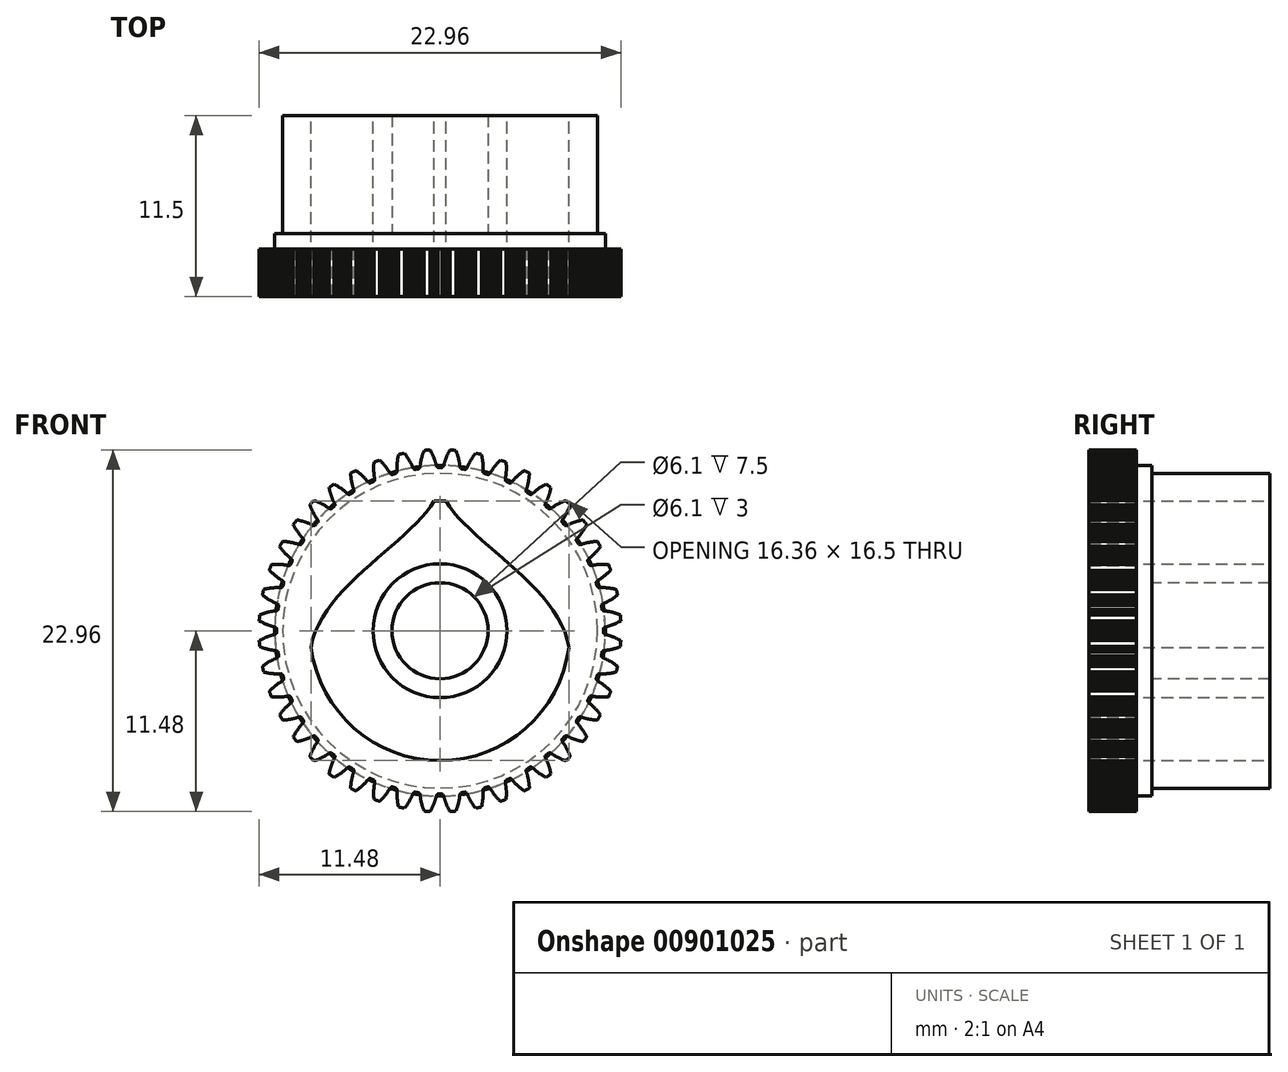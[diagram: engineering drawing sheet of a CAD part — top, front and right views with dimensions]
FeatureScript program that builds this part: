
annotation { "Feature Type Name" : "Feature", "Feature Type Description" : "" }
export const myFeature = defineFeature(function(context is Context, id is Id, definition is map)
    precondition{}
    {
        {
            var Q0;
            Q0=qCreatedBy(makeId("Front.planeOp"),FACE);
            var sketch = newSketch(context, id + "F0", { "sketchPlane" : qUnion([Q0])});
            skLineSegment(sketch, "E0", {"start": v(10.38, 0) * mm, "end": v(10.37, 0.02) * mm});
            skLineSegment(sketch, "E1", {"start": v(10.37, 0.02) * mm, "end": v(10.37, 0.05) * mm});
            skLineSegment(sketch, "E2", {"start": v(10.37, 0.05) * mm, "end": v(10.37, 0.07) * mm});
            skLineSegment(sketch, "E3", {"start": v(10.37, 0.07) * mm, "end": v(10.37, 0.1) * mm});
            skLineSegment(sketch, "E4", {"start": v(10.37, 0.1) * mm, "end": v(10.37, 0.12) * mm});
            skLineSegment(sketch, "E5", {"start": v(10.37, 0.12) * mm, "end": v(10.37, 0.12) * mm});
            skLineSegment(sketch, "E6", {"start": v(10.37, 0.12) * mm, "end": v(10.38, 0.13) * mm});
            skLineSegment(sketch, "E7", {"start": v(10.38, 0.13) * mm, "end": v(10.38, 0.14) * mm});
            skLineSegment(sketch, "E8", {"start": v(10.38, 0.14) * mm, "end": v(10.38, 0.15) * mm});
            skLineSegment(sketch, "E9", {"start": v(10.38, 0.15) * mm, "end": v(10.39, 0.16) * mm});
            skLineSegment(sketch, "E10", {"start": v(10.39, 0.16) * mm, "end": v(10.4, 0.16) * mm});
            skLineSegment(sketch, "E11", {"start": v(10.4, 0.16) * mm, "end": v(10.4, 0.17) * mm});
            skLineSegment(sketch, "E12", {"start": v(10.4, 0.17) * mm, "end": v(10.4, 0.18) * mm});
            skLineSegment(sketch, "E13", {"start": v(10.4, 0.18) * mm, "end": v(10.41, 0.19) * mm});
            skLineSegment(sketch, "E14", {"start": v(10.41, 0.19) * mm, "end": v(10.42, 0.2) * mm});
            skLineSegment(sketch, "E15", {"start": v(10.42, 0.2) * mm, "end": v(10.43, 0.2) * mm});
            skLineSegment(sketch, "E16", {"start": v(10.43, 0.2) * mm, "end": v(10.44, 0.2) * mm});
            skLineSegment(sketch, "E17", {"start": v(10.44, 0.2) * mm, "end": v(10.46, 0.21) * mm});
            skLineSegment(sketch, "E18", {"start": v(10.46, 0.21) * mm, "end": v(10.47, 0.22) * mm});
            skLineSegment(sketch, "E19", {"start": v(10.47, 0.22) * mm, "end": v(10.48, 0.23) * mm});
            skLineSegment(sketch, "E20", {"start": v(10.48, 0.23) * mm, "end": v(10.5, 0.23) * mm});
            skLineSegment(sketch, "E21", {"start": v(10.5, 0.23) * mm, "end": v(10.51, 0.24) * mm});
            skLineSegment(sketch, "E22", {"start": v(10.51, 0.24) * mm, "end": v(10.53, 0.24) * mm});
            skLineSegment(sketch, "E23", {"start": v(10.53, 0.24) * mm, "end": v(10.55, 0.25) * mm});
            skLineSegment(sketch, "E24", {"start": v(10.55, 0.25) * mm, "end": v(10.57, 0.25) * mm});
            skLineSegment(sketch, "E25", {"start": v(10.57, 0.25) * mm, "end": v(10.61, 0.26) * mm});
            skLineSegment(sketch, "E26", {"start": v(10.61, 0.26) * mm, "end": v(10.66, 0.28) * mm});
            skLineSegment(sketch, "E27", {"start": v(10.66, 0.28) * mm, "end": v(10.7, 0.3) * mm});
            skLineSegment(sketch, "E28", {"start": v(10.7, 0.3) * mm, "end": v(10.75, 0.3) * mm});
            skLineSegment(sketch, "E29", {"start": v(10.75, 0.3) * mm, "end": v(10.8, 0.32) * mm});
            skLineSegment(sketch, "E30", {"start": v(10.8, 0.32) * mm, "end": v(10.84, 0.34) * mm});
            skLineSegment(sketch, "E31", {"start": v(10.84, 0.34) * mm, "end": v(10.89, 0.35) * mm});
            skLineSegment(sketch, "E32", {"start": v(10.89, 0.35) * mm, "end": v(10.94, 0.37) * mm});
            skLineSegment(sketch, "E33", {"start": v(10.94, 0.37) * mm, "end": v(10.98, 0.39) * mm});
            skLineSegment(sketch, "E34", {"start": v(10.98, 0.39) * mm, "end": v(11.03, 0.4) * mm});
            skLineSegment(sketch, "E35", {"start": v(11.03, 0.4) * mm, "end": v(11.07, 0.43) * mm});
            skLineSegment(sketch, "E36", {"start": v(11.07, 0.43) * mm, "end": v(11.12, 0.45) * mm});
            skLineSegment(sketch, "E37", {"start": v(11.12, 0.45) * mm, "end": v(11.16, 0.47) * mm});
            skLineSegment(sketch, "E38", {"start": v(11.16, 0.47) * mm, "end": v(11.21, 0.49) * mm});
            skLineSegment(sketch, "E39", {"start": v(11.21, 0.49) * mm, "end": v(11.26, 0.51) * mm});
            skLineSegment(sketch, "E40", {"start": v(11.26, 0.51) * mm, "end": v(11.3, 0.53) * mm});
            skLineSegment(sketch, "E41", {"start": v(11.3, 0.53) * mm, "end": v(11.35, 0.56) * mm});
            skLineSegment(sketch, "E42", {"start": v(11.35, 0.56) * mm, "end": v(11.4, 0.58) * mm});
            skLineSegment(sketch, "E43", {"start": v(11.4, 0.58) * mm, "end": v(11.44, 0.6) * mm});
            skLineSegment(sketch, "E44", {"start": v(11.44, 0.6) * mm, "end": v(11.48, 0.63) * mm});
            skLineSegment(sketch, "E45", {"start": v(11.48, 0.63) * mm, "end": v(11.48, 0.67) * mm});
            skLineSegment(sketch, "E46", {"start": v(11.48, 0.67) * mm, "end": v(11.48, 0.7) * mm});
            skLineSegment(sketch, "E47", {"start": v(11.48, 0.7) * mm, "end": v(11.48, 0.74) * mm});
            skLineSegment(sketch, "E48", {"start": v(11.48, 0.74) * mm, "end": v(11.47, 0.78) * mm});
            skLineSegment(sketch, "E49", {"start": v(11.47, 0.78) * mm, "end": v(11.47, 0.82) * mm});
            skLineSegment(sketch, "E50.MirrorCS", {"start": v(10.37, -0.12) * mm, "end": v(10.37, -0.12) * mm});
            skLineSegment(sketch, "E51.MirrorCS", {"start": v(10.37, -0.12) * mm, "end": v(10.38, -0.13) * mm});
            skLineSegment(sketch, "E52.MirrorCS", {"start": v(10.38, -0.13) * mm, "end": v(10.38, -0.14) * mm});
            skLineSegment(sketch, "E53.MirrorCS", {"start": v(10.38, -0.14) * mm, "end": v(10.38, -0.15) * mm});
            skLineSegment(sketch, "E54.MirrorCS", {"start": v(10.46, -0.21) * mm, "end": v(10.47, -0.22) * mm});
            skLineSegment(sketch, "E55.MirrorCS", {"start": v(10.38, -0.15) * mm, "end": v(10.39, -0.16) * mm});
            skLineSegment(sketch, "E56.MirrorCS", {"start": v(10.44, -0.2) * mm, "end": v(10.46, -0.21) * mm});
            skLineSegment(sketch, "E57.MirrorCS", {"start": v(10.57, -0.25) * mm, "end": v(10.61, -0.26) * mm});
            skLineSegment(sketch, "E58.MirrorCS", {"start": v(10.39, -0.16) * mm, "end": v(10.4, -0.16) * mm});
            skLineSegment(sketch, "E59.MirrorCS", {"start": v(10.55, -0.25) * mm, "end": v(10.57, -0.25) * mm});
            skLineSegment(sketch, "E60.MirrorCS", {"start": v(10.43, -0.2) * mm, "end": v(10.44, -0.2) * mm});
            skLineSegment(sketch, "E61.MirrorCS", {"start": v(10.4, -0.16) * mm, "end": v(10.4, -0.17) * mm});
            skLineSegment(sketch, "E62.MirrorCS", {"start": v(10.53, -0.24) * mm, "end": v(10.55, -0.25) * mm});
            skLineSegment(sketch, "E63.MirrorCS", {"start": v(11.07, -0.43) * mm, "end": v(11.12, -0.45) * mm});
            skLineSegment(sketch, "E64.MirrorCS", {"start": v(10.51, -0.24) * mm, "end": v(10.53, -0.24) * mm});
            skLineSegment(sketch, "E65.MirrorCS", {"start": v(10.4, -0.17) * mm, "end": v(10.4, -0.18) * mm});
            skLineSegment(sketch, "E66.MirrorCS", {"start": v(10.7, -0.3) * mm, "end": v(10.75, -0.3) * mm});
            skLineSegment(sketch, "E67.MirrorCS", {"start": v(10.37, -0.02) * mm, "end": v(10.37, -0.05) * mm});
            skLineSegment(sketch, "E68.MirrorCS", {"start": v(10.37, -0.05) * mm, "end": v(10.37, -0.07) * mm});
            skLineSegment(sketch, "E69.MirrorCS", {"start": v(10.42, -0.2) * mm, "end": v(10.43, -0.2) * mm});
            skLineSegment(sketch, "E70.MirrorCS", {"start": v(11.03, -0.4) * mm, "end": v(11.07, -0.43) * mm});
            skLineSegment(sketch, "E71.MirrorCS", {"start": v(10.5, -0.23) * mm, "end": v(10.51, -0.24) * mm});
            skLineSegment(sketch, "E72.MirrorCS", {"start": v(10.66, -0.28) * mm, "end": v(10.7, -0.3) * mm});
            skLineSegment(sketch, "E73.MirrorCS", {"start": v(10.4, -0.18) * mm, "end": v(10.41, -0.19) * mm});
            skLineSegment(sketch, "E74.MirrorCS", {"start": v(10.98, -0.39) * mm, "end": v(11.03, -0.4) * mm});
            skLineSegment(sketch, "E75.MirrorCS", {"start": v(10.8, -0.32) * mm, "end": v(10.84, -0.34) * mm});
            skLineSegment(sketch, "E76.MirrorCS", {"start": v(10.84, -0.34) * mm, "end": v(10.89, -0.35) * mm});
            skLineSegment(sketch, "E77.MirrorCS", {"start": v(10.48, -0.23) * mm, "end": v(10.5, -0.23) * mm});
            skLineSegment(sketch, "E78.MirrorCS", {"start": v(10.37, -0.07) * mm, "end": v(10.37, -0.1) * mm});
            skLineSegment(sketch, "E79.MirrorCS", {"start": v(10.47, -0.22) * mm, "end": v(10.48, -0.23) * mm});
            skLineSegment(sketch, "E80.MirrorCS", {"start": v(10.89, -0.35) * mm, "end": v(10.94, -0.37) * mm});
            skLineSegment(sketch, "E81.MirrorCS", {"start": v(10.38, 0) * mm, "end": v(10.37, -0.02) * mm});
            skLineSegment(sketch, "E82.MirrorCS", {"start": v(10.75, -0.3) * mm, "end": v(10.8, -0.32) * mm});
            skLineSegment(sketch, "E83.MirrorCS", {"start": v(10.61, -0.26) * mm, "end": v(10.66, -0.28) * mm});
            skLineSegment(sketch, "E84.MirrorCS", {"start": v(10.41, -0.19) * mm, "end": v(10.42, -0.2) * mm});
            skLineSegment(sketch, "E85.MirrorCS", {"start": v(10.37, -0.1) * mm, "end": v(10.37, -0.12) * mm});
            skLineSegment(sketch, "E86.MirrorCS", {"start": v(10.94, -0.37) * mm, "end": v(10.98, -0.39) * mm});
            skLineSegment(sketch, "E87.MirrorCS", {"start": v(11.21, -0.49) * mm, "end": v(11.26, -0.51) * mm});
            skLineSegment(sketch, "E88.MirrorCS", {"start": v(11.44, -0.6) * mm, "end": v(11.48, -0.63) * mm});
            skLineSegment(sketch, "E89.MirrorCS", {"start": v(11.16, -0.47) * mm, "end": v(11.21, -0.49) * mm});
            skLineSegment(sketch, "E90.MirrorCS", {"start": v(11.26, -0.51) * mm, "end": v(11.3, -0.53) * mm});
            skLineSegment(sketch, "E91.MirrorCS", {"start": v(11.4, -0.58) * mm, "end": v(11.44, -0.6) * mm});
            skLineSegment(sketch, "E92.MirrorCS", {"start": v(11.12, -0.45) * mm, "end": v(11.16, -0.47) * mm});
            skLineSegment(sketch, "E93.MirrorCS", {"start": v(11.3, -0.53) * mm, "end": v(11.35, -0.56) * mm});
            skLineSegment(sketch, "E94.MirrorCS", {"start": v(11.48, -0.67) * mm, "end": v(11.48, -0.7) * mm});
            skLineSegment(sketch, "E95.MirrorCS", {"start": v(11.48, -0.7) * mm, "end": v(11.48, -0.74) * mm});
            skLineSegment(sketch, "E96.MirrorCS", {"start": v(11.47, -0.78) * mm, "end": v(11.47, -0.82) * mm});
            skLineSegment(sketch, "E97.MirrorCS", {"start": v(11.48, -0.74) * mm, "end": v(11.47, -0.78) * mm});
            skLineSegment(sketch, "E98.MirrorCS", {"start": v(11.35, -0.56) * mm, "end": v(11.4, -0.58) * mm});
            skLineSegment(sketch, "E99.MirrorCS", {"start": v(11.48, -0.63) * mm, "end": v(11.48, -0.67) * mm});
            skLineSegment(sketch, "E100.1.0", {"start": v(11.46, 0.97) * mm, "end": v(11.46, 0.94) * mm});
            skLineSegment(sketch, "E100.1.1", {"start": v(11.26, 2.33) * mm, "end": v(11.25, 2.37) * mm});
            skLineSegment(sketch, "E100.1.2", {"start": v(11.15, 2.17) * mm, "end": v(11.2, 2.2) * mm});
            skLineSegment(sketch, "E100.1.3", {"start": v(11.25, 2.4) * mm, "end": v(11.24, 2.44) * mm});
            skLineSegment(sketch, "E100.1.4", {"start": v(11.02, 1.15) * mm, "end": v(11.07, 1.14) * mm});
            skLineSegment(sketch, "E100.1.5", {"start": v(11.46, 0.9) * mm, "end": v(11.47, 0.86) * mm});
            skLineSegment(sketch, "E100.1.6", {"start": v(11.27, 2.3) * mm, "end": v(11.26, 2.33) * mm});
            skLineSegment(sketch, "E100.1.7", {"start": v(11.26, 1.08) * mm, "end": v(11.31, 1.06) * mm});
            skLineSegment(sketch, "E100.1.8", {"start": v(11.25, 2.37) * mm, "end": v(11.25, 2.4) * mm});
            skLineSegment(sketch, "E100.1.9", {"start": v(11.31, 1.06) * mm, "end": v(11.36, 1.05) * mm});
            skLineSegment(sketch, "E100.1.10", {"start": v(11.47, 0.86) * mm, "end": v(11.47, 0.82) * mm});
            skLineSegment(sketch, "E100.1.11", {"start": v(11.36, 1.05) * mm, "end": v(11.4, 1.03) * mm});
            skLineSegment(sketch, "E100.1.12", {"start": v(11.21, 1.1) * mm, "end": v(11.26, 1.08) * mm});
            skLineSegment(sketch, "E100.1.13", {"start": v(11.24, 2.23) * mm, "end": v(11.28, 2.26) * mm});
            skLineSegment(sketch, "E100.1.14", {"start": v(11.46, 1.01) * mm, "end": v(11.46, 0.97) * mm});
            skLineSegment(sketch, "E100.1.15", {"start": v(11.07, 1.14) * mm, "end": v(11.12, 1.13) * mm});
            skLineSegment(sketch, "E100.1.16", {"start": v(11.46, 0.94) * mm, "end": v(11.46, 0.9) * mm});
            skLineSegment(sketch, "E100.1.17", {"start": v(11.28, 2.26) * mm, "end": v(11.27, 2.3) * mm});
            skLineSegment(sketch, "E100.1.18", {"start": v(11.07, 2.1) * mm, "end": v(11.11, 2.14) * mm});
            skLineSegment(sketch, "E100.1.19", {"start": v(11.17, 1.11) * mm, "end": v(11.21, 1.1) * mm});
            skLineSegment(sketch, "E100.1.20", {"start": v(11.4, 1.03) * mm, "end": v(11.46, 1.01) * mm});
            skLineSegment(sketch, "E100.1.21", {"start": v(10.94, 2.02) * mm, "end": v(10.98, 2.05) * mm});
            skLineSegment(sketch, "E100.1.22", {"start": v(11.11, 2.14) * mm, "end": v(11.15, 2.17) * mm});
            skLineSegment(sketch, "E100.1.23", {"start": v(11.12, 1.13) * mm, "end": v(11.17, 1.11) * mm});
            skLineSegment(sketch, "E100.1.24", {"start": v(10.98, 2.05) * mm, "end": v(11.03, 2.08) * mm});
            skLineSegment(sketch, "E100.1.25", {"start": v(11.03, 2.08) * mm, "end": v(11.07, 2.1) * mm});
            skLineSegment(sketch, "E100.1.26", {"start": v(11.2, 2.2) * mm, "end": v(11.24, 2.23) * mm});
            skLineSegment(sketch, "E100.1.27", {"start": v(10.9, 2) * mm, "end": v(10.94, 2.02) * mm});
            skLineSegment(sketch, "E100.1.28", {"start": v(10.3, 1.7) * mm, "end": v(10.32, 1.7) * mm});
            skLineSegment(sketch, "E100.1.29", {"start": v(10.55, 1.81) * mm, "end": v(10.6, 1.83) * mm});
            skLineSegment(sketch, "E100.1.30", {"start": v(10.69, 1.88) * mm, "end": v(10.73, 1.9) * mm});
            skLineSegment(sketch, "E100.1.31", {"start": v(10.4, 1.27) * mm, "end": v(10.4, 1.27) * mm});
            skLineSegment(sketch, "E100.1.32", {"start": v(10.97, 1.17) * mm, "end": v(11.02, 1.15) * mm});
            skLineSegment(sketch, "E100.1.33", {"start": v(10.27, 1.65) * mm, "end": v(10.27, 1.66) * mm});
            skLineSegment(sketch, "E100.1.34", {"start": v(10.32, 1.31) * mm, "end": v(10.32, 1.3) * mm});
            skLineSegment(sketch, "E100.1.35", {"start": v(10.33, 1.7) * mm, "end": v(10.34, 1.72) * mm});
            skLineSegment(sketch, "E100.1.36", {"start": v(10.42, 1.75) * mm, "end": v(10.47, 1.77) * mm});
            skLineSegment(sketch, "E100.1.37", {"start": v(10.88, 1.2) * mm, "end": v(10.92, 1.18) * mm});
            skLineSegment(sketch, "E100.1.38", {"start": v(10.59, 1.24) * mm, "end": v(10.64, 1.24) * mm});
            skLineSegment(sketch, "E100.1.39", {"start": v(10.73, 1.22) * mm, "end": v(10.78, 1.21) * mm});
            skLineSegment(sketch, "E100.1.40", {"start": v(10.27, 1.48) * mm, "end": v(10.27, 1.45) * mm});
            skLineSegment(sketch, "E100.1.41", {"start": v(10.27, 1.45) * mm, "end": v(10.28, 1.43) * mm});
            skLineSegment(sketch, "E100.1.42", {"start": v(10.77, 1.92) * mm, "end": v(10.81, 1.95) * mm});
            skLineSegment(sketch, "E100.1.43", {"start": v(10.73, 1.9) * mm, "end": v(10.77, 1.92) * mm});
            skLineSegment(sketch, "E100.1.44", {"start": v(10.92, 1.18) * mm, "end": v(10.97, 1.17) * mm});
            skLineSegment(sketch, "E100.1.45", {"start": v(10.34, 1.3) * mm, "end": v(10.35, 1.29) * mm});
            skLineSegment(sketch, "E100.1.46", {"start": v(10.29, 1.35) * mm, "end": v(10.29, 1.35) * mm});
            skLineSegment(sketch, "E100.1.47", {"start": v(10.78, 1.21) * mm, "end": v(10.83, 1.2) * mm});
            skLineSegment(sketch, "E100.1.48", {"start": v(10.86, 1.97) * mm, "end": v(10.9, 2) * mm});
            skLineSegment(sketch, "E100.1.49", {"start": v(10.36, 1.72) * mm, "end": v(10.37, 1.73) * mm});
            skLineSegment(sketch, "E100.1.50", {"start": v(10.83, 1.2) * mm, "end": v(10.88, 1.2) * mm});
            skLineSegment(sketch, "E100.1.51", {"start": v(10.54, 1.25) * mm, "end": v(10.59, 1.24) * mm});
            skLineSegment(sketch, "E100.1.52", {"start": v(10.26, 1.64) * mm, "end": v(10.27, 1.65) * mm});
            skLineSegment(sketch, "E100.1.53", {"start": v(10.64, 1.85) * mm, "end": v(10.69, 1.88) * mm});
            skLineSegment(sketch, "E100.1.54", {"start": v(10.42, 1.26) * mm, "end": v(10.44, 1.26) * mm});
            skLineSegment(sketch, "E100.1.55", {"start": v(10.28, 1.38) * mm, "end": v(10.29, 1.36) * mm});
            skLineSegment(sketch, "E100.1.56", {"start": v(10.38, 1.28) * mm, "end": v(10.4, 1.27) * mm});
            skLineSegment(sketch, "E100.1.57", {"start": v(10.26, 1.63) * mm, "end": v(10.26, 1.64) * mm});
            skLineSegment(sketch, "E100.1.58", {"start": v(10.46, 1.26) * mm, "end": v(10.48, 1.26) * mm});
            skLineSegment(sketch, "E100.1.59", {"start": v(10.37, 1.73) * mm, "end": v(10.39, 1.74) * mm});
            skLineSegment(sketch, "E100.1.60", {"start": v(10.64, 1.24) * mm, "end": v(10.69, 1.23) * mm});
            skLineSegment(sketch, "E100.1.61", {"start": v(10.81, 1.95) * mm, "end": v(10.86, 1.97) * mm});
            skLineSegment(sketch, "E100.1.62", {"start": v(10.6, 1.83) * mm, "end": v(10.64, 1.85) * mm});
            skLineSegment(sketch, "E100.1.63", {"start": v(10.4, 1.75) * mm, "end": v(10.42, 1.75) * mm});
            skLineSegment(sketch, "E100.1.64", {"start": v(10.26, 1.62) * mm, "end": v(10.26, 1.63) * mm});
            skLineSegment(sketch, "E100.1.65", {"start": v(10.28, 1.4) * mm, "end": v(10.28, 1.38) * mm});
            skLineSegment(sketch, "E100.1.66", {"start": v(10.44, 1.26) * mm, "end": v(10.46, 1.26) * mm});
            skLineSegment(sketch, "E100.1.67", {"start": v(10.69, 1.23) * mm, "end": v(10.73, 1.22) * mm});
            skLineSegment(sketch, "E100.1.68", {"start": v(10.37, 1.28) * mm, "end": v(10.38, 1.28) * mm});
            skLineSegment(sketch, "E100.1.69", {"start": v(10.51, 1.8) * mm, "end": v(10.55, 1.81) * mm});
            skLineSegment(sketch, "E100.1.70", {"start": v(10.3, 1.34) * mm, "end": v(10.3, 1.33) * mm});
            skLineSegment(sketch, "E100.1.71", {"start": v(10.4, 1.27) * mm, "end": v(10.42, 1.26) * mm});
            skLineSegment(sketch, "E100.1.72", {"start": v(10.3, 1.32) * mm, "end": v(10.3, 1.32) * mm});
            skLineSegment(sketch, "E100.1.73", {"start": v(10.47, 1.77) * mm, "end": v(10.51, 1.8) * mm});
            skLineSegment(sketch, "E100.1.74", {"start": v(10.25, 1.62) * mm, "end": v(10.26, 1.62) * mm});
            skLineSegment(sketch, "E100.1.75", {"start": v(10.25, 1.6) * mm, "end": v(10.25, 1.62) * mm});
            skLineSegment(sketch, "E100.1.76", {"start": v(10.26, 1.52) * mm, "end": v(10.26, 1.55) * mm});
            skLineSegment(sketch, "E100.1.77", {"start": v(10.35, 1.29) * mm, "end": v(10.37, 1.28) * mm});
            skLineSegment(sketch, "E100.1.78", {"start": v(10.32, 1.7) * mm, "end": v(10.33, 1.7) * mm});
            skLineSegment(sketch, "E100.1.79", {"start": v(10.5, 1.25) * mm, "end": v(10.54, 1.25) * mm});
            skLineSegment(sketch, "E100.1.80", {"start": v(10.3, 1.32) * mm, "end": v(10.32, 1.31) * mm});
            skLineSegment(sketch, "E100.1.81", {"start": v(10.25, 1.6) * mm, "end": v(10.25, 1.6) * mm});
            skLineSegment(sketch, "E100.1.82", {"start": v(10.48, 1.26) * mm, "end": v(10.5, 1.25) * mm});
            skLineSegment(sketch, "E100.1.83", {"start": v(10.27, 1.5) * mm, "end": v(10.26, 1.52) * mm});
            skLineSegment(sketch, "E100.1.84", {"start": v(10.34, 1.72) * mm, "end": v(10.36, 1.72) * mm});
            skLineSegment(sketch, "E100.1.85", {"start": v(10.33, 1.3) * mm, "end": v(10.34, 1.3) * mm});
            skLineSegment(sketch, "E100.1.86", {"start": v(10.27, 1.48) * mm, "end": v(10.27, 1.5) * mm});
            skLineSegment(sketch, "E100.1.87", {"start": v(10.39, 1.74) * mm, "end": v(10.4, 1.75) * mm});
            skLineSegment(sketch, "E100.1.88", {"start": v(10.25, 1.6) * mm, "end": v(10.25, 1.6) * mm});
            skLineSegment(sketch, "E100.1.89", {"start": v(10.26, 1.57) * mm, "end": v(10.25, 1.6) * mm});
            skLineSegment(sketch, "E100.1.90", {"start": v(10.29, 1.36) * mm, "end": v(10.29, 1.35) * mm});
            skLineSegment(sketch, "E100.1.91", {"start": v(10.3, 1.33) * mm, "end": v(10.3, 1.32) * mm});
            skLineSegment(sketch, "E100.1.92", {"start": v(10.32, 1.3) * mm, "end": v(10.33, 1.3) * mm});
            skLineSegment(sketch, "E100.1.93", {"start": v(10.28, 1.43) * mm, "end": v(10.28, 1.4) * mm});
            skLineSegment(sketch, "E100.1.94", {"start": v(10.26, 1.55) * mm, "end": v(10.26, 1.57) * mm});
            skLineSegment(sketch, "E100.1.95", {"start": v(10.28, 1.67) * mm, "end": v(10.29, 1.67) * mm});
            skLineSegment(sketch, "E100.1.96", {"start": v(10.29, 1.35) * mm, "end": v(10.3, 1.34) * mm});
            skLineSegment(sketch, "E100.1.97", {"start": v(10.27, 1.66) * mm, "end": v(10.28, 1.67) * mm});
            skLineSegment(sketch, "E100.1.98", {"start": v(10.29, 1.67) * mm, "end": v(10.3, 1.68) * mm});
            skLineSegment(sketch, "E100.1.99", {"start": v(10.3, 1.68) * mm, "end": v(10.3, 1.7) * mm});
            skLineSegment(sketch, "E100.2.0", {"start": v(11.2, 2.6) * mm, "end": v(11.21, 2.56) * mm});
            skLineSegment(sketch, "E100.2.1", {"start": v(10.81, 3.91) * mm, "end": v(10.8, 3.95) * mm});
            skLineSegment(sketch, "E100.2.2", {"start": v(10.73, 3.73) * mm, "end": v(10.77, 3.77) * mm});
            skLineSegment(sketch, "E100.2.3", {"start": v(10.79, 3.98) * mm, "end": v(10.77, 4.02) * mm});
            skLineSegment(sketch, "E100.2.4", {"start": v(10.74, 2.71) * mm, "end": v(10.8, 2.7) * mm});
            skLineSegment(sketch, "E100.2.5", {"start": v(11.22, 2.52) * mm, "end": v(11.23, 2.48) * mm});
            skLineSegment(sketch, "E100.2.6", {"start": v(10.83, 3.87) * mm, "end": v(10.81, 3.91) * mm});
            skLineSegment(sketch, "E100.2.7", {"start": v(11, 2.67) * mm, "end": v(11.04, 2.66) * mm});
            skLineSegment(sketch, "E100.2.8", {"start": v(10.8, 3.95) * mm, "end": v(10.79, 3.98) * mm});
            skLineSegment(sketch, "E100.2.9", {"start": v(11.04, 2.66) * mm, "end": v(11.1, 2.65) * mm});
            skLineSegment(sketch, "E100.2.10", {"start": v(11.23, 2.48) * mm, "end": v(11.24, 2.44) * mm});
            skLineSegment(sketch, "E100.2.11", {"start": v(11.1, 2.65) * mm, "end": v(11.14, 2.64) * mm});
            skLineSegment(sketch, "E100.2.12", {"start": v(10.94, 2.68) * mm, "end": v(11, 2.67) * mm});
            skLineSegment(sketch, "E100.2.13", {"start": v(10.8, 3.8) * mm, "end": v(10.84, 3.84) * mm});
            skLineSegment(sketch, "E100.2.14", {"start": v(11.2, 2.63) * mm, "end": v(11.2, 2.6) * mm});
            skLineSegment(sketch, "E100.2.15", {"start": v(10.8, 2.7) * mm, "end": v(10.84, 2.7) * mm});
            skLineSegment(sketch, "E100.2.16", {"start": v(11.21, 2.56) * mm, "end": v(11.22, 2.52) * mm});
            skLineSegment(sketch, "E100.2.17", {"start": v(10.84, 3.84) * mm, "end": v(10.83, 3.87) * mm});
            skLineSegment(sketch, "E100.2.18", {"start": v(10.66, 3.66) * mm, "end": v(10.7, 3.7) * mm});
            skLineSegment(sketch, "E100.2.19", {"start": v(10.9, 2.69) * mm, "end": v(10.94, 2.68) * mm});
            skLineSegment(sketch, "E100.2.20", {"start": v(11.14, 2.64) * mm, "end": v(11.2, 2.63) * mm});
            skLineSegment(sketch, "E100.2.21", {"start": v(10.54, 3.56) * mm, "end": v(10.58, 3.6) * mm});
            skLineSegment(sketch, "E100.2.22", {"start": v(10.7, 3.7) * mm, "end": v(10.73, 3.73) * mm});
            skLineSegment(sketch, "E100.2.23", {"start": v(10.84, 2.7) * mm, "end": v(10.9, 2.69) * mm});
            skLineSegment(sketch, "E100.2.24", {"start": v(10.58, 3.6) * mm, "end": v(10.62, 3.63) * mm});
            skLineSegment(sketch, "E100.2.25", {"start": v(10.62, 3.63) * mm, "end": v(10.66, 3.66) * mm});
            skLineSegment(sketch, "E100.2.26", {"start": v(10.77, 3.77) * mm, "end": v(10.8, 3.8) * mm});
            skLineSegment(sketch, "E100.2.27", {"start": v(10.5, 3.53) * mm, "end": v(10.54, 3.56) * mm});
            skLineSegment(sketch, "E100.2.28", {"start": v(9.96, 3.14) * mm, "end": v(9.97, 3.15) * mm});
            skLineSegment(sketch, "E100.2.29", {"start": v(10.19, 3.3) * mm, "end": v(10.23, 3.32) * mm});
            skLineSegment(sketch, "E100.2.30", {"start": v(10.3, 3.38) * mm, "end": v(10.35, 3.4) * mm});
            skLineSegment(sketch, "E100.2.31", {"start": v(10.1, 2.74) * mm, "end": v(10.12, 2.74) * mm});
            skLineSegment(sketch, "E100.2.32", {"start": v(10.7, 2.72) * mm, "end": v(10.74, 2.71) * mm});
            skLineSegment(sketch, "E100.2.33", {"start": v(9.93, 3.1) * mm, "end": v(9.93, 3.1) * mm});
            skLineSegment(sketch, "E100.2.34", {"start": v(10.02, 2.76) * mm, "end": v(10.03, 2.76) * mm});
            skLineSegment(sketch, "E100.2.35", {"start": v(9.98, 3.16) * mm, "end": v(10, 3.17) * mm});
            skLineSegment(sketch, "E100.2.36", {"start": v(10.07, 3.22) * mm, "end": v(10.1, 3.24) * mm});
            skLineSegment(sketch, "E100.2.37", {"start": v(10.6, 2.73) * mm, "end": v(10.65, 2.72) * mm});
            skLineSegment(sketch, "E100.2.38", {"start": v(10.3, 2.74) * mm, "end": v(10.35, 2.74) * mm});
            skLineSegment(sketch, "E100.2.39", {"start": v(10.45, 2.73) * mm, "end": v(10.5, 2.73) * mm});
            skLineSegment(sketch, "E100.2.40", {"start": v(9.95, 2.92) * mm, "end": v(9.96, 2.9) * mm});
            skLineSegment(sketch, "E100.2.41", {"start": v(9.96, 2.9) * mm, "end": v(9.97, 2.88) * mm});
            skLineSegment(sketch, "E100.2.42", {"start": v(10.39, 3.44) * mm, "end": v(10.43, 3.47) * mm});
            skLineSegment(sketch, "E100.2.43", {"start": v(10.35, 3.4) * mm, "end": v(10.39, 3.44) * mm});
            skLineSegment(sketch, "E100.2.44", {"start": v(10.65, 2.72) * mm, "end": v(10.7, 2.72) * mm});
            skLineSegment(sketch, "E100.2.45", {"start": v(10.05, 2.75) * mm, "end": v(10.07, 2.75) * mm});
            skLineSegment(sketch, "E100.2.46", {"start": v(9.99, 2.8) * mm, "end": v(10, 2.8) * mm});
            skLineSegment(sketch, "E100.2.47", {"start": v(10.5, 2.73) * mm, "end": v(10.55, 2.73) * mm});
            skLineSegment(sketch, "E100.2.48", {"start": v(10.47, 3.5) * mm, "end": v(10.5, 3.53) * mm});
            skLineSegment(sketch, "E100.2.49", {"start": v(10, 3.18) * mm, "end": v(10.02, 3.2) * mm});
            skLineSegment(sketch, "E100.2.50", {"start": v(10.55, 2.73) * mm, "end": v(10.6, 2.73) * mm});
            skLineSegment(sketch, "E100.2.51", {"start": v(10.26, 2.74) * mm, "end": v(10.3, 2.74) * mm});
            skLineSegment(sketch, "E100.2.52", {"start": v(9.92, 3.08) * mm, "end": v(9.93, 3.1) * mm});
            skLineSegment(sketch, "E100.2.53", {"start": v(10.27, 3.35) * mm, "end": v(10.3, 3.38) * mm});
            skLineSegment(sketch, "E100.2.54", {"start": v(10.14, 2.73) * mm, "end": v(10.15, 2.73) * mm});
            skLineSegment(sketch, "E100.2.55", {"start": v(9.98, 2.83) * mm, "end": v(9.99, 2.81) * mm});
            skLineSegment(sketch, "E100.2.56", {"start": v(10.1, 2.74) * mm, "end": v(10.1, 2.74) * mm});
            skLineSegment(sketch, "E100.2.57", {"start": v(9.92, 3.08) * mm, "end": v(9.92, 3.08) * mm});
            skLineSegment(sketch, "E100.2.58", {"start": v(10.17, 2.73) * mm, "end": v(10.2, 2.73) * mm});
            skLineSegment(sketch, "E100.2.59", {"start": v(10.02, 3.2) * mm, "end": v(10.03, 3.2) * mm});
            skLineSegment(sketch, "E100.2.60", {"start": v(10.35, 2.74) * mm, "end": v(10.4, 2.74) * mm});
            skLineSegment(sketch, "E100.2.61", {"start": v(10.43, 3.47) * mm, "end": v(10.47, 3.5) * mm});
            skLineSegment(sketch, "E100.2.62", {"start": v(10.23, 3.32) * mm, "end": v(10.27, 3.35) * mm});
            skLineSegment(sketch, "E100.2.63", {"start": v(10.05, 3.2) * mm, "end": v(10.07, 3.22) * mm});
            skLineSegment(sketch, "E100.2.64", {"start": v(9.92, 3.07) * mm, "end": v(9.92, 3.08) * mm});
            skLineSegment(sketch, "E100.2.65", {"start": v(9.97, 2.86) * mm, "end": v(9.98, 2.83) * mm});
            skLineSegment(sketch, "E100.2.66", {"start": v(10.15, 2.73) * mm, "end": v(10.17, 2.73) * mm});
            skLineSegment(sketch, "E100.2.67", {"start": v(10.4, 2.74) * mm, "end": v(10.45, 2.73) * mm});
            skLineSegment(sketch, "E100.2.68", {"start": v(10.08, 2.74) * mm, "end": v(10.1, 2.74) * mm});
            skLineSegment(sketch, "E100.2.69", {"start": v(10.15, 3.27) * mm, "end": v(10.19, 3.3) * mm});
            skLineSegment(sketch, "E100.2.70", {"start": v(10, 2.79) * mm, "end": v(10, 2.78) * mm});
            skLineSegment(sketch, "E100.2.71", {"start": v(10.12, 2.74) * mm, "end": v(10.14, 2.73) * mm});
            skLineSegment(sketch, "E100.2.72", {"start": v(10, 2.78) * mm, "end": v(10.02, 2.77) * mm});
            skLineSegment(sketch, "E100.2.73", {"start": v(10.1, 3.24) * mm, "end": v(10.15, 3.27) * mm});
            skLineSegment(sketch, "E100.2.74", {"start": v(9.92, 3.06) * mm, "end": v(9.92, 3.07) * mm});
            skLineSegment(sketch, "E100.2.75", {"start": v(9.92, 3.05) * mm, "end": v(9.92, 3.06) * mm});
            skLineSegment(sketch, "E100.2.76", {"start": v(9.94, 2.97) * mm, "end": v(9.93, 3) * mm});
            skLineSegment(sketch, "E100.2.77", {"start": v(10.07, 2.75) * mm, "end": v(10.08, 2.74) * mm});
            skLineSegment(sketch, "E100.2.78", {"start": v(9.97, 3.15) * mm, "end": v(9.98, 3.16) * mm});
            skLineSegment(sketch, "E100.2.79", {"start": v(10.2, 2.73) * mm, "end": v(10.26, 2.74) * mm});
            skLineSegment(sketch, "E100.2.80", {"start": v(10.02, 2.77) * mm, "end": v(10.02, 2.76) * mm});
            skLineSegment(sketch, "E100.2.81", {"start": v(9.92, 3.04) * mm, "end": v(9.92, 3.05) * mm});
            skLineSegment(sketch, "E100.2.82", {"start": v(10.2, 2.73) * mm, "end": v(10.2, 2.73) * mm});
            skLineSegment(sketch, "E100.2.83", {"start": v(9.95, 2.95) * mm, "end": v(9.94, 2.97) * mm});
            skLineSegment(sketch, "E100.2.84", {"start": v(10, 3.17) * mm, "end": v(10, 3.18) * mm});
            skLineSegment(sketch, "E100.2.85", {"start": v(10.04, 2.76) * mm, "end": v(10.05, 2.75) * mm});
            skLineSegment(sketch, "E100.2.86", {"start": v(9.95, 2.92) * mm, "end": v(9.95, 2.95) * mm});
            skLineSegment(sketch, "E100.2.87", {"start": v(10.03, 3.2) * mm, "end": v(10.05, 3.2) * mm});
            skLineSegment(sketch, "E100.2.88", {"start": v(9.92, 3.03) * mm, "end": v(9.92, 3.04) * mm});
            skLineSegment(sketch, "E100.2.89", {"start": v(9.93, 3.01) * mm, "end": v(9.92, 3.03) * mm});
            skLineSegment(sketch, "E100.2.90", {"start": v(9.99, 2.81) * mm, "end": v(9.99, 2.8) * mm});
            skLineSegment(sketch, "E100.2.91", {"start": v(10, 2.78) * mm, "end": v(10, 2.78) * mm});
            skLineSegment(sketch, "E100.2.92", {"start": v(10.03, 2.76) * mm, "end": v(10.04, 2.76) * mm});
            skLineSegment(sketch, "E100.2.93", {"start": v(9.97, 2.88) * mm, "end": v(9.97, 2.86) * mm});
            skLineSegment(sketch, "E100.2.94", {"start": v(9.93, 3) * mm, "end": v(9.93, 3.01) * mm});
            skLineSegment(sketch, "E100.2.95", {"start": v(9.94, 3.11) * mm, "end": v(9.95, 3.12) * mm});
            skLineSegment(sketch, "E100.2.96", {"start": v(10, 2.8) * mm, "end": v(10, 2.79) * mm});
            skLineSegment(sketch, "E100.2.97", {"start": v(9.93, 3.1) * mm, "end": v(9.94, 3.11) * mm});
            skLineSegment(sketch, "E100.2.98", {"start": v(9.95, 3.12) * mm, "end": v(9.95, 3.13) * mm});
            skLineSegment(sketch, "E100.2.99", {"start": v(9.95, 3.13) * mm, "end": v(9.96, 3.14) * mm});
            skLineSegment(sketch, "E100.3.0", {"start": v(10.72, 4.16) * mm, "end": v(10.73, 4.13) * mm});
            skLineSegment(sketch, "E100.3.1", {"start": v(10.15, 5.41) * mm, "end": v(10.13, 5.44) * mm});
            skLineSegment(sketch, "E100.3.2", {"start": v(10.1, 5.22) * mm, "end": v(10.12, 5.26) * mm});
            skLineSegment(sketch, "E100.3.3", {"start": v(10.11, 5.48) * mm, "end": v(10.1, 5.51) * mm});
            skLineSegment(sketch, "E100.3.4", {"start": v(10.25, 4.21) * mm, "end": v(10.3, 4.21) * mm});
            skLineSegment(sketch, "E100.3.5", {"start": v(10.75, 4.1) * mm, "end": v(10.76, 4.05) * mm});
            skLineSegment(sketch, "E100.3.6", {"start": v(10.17, 5.38) * mm, "end": v(10.15, 5.41) * mm});
            skLineSegment(sketch, "E100.3.7", {"start": v(10.5, 4.21) * mm, "end": v(10.55, 4.2) * mm});
            skLineSegment(sketch, "E100.3.8", {"start": v(10.13, 5.44) * mm, "end": v(10.11, 5.48) * mm});
            skLineSegment(sketch, "E100.3.9", {"start": v(10.55, 4.2) * mm, "end": v(10.6, 4.2) * mm});
            skLineSegment(sketch, "E100.3.10", {"start": v(10.76, 4.05) * mm, "end": v(10.77, 4.02) * mm});
            skLineSegment(sketch, "E100.3.11", {"start": v(10.6, 4.2) * mm, "end": v(10.65, 4.2) * mm});
            skLineSegment(sketch, "E100.3.12", {"start": v(10.45, 4.21) * mm, "end": v(10.5, 4.21) * mm});
            skLineSegment(sketch, "E100.3.13", {"start": v(10.15, 5.3) * mm, "end": v(10.18, 5.34) * mm});
            skLineSegment(sketch, "E100.3.14", {"start": v(10.7, 4.2) * mm, "end": v(10.72, 4.16) * mm});
            skLineSegment(sketch, "E100.3.15", {"start": v(10.3, 4.21) * mm, "end": v(10.35, 4.21) * mm});
            skLineSegment(sketch, "E100.3.16", {"start": v(10.73, 4.13) * mm, "end": v(10.75, 4.1) * mm});
            skLineSegment(sketch, "E100.3.17", {"start": v(10.18, 5.34) * mm, "end": v(10.17, 5.38) * mm});
            skLineSegment(sketch, "E100.3.18", {"start": v(10.03, 5.14) * mm, "end": v(10.06, 5.18) * mm});
            skLineSegment(sketch, "E100.3.19", {"start": v(10.4, 4.21) * mm, "end": v(10.45, 4.21) * mm});
            skLineSegment(sketch, "E100.3.20", {"start": v(10.65, 4.2) * mm, "end": v(10.7, 4.2) * mm});
            skLineSegment(sketch, "E100.3.21", {"start": v(9.93, 5.02) * mm, "end": v(9.96, 5.06) * mm});
            skLineSegment(sketch, "E100.3.22", {"start": v(10.06, 5.18) * mm, "end": v(10.1, 5.22) * mm});
            skLineSegment(sketch, "E100.3.23", {"start": v(10.35, 4.21) * mm, "end": v(10.4, 4.21) * mm});
            skLineSegment(sketch, "E100.3.24", {"start": v(9.96, 5.06) * mm, "end": v(10, 5.1) * mm});
            skLineSegment(sketch, "E100.3.25", {"start": v(10, 5.1) * mm, "end": v(10.03, 5.14) * mm});
            skLineSegment(sketch, "E100.3.26", {"start": v(10.12, 5.26) * mm, "end": v(10.15, 5.3) * mm});
            skLineSegment(sketch, "E100.3.27", {"start": v(9.9, 4.99) * mm, "end": v(9.93, 5.02) * mm});
            skLineSegment(sketch, "E100.3.28", {"start": v(9.41, 4.53) * mm, "end": v(9.42, 4.54) * mm});
            skLineSegment(sketch, "E100.3.29", {"start": v(9.62, 4.71) * mm, "end": v(9.65, 4.74) * mm});
            skLineSegment(sketch, "E100.3.30", {"start": v(9.72, 4.8) * mm, "end": v(9.76, 4.84) * mm});
            skLineSegment(sketch, "E100.3.31", {"start": v(9.61, 4.15) * mm, "end": v(9.63, 4.15) * mm});
            skLineSegment(sketch, "E100.3.32", {"start": v(10.2, 4.21) * mm, "end": v(10.25, 4.21) * mm});
            skLineSegment(sketch, "E100.3.33", {"start": v(9.39, 4.48) * mm, "end": v(9.4, 4.48) * mm});
            skLineSegment(sketch, "E100.3.34", {"start": v(9.53, 4.16) * mm, "end": v(9.54, 4.16) * mm});
            skLineSegment(sketch, "E100.3.35", {"start": v(9.43, 4.55) * mm, "end": v(9.44, 4.56) * mm});
            skLineSegment(sketch, "E100.3.36", {"start": v(9.5, 4.62) * mm, "end": v(9.54, 4.65) * mm});
            skLineSegment(sketch, "E100.3.37", {"start": v(10.1, 4.2) * mm, "end": v(10.15, 4.2) * mm});
            skLineSegment(sketch, "E100.3.38", {"start": v(9.81, 4.18) * mm, "end": v(9.86, 4.18) * mm});
            skLineSegment(sketch, "E100.3.39", {"start": v(9.95, 4.2) * mm, "end": v(10, 4.2) * mm});
            skLineSegment(sketch, "E100.3.40", {"start": v(9.44, 4.3) * mm, "end": v(9.45, 4.29) * mm});
            skLineSegment(sketch, "E100.3.41", {"start": v(9.45, 4.29) * mm, "end": v(9.46, 4.27) * mm});
            skLineSegment(sketch, "E100.3.42", {"start": v(9.8, 4.88) * mm, "end": v(9.83, 4.91) * mm});
            skLineSegment(sketch, "E100.3.43", {"start": v(9.76, 4.84) * mm, "end": v(9.8, 4.88) * mm});
            skLineSegment(sketch, "E100.3.44", {"start": v(10.15, 4.2) * mm, "end": v(10.2, 4.21) * mm});
            skLineSegment(sketch, "E100.3.45", {"start": v(9.56, 4.15) * mm, "end": v(9.57, 4.15) * mm});
            skLineSegment(sketch, "E100.3.46", {"start": v(9.49, 4.2) * mm, "end": v(9.5, 4.19) * mm});
            skLineSegment(sketch, "E100.3.47", {"start": v(10, 4.2) * mm, "end": v(10.05, 4.2) * mm});
            skLineSegment(sketch, "E100.3.48", {"start": v(9.86, 4.95) * mm, "end": v(9.9, 4.99) * mm});
            skLineSegment(sketch, "E100.3.49", {"start": v(9.45, 4.57) * mm, "end": v(9.46, 4.58) * mm});
            skLineSegment(sketch, "E100.3.50", {"start": v(10.05, 4.2) * mm, "end": v(10.1, 4.2) * mm});
            skLineSegment(sketch, "E100.3.51", {"start": v(9.76, 4.17) * mm, "end": v(9.81, 4.18) * mm});
            skLineSegment(sketch, "E100.3.52", {"start": v(9.38, 4.47) * mm, "end": v(9.39, 4.48) * mm});
            skLineSegment(sketch, "E100.3.53", {"start": v(9.69, 4.78) * mm, "end": v(9.72, 4.8) * mm});
            skLineSegment(sketch, "E100.3.54", {"start": v(9.65, 4.15) * mm, "end": v(9.66, 4.15) * mm});
            skLineSegment(sketch, "E100.3.55", {"start": v(9.48, 4.22) * mm, "end": v(9.49, 4.2) * mm});
            skLineSegment(sketch, "E100.3.56", {"start": v(9.6, 4.15) * mm, "end": v(9.61, 4.15) * mm});
            skLineSegment(sketch, "E100.3.57", {"start": v(9.38, 4.46) * mm, "end": v(9.38, 4.47) * mm});
            skLineSegment(sketch, "E100.3.58", {"start": v(9.68, 4.15) * mm, "end": v(9.7, 4.16) * mm});
            skLineSegment(sketch, "E100.3.59", {"start": v(9.46, 4.58) * mm, "end": v(9.48, 4.6) * mm});
            skLineSegment(sketch, "E100.3.60", {"start": v(9.86, 4.18) * mm, "end": v(9.9, 4.19) * mm});
            skLineSegment(sketch, "E100.3.61", {"start": v(9.83, 4.91) * mm, "end": v(9.86, 4.95) * mm});
            skLineSegment(sketch, "E100.3.62", {"start": v(9.65, 4.74) * mm, "end": v(9.69, 4.78) * mm});
            skLineSegment(sketch, "E100.3.63", {"start": v(9.5, 4.6) * mm, "end": v(9.5, 4.62) * mm});
            skLineSegment(sketch, "E100.3.64", {"start": v(9.38, 4.45) * mm, "end": v(9.38, 4.46) * mm});
            skLineSegment(sketch, "E100.3.65", {"start": v(9.47, 4.25) * mm, "end": v(9.48, 4.22) * mm});
            skLineSegment(sketch, "E100.3.66", {"start": v(9.66, 4.15) * mm, "end": v(9.68, 4.15) * mm});
            skLineSegment(sketch, "E100.3.67", {"start": v(9.9, 4.19) * mm, "end": v(9.95, 4.2) * mm});
            skLineSegment(sketch, "E100.3.68", {"start": v(9.59, 4.15) * mm, "end": v(9.6, 4.15) * mm});
            skLineSegment(sketch, "E100.3.69", {"start": v(9.58, 4.68) * mm, "end": v(9.62, 4.71) * mm});
            skLineSegment(sketch, "E100.3.70", {"start": v(9.5, 4.18) * mm, "end": v(9.5, 4.18) * mm});
            skLineSegment(sketch, "E100.3.71", {"start": v(9.63, 4.15) * mm, "end": v(9.65, 4.15) * mm});
            skLineSegment(sketch, "E100.3.72", {"start": v(9.51, 4.17) * mm, "end": v(9.52, 4.17) * mm});
            skLineSegment(sketch, "E100.3.73", {"start": v(9.54, 4.65) * mm, "end": v(9.58, 4.68) * mm});
            skLineSegment(sketch, "E100.3.74", {"start": v(9.38, 4.44) * mm, "end": v(9.38, 4.45) * mm});
            skLineSegment(sketch, "E100.3.75", {"start": v(9.38, 4.43) * mm, "end": v(9.38, 4.44) * mm});
            skLineSegment(sketch, "E100.3.76", {"start": v(9.42, 4.35) * mm, "end": v(9.4, 4.37) * mm});
            skLineSegment(sketch, "E100.3.77", {"start": v(9.57, 4.15) * mm, "end": v(9.59, 4.15) * mm});
            skLineSegment(sketch, "E100.3.78", {"start": v(9.42, 4.54) * mm, "end": v(9.43, 4.55) * mm});
            skLineSegment(sketch, "E100.3.79", {"start": v(9.72, 4.16) * mm, "end": v(9.76, 4.17) * mm});
            skLineSegment(sketch, "E100.3.80", {"start": v(9.52, 4.17) * mm, "end": v(9.53, 4.16) * mm});
            skLineSegment(sketch, "E100.3.81", {"start": v(9.39, 4.42) * mm, "end": v(9.38, 4.43) * mm});
            skLineSegment(sketch, "E100.3.82", {"start": v(9.7, 4.16) * mm, "end": v(9.72, 4.16) * mm});
            skLineSegment(sketch, "E100.3.83", {"start": v(9.43, 4.33) * mm, "end": v(9.42, 4.35) * mm});
            skLineSegment(sketch, "E100.3.84", {"start": v(9.44, 4.56) * mm, "end": v(9.45, 4.57) * mm});
            skLineSegment(sketch, "E100.3.85", {"start": v(9.55, 4.16) * mm, "end": v(9.56, 4.15) * mm});
            skLineSegment(sketch, "E100.3.86", {"start": v(9.44, 4.3) * mm, "end": v(9.43, 4.33) * mm});
            skLineSegment(sketch, "E100.3.87", {"start": v(9.48, 4.6) * mm, "end": v(9.5, 4.6) * mm});
            skLineSegment(sketch, "E100.3.88", {"start": v(9.39, 4.42) * mm, "end": v(9.39, 4.42) * mm});
            skLineSegment(sketch, "E100.3.89", {"start": v(9.4, 4.4) * mm, "end": v(9.39, 4.42) * mm});
            skLineSegment(sketch, "E100.3.90", {"start": v(9.49, 4.2) * mm, "end": v(9.49, 4.2) * mm});
            skLineSegment(sketch, "E100.3.91", {"start": v(9.5, 4.18) * mm, "end": v(9.51, 4.17) * mm});
            skLineSegment(sketch, "E100.3.92", {"start": v(9.54, 4.16) * mm, "end": v(9.55, 4.16) * mm});
            skLineSegment(sketch, "E100.3.93", {"start": v(9.46, 4.27) * mm, "end": v(9.47, 4.25) * mm});
            skLineSegment(sketch, "E100.3.94", {"start": v(9.4, 4.37) * mm, "end": v(9.4, 4.4) * mm});
            skLineSegment(sketch, "E100.3.95", {"start": v(9.4, 4.5) * mm, "end": v(9.4, 4.5) * mm});
            skLineSegment(sketch, "E100.3.96", {"start": v(9.5, 4.19) * mm, "end": v(9.5, 4.18) * mm});
            skLineSegment(sketch, "E100.3.97", {"start": v(9.4, 4.48) * mm, "end": v(9.4, 4.5) * mm});
            skLineSegment(sketch, "E100.3.98", {"start": v(9.4, 4.5) * mm, "end": v(9.4, 4.52) * mm});
            skLineSegment(sketch, "E100.3.99", {"start": v(9.4, 4.52) * mm, "end": v(9.41, 4.53) * mm});
            skLineSegment(sketch, "E100.4.0", {"start": v(10.02, 5.65) * mm, "end": v(10.04, 5.61) * mm});
            skLineSegment(sketch, "E100.4.1", {"start": v(9.27, 6.8) * mm, "end": v(9.25, 6.83) * mm});
            skLineSegment(sketch, "E100.4.2", {"start": v(9.24, 6.6) * mm, "end": v(9.27, 6.65) * mm});
            skLineSegment(sketch, "E100.4.3", {"start": v(9.23, 6.86) * mm, "end": v(9.2, 6.9) * mm});
            skLineSegment(sketch, "E100.4.4", {"start": v(9.55, 5.63) * mm, "end": v(9.6, 5.64) * mm});
            skLineSegment(sketch, "E100.4.5", {"start": v(10.06, 5.58) * mm, "end": v(10.07, 5.55) * mm});
            skLineSegment(sketch, "E100.4.6", {"start": v(9.3, 6.77) * mm, "end": v(9.27, 6.8) * mm});
            skLineSegment(sketch, "E100.4.7", {"start": v(9.8, 5.66) * mm, "end": v(9.85, 5.67) * mm});
            skLineSegment(sketch, "E100.4.8", {"start": v(9.25, 6.83) * mm, "end": v(9.23, 6.86) * mm});
            skLineSegment(sketch, "E100.4.9", {"start": v(9.85, 5.67) * mm, "end": v(9.9, 5.67) * mm});
            skLineSegment(sketch, "E100.4.10", {"start": v(10.07, 5.55) * mm, "end": v(10.1, 5.51) * mm});
            skLineSegment(sketch, "E100.4.11", {"start": v(9.9, 5.67) * mm, "end": v(9.95, 5.68) * mm});
            skLineSegment(sketch, "E100.4.12", {"start": v(9.74, 5.66) * mm, "end": v(9.8, 5.66) * mm});
            skLineSegment(sketch, "E100.4.13", {"start": v(9.3, 6.7) * mm, "end": v(9.32, 6.74) * mm});
            skLineSegment(sketch, "E100.4.14", {"start": v(10, 5.68) * mm, "end": v(10.02, 5.65) * mm});
            skLineSegment(sketch, "E100.4.15", {"start": v(9.6, 5.64) * mm, "end": v(9.64, 5.64) * mm});
            skLineSegment(sketch, "E100.4.16", {"start": v(10.04, 5.61) * mm, "end": v(10.06, 5.58) * mm});
            skLineSegment(sketch, "E100.4.17", {"start": v(9.32, 6.74) * mm, "end": v(9.3, 6.77) * mm});
            skLineSegment(sketch, "E100.4.18", {"start": v(9.2, 6.51) * mm, "end": v(9.22, 6.56) * mm});
            skLineSegment(sketch, "E100.4.19", {"start": v(9.7, 5.65) * mm, "end": v(9.74, 5.66) * mm});
            skLineSegment(sketch, "E100.4.20", {"start": v(9.95, 5.68) * mm, "end": v(10, 5.68) * mm});
            skLineSegment(sketch, "E100.4.21", {"start": v(9.11, 6.39) * mm, "end": v(9.14, 6.43) * mm});
            skLineSegment(sketch, "E100.4.22", {"start": v(9.22, 6.56) * mm, "end": v(9.24, 6.6) * mm});
            skLineSegment(sketch, "E100.4.23", {"start": v(9.64, 5.64) * mm, "end": v(9.7, 5.65) * mm});
            skLineSegment(sketch, "E100.4.24", {"start": v(9.14, 6.43) * mm, "end": v(9.17, 6.47) * mm});
            skLineSegment(sketch, "E100.4.25", {"start": v(9.17, 6.47) * mm, "end": v(9.2, 6.51) * mm});
            skLineSegment(sketch, "E100.4.26", {"start": v(9.27, 6.65) * mm, "end": v(9.3, 6.7) * mm});
            skLineSegment(sketch, "E100.4.27", {"start": v(9.08, 6.34) * mm, "end": v(9.11, 6.39) * mm});
            skLineSegment(sketch, "E100.4.28", {"start": v(8.67, 5.82) * mm, "end": v(8.68, 5.83) * mm});
            skLineSegment(sketch, "E100.4.29", {"start": v(8.85, 6.03) * mm, "end": v(8.88, 6.07) * mm});
            skLineSegment(sketch, "E100.4.30", {"start": v(8.94, 6.14) * mm, "end": v(8.97, 6.18) * mm});
            skLineSegment(sketch, "E100.4.31", {"start": v(8.93, 5.47) * mm, "end": v(8.94, 5.48) * mm});
            skLineSegment(sketch, "E100.4.32", {"start": v(9.5, 5.62) * mm, "end": v(9.55, 5.63) * mm});
            skLineSegment(sketch, "E100.4.33", {"start": v(8.65, 5.77) * mm, "end": v(8.66, 5.78) * mm});
            skLineSegment(sketch, "E100.4.34", {"start": v(8.84, 5.48) * mm, "end": v(8.85, 5.47) * mm});
            skLineSegment(sketch, "E100.4.35", {"start": v(8.69, 5.84) * mm, "end": v(8.7, 5.86) * mm});
            skLineSegment(sketch, "E100.4.36", {"start": v(8.75, 5.93) * mm, "end": v(8.78, 5.96) * mm});
            skLineSegment(sketch, "E100.4.37", {"start": v(9.4, 5.6) * mm, "end": v(9.45, 5.61) * mm});
            skLineSegment(sketch, "E100.4.38", {"start": v(9.12, 5.53) * mm, "end": v(9.16, 5.54) * mm});
            skLineSegment(sketch, "E100.4.39", {"start": v(9.26, 5.57) * mm, "end": v(9.3, 5.58) * mm});
            skLineSegment(sketch, "E100.4.40", {"start": v(8.73, 5.6) * mm, "end": v(8.74, 5.59) * mm});
            skLineSegment(sketch, "E100.4.41", {"start": v(8.74, 5.59) * mm, "end": v(8.75, 5.57) * mm});
            skLineSegment(sketch, "E100.4.42", {"start": v(9, 6.22) * mm, "end": v(9.03, 6.26) * mm});
            skLineSegment(sketch, "E100.4.43", {"start": v(8.97, 6.18) * mm, "end": v(9, 6.22) * mm});
            skLineSegment(sketch, "E100.4.44", {"start": v(9.45, 5.61) * mm, "end": v(9.5, 5.62) * mm});
            skLineSegment(sketch, "E100.4.45", {"start": v(8.87, 5.47) * mm, "end": v(8.88, 5.47) * mm});
            skLineSegment(sketch, "E100.4.46", {"start": v(8.8, 5.5) * mm, "end": v(8.8, 5.5) * mm});
            skLineSegment(sketch, "E100.4.47", {"start": v(9.3, 5.58) * mm, "end": v(9.35, 5.6) * mm});
            skLineSegment(sketch, "E100.4.48", {"start": v(9.06, 6.3) * mm, "end": v(9.08, 6.34) * mm});
            skLineSegment(sketch, "E100.4.49", {"start": v(8.7, 5.87) * mm, "end": v(8.72, 5.88) * mm});
            skLineSegment(sketch, "E100.4.50", {"start": v(9.35, 5.6) * mm, "end": v(9.4, 5.6) * mm});
            skLineSegment(sketch, "E100.4.51", {"start": v(9.07, 5.51) * mm, "end": v(9.12, 5.53) * mm});
            skLineSegment(sketch, "E100.4.52", {"start": v(8.65, 5.76) * mm, "end": v(8.65, 5.77) * mm});
            skLineSegment(sketch, "E100.4.53", {"start": v(8.91, 6.1) * mm, "end": v(8.94, 6.14) * mm});
            skLineSegment(sketch, "E100.4.54", {"start": v(8.96, 5.48) * mm, "end": v(8.97, 5.48) * mm});
            skLineSegment(sketch, "E100.4.55", {"start": v(8.78, 5.53) * mm, "end": v(8.8, 5.51) * mm});
            skLineSegment(sketch, "E100.4.56", {"start": v(8.91, 5.47) * mm, "end": v(8.93, 5.47) * mm});
            skLineSegment(sketch, "E100.4.57", {"start": v(8.65, 5.75) * mm, "end": v(8.65, 5.76) * mm});
            skLineSegment(sketch, "E100.4.58", {"start": v(8.99, 5.49) * mm, "end": v(9, 5.5) * mm});
            skLineSegment(sketch, "E100.4.59", {"start": v(8.72, 5.88) * mm, "end": v(8.73, 5.9) * mm});
            skLineSegment(sketch, "E100.4.60", {"start": v(9.16, 5.54) * mm, "end": v(9.2, 5.56) * mm});
            skLineSegment(sketch, "E100.4.61", {"start": v(9.03, 6.26) * mm, "end": v(9.06, 6.3) * mm});
            skLineSegment(sketch, "E100.4.62", {"start": v(8.88, 6.07) * mm, "end": v(8.91, 6.1) * mm});
            skLineSegment(sketch, "E100.4.63", {"start": v(8.74, 5.91) * mm, "end": v(8.75, 5.93) * mm});
            skLineSegment(sketch, "E100.4.64", {"start": v(8.65, 5.74) * mm, "end": v(8.65, 5.75) * mm});
            skLineSegment(sketch, "E100.4.65", {"start": v(8.77, 5.55) * mm, "end": v(8.78, 5.53) * mm});
            skLineSegment(sketch, "E100.4.66", {"start": v(8.97, 5.48) * mm, "end": v(8.99, 5.49) * mm});
            skLineSegment(sketch, "E100.4.67", {"start": v(9.2, 5.56) * mm, "end": v(9.26, 5.57) * mm});
            skLineSegment(sketch, "E100.4.68", {"start": v(8.9, 5.47) * mm, "end": v(8.91, 5.47) * mm});
            skLineSegment(sketch, "E100.4.69", {"start": v(8.82, 6) * mm, "end": v(8.85, 6.03) * mm});
            skLineSegment(sketch, "E100.4.70", {"start": v(8.8, 5.5) * mm, "end": v(8.81, 5.49) * mm});
            skLineSegment(sketch, "E100.4.71", {"start": v(8.94, 5.48) * mm, "end": v(8.96, 5.48) * mm});
            skLineSegment(sketch, "E100.4.72", {"start": v(8.82, 5.48) * mm, "end": v(8.83, 5.48) * mm});
            skLineSegment(sketch, "E100.4.73", {"start": v(8.78, 5.96) * mm, "end": v(8.82, 6) * mm});
            skLineSegment(sketch, "E100.4.74", {"start": v(8.65, 5.73) * mm, "end": v(8.65, 5.74) * mm});
            skLineSegment(sketch, "E100.4.75", {"start": v(8.66, 5.72) * mm, "end": v(8.65, 5.73) * mm});
            skLineSegment(sketch, "E100.4.76", {"start": v(8.7, 5.65) * mm, "end": v(8.69, 5.67) * mm});
            skLineSegment(sketch, "E100.4.77", {"start": v(8.88, 5.47) * mm, "end": v(8.9, 5.47) * mm});
            skLineSegment(sketch, "E100.4.78", {"start": v(8.68, 5.83) * mm, "end": v(8.69, 5.84) * mm});
            skLineSegment(sketch, "E100.4.79", {"start": v(9.03, 5.5) * mm, "end": v(9.07, 5.51) * mm});
            skLineSegment(sketch, "E100.4.80", {"start": v(8.83, 5.48) * mm, "end": v(8.84, 5.48) * mm});
            skLineSegment(sketch, "E100.4.81", {"start": v(8.66, 5.71) * mm, "end": v(8.66, 5.72) * mm});
            skLineSegment(sketch, "E100.4.82", {"start": v(9, 5.5) * mm, "end": v(9.03, 5.5) * mm});
            skLineSegment(sketch, "E100.4.83", {"start": v(8.72, 5.63) * mm, "end": v(8.7, 5.65) * mm});
            skLineSegment(sketch, "E100.4.84", {"start": v(8.7, 5.86) * mm, "end": v(8.7, 5.87) * mm});
            skLineSegment(sketch, "E100.4.85", {"start": v(8.86, 5.47) * mm, "end": v(8.87, 5.47) * mm});
            skLineSegment(sketch, "E100.4.86", {"start": v(8.73, 5.6) * mm, "end": v(8.72, 5.63) * mm});
            skLineSegment(sketch, "E100.4.87", {"start": v(8.73, 5.9) * mm, "end": v(8.74, 5.91) * mm});
            skLineSegment(sketch, "E100.4.88", {"start": v(8.66, 5.7) * mm, "end": v(8.66, 5.71) * mm});
            skLineSegment(sketch, "E100.4.89", {"start": v(8.68, 5.69) * mm, "end": v(8.66, 5.7) * mm});
            skLineSegment(sketch, "E100.4.90", {"start": v(8.8, 5.51) * mm, "end": v(8.8, 5.5) * mm});
            skLineSegment(sketch, "E100.4.91", {"start": v(8.81, 5.49) * mm, "end": v(8.82, 5.48) * mm});
            skLineSegment(sketch, "E100.4.92", {"start": v(8.85, 5.47) * mm, "end": v(8.86, 5.47) * mm});
            skLineSegment(sketch, "E100.4.93", {"start": v(8.75, 5.57) * mm, "end": v(8.77, 5.55) * mm});
            skLineSegment(sketch, "E100.4.94", {"start": v(8.69, 5.67) * mm, "end": v(8.68, 5.69) * mm});
            skLineSegment(sketch, "E100.4.95", {"start": v(8.66, 5.79) * mm, "end": v(8.66, 5.8) * mm});
            skLineSegment(sketch, "E100.4.96", {"start": v(8.8, 5.5) * mm, "end": v(8.8, 5.5) * mm});
            skLineSegment(sketch, "E100.4.97", {"start": v(8.66, 5.78) * mm, "end": v(8.66, 5.79) * mm});
            skLineSegment(sketch, "E100.4.98", {"start": v(8.66, 5.8) * mm, "end": v(8.67, 5.8) * mm});
            skLineSegment(sketch, "E100.4.99", {"start": v(8.67, 5.8) * mm, "end": v(8.67, 5.82) * mm});
            skLineSegment(sketch, "E100.5.0", {"start": v(9.11, 7.01) * mm, "end": v(9.14, 6.98) * mm});
            skLineSegment(sketch, "E100.5.1", {"start": v(8.21, 8.05) * mm, "end": v(8.19, 8.08) * mm});
            skLineSegment(sketch, "E100.5.2", {"start": v(8.21, 7.85) * mm, "end": v(8.23, 7.9) * mm});
            skLineSegment(sketch, "E100.5.3", {"start": v(8.16, 8.1) * mm, "end": v(8.13, 8.13) * mm});
            skLineSegment(sketch, "E100.5.4", {"start": v(8.65, 6.93) * mm, "end": v(8.7, 6.94) * mm});
            skLineSegment(sketch, "E100.5.5", {"start": v(9.16, 6.95) * mm, "end": v(9.18, 6.92) * mm});
            skLineSegment(sketch, "E100.5.6", {"start": v(8.24, 8.02) * mm, "end": v(8.21, 8.05) * mm});
            skLineSegment(sketch, "E100.5.7", {"start": v(8.89, 7) * mm, "end": v(8.94, 7.01) * mm});
            skLineSegment(sketch, "E100.5.8", {"start": v(8.19, 8.08) * mm, "end": v(8.16, 8.1) * mm});
            skLineSegment(sketch, "E100.5.9", {"start": v(8.94, 7.01) * mm, "end": v(8.99, 7.02) * mm});
            skLineSegment(sketch, "E100.5.10", {"start": v(9.18, 6.92) * mm, "end": v(9.2, 6.9) * mm});
            skLineSegment(sketch, "E100.5.11", {"start": v(8.99, 7.02) * mm, "end": v(9.04, 7.03) * mm});
            skLineSegment(sketch, "E100.5.12", {"start": v(8.84, 6.99) * mm, "end": v(8.89, 7) * mm});
            skLineSegment(sketch, "E100.5.13", {"start": v(8.25, 7.95) * mm, "end": v(8.27, 8) * mm});
            skLineSegment(sketch, "E100.5.14", {"start": v(9.09, 7.04) * mm, "end": v(9.11, 7.01) * mm});
            skLineSegment(sketch, "E100.5.15", {"start": v(8.7, 6.94) * mm, "end": v(8.74, 6.96) * mm});
            skLineSegment(sketch, "E100.5.16", {"start": v(9.14, 6.98) * mm, "end": v(9.16, 6.95) * mm});
            skLineSegment(sketch, "E100.5.17", {"start": v(8.27, 8) * mm, "end": v(8.24, 8.02) * mm});
            skLineSegment(sketch, "E100.5.18", {"start": v(8.17, 7.76) * mm, "end": v(8.2, 7.8) * mm});
            skLineSegment(sketch, "E100.5.19", {"start": v(8.8, 6.97) * mm, "end": v(8.84, 6.99) * mm});
            skLineSegment(sketch, "E100.5.20", {"start": v(9.04, 7.03) * mm, "end": v(9.09, 7.04) * mm});
            skLineSegment(sketch, "E100.5.21", {"start": v(8.11, 7.62) * mm, "end": v(8.13, 7.66) * mm});
            skLineSegment(sketch, "E100.5.22", {"start": v(8.2, 7.8) * mm, "end": v(8.21, 7.85) * mm});
            skLineSegment(sketch, "E100.5.23", {"start": v(8.74, 6.96) * mm, "end": v(8.8, 6.97) * mm});
            skLineSegment(sketch, "E100.5.24", {"start": v(8.13, 7.66) * mm, "end": v(8.15, 7.71) * mm});
            skLineSegment(sketch, "E100.5.25", {"start": v(8.15, 7.71) * mm, "end": v(8.17, 7.76) * mm});
            skLineSegment(sketch, "E100.5.26", {"start": v(8.23, 7.9) * mm, "end": v(8.25, 7.95) * mm});
            skLineSegment(sketch, "E100.5.27", {"start": v(8.09, 7.57) * mm, "end": v(8.11, 7.62) * mm});
            skLineSegment(sketch, "E100.5.28", {"start": v(7.76, 7) * mm, "end": v(7.76, 7) * mm});
            skLineSegment(sketch, "E100.5.29", {"start": v(7.9, 7.23) * mm, "end": v(7.93, 7.27) * mm});
            skLineSegment(sketch, "E100.5.30", {"start": v(7.97, 7.35) * mm, "end": v(8, 7.4) * mm});
            skLineSegment(sketch, "E100.5.31", {"start": v(8.06, 6.69) * mm, "end": v(8.07, 6.7) * mm});
            skLineSegment(sketch, "E100.5.32", {"start": v(8.6, 6.91) * mm, "end": v(8.65, 6.93) * mm});
            skLineSegment(sketch, "E100.5.33", {"start": v(7.75, 6.94) * mm, "end": v(7.75, 6.95) * mm});
            skLineSegment(sketch, "E100.5.34", {"start": v(7.97, 6.68) * mm, "end": v(7.98, 6.68) * mm});
            skLineSegment(sketch, "E100.5.35", {"start": v(7.77, 7.02) * mm, "end": v(7.77, 7.04) * mm});
            skLineSegment(sketch, "E100.5.36", {"start": v(7.82, 7.11) * mm, "end": v(7.85, 7.15) * mm});
            skLineSegment(sketch, "E100.5.37", {"start": v(8.5, 6.88) * mm, "end": v(8.55, 6.9) * mm});
            skLineSegment(sketch, "E100.5.38", {"start": v(8.24, 6.77) * mm, "end": v(8.28, 6.8) * mm});
            skLineSegment(sketch, "E100.5.39", {"start": v(8.37, 6.83) * mm, "end": v(8.41, 6.85) * mm});
            skLineSegment(sketch, "E100.5.40", {"start": v(7.84, 6.8) * mm, "end": v(7.86, 6.78) * mm});
            skLineSegment(sketch, "E100.5.41", {"start": v(7.86, 6.78) * mm, "end": v(7.87, 6.76) * mm});
            skLineSegment(sketch, "E100.5.42", {"start": v(8.02, 7.44) * mm, "end": v(8.05, 7.48) * mm});
            skLineSegment(sketch, "E100.5.43", {"start": v(8, 7.4) * mm, "end": v(8.02, 7.44) * mm});
            skLineSegment(sketch, "E100.5.44", {"start": v(8.55, 6.9) * mm, "end": v(8.6, 6.91) * mm});
            skLineSegment(sketch, "E100.5.45", {"start": v(8, 6.68) * mm, "end": v(8.02, 6.68) * mm});
            skLineSegment(sketch, "E100.5.46", {"start": v(7.92, 6.7) * mm, "end": v(7.93, 6.7) * mm});
            skLineSegment(sketch, "E100.5.47", {"start": v(8.41, 6.85) * mm, "end": v(8.46, 6.86) * mm});
            skLineSegment(sketch, "E100.5.48", {"start": v(8.07, 7.53) * mm, "end": v(8.09, 7.57) * mm});
            skLineSegment(sketch, "E100.5.49", {"start": v(7.78, 7.05) * mm, "end": v(7.79, 7.06) * mm});
            skLineSegment(sketch, "E100.5.50", {"start": v(8.46, 6.86) * mm, "end": v(8.5, 6.88) * mm});
            skLineSegment(sketch, "E100.5.51", {"start": v(8.2, 6.75) * mm, "end": v(8.24, 6.77) * mm});
            skLineSegment(sketch, "E100.5.52", {"start": v(7.75, 6.93) * mm, "end": v(7.75, 6.94) * mm});
            skLineSegment(sketch, "E100.5.53", {"start": v(7.95, 7.31) * mm, "end": v(7.97, 7.35) * mm});
            skLineSegment(sketch, "E100.5.54", {"start": v(8.09, 6.7) * mm, "end": v(8.1, 6.7) * mm});
            skLineSegment(sketch, "E100.5.55", {"start": v(7.9, 6.72) * mm, "end": v(7.92, 6.7) * mm});
            skLineSegment(sketch, "E100.5.56", {"start": v(8.04, 6.69) * mm, "end": v(8.06, 6.69) * mm});
            skLineSegment(sketch, "E100.5.57", {"start": v(7.75, 6.92) * mm, "end": v(7.75, 6.93) * mm});
            skLineSegment(sketch, "E100.5.58", {"start": v(8.12, 6.71) * mm, "end": v(8.13, 6.72) * mm});
            skLineSegment(sketch, "E100.5.59", {"start": v(7.79, 7.06) * mm, "end": v(7.8, 7.08) * mm});
            skLineSegment(sketch, "E100.5.60", {"start": v(8.28, 6.8) * mm, "end": v(8.32, 6.81) * mm});
            skLineSegment(sketch, "E100.5.61", {"start": v(8.05, 7.48) * mm, "end": v(8.07, 7.53) * mm});
            skLineSegment(sketch, "E100.5.62", {"start": v(7.93, 7.27) * mm, "end": v(7.95, 7.31) * mm});
            skLineSegment(sketch, "E100.5.63", {"start": v(7.8, 7.1) * mm, "end": v(7.82, 7.11) * mm});
            skLineSegment(sketch, "E100.5.64", {"start": v(7.75, 6.91) * mm, "end": v(7.75, 6.92) * mm});
            skLineSegment(sketch, "E100.5.65", {"start": v(7.89, 6.74) * mm, "end": v(7.9, 6.72) * mm});
            skLineSegment(sketch, "E100.5.66", {"start": v(8.1, 6.7) * mm, "end": v(8.12, 6.71) * mm});
            skLineSegment(sketch, "E100.5.67", {"start": v(8.32, 6.81) * mm, "end": v(8.37, 6.83) * mm});
            skLineSegment(sketch, "E100.5.68", {"start": v(8.03, 6.68) * mm, "end": v(8.04, 6.69) * mm});
            skLineSegment(sketch, "E100.5.69", {"start": v(7.87, 7.19) * mm, "end": v(7.9, 7.23) * mm});
            skLineSegment(sketch, "E100.5.70", {"start": v(7.94, 6.7) * mm, "end": v(7.94, 6.69) * mm});
            skLineSegment(sketch, "E100.5.71", {"start": v(8.07, 6.7) * mm, "end": v(8.09, 6.7) * mm});
            skLineSegment(sketch, "E100.5.72", {"start": v(7.95, 6.68) * mm, "end": v(7.96, 6.68) * mm});
            skLineSegment(sketch, "E100.5.73", {"start": v(7.85, 7.15) * mm, "end": v(7.87, 7.19) * mm});
            skLineSegment(sketch, "E100.5.74", {"start": v(7.75, 6.9) * mm, "end": v(7.75, 6.91) * mm});
            skLineSegment(sketch, "E100.5.75", {"start": v(7.75, 6.9) * mm, "end": v(7.75, 6.9) * mm});
            skLineSegment(sketch, "E100.5.76", {"start": v(7.81, 6.83) * mm, "end": v(7.8, 6.85) * mm});
            skLineSegment(sketch, "E100.5.77", {"start": v(8.02, 6.68) * mm, "end": v(8.03, 6.68) * mm});
            skLineSegment(sketch, "E100.5.78", {"start": v(7.76, 7) * mm, "end": v(7.77, 7.02) * mm});
            skLineSegment(sketch, "E100.5.79", {"start": v(8.15, 6.73) * mm, "end": v(8.2, 6.75) * mm});
            skLineSegment(sketch, "E100.5.80", {"start": v(7.96, 6.68) * mm, "end": v(7.97, 6.68) * mm});
            skLineSegment(sketch, "E100.5.81", {"start": v(7.76, 6.89) * mm, "end": v(7.75, 6.9) * mm});
            skLineSegment(sketch, "E100.5.82", {"start": v(8.13, 6.72) * mm, "end": v(8.15, 6.73) * mm});
            skLineSegment(sketch, "E100.5.83", {"start": v(7.83, 6.81) * mm, "end": v(7.81, 6.83) * mm});
            skLineSegment(sketch, "E100.5.84", {"start": v(7.77, 7.04) * mm, "end": v(7.78, 7.05) * mm});
            skLineSegment(sketch, "E100.5.85", {"start": v(8, 6.68) * mm, "end": v(8, 6.68) * mm});
            skLineSegment(sketch, "E100.5.86", {"start": v(7.84, 6.8) * mm, "end": v(7.83, 6.81) * mm});
            skLineSegment(sketch, "E100.5.87", {"start": v(7.8, 7.08) * mm, "end": v(7.8, 7.1) * mm});
            skLineSegment(sketch, "E100.5.88", {"start": v(7.76, 6.88) * mm, "end": v(7.76, 6.89) * mm});
            skLineSegment(sketch, "E100.5.89", {"start": v(7.78, 6.86) * mm, "end": v(7.76, 6.88) * mm});
            skLineSegment(sketch, "E100.5.90", {"start": v(7.92, 6.7) * mm, "end": v(7.92, 6.7) * mm});
            skLineSegment(sketch, "E100.5.91", {"start": v(7.94, 6.69) * mm, "end": v(7.95, 6.68) * mm});
            skLineSegment(sketch, "E100.5.92", {"start": v(7.98, 6.68) * mm, "end": v(8, 6.68) * mm});
            skLineSegment(sketch, "E100.5.93", {"start": v(7.87, 6.76) * mm, "end": v(7.89, 6.74) * mm});
            skLineSegment(sketch, "E100.5.94", {"start": v(7.8, 6.85) * mm, "end": v(7.78, 6.86) * mm});
            skLineSegment(sketch, "E100.5.95", {"start": v(7.75, 6.96) * mm, "end": v(7.75, 6.97) * mm});
            skLineSegment(sketch, "E100.5.96", {"start": v(7.93, 6.7) * mm, "end": v(7.94, 6.7) * mm});
            skLineSegment(sketch, "E100.5.97", {"start": v(7.75, 6.95) * mm, "end": v(7.75, 6.96) * mm});
            skLineSegment(sketch, "E100.5.98", {"start": v(7.75, 6.97) * mm, "end": v(7.75, 6.98) * mm});
            skLineSegment(sketch, "E100.5.99", {"start": v(7.75, 6.98) * mm, "end": v(7.76, 7) * mm});
            skLineSegment(sketch, "E100.6.0", {"start": v(8.02, 8.24) * mm, "end": v(8.05, 8.21) * mm});
            skLineSegment(sketch, "E100.6.1", {"start": v(6.98, 9.14) * mm, "end": v(6.95, 9.16) * mm});
            skLineSegment(sketch, "E100.6.2", {"start": v(7.01, 8.94) * mm, "end": v(7.02, 8.99) * mm});
            skLineSegment(sketch, "E100.6.3", {"start": v(6.92, 9.18) * mm, "end": v(6.9, 9.2) * mm});
            skLineSegment(sketch, "E100.6.4", {"start": v(7.57, 8.09) * mm, "end": v(7.62, 8.11) * mm});
            skLineSegment(sketch, "E100.6.5", {"start": v(8.08, 8.19) * mm, "end": v(8.1, 8.16) * mm});
            skLineSegment(sketch, "E100.6.6", {"start": v(7.01, 9.11) * mm, "end": v(6.98, 9.14) * mm});
            skLineSegment(sketch, "E100.6.7", {"start": v(7.8, 8.2) * mm, "end": v(7.85, 8.21) * mm});
            skLineSegment(sketch, "E100.6.8", {"start": v(6.95, 9.16) * mm, "end": v(6.92, 9.18) * mm});
            skLineSegment(sketch, "E100.6.9", {"start": v(7.85, 8.21) * mm, "end": v(7.9, 8.23) * mm});
            skLineSegment(sketch, "E100.6.10", {"start": v(8.1, 8.16) * mm, "end": v(8.13, 8.13) * mm});
            skLineSegment(sketch, "E100.6.11", {"start": v(7.9, 8.23) * mm, "end": v(7.95, 8.25) * mm});
            skLineSegment(sketch, "E100.6.12", {"start": v(7.76, 8.17) * mm, "end": v(7.8, 8.2) * mm});
            skLineSegment(sketch, "E100.6.13", {"start": v(7.03, 9.04) * mm, "end": v(7.04, 9.09) * mm});
            skLineSegment(sketch, "E100.6.14", {"start": v(8, 8.27) * mm, "end": v(8.02, 8.24) * mm});
            skLineSegment(sketch, "E100.6.15", {"start": v(7.62, 8.11) * mm, "end": v(7.66, 8.13) * mm});
            skLineSegment(sketch, "E100.6.16", {"start": v(8.05, 8.21) * mm, "end": v(8.08, 8.19) * mm});
            skLineSegment(sketch, "E100.6.17", {"start": v(7.04, 9.09) * mm, "end": v(7.01, 9.11) * mm});
            skLineSegment(sketch, "E100.6.18", {"start": v(6.99, 8.84) * mm, "end": v(7, 8.89) * mm});
            skLineSegment(sketch, "E100.6.19", {"start": v(7.71, 8.15) * mm, "end": v(7.76, 8.17) * mm});
            skLineSegment(sketch, "E100.6.20", {"start": v(7.95, 8.25) * mm, "end": v(8, 8.27) * mm});
            skLineSegment(sketch, "E100.6.21", {"start": v(6.94, 8.7) * mm, "end": v(6.96, 8.74) * mm});
            skLineSegment(sketch, "E100.6.22", {"start": v(7, 8.89) * mm, "end": v(7.01, 8.94) * mm});
            skLineSegment(sketch, "E100.6.23", {"start": v(7.66, 8.13) * mm, "end": v(7.71, 8.15) * mm});
            skLineSegment(sketch, "E100.6.24", {"start": v(6.96, 8.74) * mm, "end": v(6.97, 8.8) * mm});
            skLineSegment(sketch, "E100.6.25", {"start": v(6.97, 8.8) * mm, "end": v(6.99, 8.84) * mm});
            skLineSegment(sketch, "E100.6.26", {"start": v(7.02, 8.99) * mm, "end": v(7.03, 9.04) * mm});
            skLineSegment(sketch, "E100.6.27", {"start": v(6.93, 8.65) * mm, "end": v(6.94, 8.7) * mm});
            skLineSegment(sketch, "E100.6.28", {"start": v(6.68, 8.03) * mm, "end": v(6.69, 8.04) * mm});
            skLineSegment(sketch, "E100.6.29", {"start": v(6.8, 8.28) * mm, "end": v(6.81, 8.32) * mm});
            skLineSegment(sketch, "E100.6.30", {"start": v(6.85, 8.41) * mm, "end": v(6.86, 8.46) * mm});
            skLineSegment(sketch, "E100.6.31", {"start": v(7.02, 7.77) * mm, "end": v(7.04, 7.77) * mm});
            skLineSegment(sketch, "E100.6.32", {"start": v(7.53, 8.07) * mm, "end": v(7.57, 8.09) * mm});
            skLineSegment(sketch, "E100.6.33", {"start": v(6.68, 7.97) * mm, "end": v(6.68, 7.98) * mm});
            skLineSegment(sketch, "E100.6.34", {"start": v(6.94, 7.75) * mm, "end": v(6.95, 7.75) * mm});
            skLineSegment(sketch, "E100.6.35", {"start": v(6.69, 8.06) * mm, "end": v(6.7, 8.07) * mm});
            skLineSegment(sketch, "E100.6.36", {"start": v(6.73, 8.15) * mm, "end": v(6.75, 8.2) * mm});
            skLineSegment(sketch, "E100.6.37", {"start": v(7.44, 8.02) * mm, "end": v(7.48, 8.05) * mm});
            skLineSegment(sketch, "E100.6.38", {"start": v(7.19, 7.87) * mm, "end": v(7.23, 7.9) * mm});
            skLineSegment(sketch, "E100.6.39", {"start": v(7.31, 7.95) * mm, "end": v(7.35, 7.97) * mm});
            skLineSegment(sketch, "E100.6.40", {"start": v(6.8, 7.84) * mm, "end": v(6.81, 7.83) * mm});
            skLineSegment(sketch, "E100.6.41", {"start": v(6.81, 7.83) * mm, "end": v(6.83, 7.81) * mm});
            skLineSegment(sketch, "E100.6.42", {"start": v(6.88, 8.5) * mm, "end": v(6.9, 8.55) * mm});
            skLineSegment(sketch, "E100.6.43", {"start": v(6.86, 8.46) * mm, "end": v(6.88, 8.5) * mm});
            skLineSegment(sketch, "E100.6.44", {"start": v(7.48, 8.05) * mm, "end": v(7.53, 8.07) * mm});
            skLineSegment(sketch, "E100.6.45", {"start": v(6.97, 7.75) * mm, "end": v(6.98, 7.75) * mm});
            skLineSegment(sketch, "E100.6.46", {"start": v(6.89, 7.76) * mm, "end": v(6.9, 7.75) * mm});
            skLineSegment(sketch, "E100.6.47", {"start": v(7.35, 7.97) * mm, "end": v(7.4, 8) * mm});
            skLineSegment(sketch, "E100.6.48", {"start": v(6.91, 8.6) * mm, "end": v(6.93, 8.65) * mm});
            skLineSegment(sketch, "E100.6.49", {"start": v(6.7, 8.09) * mm, "end": v(6.7, 8.1) * mm});
            skLineSegment(sketch, "E100.6.50", {"start": v(7.4, 8) * mm, "end": v(7.44, 8.02) * mm});
            skLineSegment(sketch, "E100.6.51", {"start": v(7.15, 7.85) * mm, "end": v(7.19, 7.87) * mm});
            skLineSegment(sketch, "E100.6.52", {"start": v(6.68, 7.96) * mm, "end": v(6.68, 7.97) * mm});
            skLineSegment(sketch, "E100.6.53", {"start": v(6.83, 8.37) * mm, "end": v(6.85, 8.41) * mm});
            skLineSegment(sketch, "E100.6.54", {"start": v(7.05, 7.78) * mm, "end": v(7.06, 7.79) * mm});
            skLineSegment(sketch, "E100.6.55", {"start": v(6.86, 7.78) * mm, "end": v(6.88, 7.76) * mm});
            skLineSegment(sketch, "E100.6.56", {"start": v(7, 7.76) * mm, "end": v(7.02, 7.77) * mm});
            skLineSegment(sketch, "E100.6.57", {"start": v(6.68, 7.95) * mm, "end": v(6.68, 7.96) * mm});
            skLineSegment(sketch, "E100.6.58", {"start": v(7.08, 7.8) * mm, "end": v(7.1, 7.8) * mm});
            skLineSegment(sketch, "E100.6.59", {"start": v(6.7, 8.1) * mm, "end": v(6.71, 8.12) * mm});
            skLineSegment(sketch, "E100.6.60", {"start": v(7.23, 7.9) * mm, "end": v(7.27, 7.93) * mm});
            skLineSegment(sketch, "E100.6.61", {"start": v(6.9, 8.55) * mm, "end": v(6.91, 8.6) * mm});
            skLineSegment(sketch, "E100.6.62", {"start": v(6.81, 8.32) * mm, "end": v(6.83, 8.37) * mm});
            skLineSegment(sketch, "E100.6.63", {"start": v(6.72, 8.13) * mm, "end": v(6.73, 8.15) * mm});
            skLineSegment(sketch, "E100.6.64", {"start": v(6.69, 7.94) * mm, "end": v(6.68, 7.95) * mm});
            skLineSegment(sketch, "E100.6.65", {"start": v(6.85, 7.8) * mm, "end": v(6.86, 7.78) * mm});
            skLineSegment(sketch, "E100.6.66", {"start": v(7.06, 7.79) * mm, "end": v(7.08, 7.8) * mm});
            skLineSegment(sketch, "E100.6.67", {"start": v(7.27, 7.93) * mm, "end": v(7.31, 7.95) * mm});
            skLineSegment(sketch, "E100.6.68", {"start": v(7, 7.76) * mm, "end": v(7, 7.76) * mm});
            skLineSegment(sketch, "E100.6.69", {"start": v(6.77, 8.24) * mm, "end": v(6.8, 8.28) * mm});
            skLineSegment(sketch, "E100.6.70", {"start": v(6.9, 7.75) * mm, "end": v(6.91, 7.75) * mm});
            skLineSegment(sketch, "E100.6.71", {"start": v(7.04, 7.77) * mm, "end": v(7.05, 7.78) * mm});
            skLineSegment(sketch, "E100.6.72", {"start": v(6.92, 7.75) * mm, "end": v(6.93, 7.75) * mm});
            skLineSegment(sketch, "E100.6.73", {"start": v(6.75, 8.2) * mm, "end": v(6.77, 8.24) * mm});
            skLineSegment(sketch, "E100.6.74", {"start": v(6.7, 7.94) * mm, "end": v(6.69, 7.94) * mm});
            skLineSegment(sketch, "E100.6.75", {"start": v(6.7, 7.93) * mm, "end": v(6.7, 7.94) * mm});
            skLineSegment(sketch, "E100.6.76", {"start": v(6.76, 7.87) * mm, "end": v(6.74, 7.89) * mm});
            skLineSegment(sketch, "E100.6.77", {"start": v(6.98, 7.75) * mm, "end": v(7, 7.76) * mm});
            skLineSegment(sketch, "E100.6.78", {"start": v(6.69, 8.04) * mm, "end": v(6.69, 8.06) * mm});
            skLineSegment(sketch, "E100.6.79", {"start": v(7.11, 7.82) * mm, "end": v(7.15, 7.85) * mm});
            skLineSegment(sketch, "E100.6.80", {"start": v(6.93, 7.75) * mm, "end": v(6.94, 7.75) * mm});
            skLineSegment(sketch, "E100.6.81", {"start": v(6.7, 7.92) * mm, "end": v(6.7, 7.93) * mm});
            skLineSegment(sketch, "E100.6.82", {"start": v(7.1, 7.8) * mm, "end": v(7.11, 7.82) * mm});
            skLineSegment(sketch, "E100.6.83", {"start": v(6.78, 7.86) * mm, "end": v(6.76, 7.87) * mm});
            skLineSegment(sketch, "E100.6.84", {"start": v(6.7, 8.07) * mm, "end": v(6.7, 8.09) * mm});
            skLineSegment(sketch, "E100.6.85", {"start": v(6.96, 7.75) * mm, "end": v(6.97, 7.75) * mm});
            skLineSegment(sketch, "E100.6.86", {"start": v(6.8, 7.84) * mm, "end": v(6.78, 7.86) * mm});
            skLineSegment(sketch, "E100.6.87", {"start": v(6.71, 8.12) * mm, "end": v(6.72, 8.13) * mm});
            skLineSegment(sketch, "E100.6.88", {"start": v(6.7, 7.92) * mm, "end": v(6.7, 7.92) * mm});
            skLineSegment(sketch, "E100.6.89", {"start": v(6.72, 7.9) * mm, "end": v(6.7, 7.92) * mm});
            skLineSegment(sketch, "E100.6.90", {"start": v(6.88, 7.76) * mm, "end": v(6.89, 7.76) * mm});
            skLineSegment(sketch, "E100.6.91", {"start": v(6.91, 7.75) * mm, "end": v(6.92, 7.75) * mm});
            skLineSegment(sketch, "E100.6.92", {"start": v(6.95, 7.75) * mm, "end": v(6.96, 7.75) * mm});
            skLineSegment(sketch, "E100.6.93", {"start": v(6.83, 7.81) * mm, "end": v(6.85, 7.8) * mm});
            skLineSegment(sketch, "E100.6.94", {"start": v(6.74, 7.89) * mm, "end": v(6.72, 7.9) * mm});
            skLineSegment(sketch, "E100.6.95", {"start": v(6.68, 8) * mm, "end": v(6.68, 8) * mm});
            skLineSegment(sketch, "E100.6.96", {"start": v(6.9, 7.75) * mm, "end": v(6.9, 7.75) * mm});
            skLineSegment(sketch, "E100.6.97", {"start": v(6.68, 7.98) * mm, "end": v(6.68, 8) * mm});
            skLineSegment(sketch, "E100.6.98", {"start": v(6.68, 8) * mm, "end": v(6.68, 8.02) * mm});
            skLineSegment(sketch, "E100.6.99", {"start": v(6.68, 8.02) * mm, "end": v(6.68, 8.03) * mm});
            skLineSegment(sketch, "E100.7.0", {"start": v(6.77, 9.3) * mm, "end": v(6.8, 9.27) * mm});
            skLineSegment(sketch, "E100.7.1", {"start": v(5.61, 10.04) * mm, "end": v(5.58, 10.06) * mm});
            skLineSegment(sketch, "E100.7.2", {"start": v(5.67, 9.85) * mm, "end": v(5.67, 9.9) * mm});
            skLineSegment(sketch, "E100.7.3", {"start": v(5.55, 10.07) * mm, "end": v(5.51, 10.1) * mm});
            skLineSegment(sketch, "E100.7.4", {"start": v(6.34, 9.08) * mm, "end": v(6.39, 9.11) * mm});
            skLineSegment(sketch, "E100.7.5", {"start": v(6.83, 9.25) * mm, "end": v(6.86, 9.23) * mm});
            skLineSegment(sketch, "E100.7.6", {"start": v(5.65, 10.02) * mm, "end": v(5.61, 10.04) * mm});
            skLineSegment(sketch, "E100.7.7", {"start": v(6.56, 9.22) * mm, "end": v(6.6, 9.24) * mm});
            skLineSegment(sketch, "E100.7.8", {"start": v(5.58, 10.06) * mm, "end": v(5.55, 10.07) * mm});
            skLineSegment(sketch, "E100.7.9", {"start": v(6.6, 9.24) * mm, "end": v(6.65, 9.27) * mm});
            skLineSegment(sketch, "E100.7.10", {"start": v(6.86, 9.23) * mm, "end": v(6.9, 9.2) * mm});
            skLineSegment(sketch, "E100.7.11", {"start": v(6.65, 9.27) * mm, "end": v(6.7, 9.3) * mm});
            skLineSegment(sketch, "E100.7.12", {"start": v(6.51, 9.2) * mm, "end": v(6.56, 9.22) * mm});
            skLineSegment(sketch, "E100.7.13", {"start": v(5.68, 9.95) * mm, "end": v(5.68, 10) * mm});
            skLineSegment(sketch, "E100.7.14", {"start": v(6.74, 9.32) * mm, "end": v(6.77, 9.3) * mm});
            skLineSegment(sketch, "E100.7.15", {"start": v(6.39, 9.11) * mm, "end": v(6.43, 9.14) * mm});
            skLineSegment(sketch, "E100.7.16", {"start": v(6.8, 9.27) * mm, "end": v(6.83, 9.25) * mm});
            skLineSegment(sketch, "E100.7.17", {"start": v(5.68, 10) * mm, "end": v(5.65, 10.02) * mm});
            skLineSegment(sketch, "E100.7.18", {"start": v(5.66, 9.74) * mm, "end": v(5.66, 9.8) * mm});
            skLineSegment(sketch, "E100.7.19", {"start": v(6.47, 9.17) * mm, "end": v(6.51, 9.2) * mm});
            skLineSegment(sketch, "E100.7.20", {"start": v(6.7, 9.3) * mm, "end": v(6.74, 9.32) * mm});
            skLineSegment(sketch, "E100.7.21", {"start": v(5.64, 9.6) * mm, "end": v(5.64, 9.64) * mm});
            skLineSegment(sketch, "E100.7.22", {"start": v(5.66, 9.8) * mm, "end": v(5.67, 9.85) * mm});
            skLineSegment(sketch, "E100.7.23", {"start": v(6.43, 9.14) * mm, "end": v(6.47, 9.17) * mm});
            skLineSegment(sketch, "E100.7.24", {"start": v(5.64, 9.64) * mm, "end": v(5.65, 9.7) * mm});
            skLineSegment(sketch, "E100.7.25", {"start": v(5.65, 9.7) * mm, "end": v(5.66, 9.74) * mm});
            skLineSegment(sketch, "E100.7.26", {"start": v(5.67, 9.9) * mm, "end": v(5.68, 9.95) * mm});
            skLineSegment(sketch, "E100.7.27", {"start": v(5.63, 9.55) * mm, "end": v(5.64, 9.6) * mm});
            skLineSegment(sketch, "E100.7.28", {"start": v(5.47, 8.9) * mm, "end": v(5.47, 8.91) * mm});
            skLineSegment(sketch, "E100.7.29", {"start": v(5.54, 9.16) * mm, "end": v(5.56, 9.2) * mm});
            skLineSegment(sketch, "E100.7.30", {"start": v(5.58, 9.3) * mm, "end": v(5.6, 9.35) * mm});
            skLineSegment(sketch, "E100.7.31", {"start": v(5.84, 8.69) * mm, "end": v(5.86, 8.7) * mm});
            skLineSegment(sketch, "E100.7.32", {"start": v(6.3, 9.06) * mm, "end": v(6.34, 9.08) * mm});
            skLineSegment(sketch, "E100.7.33", {"start": v(5.48, 8.84) * mm, "end": v(5.47, 8.85) * mm});
            skLineSegment(sketch, "E100.7.34", {"start": v(5.77, 8.65) * mm, "end": v(5.78, 8.66) * mm});
            skLineSegment(sketch, "E100.7.35", {"start": v(5.47, 8.93) * mm, "end": v(5.48, 8.94) * mm});
            skLineSegment(sketch, "E100.7.36", {"start": v(5.5, 9.03) * mm, "end": v(5.51, 9.07) * mm});
            skLineSegment(sketch, "E100.7.37", {"start": v(6.22, 9) * mm, "end": v(6.26, 9.03) * mm});
            skLineSegment(sketch, "E100.7.38", {"start": v(6, 8.82) * mm, "end": v(6.03, 8.85) * mm});
            skLineSegment(sketch, "E100.7.39", {"start": v(6.1, 8.91) * mm, "end": v(6.14, 8.94) * mm});
            skLineSegment(sketch, "E100.7.40", {"start": v(5.6, 8.73) * mm, "end": v(5.63, 8.72) * mm});
            skLineSegment(sketch, "E100.7.41", {"start": v(5.63, 8.72) * mm, "end": v(5.65, 8.7) * mm});
            skLineSegment(sketch, "E100.7.42", {"start": v(5.6, 9.4) * mm, "end": v(5.61, 9.45) * mm});
            skLineSegment(sketch, "E100.7.43", {"start": v(5.6, 9.35) * mm, "end": v(5.6, 9.4) * mm});
            skLineSegment(sketch, "E100.7.44", {"start": v(6.26, 9.03) * mm, "end": v(6.3, 9.06) * mm});
            skLineSegment(sketch, "E100.7.45", {"start": v(5.8, 8.66) * mm, "end": v(5.8, 8.67) * mm});
            skLineSegment(sketch, "E100.7.46", {"start": v(5.71, 8.66) * mm, "end": v(5.72, 8.66) * mm});
            skLineSegment(sketch, "E100.7.47", {"start": v(6.14, 8.94) * mm, "end": v(6.18, 8.97) * mm});
            skLineSegment(sketch, "E100.7.48", {"start": v(5.62, 9.5) * mm, "end": v(5.63, 9.55) * mm});
            skLineSegment(sketch, "E100.7.49", {"start": v(5.48, 8.96) * mm, "end": v(5.48, 8.97) * mm});
            skLineSegment(sketch, "E100.7.50", {"start": v(6.18, 8.97) * mm, "end": v(6.22, 9) * mm});
            skLineSegment(sketch, "E100.7.51", {"start": v(5.96, 8.78) * mm, "end": v(6, 8.82) * mm});
            skLineSegment(sketch, "E100.7.52", {"start": v(5.48, 8.83) * mm, "end": v(5.48, 8.84) * mm});
            skLineSegment(sketch, "E100.7.53", {"start": v(5.57, 9.26) * mm, "end": v(5.58, 9.3) * mm});
            skLineSegment(sketch, "E100.7.54", {"start": v(5.87, 8.7) * mm, "end": v(5.88, 8.72) * mm});
            skLineSegment(sketch, "E100.7.55", {"start": v(5.69, 8.68) * mm, "end": v(5.7, 8.66) * mm});
            skLineSegment(sketch, "E100.7.56", {"start": v(5.83, 8.68) * mm, "end": v(5.84, 8.69) * mm});
            skLineSegment(sketch, "E100.7.57", {"start": v(5.48, 8.82) * mm, "end": v(5.48, 8.83) * mm});
            skLineSegment(sketch, "E100.7.58", {"start": v(5.9, 8.73) * mm, "end": v(5.91, 8.74) * mm});
            skLineSegment(sketch, "E100.7.59", {"start": v(5.48, 8.97) * mm, "end": v(5.49, 8.99) * mm});
            skLineSegment(sketch, "E100.7.60", {"start": v(6.03, 8.85) * mm, "end": v(6.07, 8.88) * mm});
            skLineSegment(sketch, "E100.7.61", {"start": v(5.61, 9.45) * mm, "end": v(5.62, 9.5) * mm});
            skLineSegment(sketch, "E100.7.62", {"start": v(5.56, 9.2) * mm, "end": v(5.57, 9.26) * mm});
            skLineSegment(sketch, "E100.7.63", {"start": v(5.5, 9) * mm, "end": v(5.5, 9.03) * mm});
            skLineSegment(sketch, "E100.7.64", {"start": v(5.49, 8.81) * mm, "end": v(5.48, 8.82) * mm});
            skLineSegment(sketch, "E100.7.65", {"start": v(5.67, 8.69) * mm, "end": v(5.69, 8.68) * mm});
            skLineSegment(sketch, "E100.7.66", {"start": v(5.88, 8.72) * mm, "end": v(5.9, 8.73) * mm});
            skLineSegment(sketch, "E100.7.67", {"start": v(6.07, 8.88) * mm, "end": v(6.1, 8.91) * mm});
            skLineSegment(sketch, "E100.7.68", {"start": v(5.82, 8.67) * mm, "end": v(5.83, 8.68) * mm});
            skLineSegment(sketch, "E100.7.69", {"start": v(5.53, 9.12) * mm, "end": v(5.54, 9.16) * mm});
            skLineSegment(sketch, "E100.7.70", {"start": v(5.73, 8.65) * mm, "end": v(5.74, 8.65) * mm});
            skLineSegment(sketch, "E100.7.71", {"start": v(5.86, 8.7) * mm, "end": v(5.87, 8.7) * mm});
            skLineSegment(sketch, "E100.7.72", {"start": v(5.75, 8.65) * mm, "end": v(5.76, 8.65) * mm});
            skLineSegment(sketch, "E100.7.73", {"start": v(5.51, 9.07) * mm, "end": v(5.53, 9.12) * mm});
            skLineSegment(sketch, "E100.7.74", {"start": v(5.5, 8.8) * mm, "end": v(5.49, 8.81) * mm});
            skLineSegment(sketch, "E100.7.75", {"start": v(5.5, 8.8) * mm, "end": v(5.5, 8.8) * mm});
            skLineSegment(sketch, "E100.7.76", {"start": v(5.57, 8.75) * mm, "end": v(5.55, 8.77) * mm});
            skLineSegment(sketch, "E100.7.77", {"start": v(5.8, 8.67) * mm, "end": v(5.82, 8.67) * mm});
            skLineSegment(sketch, "E100.7.78", {"start": v(5.47, 8.91) * mm, "end": v(5.47, 8.93) * mm});
            skLineSegment(sketch, "E100.7.79", {"start": v(5.93, 8.75) * mm, "end": v(5.96, 8.78) * mm});
            skLineSegment(sketch, "E100.7.80", {"start": v(5.76, 8.65) * mm, "end": v(5.77, 8.65) * mm});
            skLineSegment(sketch, "E100.7.81", {"start": v(5.5, 8.8) * mm, "end": v(5.5, 8.8) * mm});
            skLineSegment(sketch, "E100.7.82", {"start": v(5.91, 8.74) * mm, "end": v(5.93, 8.75) * mm});
            skLineSegment(sketch, "E100.7.83", {"start": v(5.59, 8.74) * mm, "end": v(5.57, 8.75) * mm});
            skLineSegment(sketch, "E100.7.84", {"start": v(5.48, 8.94) * mm, "end": v(5.48, 8.96) * mm});
            skLineSegment(sketch, "E100.7.85", {"start": v(5.79, 8.66) * mm, "end": v(5.8, 8.66) * mm});
            skLineSegment(sketch, "E100.7.86", {"start": v(5.6, 8.73) * mm, "end": v(5.59, 8.74) * mm});
            skLineSegment(sketch, "E100.7.87", {"start": v(5.49, 8.99) * mm, "end": v(5.5, 9) * mm});
            skLineSegment(sketch, "E100.7.88", {"start": v(5.51, 8.8) * mm, "end": v(5.5, 8.8) * mm});
            skLineSegment(sketch, "E100.7.89", {"start": v(5.53, 8.78) * mm, "end": v(5.51, 8.8) * mm});
            skLineSegment(sketch, "E100.7.90", {"start": v(5.7, 8.66) * mm, "end": v(5.71, 8.66) * mm});
            skLineSegment(sketch, "E100.7.91", {"start": v(5.74, 8.65) * mm, "end": v(5.75, 8.65) * mm});
            skLineSegment(sketch, "E100.7.92", {"start": v(5.78, 8.66) * mm, "end": v(5.79, 8.66) * mm});
            skLineSegment(sketch, "E100.7.93", {"start": v(5.65, 8.7) * mm, "end": v(5.67, 8.69) * mm});
            skLineSegment(sketch, "E100.7.94", {"start": v(5.55, 8.77) * mm, "end": v(5.53, 8.78) * mm});
            skLineSegment(sketch, "E100.7.95", {"start": v(5.47, 8.86) * mm, "end": v(5.47, 8.87) * mm});
            skLineSegment(sketch, "E100.7.96", {"start": v(5.72, 8.66) * mm, "end": v(5.73, 8.65) * mm});
            skLineSegment(sketch, "E100.7.97", {"start": v(5.47, 8.85) * mm, "end": v(5.47, 8.86) * mm});
            skLineSegment(sketch, "E100.7.98", {"start": v(5.47, 8.87) * mm, "end": v(5.47, 8.88) * mm});
            skLineSegment(sketch, "E100.7.99", {"start": v(5.47, 8.88) * mm, "end": v(5.47, 8.9) * mm});
            skLineSegment(sketch, "E100.8.0", {"start": v(5.38, 10.17) * mm, "end": v(5.41, 10.15) * mm});
            skLineSegment(sketch, "E100.8.1", {"start": v(4.13, 10.73) * mm, "end": v(4.1, 10.75) * mm});
            skLineSegment(sketch, "E100.8.2", {"start": v(4.2, 10.55) * mm, "end": v(4.2, 10.6) * mm});
            skLineSegment(sketch, "E100.8.3", {"start": v(4.05, 10.76) * mm, "end": v(4.02, 10.77) * mm});
            skLineSegment(sketch, "E100.8.4", {"start": v(4.99, 9.9) * mm, "end": v(5.02, 9.93) * mm});
            skLineSegment(sketch, "E100.8.5", {"start": v(5.44, 10.13) * mm, "end": v(5.48, 10.11) * mm});
            skLineSegment(sketch, "E100.8.6", {"start": v(4.16, 10.72) * mm, "end": v(4.13, 10.73) * mm});
            skLineSegment(sketch, "E100.8.7", {"start": v(5.18, 10.06) * mm, "end": v(5.22, 10.1) * mm});
            skLineSegment(sketch, "E100.8.8", {"start": v(4.1, 10.75) * mm, "end": v(4.05, 10.76) * mm});
            skLineSegment(sketch, "E100.8.9", {"start": v(5.22, 10.1) * mm, "end": v(5.26, 10.12) * mm});
            skLineSegment(sketch, "E100.8.10", {"start": v(5.48, 10.11) * mm, "end": v(5.51, 10.1) * mm});
            skLineSegment(sketch, "E100.8.11", {"start": v(5.26, 10.12) * mm, "end": v(5.3, 10.15) * mm});
            skLineSegment(sketch, "E100.8.12", {"start": v(5.14, 10.03) * mm, "end": v(5.18, 10.06) * mm});
            skLineSegment(sketch, "E100.8.13", {"start": v(4.2, 10.65) * mm, "end": v(4.2, 10.7) * mm});
            skLineSegment(sketch, "E100.8.14", {"start": v(5.34, 10.18) * mm, "end": v(5.38, 10.17) * mm});
            skLineSegment(sketch, "E100.8.15", {"start": v(5.02, 9.93) * mm, "end": v(5.06, 9.96) * mm});
            skLineSegment(sketch, "E100.8.16", {"start": v(5.41, 10.15) * mm, "end": v(5.44, 10.13) * mm});
            skLineSegment(sketch, "E100.8.17", {"start": v(4.2, 10.7) * mm, "end": v(4.16, 10.72) * mm});
            skLineSegment(sketch, "E100.8.18", {"start": v(4.21, 10.45) * mm, "end": v(4.21, 10.5) * mm});
            skLineSegment(sketch, "E100.8.19", {"start": v(5.1, 10) * mm, "end": v(5.14, 10.03) * mm});
            skLineSegment(sketch, "E100.8.20", {"start": v(5.3, 10.15) * mm, "end": v(5.34, 10.18) * mm});
            skLineSegment(sketch, "E100.8.21", {"start": v(4.21, 10.3) * mm, "end": v(4.21, 10.35) * mm});
            skLineSegment(sketch, "E100.8.22", {"start": v(4.21, 10.5) * mm, "end": v(4.2, 10.55) * mm});
            skLineSegment(sketch, "E100.8.23", {"start": v(5.06, 9.96) * mm, "end": v(5.1, 10) * mm});
            skLineSegment(sketch, "E100.8.24", {"start": v(4.21, 10.35) * mm, "end": v(4.21, 10.4) * mm});
            skLineSegment(sketch, "E100.8.25", {"start": v(4.21, 10.4) * mm, "end": v(4.21, 10.45) * mm});
            skLineSegment(sketch, "E100.8.26", {"start": v(4.2, 10.6) * mm, "end": v(4.2, 10.65) * mm});
            skLineSegment(sketch, "E100.8.27", {"start": v(4.21, 10.25) * mm, "end": v(4.21, 10.3) * mm});
            skLineSegment(sketch, "E100.8.28", {"start": v(4.15, 9.59) * mm, "end": v(4.15, 9.6) * mm});
            skLineSegment(sketch, "E100.8.29", {"start": v(4.18, 9.86) * mm, "end": v(4.19, 9.9) * mm});
            skLineSegment(sketch, "E100.8.30", {"start": v(4.2, 10) * mm, "end": v(4.2, 10.05) * mm});
            skLineSegment(sketch, "E100.8.31", {"start": v(4.55, 9.43) * mm, "end": v(4.56, 9.44) * mm});
            skLineSegment(sketch, "E100.8.32", {"start": v(4.95, 9.86) * mm, "end": v(4.99, 9.9) * mm});
            skLineSegment(sketch, "E100.8.33", {"start": v(4.16, 9.53) * mm, "end": v(4.16, 9.54) * mm});
            skLineSegment(sketch, "E100.8.34", {"start": v(4.48, 9.39) * mm, "end": v(4.48, 9.4) * mm});
            skLineSegment(sketch, "E100.8.35", {"start": v(4.15, 9.61) * mm, "end": v(4.15, 9.63) * mm});
            skLineSegment(sketch, "E100.8.36", {"start": v(4.16, 9.72) * mm, "end": v(4.17, 9.76) * mm});
            skLineSegment(sketch, "E100.8.37", {"start": v(4.88, 9.8) * mm, "end": v(4.91, 9.83) * mm});
            skLineSegment(sketch, "E100.8.38", {"start": v(4.68, 9.58) * mm, "end": v(4.71, 9.62) * mm});
            skLineSegment(sketch, "E100.8.39", {"start": v(4.78, 9.69) * mm, "end": v(4.8, 9.72) * mm});
            skLineSegment(sketch, "E100.8.40", {"start": v(4.3, 9.44) * mm, "end": v(4.33, 9.43) * mm});
            skLineSegment(sketch, "E100.8.41", {"start": v(4.33, 9.43) * mm, "end": v(4.35, 9.42) * mm});
            skLineSegment(sketch, "E100.8.42", {"start": v(4.2, 10.1) * mm, "end": v(4.2, 10.15) * mm});
            skLineSegment(sketch, "E100.8.43", {"start": v(4.2, 10.05) * mm, "end": v(4.2, 10.1) * mm});
            skLineSegment(sketch, "E100.8.44", {"start": v(4.91, 9.83) * mm, "end": v(4.95, 9.86) * mm});
            skLineSegment(sketch, "E100.8.45", {"start": v(4.5, 9.4) * mm, "end": v(4.52, 9.4) * mm});
            skLineSegment(sketch, "E100.8.46", {"start": v(4.42, 9.39) * mm, "end": v(4.43, 9.38) * mm});
            skLineSegment(sketch, "E100.8.47", {"start": v(4.8, 9.72) * mm, "end": v(4.84, 9.76) * mm});
            skLineSegment(sketch, "E100.8.48", {"start": v(4.21, 10.2) * mm, "end": v(4.21, 10.25) * mm});
            skLineSegment(sketch, "E100.8.49", {"start": v(4.15, 9.65) * mm, "end": v(4.15, 9.66) * mm});
            skLineSegment(sketch, "E100.8.50", {"start": v(4.84, 9.76) * mm, "end": v(4.88, 9.8) * mm});
            skLineSegment(sketch, "E100.8.51", {"start": v(4.65, 9.54) * mm, "end": v(4.68, 9.58) * mm});
            skLineSegment(sketch, "E100.8.52", {"start": v(4.17, 9.52) * mm, "end": v(4.16, 9.53) * mm});
            skLineSegment(sketch, "E100.8.53", {"start": v(4.2, 9.95) * mm, "end": v(4.2, 10) * mm});
            skLineSegment(sketch, "E100.8.54", {"start": v(4.57, 9.45) * mm, "end": v(4.58, 9.46) * mm});
            skLineSegment(sketch, "E100.8.55", {"start": v(4.4, 9.4) * mm, "end": v(4.42, 9.39) * mm});
            skLineSegment(sketch, "E100.8.56", {"start": v(4.54, 9.42) * mm, "end": v(4.55, 9.43) * mm});
            skLineSegment(sketch, "E100.8.57", {"start": v(4.17, 9.51) * mm, "end": v(4.17, 9.52) * mm});
            skLineSegment(sketch, "E100.8.58", {"start": v(4.6, 9.48) * mm, "end": v(4.6, 9.5) * mm});
            skLineSegment(sketch, "E100.8.59", {"start": v(4.15, 9.66) * mm, "end": v(4.15, 9.68) * mm});
            skLineSegment(sketch, "E100.8.60", {"start": v(4.71, 9.62) * mm, "end": v(4.74, 9.65) * mm});
            skLineSegment(sketch, "E100.8.61", {"start": v(4.2, 10.15) * mm, "end": v(4.21, 10.2) * mm});
            skLineSegment(sketch, "E100.8.62", {"start": v(4.19, 9.9) * mm, "end": v(4.2, 9.95) * mm});
            skLineSegment(sketch, "E100.8.63", {"start": v(4.16, 9.7) * mm, "end": v(4.16, 9.72) * mm});
            skLineSegment(sketch, "E100.8.64", {"start": v(4.18, 9.5) * mm, "end": v(4.17, 9.51) * mm});
            skLineSegment(sketch, "E100.8.65", {"start": v(4.37, 9.4) * mm, "end": v(4.4, 9.4) * mm});
            skLineSegment(sketch, "E100.8.66", {"start": v(4.58, 9.46) * mm, "end": v(4.6, 9.48) * mm});
            skLineSegment(sketch, "E100.8.67", {"start": v(4.74, 9.65) * mm, "end": v(4.78, 9.69) * mm});
            skLineSegment(sketch, "E100.8.68", {"start": v(4.53, 9.41) * mm, "end": v(4.54, 9.42) * mm});
            skLineSegment(sketch, "E100.8.69", {"start": v(4.18, 9.81) * mm, "end": v(4.18, 9.86) * mm});
            skLineSegment(sketch, "E100.8.70", {"start": v(4.44, 9.38) * mm, "end": v(4.45, 9.38) * mm});
            skLineSegment(sketch, "E100.8.71", {"start": v(4.56, 9.44) * mm, "end": v(4.57, 9.45) * mm});
            skLineSegment(sketch, "E100.8.72", {"start": v(4.46, 9.38) * mm, "end": v(4.47, 9.38) * mm});
            skLineSegment(sketch, "E100.8.73", {"start": v(4.17, 9.76) * mm, "end": v(4.18, 9.81) * mm});
            skLineSegment(sketch, "E100.8.74", {"start": v(4.18, 9.5) * mm, "end": v(4.18, 9.5) * mm});
            skLineSegment(sketch, "E100.8.75", {"start": v(4.19, 9.5) * mm, "end": v(4.18, 9.5) * mm});
            skLineSegment(sketch, "E100.8.76", {"start": v(4.27, 9.46) * mm, "end": v(4.25, 9.47) * mm});
            skLineSegment(sketch, "E100.8.77", {"start": v(4.52, 9.4) * mm, "end": v(4.53, 9.41) * mm});
            skLineSegment(sketch, "E100.8.78", {"start": v(4.15, 9.6) * mm, "end": v(4.15, 9.61) * mm});
            skLineSegment(sketch, "E100.8.79", {"start": v(4.62, 9.5) * mm, "end": v(4.65, 9.54) * mm});
            skLineSegment(sketch, "E100.8.80", {"start": v(4.47, 9.38) * mm, "end": v(4.48, 9.39) * mm});
            skLineSegment(sketch, "E100.8.81", {"start": v(4.2, 9.49) * mm, "end": v(4.19, 9.5) * mm});
            skLineSegment(sketch, "E100.8.82", {"start": v(4.6, 9.5) * mm, "end": v(4.62, 9.5) * mm});
            skLineSegment(sketch, "E100.8.83", {"start": v(4.29, 9.45) * mm, "end": v(4.27, 9.46) * mm});
            skLineSegment(sketch, "E100.8.84", {"start": v(4.15, 9.63) * mm, "end": v(4.15, 9.65) * mm});
            skLineSegment(sketch, "E100.8.85", {"start": v(4.5, 9.4) * mm, "end": v(4.5, 9.4) * mm});
            skLineSegment(sketch, "E100.8.86", {"start": v(4.3, 9.44) * mm, "end": v(4.29, 9.45) * mm});
            skLineSegment(sketch, "E100.8.87", {"start": v(4.15, 9.68) * mm, "end": v(4.16, 9.7) * mm});
            skLineSegment(sketch, "E100.8.88", {"start": v(4.2, 9.49) * mm, "end": v(4.2, 9.49) * mm});
            skLineSegment(sketch, "E100.8.89", {"start": v(4.22, 9.48) * mm, "end": v(4.2, 9.49) * mm});
            skLineSegment(sketch, "E100.8.90", {"start": v(4.42, 9.39) * mm, "end": v(4.42, 9.39) * mm});
            skLineSegment(sketch, "E100.8.91", {"start": v(4.45, 9.38) * mm, "end": v(4.46, 9.38) * mm});
            skLineSegment(sketch, "E100.8.92", {"start": v(4.48, 9.4) * mm, "end": v(4.5, 9.4) * mm});
            skLineSegment(sketch, "E100.8.93", {"start": v(4.35, 9.42) * mm, "end": v(4.37, 9.4) * mm});
            skLineSegment(sketch, "E100.8.94", {"start": v(4.25, 9.47) * mm, "end": v(4.22, 9.48) * mm});
            skLineSegment(sketch, "E100.8.95", {"start": v(4.16, 9.55) * mm, "end": v(4.15, 9.56) * mm});
            skLineSegment(sketch, "E100.8.96", {"start": v(4.43, 9.38) * mm, "end": v(4.44, 9.38) * mm});
            skLineSegment(sketch, "E100.8.97", {"start": v(4.16, 9.54) * mm, "end": v(4.16, 9.55) * mm});
            skLineSegment(sketch, "E100.8.98", {"start": v(4.15, 9.56) * mm, "end": v(4.15, 9.57) * mm});
            skLineSegment(sketch, "E100.8.99", {"start": v(4.15, 9.57) * mm, "end": v(4.15, 9.59) * mm});
            skLineSegment(sketch, "E100.9.0", {"start": v(3.87, 10.83) * mm, "end": v(3.91, 10.81) * mm});
            skLineSegment(sketch, "E100.9.1", {"start": v(2.56, 11.21) * mm, "end": v(2.52, 11.22) * mm});
            skLineSegment(sketch, "E100.9.2", {"start": v(2.66, 11.04) * mm, "end": v(2.65, 11.1) * mm});
            skLineSegment(sketch, "E100.9.3", {"start": v(2.48, 11.23) * mm, "end": v(2.44, 11.24) * mm});
            skLineSegment(sketch, "E100.9.4", {"start": v(3.53, 10.5) * mm, "end": v(3.56, 10.54) * mm});
            skLineSegment(sketch, "E100.9.5", {"start": v(3.95, 10.8) * mm, "end": v(3.98, 10.79) * mm});
            skLineSegment(sketch, "E100.9.6", {"start": v(2.6, 11.2) * mm, "end": v(2.56, 11.21) * mm});
            skLineSegment(sketch, "E100.9.7", {"start": v(3.7, 10.7) * mm, "end": v(3.73, 10.73) * mm});
            skLineSegment(sketch, "E100.9.8", {"start": v(2.52, 11.22) * mm, "end": v(2.48, 11.23) * mm});
            skLineSegment(sketch, "E100.9.9", {"start": v(3.73, 10.73) * mm, "end": v(3.77, 10.77) * mm});
            skLineSegment(sketch, "E100.9.10", {"start": v(3.98, 10.79) * mm, "end": v(4.02, 10.77) * mm});
            skLineSegment(sketch, "E100.9.11", {"start": v(3.77, 10.77) * mm, "end": v(3.8, 10.8) * mm});
            skLineSegment(sketch, "E100.9.12", {"start": v(3.66, 10.66) * mm, "end": v(3.7, 10.7) * mm});
            skLineSegment(sketch, "E100.9.13", {"start": v(2.64, 11.14) * mm, "end": v(2.63, 11.2) * mm});
            skLineSegment(sketch, "E100.9.14", {"start": v(3.84, 10.84) * mm, "end": v(3.87, 10.83) * mm});
            skLineSegment(sketch, "E100.9.15", {"start": v(3.56, 10.54) * mm, "end": v(3.6, 10.58) * mm});
            skLineSegment(sketch, "E100.9.16", {"start": v(3.91, 10.81) * mm, "end": v(3.95, 10.8) * mm});
            skLineSegment(sketch, "E100.9.17", {"start": v(2.63, 11.2) * mm, "end": v(2.6, 11.2) * mm});
            skLineSegment(sketch, "E100.9.18", {"start": v(2.68, 10.94) * mm, "end": v(2.67, 11) * mm});
            skLineSegment(sketch, "E100.9.19", {"start": v(3.63, 10.62) * mm, "end": v(3.66, 10.66) * mm});
            skLineSegment(sketch, "E100.9.20", {"start": v(3.8, 10.8) * mm, "end": v(3.84, 10.84) * mm});
            skLineSegment(sketch, "E100.9.21", {"start": v(2.7, 10.8) * mm, "end": v(2.7, 10.84) * mm});
            skLineSegment(sketch, "E100.9.22", {"start": v(2.67, 11) * mm, "end": v(2.66, 11.04) * mm});
            skLineSegment(sketch, "E100.9.23", {"start": v(3.6, 10.58) * mm, "end": v(3.63, 10.62) * mm});
            skLineSegment(sketch, "E100.9.24", {"start": v(2.7, 10.84) * mm, "end": v(2.69, 10.9) * mm});
            skLineSegment(sketch, "E100.9.25", {"start": v(2.69, 10.9) * mm, "end": v(2.68, 10.94) * mm});
            skLineSegment(sketch, "E100.9.26", {"start": v(2.65, 11.1) * mm, "end": v(2.64, 11.14) * mm});
            skLineSegment(sketch, "E100.9.27", {"start": v(2.71, 10.74) * mm, "end": v(2.7, 10.8) * mm});
            skLineSegment(sketch, "E100.9.28", {"start": v(2.74, 10.08) * mm, "end": v(2.74, 10.1) * mm});
            skLineSegment(sketch, "E100.9.29", {"start": v(2.74, 10.35) * mm, "end": v(2.74, 10.4) * mm});
            skLineSegment(sketch, "E100.9.30", {"start": v(2.73, 10.5) * mm, "end": v(2.73, 10.55) * mm});
            skLineSegment(sketch, "E100.9.31", {"start": v(3.16, 9.98) * mm, "end": v(3.17, 10) * mm});
            skLineSegment(sketch, "E100.9.32", {"start": v(3.5, 10.47) * mm, "end": v(3.53, 10.5) * mm});
            skLineSegment(sketch, "E100.9.33", {"start": v(2.76, 10.02) * mm, "end": v(2.76, 10.03) * mm});
            skLineSegment(sketch, "E100.9.34", {"start": v(3.1, 9.93) * mm, "end": v(3.1, 9.93) * mm});
            skLineSegment(sketch, "E100.9.35", {"start": v(2.74, 10.1) * mm, "end": v(2.74, 10.12) * mm});
            skLineSegment(sketch, "E100.9.36", {"start": v(2.73, 10.2) * mm, "end": v(2.74, 10.26) * mm});
            skLineSegment(sketch, "E100.9.37", {"start": v(3.44, 10.39) * mm, "end": v(3.47, 10.43) * mm});
            skLineSegment(sketch, "E100.9.38", {"start": v(3.27, 10.15) * mm, "end": v(3.3, 10.19) * mm});
            skLineSegment(sketch, "E100.9.39", {"start": v(3.35, 10.27) * mm, "end": v(3.38, 10.3) * mm});
            skLineSegment(sketch, "E100.9.40", {"start": v(2.92, 9.95) * mm, "end": v(2.95, 9.95) * mm});
            skLineSegment(sketch, "E100.9.41", {"start": v(2.95, 9.95) * mm, "end": v(2.97, 9.94) * mm});
            skLineSegment(sketch, "E100.9.42", {"start": v(2.73, 10.6) * mm, "end": v(2.72, 10.65) * mm});
            skLineSegment(sketch, "E100.9.43", {"start": v(2.73, 10.55) * mm, "end": v(2.73, 10.6) * mm});
            skLineSegment(sketch, "E100.9.44", {"start": v(3.47, 10.43) * mm, "end": v(3.5, 10.47) * mm});
            skLineSegment(sketch, "E100.9.45", {"start": v(3.12, 9.95) * mm, "end": v(3.13, 9.95) * mm});
            skLineSegment(sketch, "E100.9.46", {"start": v(3.04, 9.92) * mm, "end": v(3.05, 9.92) * mm});
            skLineSegment(sketch, "E100.9.47", {"start": v(3.38, 10.3) * mm, "end": v(3.4, 10.35) * mm});
            skLineSegment(sketch, "E100.9.48", {"start": v(2.72, 10.7) * mm, "end": v(2.71, 10.74) * mm});
            skLineSegment(sketch, "E100.9.49", {"start": v(2.73, 10.14) * mm, "end": v(2.73, 10.15) * mm});
            skLineSegment(sketch, "E100.9.50", {"start": v(3.4, 10.35) * mm, "end": v(3.44, 10.39) * mm});
            skLineSegment(sketch, "E100.9.51", {"start": v(3.24, 10.1) * mm, "end": v(3.27, 10.15) * mm});
            skLineSegment(sketch, "E100.9.52", {"start": v(2.77, 10.02) * mm, "end": v(2.76, 10.02) * mm});
            skLineSegment(sketch, "E100.9.53", {"start": v(2.73, 10.45) * mm, "end": v(2.73, 10.5) * mm});
            skLineSegment(sketch, "E100.9.54", {"start": v(3.18, 10) * mm, "end": v(3.2, 10.02) * mm});
            skLineSegment(sketch, "E100.9.55", {"start": v(3.01, 9.93) * mm, "end": v(3.03, 9.92) * mm});
            skLineSegment(sketch, "E100.9.56", {"start": v(3.15, 9.97) * mm, "end": v(3.16, 9.98) * mm});
            skLineSegment(sketch, "E100.9.57", {"start": v(2.78, 10) * mm, "end": v(2.77, 10.02) * mm});
            skLineSegment(sketch, "E100.9.58", {"start": v(3.2, 10.03) * mm, "end": v(3.2, 10.05) * mm});
            skLineSegment(sketch, "E100.9.59", {"start": v(2.73, 10.15) * mm, "end": v(2.73, 10.17) * mm});
            skLineSegment(sketch, "E100.9.60", {"start": v(3.3, 10.19) * mm, "end": v(3.32, 10.23) * mm});
            skLineSegment(sketch, "E100.9.61", {"start": v(2.72, 10.65) * mm, "end": v(2.72, 10.7) * mm});
            skLineSegment(sketch, "E100.9.62", {"start": v(2.74, 10.4) * mm, "end": v(2.73, 10.45) * mm});
            skLineSegment(sketch, "E100.9.63", {"start": v(2.73, 10.2) * mm, "end": v(2.73, 10.2) * mm});
            skLineSegment(sketch, "E100.9.64", {"start": v(2.78, 10) * mm, "end": v(2.78, 10) * mm});
            skLineSegment(sketch, "E100.9.65", {"start": v(3, 9.93) * mm, "end": v(3.01, 9.93) * mm});
            skLineSegment(sketch, "E100.9.66", {"start": v(3.2, 10.02) * mm, "end": v(3.2, 10.03) * mm});
            skLineSegment(sketch, "E100.9.67", {"start": v(3.32, 10.23) * mm, "end": v(3.35, 10.27) * mm});
            skLineSegment(sketch, "E100.9.68", {"start": v(3.14, 9.96) * mm, "end": v(3.15, 9.97) * mm});
            skLineSegment(sketch, "E100.9.69", {"start": v(2.74, 10.3) * mm, "end": v(2.74, 10.35) * mm});
            skLineSegment(sketch, "E100.9.70", {"start": v(3.06, 9.92) * mm, "end": v(3.07, 9.92) * mm});
            skLineSegment(sketch, "E100.9.71", {"start": v(3.17, 10) * mm, "end": v(3.18, 10) * mm});
            skLineSegment(sketch, "E100.9.72", {"start": v(3.08, 9.92) * mm, "end": v(3.08, 9.92) * mm});
            skLineSegment(sketch, "E100.9.73", {"start": v(2.74, 10.26) * mm, "end": v(2.74, 10.3) * mm});
            skLineSegment(sketch, "E100.9.74", {"start": v(2.79, 10) * mm, "end": v(2.78, 10) * mm});
            skLineSegment(sketch, "E100.9.75", {"start": v(2.8, 10) * mm, "end": v(2.79, 10) * mm});
            skLineSegment(sketch, "E100.9.76", {"start": v(2.88, 9.97) * mm, "end": v(2.86, 9.97) * mm});
            skLineSegment(sketch, "E100.9.77", {"start": v(3.13, 9.95) * mm, "end": v(3.14, 9.96) * mm});
            skLineSegment(sketch, "E100.9.78", {"start": v(2.74, 10.1) * mm, "end": v(2.74, 10.1) * mm});
            skLineSegment(sketch, "E100.9.79", {"start": v(3.22, 10.07) * mm, "end": v(3.24, 10.1) * mm});
            skLineSegment(sketch, "E100.9.80", {"start": v(3.08, 9.92) * mm, "end": v(3.1, 9.93) * mm});
            skLineSegment(sketch, "E100.9.81", {"start": v(2.8, 9.99) * mm, "end": v(2.8, 10) * mm});
            skLineSegment(sketch, "E100.9.82", {"start": v(3.2, 10.05) * mm, "end": v(3.22, 10.07) * mm});
            skLineSegment(sketch, "E100.9.83", {"start": v(2.9, 9.96) * mm, "end": v(2.88, 9.97) * mm});
            skLineSegment(sketch, "E100.9.84", {"start": v(2.74, 10.12) * mm, "end": v(2.73, 10.14) * mm});
            skLineSegment(sketch, "E100.9.85", {"start": v(3.11, 9.94) * mm, "end": v(3.12, 9.95) * mm});
            skLineSegment(sketch, "E100.9.86", {"start": v(2.92, 9.95) * mm, "end": v(2.9, 9.96) * mm});
            skLineSegment(sketch, "E100.9.87", {"start": v(2.73, 10.17) * mm, "end": v(2.73, 10.2) * mm});
            skLineSegment(sketch, "E100.9.88", {"start": v(2.81, 9.99) * mm, "end": v(2.8, 9.99) * mm});
            skLineSegment(sketch, "E100.9.89", {"start": v(2.83, 9.98) * mm, "end": v(2.81, 9.99) * mm});
            skLineSegment(sketch, "E100.9.90", {"start": v(3.03, 9.92) * mm, "end": v(3.04, 9.92) * mm});
            skLineSegment(sketch, "E100.9.91", {"start": v(3.07, 9.92) * mm, "end": v(3.08, 9.92) * mm});
            skLineSegment(sketch, "E100.9.92", {"start": v(3.1, 9.93) * mm, "end": v(3.11, 9.94) * mm});
            skLineSegment(sketch, "E100.9.93", {"start": v(2.97, 9.94) * mm, "end": v(3, 9.93) * mm});
            skLineSegment(sketch, "E100.9.94", {"start": v(2.86, 9.97) * mm, "end": v(2.83, 9.98) * mm});
            skLineSegment(sketch, "E100.9.95", {"start": v(2.76, 10.04) * mm, "end": v(2.75, 10.05) * mm});
            skLineSegment(sketch, "E100.9.96", {"start": v(3.05, 9.92) * mm, "end": v(3.06, 9.92) * mm});
            skLineSegment(sketch, "E100.9.97", {"start": v(2.76, 10.03) * mm, "end": v(2.76, 10.04) * mm});
            skLineSegment(sketch, "E100.9.98", {"start": v(2.75, 10.05) * mm, "end": v(2.75, 10.07) * mm});
            skLineSegment(sketch, "E100.9.99", {"start": v(2.75, 10.07) * mm, "end": v(2.74, 10.08) * mm});
            skLineSegment(sketch, "E100.10.0", {"start": v(2.3, 11.27) * mm, "end": v(2.33, 11.26) * mm});
            skLineSegment(sketch, "E100.10.1", {"start": v(0.94, 11.46) * mm, "end": v(0.9, 11.46) * mm});
            skLineSegment(sketch, "E100.10.2", {"start": v(1.06, 11.31) * mm, "end": v(1.05, 11.36) * mm});
            skLineSegment(sketch, "E100.10.3", {"start": v(0.86, 11.47) * mm, "end": v(0.82, 11.47) * mm});
            skLineSegment(sketch, "E100.10.4", {"start": v(2, 10.9) * mm, "end": v(2.02, 10.94) * mm});
            skLineSegment(sketch, "E100.10.5", {"start": v(2.37, 11.25) * mm, "end": v(2.4, 11.25) * mm});
            skLineSegment(sketch, "E100.10.6", {"start": v(0.97, 11.46) * mm, "end": v(0.94, 11.46) * mm});
            skLineSegment(sketch, "E100.10.7", {"start": v(2.14, 11.11) * mm, "end": v(2.17, 11.15) * mm});
            skLineSegment(sketch, "E100.10.8", {"start": v(0.9, 11.46) * mm, "end": v(0.86, 11.47) * mm});
            skLineSegment(sketch, "E100.10.9", {"start": v(2.17, 11.15) * mm, "end": v(2.2, 11.2) * mm});
            skLineSegment(sketch, "E100.10.10", {"start": v(2.4, 11.25) * mm, "end": v(2.44, 11.24) * mm});
            skLineSegment(sketch, "E100.10.11", {"start": v(2.2, 11.2) * mm, "end": v(2.23, 11.24) * mm});
            skLineSegment(sketch, "E100.10.12", {"start": v(2.1, 11.07) * mm, "end": v(2.14, 11.11) * mm});
            skLineSegment(sketch, "E100.10.13", {"start": v(1.03, 11.4) * mm, "end": v(1.01, 11.46) * mm});
            skLineSegment(sketch, "E100.10.14", {"start": v(2.26, 11.28) * mm, "end": v(2.3, 11.27) * mm});
            skLineSegment(sketch, "E100.10.15", {"start": v(2.02, 10.94) * mm, "end": v(2.05, 10.98) * mm});
            skLineSegment(sketch, "E100.10.16", {"start": v(2.33, 11.26) * mm, "end": v(2.37, 11.25) * mm});
            skLineSegment(sketch, "E100.10.17", {"start": v(1.01, 11.46) * mm, "end": v(0.97, 11.46) * mm});
            skLineSegment(sketch, "E100.10.18", {"start": v(1.1, 11.21) * mm, "end": v(1.08, 11.26) * mm});
            skLineSegment(sketch, "E100.10.19", {"start": v(2.08, 11.03) * mm, "end": v(2.1, 11.07) * mm});
            skLineSegment(sketch, "E100.10.20", {"start": v(2.23, 11.24) * mm, "end": v(2.26, 11.28) * mm});
            skLineSegment(sketch, "E100.10.21", {"start": v(1.14, 11.07) * mm, "end": v(1.13, 11.12) * mm});
            skLineSegment(sketch, "E100.10.22", {"start": v(1.08, 11.26) * mm, "end": v(1.06, 11.31) * mm});
            skLineSegment(sketch, "E100.10.23", {"start": v(2.05, 10.98) * mm, "end": v(2.08, 11.03) * mm});
            skLineSegment(sketch, "E100.10.24", {"start": v(1.13, 11.12) * mm, "end": v(1.11, 11.17) * mm});
            skLineSegment(sketch, "E100.10.25", {"start": v(1.11, 11.17) * mm, "end": v(1.1, 11.21) * mm});
            skLineSegment(sketch, "E100.10.26", {"start": v(1.05, 11.36) * mm, "end": v(1.03, 11.4) * mm});
            skLineSegment(sketch, "E100.10.27", {"start": v(1.15, 11.02) * mm, "end": v(1.14, 11.07) * mm});
            skLineSegment(sketch, "E100.10.28", {"start": v(1.28, 10.37) * mm, "end": v(1.28, 10.38) * mm});
            skLineSegment(sketch, "E100.10.29", {"start": v(1.24, 10.64) * mm, "end": v(1.23, 10.69) * mm});
            skLineSegment(sketch, "E100.10.30", {"start": v(1.21, 10.78) * mm, "end": v(1.2, 10.83) * mm});
            skLineSegment(sketch, "E100.10.31", {"start": v(1.7, 10.33) * mm, "end": v(1.72, 10.34) * mm});
            skLineSegment(sketch, "E100.10.32", {"start": v(1.97, 10.86) * mm, "end": v(2, 10.9) * mm});
            skLineSegment(sketch, "E100.10.33", {"start": v(1.31, 10.32) * mm, "end": v(1.3, 10.32) * mm});
            skLineSegment(sketch, "E100.10.34", {"start": v(1.65, 10.27) * mm, "end": v(1.66, 10.27) * mm});
            skLineSegment(sketch, "E100.10.35", {"start": v(1.27, 10.4) * mm, "end": v(1.27, 10.4) * mm});
            skLineSegment(sketch, "E100.10.36", {"start": v(1.25, 10.5) * mm, "end": v(1.25, 10.54) * mm});
            skLineSegment(sketch, "E100.10.37", {"start": v(1.92, 10.77) * mm, "end": v(1.95, 10.81) * mm});
            skLineSegment(sketch, "E100.10.38", {"start": v(1.8, 10.51) * mm, "end": v(1.81, 10.55) * mm});
            skLineSegment(sketch, "E100.10.39", {"start": v(1.85, 10.64) * mm, "end": v(1.88, 10.69) * mm});
            skLineSegment(sketch, "E100.10.40", {"start": v(1.48, 10.27) * mm, "end": v(1.5, 10.27) * mm});
            skLineSegment(sketch, "E100.10.41", {"start": v(1.5, 10.27) * mm, "end": v(1.52, 10.26) * mm});
            skLineSegment(sketch, "E100.10.42", {"start": v(1.2, 10.88) * mm, "end": v(1.18, 10.92) * mm});
            skLineSegment(sketch, "E100.10.43", {"start": v(1.2, 10.83) * mm, "end": v(1.2, 10.88) * mm});
            skLineSegment(sketch, "E100.10.44", {"start": v(1.95, 10.81) * mm, "end": v(1.97, 10.86) * mm});
            skLineSegment(sketch, "E100.10.45", {"start": v(1.67, 10.29) * mm, "end": v(1.68, 10.3) * mm});
            skLineSegment(sketch, "E100.10.46", {"start": v(1.6, 10.25) * mm, "end": v(1.6, 10.25) * mm});
            skLineSegment(sketch, "E100.10.47", {"start": v(1.88, 10.69) * mm, "end": v(1.9, 10.73) * mm});
            skLineSegment(sketch, "E100.10.48", {"start": v(1.17, 10.97) * mm, "end": v(1.15, 11.02) * mm});
            skLineSegment(sketch, "E100.10.49", {"start": v(1.26, 10.42) * mm, "end": v(1.26, 10.44) * mm});
            skLineSegment(sketch, "E100.10.50", {"start": v(1.9, 10.73) * mm, "end": v(1.92, 10.77) * mm});
            skLineSegment(sketch, "E100.10.51", {"start": v(1.77, 10.47) * mm, "end": v(1.8, 10.51) * mm});
            skLineSegment(sketch, "E100.10.52", {"start": v(1.32, 10.3) * mm, "end": v(1.31, 10.32) * mm});
            skLineSegment(sketch, "E100.10.53", {"start": v(1.22, 10.73) * mm, "end": v(1.21, 10.78) * mm});
            skLineSegment(sketch, "E100.10.54", {"start": v(1.72, 10.36) * mm, "end": v(1.73, 10.37) * mm});
            skLineSegment(sketch, "E100.10.55", {"start": v(1.57, 10.26) * mm, "end": v(1.6, 10.25) * mm});
            skLineSegment(sketch, "E100.10.56", {"start": v(1.7, 10.32) * mm, "end": v(1.7, 10.33) * mm});
            skLineSegment(sketch, "E100.10.57", {"start": v(1.32, 10.3) * mm, "end": v(1.32, 10.3) * mm});
            skLineSegment(sketch, "E100.10.58", {"start": v(1.74, 10.39) * mm, "end": v(1.75, 10.4) * mm});
            skLineSegment(sketch, "E100.10.59", {"start": v(1.26, 10.44) * mm, "end": v(1.26, 10.46) * mm});
            skLineSegment(sketch, "E100.10.60", {"start": v(1.81, 10.55) * mm, "end": v(1.83, 10.6) * mm});
            skLineSegment(sketch, "E100.10.61", {"start": v(1.18, 10.92) * mm, "end": v(1.17, 10.97) * mm});
            skLineSegment(sketch, "E100.10.62", {"start": v(1.23, 10.69) * mm, "end": v(1.22, 10.73) * mm});
            skLineSegment(sketch, "E100.10.63", {"start": v(1.26, 10.48) * mm, "end": v(1.25, 10.5) * mm});
            skLineSegment(sketch, "E100.10.64", {"start": v(1.33, 10.3) * mm, "end": v(1.32, 10.3) * mm});
            skLineSegment(sketch, "E100.10.65", {"start": v(1.55, 10.26) * mm, "end": v(1.57, 10.26) * mm});
            skLineSegment(sketch, "E100.10.66", {"start": v(1.73, 10.37) * mm, "end": v(1.74, 10.39) * mm});
            skLineSegment(sketch, "E100.10.67", {"start": v(1.83, 10.6) * mm, "end": v(1.85, 10.64) * mm});
            skLineSegment(sketch, "E100.10.68", {"start": v(1.7, 10.3) * mm, "end": v(1.7, 10.32) * mm});
            skLineSegment(sketch, "E100.10.69", {"start": v(1.24, 10.59) * mm, "end": v(1.24, 10.64) * mm});
            skLineSegment(sketch, "E100.10.70", {"start": v(1.62, 10.25) * mm, "end": v(1.62, 10.26) * mm});
            skLineSegment(sketch, "E100.10.71", {"start": v(1.72, 10.34) * mm, "end": v(1.72, 10.36) * mm});
            skLineSegment(sketch, "E100.10.72", {"start": v(1.63, 10.26) * mm, "end": v(1.64, 10.26) * mm});
            skLineSegment(sketch, "E100.10.73", {"start": v(1.25, 10.54) * mm, "end": v(1.24, 10.59) * mm});
            skLineSegment(sketch, "E100.10.74", {"start": v(1.34, 10.3) * mm, "end": v(1.33, 10.3) * mm});
            skLineSegment(sketch, "E100.10.75", {"start": v(1.35, 10.29) * mm, "end": v(1.34, 10.3) * mm});
            skLineSegment(sketch, "E100.10.76", {"start": v(1.43, 10.28) * mm, "end": v(1.4, 10.28) * mm});
            skLineSegment(sketch, "E100.10.77", {"start": v(1.68, 10.3) * mm, "end": v(1.7, 10.3) * mm});
            skLineSegment(sketch, "E100.10.78", {"start": v(1.28, 10.38) * mm, "end": v(1.27, 10.4) * mm});
            skLineSegment(sketch, "E100.10.79", {"start": v(1.75, 10.42) * mm, "end": v(1.77, 10.47) * mm});
            skLineSegment(sketch, "E100.10.80", {"start": v(1.64, 10.26) * mm, "end": v(1.65, 10.27) * mm});
            skLineSegment(sketch, "E100.10.81", {"start": v(1.35, 10.29) * mm, "end": v(1.35, 10.29) * mm});
            skLineSegment(sketch, "E100.10.82", {"start": v(1.75, 10.4) * mm, "end": v(1.75, 10.42) * mm});
            skLineSegment(sketch, "E100.10.83", {"start": v(1.45, 10.27) * mm, "end": v(1.43, 10.28) * mm});
            skLineSegment(sketch, "E100.10.84", {"start": v(1.27, 10.4) * mm, "end": v(1.26, 10.42) * mm});
            skLineSegment(sketch, "E100.10.85", {"start": v(1.67, 10.28) * mm, "end": v(1.67, 10.29) * mm});
            skLineSegment(sketch, "E100.10.86", {"start": v(1.48, 10.27) * mm, "end": v(1.45, 10.27) * mm});
            skLineSegment(sketch, "E100.10.87", {"start": v(1.26, 10.46) * mm, "end": v(1.26, 10.48) * mm});
            skLineSegment(sketch, "E100.10.88", {"start": v(1.36, 10.29) * mm, "end": v(1.35, 10.29) * mm});
            skLineSegment(sketch, "E100.10.89", {"start": v(1.38, 10.28) * mm, "end": v(1.36, 10.29) * mm});
            skLineSegment(sketch, "E100.10.90", {"start": v(1.6, 10.25) * mm, "end": v(1.6, 10.25) * mm});
            skLineSegment(sketch, "E100.10.91", {"start": v(1.62, 10.26) * mm, "end": v(1.63, 10.26) * mm});
            skLineSegment(sketch, "E100.10.92", {"start": v(1.66, 10.27) * mm, "end": v(1.67, 10.28) * mm});
            skLineSegment(sketch, "E100.10.93", {"start": v(1.52, 10.26) * mm, "end": v(1.55, 10.26) * mm});
            skLineSegment(sketch, "E100.10.94", {"start": v(1.4, 10.28) * mm, "end": v(1.38, 10.28) * mm});
            skLineSegment(sketch, "E100.10.95", {"start": v(1.3, 10.33) * mm, "end": v(1.3, 10.34) * mm});
            skLineSegment(sketch, "E100.10.96", {"start": v(1.6, 10.25) * mm, "end": v(1.62, 10.25) * mm});
            skLineSegment(sketch, "E100.10.97", {"start": v(1.3, 10.32) * mm, "end": v(1.3, 10.33) * mm});
            skLineSegment(sketch, "E100.10.98", {"start": v(1.3, 10.34) * mm, "end": v(1.29, 10.35) * mm});
            skLineSegment(sketch, "E100.10.99", {"start": v(1.29, 10.35) * mm, "end": v(1.28, 10.37) * mm});
            skLineSegment(sketch, "E100.11.0", {"start": v(0.67, 11.48) * mm, "end": v(0.7, 11.48) * mm});
            skLineSegment(sketch, "E100.11.1", {"start": v(-0.7, 11.48) * mm, "end": v(-0.74, 11.48) * mm});
            skLineSegment(sketch, "E100.11.2", {"start": v(-0.56, 11.35) * mm, "end": v(-0.58, 11.4) * mm});
            skLineSegment(sketch, "E100.11.3", {"start": v(-0.78, 11.47) * mm, "end": v(-0.82, 11.47) * mm});
            skLineSegment(sketch, "E100.11.4", {"start": v(0.43, 11.07) * mm, "end": v(0.45, 11.12) * mm});
            skLineSegment(sketch, "E100.11.5", {"start": v(0.74, 11.48) * mm, "end": v(0.78, 11.47) * mm});
            skLineSegment(sketch, "E100.11.6", {"start": v(-0.67, 11.48) * mm, "end": v(-0.7, 11.48) * mm});
            skLineSegment(sketch, "E100.11.7", {"start": v(0.53, 11.3) * mm, "end": v(0.56, 11.35) * mm});
            skLineSegment(sketch, "E100.11.8", {"start": v(-0.74, 11.48) * mm, "end": v(-0.78, 11.47) * mm});
            skLineSegment(sketch, "E100.11.9", {"start": v(0.56, 11.35) * mm, "end": v(0.58, 11.4) * mm});
            skLineSegment(sketch, "E100.11.10", {"start": v(0.78, 11.47) * mm, "end": v(0.82, 11.47) * mm});
            skLineSegment(sketch, "E100.11.11", {"start": v(0.58, 11.4) * mm, "end": v(0.6, 11.44) * mm});
            skLineSegment(sketch, "E100.11.12", {"start": v(0.51, 11.26) * mm, "end": v(0.53, 11.3) * mm});
            skLineSegment(sketch, "E100.11.13", {"start": v(-0.6, 11.44) * mm, "end": v(-0.63, 11.48) * mm});
            skLineSegment(sketch, "E100.11.14", {"start": v(0.63, 11.48) * mm, "end": v(0.67, 11.48) * mm});
            skLineSegment(sketch, "E100.11.15", {"start": v(0.45, 11.12) * mm, "end": v(0.47, 11.16) * mm});
            skLineSegment(sketch, "E100.11.16", {"start": v(0.7, 11.48) * mm, "end": v(0.74, 11.48) * mm});
            skLineSegment(sketch, "E100.11.17", {"start": v(-0.63, 11.48) * mm, "end": v(-0.67, 11.48) * mm});
            skLineSegment(sketch, "E100.11.18", {"start": v(-0.51, 11.26) * mm, "end": v(-0.53, 11.3) * mm});
            skLineSegment(sketch, "E100.11.19", {"start": v(0.49, 11.21) * mm, "end": v(0.51, 11.26) * mm});
            skLineSegment(sketch, "E100.11.20", {"start": v(0.6, 11.44) * mm, "end": v(0.63, 11.48) * mm});
            skLineSegment(sketch, "E100.11.21", {"start": v(-0.45, 11.12) * mm, "end": v(-0.47, 11.16) * mm});
            skLineSegment(sketch, "E100.11.22", {"start": v(-0.53, 11.3) * mm, "end": v(-0.56, 11.35) * mm});
            skLineSegment(sketch, "E100.11.23", {"start": v(0.47, 11.16) * mm, "end": v(0.49, 11.21) * mm});
            skLineSegment(sketch, "E100.11.24", {"start": v(-0.47, 11.16) * mm, "end": v(-0.49, 11.21) * mm});
            skLineSegment(sketch, "E100.11.25", {"start": v(-0.49, 11.21) * mm, "end": v(-0.51, 11.26) * mm});
            skLineSegment(sketch, "E100.11.26", {"start": v(-0.58, 11.4) * mm, "end": v(-0.6, 11.44) * mm});
            skLineSegment(sketch, "E100.11.27", {"start": v(-0.43, 11.07) * mm, "end": v(-0.45, 11.12) * mm});
            skLineSegment(sketch, "E100.11.28", {"start": v(-0.2, 10.44) * mm, "end": v(-0.21, 10.46) * mm});
            skLineSegment(sketch, "E100.11.29", {"start": v(-0.3, 10.7) * mm, "end": v(-0.3, 10.75) * mm});
            skLineSegment(sketch, "E100.11.30", {"start": v(-0.34, 10.84) * mm, "end": v(-0.35, 10.89) * mm});
            skLineSegment(sketch, "E100.11.31", {"start": v(0.22, 10.47) * mm, "end": v(0.23, 10.48) * mm});
            skLineSegment(sketch, "E100.11.32", {"start": v(0.4, 11.03) * mm, "end": v(0.43, 11.07) * mm});
            skLineSegment(sketch, "E100.11.33", {"start": v(-0.17, 10.4) * mm, "end": v(-0.18, 10.4) * mm});
            skLineSegment(sketch, "E100.11.34", {"start": v(0.17, 10.4) * mm, "end": v(0.18, 10.4) * mm});
            skLineSegment(sketch, "E100.11.35", {"start": v(-0.22, 10.47) * mm, "end": v(-0.23, 10.48) * mm});
            skLineSegment(sketch, "E100.11.36", {"start": v(-0.25, 10.57) * mm, "end": v(-0.26, 10.61) * mm});
            skLineSegment(sketch, "E100.11.37", {"start": v(0.37, 10.94) * mm, "end": v(0.39, 10.98) * mm});
            skLineSegment(sketch, "E100.11.38", {"start": v(0.28, 10.66) * mm, "end": v(0.3, 10.7) * mm});
            skLineSegment(sketch, "E100.11.39", {"start": v(0.32, 10.8) * mm, "end": v(0.34, 10.84) * mm});
            skLineSegment(sketch, "E100.11.40", {"start": v(0, 10.38) * mm, "end": v(0.02, 10.37) * mm});
            skLineSegment(sketch, "E100.11.41", {"start": v(0.02, 10.37) * mm, "end": v(0.05, 10.37) * mm});
            skLineSegment(sketch, "E100.11.42", {"start": v(-0.37, 10.94) * mm, "end": v(-0.39, 10.98) * mm});
            skLineSegment(sketch, "E100.11.43", {"start": v(-0.35, 10.89) * mm, "end": v(-0.37, 10.94) * mm});
            skLineSegment(sketch, "E100.11.44", {"start": v(0.39, 10.98) * mm, "end": v(0.4, 11.03) * mm});
            skLineSegment(sketch, "E100.11.45", {"start": v(0.2, 10.42) * mm, "end": v(0.2, 10.43) * mm});
            skLineSegment(sketch, "E100.11.46", {"start": v(0.12, 10.37) * mm, "end": v(0.13, 10.38) * mm});
            skLineSegment(sketch, "E100.11.47", {"start": v(0.34, 10.84) * mm, "end": v(0.35, 10.89) * mm});
            skLineSegment(sketch, "E100.11.48", {"start": v(-0.4, 11.03) * mm, "end": v(-0.43, 11.07) * mm});
            skLineSegment(sketch, "E100.11.49", {"start": v(-0.23, 10.5) * mm, "end": v(-0.24, 10.51) * mm});
            skLineSegment(sketch, "E100.11.50", {"start": v(0.35, 10.89) * mm, "end": v(0.37, 10.94) * mm});
            skLineSegment(sketch, "E100.11.51", {"start": v(0.26, 10.61) * mm, "end": v(0.28, 10.66) * mm});
            skLineSegment(sketch, "E100.11.52", {"start": v(-0.16, 10.4) * mm, "end": v(-0.17, 10.4) * mm});
            skLineSegment(sketch, "E100.11.53", {"start": v(-0.32, 10.8) * mm, "end": v(-0.34, 10.84) * mm});
            skLineSegment(sketch, "E100.11.54", {"start": v(0.23, 10.5) * mm, "end": v(0.24, 10.51) * mm});
            skLineSegment(sketch, "E100.11.55", {"start": v(0.1, 10.37) * mm, "end": v(0.12, 10.37) * mm});
            skLineSegment(sketch, "E100.11.56", {"start": v(0.21, 10.46) * mm, "end": v(0.22, 10.47) * mm});
            skLineSegment(sketch, "E100.11.57", {"start": v(-0.16, 10.39) * mm, "end": v(-0.16, 10.4) * mm});
            skLineSegment(sketch, "E100.11.58", {"start": v(0.24, 10.53) * mm, "end": v(0.25, 10.55) * mm});
            skLineSegment(sketch, "E100.11.59", {"start": v(-0.24, 10.51) * mm, "end": v(-0.24, 10.53) * mm});
            skLineSegment(sketch, "E100.11.60", {"start": v(0.3, 10.7) * mm, "end": v(0.3, 10.75) * mm});
            skLineSegment(sketch, "E100.11.61", {"start": v(-0.39, 10.98) * mm, "end": v(-0.4, 11.03) * mm});
            skLineSegment(sketch, "E100.11.62", {"start": v(-0.3, 10.75) * mm, "end": v(-0.32, 10.8) * mm});
            skLineSegment(sketch, "E100.11.63", {"start": v(-0.25, 10.55) * mm, "end": v(-0.25, 10.57) * mm});
            skLineSegment(sketch, "E100.11.64", {"start": v(-0.15, 10.38) * mm, "end": v(-0.16, 10.39) * mm});
            skLineSegment(sketch, "E100.11.65", {"start": v(0.07, 10.37) * mm, "end": v(0.1, 10.37) * mm});
            skLineSegment(sketch, "E100.11.66", {"start": v(0.24, 10.51) * mm, "end": v(0.24, 10.53) * mm});
            skLineSegment(sketch, "E100.11.67", {"start": v(0.3, 10.75) * mm, "end": v(0.32, 10.8) * mm});
            skLineSegment(sketch, "E100.11.68", {"start": v(0.2, 10.44) * mm, "end": v(0.21, 10.46) * mm});
            skLineSegment(sketch, "E100.11.69", {"start": v(-0.28, 10.66) * mm, "end": v(-0.3, 10.7) * mm});
            skLineSegment(sketch, "E100.11.70", {"start": v(0.14, 10.38) * mm, "end": v(0.15, 10.38) * mm});
            skLineSegment(sketch, "E100.11.71", {"start": v(0.23, 10.48) * mm, "end": v(0.23, 10.5) * mm});
            skLineSegment(sketch, "E100.11.72", {"start": v(0.16, 10.39) * mm, "end": v(0.16, 10.4) * mm});
            skLineSegment(sketch, "E100.11.73", {"start": v(-0.26, 10.61) * mm, "end": v(-0.28, 10.66) * mm});
            skLineSegment(sketch, "E100.11.74", {"start": v(-0.14, 10.38) * mm, "end": v(-0.15, 10.38) * mm});
            skLineSegment(sketch, "E100.11.75", {"start": v(-0.13, 10.38) * mm, "end": v(-0.14, 10.38) * mm});
            skLineSegment(sketch, "E100.11.76", {"start": v(-0.05, 10.37) * mm, "end": v(-0.07, 10.37) * mm});
            skLineSegment(sketch, "E100.11.77", {"start": v(0.2, 10.43) * mm, "end": v(0.2, 10.44) * mm});
            skLineSegment(sketch, "E100.11.78", {"start": v(-0.21, 10.46) * mm, "end": v(-0.22, 10.47) * mm});
            skLineSegment(sketch, "E100.11.79", {"start": v(0.25, 10.57) * mm, "end": v(0.26, 10.61) * mm});
            skLineSegment(sketch, "E100.11.80", {"start": v(0.16, 10.4) * mm, "end": v(0.17, 10.4) * mm});
            skLineSegment(sketch, "E100.11.81", {"start": v(-0.12, 10.37) * mm, "end": v(-0.13, 10.38) * mm});
            skLineSegment(sketch, "E100.11.82", {"start": v(0.25, 10.55) * mm, "end": v(0.25, 10.57) * mm});
            skLineSegment(sketch, "E100.11.83", {"start": v(-0.02, 10.37) * mm, "end": v(-0.05, 10.37) * mm});
            skLineSegment(sketch, "E100.11.84", {"start": v(-0.23, 10.48) * mm, "end": v(-0.23, 10.5) * mm});
            skLineSegment(sketch, "E100.11.85", {"start": v(0.19, 10.41) * mm, "end": v(0.2, 10.42) * mm});
            skLineSegment(sketch, "E100.11.86", {"start": v(0, 10.38) * mm, "end": v(-0.02, 10.37) * mm});
            skLineSegment(sketch, "E100.11.87", {"start": v(-0.24, 10.53) * mm, "end": v(-0.25, 10.55) * mm});
            skLineSegment(sketch, "E100.11.88", {"start": v(-0.12, 10.37) * mm, "end": v(-0.12, 10.37) * mm});
            skLineSegment(sketch, "E100.11.89", {"start": v(-0.1, 10.37) * mm, "end": v(-0.12, 10.37) * mm});
            skLineSegment(sketch, "E100.11.90", {"start": v(0.12, 10.37) * mm, "end": v(0.12, 10.37) * mm});
            skLineSegment(sketch, "E100.11.91", {"start": v(0.15, 10.38) * mm, "end": v(0.16, 10.39) * mm});
            skLineSegment(sketch, "E100.11.92", {"start": v(0.18, 10.4) * mm, "end": v(0.19, 10.41) * mm});
            skLineSegment(sketch, "E100.11.93", {"start": v(0.05, 10.37) * mm, "end": v(0.07, 10.37) * mm});
            skLineSegment(sketch, "E100.11.94", {"start": v(-0.07, 10.37) * mm, "end": v(-0.1, 10.37) * mm});
            skLineSegment(sketch, "E100.11.95", {"start": v(-0.19, 10.41) * mm, "end": v(-0.2, 10.42) * mm});
            skLineSegment(sketch, "E100.11.96", {"start": v(0.13, 10.38) * mm, "end": v(0.14, 10.38) * mm});
            skLineSegment(sketch, "E100.11.97", {"start": v(-0.18, 10.4) * mm, "end": v(-0.19, 10.41) * mm});
            skLineSegment(sketch, "E100.11.98", {"start": v(-0.2, 10.42) * mm, "end": v(-0.2, 10.43) * mm});
            skLineSegment(sketch, "E100.11.99", {"start": v(-0.2, 10.43) * mm, "end": v(-0.2, 10.44) * mm});
            skLineSegment(sketch, "E100.12.0", {"start": v(-0.97, 11.46) * mm, "end": v(-0.94, 11.46) * mm});
            skLineSegment(sketch, "E100.12.1", {"start": v(-2.33, 11.26) * mm, "end": v(-2.37, 11.25) * mm});
            skLineSegment(sketch, "E100.12.2", {"start": v(-2.17, 11.15) * mm, "end": v(-2.2, 11.2) * mm});
            skLineSegment(sketch, "E100.12.3", {"start": v(-2.4, 11.25) * mm, "end": v(-2.44, 11.24) * mm});
            skLineSegment(sketch, "E100.12.4", {"start": v(-1.15, 11.02) * mm, "end": v(-1.14, 11.07) * mm});
            skLineSegment(sketch, "E100.12.5", {"start": v(-0.9, 11.46) * mm, "end": v(-0.86, 11.47) * mm});
            skLineSegment(sketch, "E100.12.6", {"start": v(-2.3, 11.27) * mm, "end": v(-2.33, 11.26) * mm});
            skLineSegment(sketch, "E100.12.7", {"start": v(-1.08, 11.26) * mm, "end": v(-1.06, 11.31) * mm});
            skLineSegment(sketch, "E100.12.8", {"start": v(-2.37, 11.25) * mm, "end": v(-2.4, 11.25) * mm});
            skLineSegment(sketch, "E100.12.9", {"start": v(-1.06, 11.31) * mm, "end": v(-1.05, 11.36) * mm});
            skLineSegment(sketch, "E100.12.10", {"start": v(-0.86, 11.47) * mm, "end": v(-0.82, 11.47) * mm});
            skLineSegment(sketch, "E100.12.11", {"start": v(-1.05, 11.36) * mm, "end": v(-1.03, 11.4) * mm});
            skLineSegment(sketch, "E100.12.12", {"start": v(-1.1, 11.21) * mm, "end": v(-1.08, 11.26) * mm});
            skLineSegment(sketch, "E100.12.13", {"start": v(-2.23, 11.24) * mm, "end": v(-2.26, 11.28) * mm});
            skLineSegment(sketch, "E100.12.14", {"start": v(-1.01, 11.46) * mm, "end": v(-0.97, 11.46) * mm});
            skLineSegment(sketch, "E100.12.15", {"start": v(-1.14, 11.07) * mm, "end": v(-1.13, 11.12) * mm});
            skLineSegment(sketch, "E100.12.16", {"start": v(-0.94, 11.46) * mm, "end": v(-0.9, 11.46) * mm});
            skLineSegment(sketch, "E100.12.17", {"start": v(-2.26, 11.28) * mm, "end": v(-2.3, 11.27) * mm});
            skLineSegment(sketch, "E100.12.18", {"start": v(-2.1, 11.07) * mm, "end": v(-2.14, 11.11) * mm});
            skLineSegment(sketch, "E100.12.19", {"start": v(-1.11, 11.17) * mm, "end": v(-1.1, 11.21) * mm});
            skLineSegment(sketch, "E100.12.20", {"start": v(-1.03, 11.4) * mm, "end": v(-1.01, 11.46) * mm});
            skLineSegment(sketch, "E100.12.21", {"start": v(-2.02, 10.94) * mm, "end": v(-2.05, 10.98) * mm});
            skLineSegment(sketch, "E100.12.22", {"start": v(-2.14, 11.11) * mm, "end": v(-2.17, 11.15) * mm});
            skLineSegment(sketch, "E100.12.23", {"start": v(-1.13, 11.12) * mm, "end": v(-1.11, 11.17) * mm});
            skLineSegment(sketch, "E100.12.24", {"start": v(-2.05, 10.98) * mm, "end": v(-2.08, 11.03) * mm});
            skLineSegment(sketch, "E100.12.25", {"start": v(-2.08, 11.03) * mm, "end": v(-2.1, 11.07) * mm});
            skLineSegment(sketch, "E100.12.26", {"start": v(-2.2, 11.2) * mm, "end": v(-2.23, 11.24) * mm});
            skLineSegment(sketch, "E100.12.27", {"start": v(-2, 10.9) * mm, "end": v(-2.02, 10.94) * mm});
            skLineSegment(sketch, "E100.12.28", {"start": v(-1.7, 10.3) * mm, "end": v(-1.7, 10.32) * mm});
            skLineSegment(sketch, "E100.12.29", {"start": v(-1.81, 10.55) * mm, "end": v(-1.83, 10.6) * mm});
            skLineSegment(sketch, "E100.12.30", {"start": v(-1.88, 10.69) * mm, "end": v(-1.9, 10.73) * mm});
            skLineSegment(sketch, "E100.12.31", {"start": v(-1.27, 10.4) * mm, "end": v(-1.27, 10.4) * mm});
            skLineSegment(sketch, "E100.12.32", {"start": v(-1.17, 10.97) * mm, "end": v(-1.15, 11.02) * mm});
            skLineSegment(sketch, "E100.12.33", {"start": v(-1.65, 10.27) * mm, "end": v(-1.66, 10.27) * mm});
            skLineSegment(sketch, "E100.12.34", {"start": v(-1.31, 10.32) * mm, "end": v(-1.3, 10.32) * mm});
            skLineSegment(sketch, "E100.12.35", {"start": v(-1.7, 10.33) * mm, "end": v(-1.72, 10.34) * mm});
            skLineSegment(sketch, "E100.12.36", {"start": v(-1.75, 10.42) * mm, "end": v(-1.77, 10.47) * mm});
            skLineSegment(sketch, "E100.12.37", {"start": v(-1.2, 10.88) * mm, "end": v(-1.18, 10.92) * mm});
            skLineSegment(sketch, "E100.12.38", {"start": v(-1.24, 10.59) * mm, "end": v(-1.24, 10.64) * mm});
            skLineSegment(sketch, "E100.12.39", {"start": v(-1.22, 10.73) * mm, "end": v(-1.21, 10.78) * mm});
            skLineSegment(sketch, "E100.12.40", {"start": v(-1.48, 10.27) * mm, "end": v(-1.45, 10.27) * mm});
            skLineSegment(sketch, "E100.12.41", {"start": v(-1.45, 10.27) * mm, "end": v(-1.43, 10.28) * mm});
            skLineSegment(sketch, "E100.12.42", {"start": v(-1.92, 10.77) * mm, "end": v(-1.95, 10.81) * mm});
            skLineSegment(sketch, "E100.12.43", {"start": v(-1.9, 10.73) * mm, "end": v(-1.92, 10.77) * mm});
            skLineSegment(sketch, "E100.12.44", {"start": v(-1.18, 10.92) * mm, "end": v(-1.17, 10.97) * mm});
            skLineSegment(sketch, "E100.12.45", {"start": v(-1.3, 10.34) * mm, "end": v(-1.29, 10.35) * mm});
            skLineSegment(sketch, "E100.12.46", {"start": v(-1.35, 10.29) * mm, "end": v(-1.35, 10.29) * mm});
            skLineSegment(sketch, "E100.12.47", {"start": v(-1.21, 10.78) * mm, "end": v(-1.2, 10.83) * mm});
            skLineSegment(sketch, "E100.12.48", {"start": v(-1.97, 10.86) * mm, "end": v(-2, 10.9) * mm});
            skLineSegment(sketch, "E100.12.49", {"start": v(-1.72, 10.36) * mm, "end": v(-1.73, 10.37) * mm});
            skLineSegment(sketch, "E100.12.50", {"start": v(-1.2, 10.83) * mm, "end": v(-1.2, 10.88) * mm});
            skLineSegment(sketch, "E100.12.51", {"start": v(-1.25, 10.54) * mm, "end": v(-1.24, 10.59) * mm});
            skLineSegment(sketch, "E100.12.52", {"start": v(-1.64, 10.26) * mm, "end": v(-1.65, 10.27) * mm});
            skLineSegment(sketch, "E100.12.53", {"start": v(-1.85, 10.64) * mm, "end": v(-1.88, 10.69) * mm});
            skLineSegment(sketch, "E100.12.54", {"start": v(-1.26, 10.42) * mm, "end": v(-1.26, 10.44) * mm});
            skLineSegment(sketch, "E100.12.55", {"start": v(-1.38, 10.28) * mm, "end": v(-1.36, 10.29) * mm});
            skLineSegment(sketch, "E100.12.56", {"start": v(-1.28, 10.38) * mm, "end": v(-1.27, 10.4) * mm});
            skLineSegment(sketch, "E100.12.57", {"start": v(-1.63, 10.26) * mm, "end": v(-1.64, 10.26) * mm});
            skLineSegment(sketch, "E100.12.58", {"start": v(-1.26, 10.46) * mm, "end": v(-1.26, 10.48) * mm});
            skLineSegment(sketch, "E100.12.59", {"start": v(-1.73, 10.37) * mm, "end": v(-1.74, 10.39) * mm});
            skLineSegment(sketch, "E100.12.60", {"start": v(-1.24, 10.64) * mm, "end": v(-1.23, 10.69) * mm});
            skLineSegment(sketch, "E100.12.61", {"start": v(-1.95, 10.81) * mm, "end": v(-1.97, 10.86) * mm});
            skLineSegment(sketch, "E100.12.62", {"start": v(-1.83, 10.6) * mm, "end": v(-1.85, 10.64) * mm});
            skLineSegment(sketch, "E100.12.63", {"start": v(-1.75, 10.4) * mm, "end": v(-1.75, 10.42) * mm});
            skLineSegment(sketch, "E100.12.64", {"start": v(-1.62, 10.26) * mm, "end": v(-1.63, 10.26) * mm});
            skLineSegment(sketch, "E100.12.65", {"start": v(-1.4, 10.28) * mm, "end": v(-1.38, 10.28) * mm});
            skLineSegment(sketch, "E100.12.66", {"start": v(-1.26, 10.44) * mm, "end": v(-1.26, 10.46) * mm});
            skLineSegment(sketch, "E100.12.67", {"start": v(-1.23, 10.69) * mm, "end": v(-1.22, 10.73) * mm});
            skLineSegment(sketch, "E100.12.68", {"start": v(-1.28, 10.37) * mm, "end": v(-1.28, 10.38) * mm});
            skLineSegment(sketch, "E100.12.69", {"start": v(-1.8, 10.51) * mm, "end": v(-1.81, 10.55) * mm});
            skLineSegment(sketch, "E100.12.70", {"start": v(-1.34, 10.3) * mm, "end": v(-1.33, 10.3) * mm});
            skLineSegment(sketch, "E100.12.71", {"start": v(-1.27, 10.4) * mm, "end": v(-1.26, 10.42) * mm});
            skLineSegment(sketch, "E100.12.72", {"start": v(-1.32, 10.3) * mm, "end": v(-1.32, 10.3) * mm});
            skLineSegment(sketch, "E100.12.73", {"start": v(-1.77, 10.47) * mm, "end": v(-1.8, 10.51) * mm});
            skLineSegment(sketch, "E100.12.74", {"start": v(-1.62, 10.25) * mm, "end": v(-1.62, 10.26) * mm});
            skLineSegment(sketch, "E100.12.75", {"start": v(-1.6, 10.25) * mm, "end": v(-1.62, 10.25) * mm});
            skLineSegment(sketch, "E100.12.76", {"start": v(-1.52, 10.26) * mm, "end": v(-1.55, 10.26) * mm});
            skLineSegment(sketch, "E100.12.77", {"start": v(-1.29, 10.35) * mm, "end": v(-1.28, 10.37) * mm});
            skLineSegment(sketch, "E100.12.78", {"start": v(-1.7, 10.32) * mm, "end": v(-1.7, 10.33) * mm});
            skLineSegment(sketch, "E100.12.79", {"start": v(-1.25, 10.5) * mm, "end": v(-1.25, 10.54) * mm});
            skLineSegment(sketch, "E100.12.80", {"start": v(-1.32, 10.3) * mm, "end": v(-1.31, 10.32) * mm});
            skLineSegment(sketch, "E100.12.81", {"start": v(-1.6, 10.25) * mm, "end": v(-1.6, 10.25) * mm});
            skLineSegment(sketch, "E100.12.82", {"start": v(-1.26, 10.48) * mm, "end": v(-1.25, 10.5) * mm});
            skLineSegment(sketch, "E100.12.83", {"start": v(-1.5, 10.27) * mm, "end": v(-1.52, 10.26) * mm});
            skLineSegment(sketch, "E100.12.84", {"start": v(-1.72, 10.34) * mm, "end": v(-1.72, 10.36) * mm});
            skLineSegment(sketch, "E100.12.85", {"start": v(-1.3, 10.33) * mm, "end": v(-1.3, 10.34) * mm});
            skLineSegment(sketch, "E100.12.86", {"start": v(-1.48, 10.27) * mm, "end": v(-1.5, 10.27) * mm});
            skLineSegment(sketch, "E100.12.87", {"start": v(-1.74, 10.39) * mm, "end": v(-1.75, 10.4) * mm});
            skLineSegment(sketch, "E100.12.88", {"start": v(-1.6, 10.25) * mm, "end": v(-1.6, 10.25) * mm});
            skLineSegment(sketch, "E100.12.89", {"start": v(-1.57, 10.26) * mm, "end": v(-1.6, 10.25) * mm});
            skLineSegment(sketch, "E100.12.90", {"start": v(-1.36, 10.29) * mm, "end": v(-1.35, 10.29) * mm});
            skLineSegment(sketch, "E100.12.91", {"start": v(-1.33, 10.3) * mm, "end": v(-1.32, 10.3) * mm});
            skLineSegment(sketch, "E100.12.92", {"start": v(-1.3, 10.32) * mm, "end": v(-1.3, 10.33) * mm});
            skLineSegment(sketch, "E100.12.93", {"start": v(-1.43, 10.28) * mm, "end": v(-1.4, 10.28) * mm});
            skLineSegment(sketch, "E100.12.94", {"start": v(-1.55, 10.26) * mm, "end": v(-1.57, 10.26) * mm});
            skLineSegment(sketch, "E100.12.95", {"start": v(-1.67, 10.28) * mm, "end": v(-1.67, 10.29) * mm});
            skLineSegment(sketch, "E100.12.96", {"start": v(-1.35, 10.29) * mm, "end": v(-1.34, 10.3) * mm});
            skLineSegment(sketch, "E100.12.97", {"start": v(-1.66, 10.27) * mm, "end": v(-1.67, 10.28) * mm});
            skLineSegment(sketch, "E100.12.98", {"start": v(-1.67, 10.29) * mm, "end": v(-1.68, 10.3) * mm});
            skLineSegment(sketch, "E100.12.99", {"start": v(-1.68, 10.3) * mm, "end": v(-1.7, 10.3) * mm});
            skLineSegment(sketch, "E100.13.0", {"start": v(-2.6, 11.2) * mm, "end": v(-2.56, 11.21) * mm});
            skLineSegment(sketch, "E100.13.1", {"start": v(-3.91, 10.81) * mm, "end": v(-3.95, 10.8) * mm});
            skLineSegment(sketch, "E100.13.2", {"start": v(-3.73, 10.73) * mm, "end": v(-3.77, 10.77) * mm});
            skLineSegment(sketch, "E100.13.3", {"start": v(-3.98, 10.79) * mm, "end": v(-4.02, 10.77) * mm});
            skLineSegment(sketch, "E100.13.4", {"start": v(-2.71, 10.74) * mm, "end": v(-2.7, 10.8) * mm});
            skLineSegment(sketch, "E100.13.5", {"start": v(-2.52, 11.22) * mm, "end": v(-2.48, 11.23) * mm});
            skLineSegment(sketch, "E100.13.6", {"start": v(-3.87, 10.83) * mm, "end": v(-3.91, 10.81) * mm});
            skLineSegment(sketch, "E100.13.7", {"start": v(-2.67, 11) * mm, "end": v(-2.66, 11.04) * mm});
            skLineSegment(sketch, "E100.13.8", {"start": v(-3.95, 10.8) * mm, "end": v(-3.98, 10.79) * mm});
            skLineSegment(sketch, "E100.13.9", {"start": v(-2.66, 11.04) * mm, "end": v(-2.65, 11.1) * mm});
            skLineSegment(sketch, "E100.13.10", {"start": v(-2.48, 11.23) * mm, "end": v(-2.44, 11.24) * mm});
            skLineSegment(sketch, "E100.13.11", {"start": v(-2.65, 11.1) * mm, "end": v(-2.64, 11.14) * mm});
            skLineSegment(sketch, "E100.13.12", {"start": v(-2.68, 10.94) * mm, "end": v(-2.67, 11) * mm});
            skLineSegment(sketch, "E100.13.13", {"start": v(-3.8, 10.8) * mm, "end": v(-3.84, 10.84) * mm});
            skLineSegment(sketch, "E100.13.14", {"start": v(-2.63, 11.2) * mm, "end": v(-2.6, 11.2) * mm});
            skLineSegment(sketch, "E100.13.15", {"start": v(-2.7, 10.8) * mm, "end": v(-2.7, 10.84) * mm});
            skLineSegment(sketch, "E100.13.16", {"start": v(-2.56, 11.21) * mm, "end": v(-2.52, 11.22) * mm});
            skLineSegment(sketch, "E100.13.17", {"start": v(-3.84, 10.84) * mm, "end": v(-3.87, 10.83) * mm});
            skLineSegment(sketch, "E100.13.18", {"start": v(-3.66, 10.66) * mm, "end": v(-3.7, 10.7) * mm});
            skLineSegment(sketch, "E100.13.19", {"start": v(-2.69, 10.9) * mm, "end": v(-2.68, 10.94) * mm});
            skLineSegment(sketch, "E100.13.20", {"start": v(-2.64, 11.14) * mm, "end": v(-2.63, 11.2) * mm});
            skLineSegment(sketch, "E100.13.21", {"start": v(-3.56, 10.54) * mm, "end": v(-3.6, 10.58) * mm});
            skLineSegment(sketch, "E100.13.22", {"start": v(-3.7, 10.7) * mm, "end": v(-3.73, 10.73) * mm});
            skLineSegment(sketch, "E100.13.23", {"start": v(-2.7, 10.84) * mm, "end": v(-2.69, 10.9) * mm});
            skLineSegment(sketch, "E100.13.24", {"start": v(-3.6, 10.58) * mm, "end": v(-3.63, 10.62) * mm});
            skLineSegment(sketch, "E100.13.25", {"start": v(-3.63, 10.62) * mm, "end": v(-3.66, 10.66) * mm});
            skLineSegment(sketch, "E100.13.26", {"start": v(-3.77, 10.77) * mm, "end": v(-3.8, 10.8) * mm});
            skLineSegment(sketch, "E100.13.27", {"start": v(-3.53, 10.5) * mm, "end": v(-3.56, 10.54) * mm});
            skLineSegment(sketch, "E100.13.28", {"start": v(-3.14, 9.96) * mm, "end": v(-3.15, 9.97) * mm});
            skLineSegment(sketch, "E100.13.29", {"start": v(-3.3, 10.19) * mm, "end": v(-3.32, 10.23) * mm});
            skLineSegment(sketch, "E100.13.30", {"start": v(-3.38, 10.3) * mm, "end": v(-3.4, 10.35) * mm});
            skLineSegment(sketch, "E100.13.31", {"start": v(-2.74, 10.1) * mm, "end": v(-2.74, 10.12) * mm});
            skLineSegment(sketch, "E100.13.32", {"start": v(-2.72, 10.7) * mm, "end": v(-2.71, 10.74) * mm});
            skLineSegment(sketch, "E100.13.33", {"start": v(-3.1, 9.93) * mm, "end": v(-3.1, 9.93) * mm});
            skLineSegment(sketch, "E100.13.34", {"start": v(-2.76, 10.02) * mm, "end": v(-2.76, 10.03) * mm});
            skLineSegment(sketch, "E100.13.35", {"start": v(-3.16, 9.98) * mm, "end": v(-3.17, 10) * mm});
            skLineSegment(sketch, "E100.13.36", {"start": v(-3.22, 10.07) * mm, "end": v(-3.24, 10.1) * mm});
            skLineSegment(sketch, "E100.13.37", {"start": v(-2.73, 10.6) * mm, "end": v(-2.72, 10.65) * mm});
            skLineSegment(sketch, "E100.13.38", {"start": v(-2.74, 10.3) * mm, "end": v(-2.74, 10.35) * mm});
            skLineSegment(sketch, "E100.13.39", {"start": v(-2.73, 10.45) * mm, "end": v(-2.73, 10.5) * mm});
            skLineSegment(sketch, "E100.13.40", {"start": v(-2.92, 9.95) * mm, "end": v(-2.9, 9.96) * mm});
            skLineSegment(sketch, "E100.13.41", {"start": v(-2.9, 9.96) * mm, "end": v(-2.88, 9.97) * mm});
            skLineSegment(sketch, "E100.13.42", {"start": v(-3.44, 10.39) * mm, "end": v(-3.47, 10.43) * mm});
            skLineSegment(sketch, "E100.13.43", {"start": v(-3.4, 10.35) * mm, "end": v(-3.44, 10.39) * mm});
            skLineSegment(sketch, "E100.13.44", {"start": v(-2.72, 10.65) * mm, "end": v(-2.72, 10.7) * mm});
            skLineSegment(sketch, "E100.13.45", {"start": v(-2.75, 10.05) * mm, "end": v(-2.75, 10.07) * mm});
            skLineSegment(sketch, "E100.13.46", {"start": v(-2.8, 9.99) * mm, "end": v(-2.8, 10) * mm});
            skLineSegment(sketch, "E100.13.47", {"start": v(-2.73, 10.5) * mm, "end": v(-2.73, 10.55) * mm});
            skLineSegment(sketch, "E100.13.48", {"start": v(-3.5, 10.47) * mm, "end": v(-3.53, 10.5) * mm});
            skLineSegment(sketch, "E100.13.49", {"start": v(-3.18, 10) * mm, "end": v(-3.2, 10.02) * mm});
            skLineSegment(sketch, "E100.13.50", {"start": v(-2.73, 10.55) * mm, "end": v(-2.73, 10.6) * mm});
            skLineSegment(sketch, "E100.13.51", {"start": v(-2.74, 10.26) * mm, "end": v(-2.74, 10.3) * mm});
            skLineSegment(sketch, "E100.13.52", {"start": v(-3.08, 9.92) * mm, "end": v(-3.1, 9.93) * mm});
            skLineSegment(sketch, "E100.13.53", {"start": v(-3.35, 10.27) * mm, "end": v(-3.38, 10.3) * mm});
            skLineSegment(sketch, "E100.13.54", {"start": v(-2.73, 10.14) * mm, "end": v(-2.73, 10.15) * mm});
            skLineSegment(sketch, "E100.13.55", {"start": v(-2.83, 9.98) * mm, "end": v(-2.81, 9.99) * mm});
            skLineSegment(sketch, "E100.13.56", {"start": v(-2.74, 10.1) * mm, "end": v(-2.74, 10.1) * mm});
            skLineSegment(sketch, "E100.13.57", {"start": v(-3.08, 9.92) * mm, "end": v(-3.08, 9.92) * mm});
            skLineSegment(sketch, "E100.13.58", {"start": v(-2.73, 10.17) * mm, "end": v(-2.73, 10.2) * mm});
            skLineSegment(sketch, "E100.13.59", {"start": v(-3.2, 10.02) * mm, "end": v(-3.2, 10.03) * mm});
            skLineSegment(sketch, "E100.13.60", {"start": v(-2.74, 10.35) * mm, "end": v(-2.74, 10.4) * mm});
            skLineSegment(sketch, "E100.13.61", {"start": v(-3.47, 10.43) * mm, "end": v(-3.5, 10.47) * mm});
            skLineSegment(sketch, "E100.13.62", {"start": v(-3.32, 10.23) * mm, "end": v(-3.35, 10.27) * mm});
            skLineSegment(sketch, "E100.13.63", {"start": v(-3.2, 10.05) * mm, "end": v(-3.22, 10.07) * mm});
            skLineSegment(sketch, "E100.13.64", {"start": v(-3.07, 9.92) * mm, "end": v(-3.08, 9.92) * mm});
            skLineSegment(sketch, "E100.13.65", {"start": v(-2.86, 9.97) * mm, "end": v(-2.83, 9.98) * mm});
            skLineSegment(sketch, "E100.13.66", {"start": v(-2.73, 10.15) * mm, "end": v(-2.73, 10.17) * mm});
            skLineSegment(sketch, "E100.13.67", {"start": v(-2.74, 10.4) * mm, "end": v(-2.73, 10.45) * mm});
            skLineSegment(sketch, "E100.13.68", {"start": v(-2.74, 10.08) * mm, "end": v(-2.74, 10.1) * mm});
            skLineSegment(sketch, "E100.13.69", {"start": v(-3.27, 10.15) * mm, "end": v(-3.3, 10.19) * mm});
            skLineSegment(sketch, "E100.13.70", {"start": v(-2.79, 10) * mm, "end": v(-2.78, 10) * mm});
            skLineSegment(sketch, "E100.13.71", {"start": v(-2.74, 10.12) * mm, "end": v(-2.73, 10.14) * mm});
            skLineSegment(sketch, "E100.13.72", {"start": v(-2.78, 10) * mm, "end": v(-2.77, 10.02) * mm});
            skLineSegment(sketch, "E100.13.73", {"start": v(-3.24, 10.1) * mm, "end": v(-3.27, 10.15) * mm});
            skLineSegment(sketch, "E100.13.74", {"start": v(-3.06, 9.92) * mm, "end": v(-3.07, 9.92) * mm});
            skLineSegment(sketch, "E100.13.75", {"start": v(-3.05, 9.92) * mm, "end": v(-3.06, 9.92) * mm});
            skLineSegment(sketch, "E100.13.76", {"start": v(-2.97, 9.94) * mm, "end": v(-3, 9.93) * mm});
            skLineSegment(sketch, "E100.13.77", {"start": v(-2.75, 10.07) * mm, "end": v(-2.74, 10.08) * mm});
            skLineSegment(sketch, "E100.13.78", {"start": v(-3.15, 9.97) * mm, "end": v(-3.16, 9.98) * mm});
            skLineSegment(sketch, "E100.13.79", {"start": v(-2.73, 10.2) * mm, "end": v(-2.74, 10.26) * mm});
            skLineSegment(sketch, "E100.13.80", {"start": v(-2.77, 10.02) * mm, "end": v(-2.76, 10.02) * mm});
            skLineSegment(sketch, "E100.13.81", {"start": v(-3.04, 9.92) * mm, "end": v(-3.05, 9.92) * mm});
            skLineSegment(sketch, "E100.13.82", {"start": v(-2.73, 10.2) * mm, "end": v(-2.73, 10.2) * mm});
            skLineSegment(sketch, "E100.13.83", {"start": v(-2.95, 9.95) * mm, "end": v(-2.97, 9.94) * mm});
            skLineSegment(sketch, "E100.13.84", {"start": v(-3.17, 10) * mm, "end": v(-3.18, 10) * mm});
            skLineSegment(sketch, "E100.13.85", {"start": v(-2.76, 10.04) * mm, "end": v(-2.75, 10.05) * mm});
            skLineSegment(sketch, "E100.13.86", {"start": v(-2.92, 9.95) * mm, "end": v(-2.95, 9.95) * mm});
            skLineSegment(sketch, "E100.13.87", {"start": v(-3.2, 10.03) * mm, "end": v(-3.2, 10.05) * mm});
            skLineSegment(sketch, "E100.13.88", {"start": v(-3.03, 9.92) * mm, "end": v(-3.04, 9.92) * mm});
            skLineSegment(sketch, "E100.13.89", {"start": v(-3.01, 9.93) * mm, "end": v(-3.03, 9.92) * mm});
            skLineSegment(sketch, "E100.13.90", {"start": v(-2.81, 9.99) * mm, "end": v(-2.8, 9.99) * mm});
            skLineSegment(sketch, "E100.13.91", {"start": v(-2.78, 10) * mm, "end": v(-2.78, 10) * mm});
            skLineSegment(sketch, "E100.13.92", {"start": v(-2.76, 10.03) * mm, "end": v(-2.76, 10.04) * mm});
            skLineSegment(sketch, "E100.13.93", {"start": v(-2.88, 9.97) * mm, "end": v(-2.86, 9.97) * mm});
            skLineSegment(sketch, "E100.13.94", {"start": v(-3, 9.93) * mm, "end": v(-3.01, 9.93) * mm});
            skLineSegment(sketch, "E100.13.95", {"start": v(-3.11, 9.94) * mm, "end": v(-3.12, 9.95) * mm});
            skLineSegment(sketch, "E100.13.96", {"start": v(-2.8, 10) * mm, "end": v(-2.79, 10) * mm});
            skLineSegment(sketch, "E100.13.97", {"start": v(-3.1, 9.93) * mm, "end": v(-3.11, 9.94) * mm});
            skLineSegment(sketch, "E100.13.98", {"start": v(-3.12, 9.95) * mm, "end": v(-3.13, 9.95) * mm});
            skLineSegment(sketch, "E100.13.99", {"start": v(-3.13, 9.95) * mm, "end": v(-3.14, 9.96) * mm});
            skLineSegment(sketch, "E100.14.0", {"start": v(-4.16, 10.72) * mm, "end": v(-4.13, 10.73) * mm});
            skLineSegment(sketch, "E100.14.1", {"start": v(-5.41, 10.15) * mm, "end": v(-5.44, 10.13) * mm});
            skLineSegment(sketch, "E100.14.2", {"start": v(-5.22, 10.1) * mm, "end": v(-5.26, 10.12) * mm});
            skLineSegment(sketch, "E100.14.3", {"start": v(-5.48, 10.11) * mm, "end": v(-5.51, 10.1) * mm});
            skLineSegment(sketch, "E100.14.4", {"start": v(-4.21, 10.25) * mm, "end": v(-4.21, 10.3) * mm});
            skLineSegment(sketch, "E100.14.5", {"start": v(-4.1, 10.75) * mm, "end": v(-4.05, 10.76) * mm});
            skLineSegment(sketch, "E100.14.6", {"start": v(-5.38, 10.17) * mm, "end": v(-5.41, 10.15) * mm});
            skLineSegment(sketch, "E100.14.7", {"start": v(-4.21, 10.5) * mm, "end": v(-4.2, 10.55) * mm});
            skLineSegment(sketch, "E100.14.8", {"start": v(-5.44, 10.13) * mm, "end": v(-5.48, 10.11) * mm});
            skLineSegment(sketch, "E100.14.9", {"start": v(-4.2, 10.55) * mm, "end": v(-4.2, 10.6) * mm});
            skLineSegment(sketch, "E100.14.10", {"start": v(-4.05, 10.76) * mm, "end": v(-4.02, 10.77) * mm});
            skLineSegment(sketch, "E100.14.11", {"start": v(-4.2, 10.6) * mm, "end": v(-4.2, 10.65) * mm});
            skLineSegment(sketch, "E100.14.12", {"start": v(-4.21, 10.45) * mm, "end": v(-4.21, 10.5) * mm});
            skLineSegment(sketch, "E100.14.13", {"start": v(-5.3, 10.15) * mm, "end": v(-5.34, 10.18) * mm});
            skLineSegment(sketch, "E100.14.14", {"start": v(-4.2, 10.7) * mm, "end": v(-4.16, 10.72) * mm});
            skLineSegment(sketch, "E100.14.15", {"start": v(-4.21, 10.3) * mm, "end": v(-4.21, 10.35) * mm});
            skLineSegment(sketch, "E100.14.16", {"start": v(-4.13, 10.73) * mm, "end": v(-4.1, 10.75) * mm});
            skLineSegment(sketch, "E100.14.17", {"start": v(-5.34, 10.18) * mm, "end": v(-5.38, 10.17) * mm});
            skLineSegment(sketch, "E100.14.18", {"start": v(-5.14, 10.03) * mm, "end": v(-5.18, 10.06) * mm});
            skLineSegment(sketch, "E100.14.19", {"start": v(-4.21, 10.4) * mm, "end": v(-4.21, 10.45) * mm});
            skLineSegment(sketch, "E100.14.20", {"start": v(-4.2, 10.65) * mm, "end": v(-4.2, 10.7) * mm});
            skLineSegment(sketch, "E100.14.21", {"start": v(-5.02, 9.93) * mm, "end": v(-5.06, 9.96) * mm});
            skLineSegment(sketch, "E100.14.22", {"start": v(-5.18, 10.06) * mm, "end": v(-5.22, 10.1) * mm});
            skLineSegment(sketch, "E100.14.23", {"start": v(-4.21, 10.35) * mm, "end": v(-4.21, 10.4) * mm});
            skLineSegment(sketch, "E100.14.24", {"start": v(-5.06, 9.96) * mm, "end": v(-5.1, 10) * mm});
            skLineSegment(sketch, "E100.14.25", {"start": v(-5.1, 10) * mm, "end": v(-5.14, 10.03) * mm});
            skLineSegment(sketch, "E100.14.26", {"start": v(-5.26, 10.12) * mm, "end": v(-5.3, 10.15) * mm});
            skLineSegment(sketch, "E100.14.27", {"start": v(-4.99, 9.9) * mm, "end": v(-5.02, 9.93) * mm});
            skLineSegment(sketch, "E100.14.28", {"start": v(-4.53, 9.41) * mm, "end": v(-4.54, 9.42) * mm});
            skLineSegment(sketch, "E100.14.29", {"start": v(-4.71, 9.62) * mm, "end": v(-4.74, 9.65) * mm});
            skLineSegment(sketch, "E100.14.30", {"start": v(-4.8, 9.72) * mm, "end": v(-4.84, 9.76) * mm});
            skLineSegment(sketch, "E100.14.31", {"start": v(-4.15, 9.61) * mm, "end": v(-4.15, 9.63) * mm});
            skLineSegment(sketch, "E100.14.32", {"start": v(-4.21, 10.2) * mm, "end": v(-4.21, 10.25) * mm});
            skLineSegment(sketch, "E100.14.33", {"start": v(-4.48, 9.39) * mm, "end": v(-4.48, 9.4) * mm});
            skLineSegment(sketch, "E100.14.34", {"start": v(-4.16, 9.53) * mm, "end": v(-4.16, 9.54) * mm});
            skLineSegment(sketch, "E100.14.35", {"start": v(-4.55, 9.43) * mm, "end": v(-4.56, 9.44) * mm});
            skLineSegment(sketch, "E100.14.36", {"start": v(-4.62, 9.5) * mm, "end": v(-4.65, 9.54) * mm});
            skLineSegment(sketch, "E100.14.37", {"start": v(-4.2, 10.1) * mm, "end": v(-4.2, 10.15) * mm});
            skLineSegment(sketch, "E100.14.38", {"start": v(-4.18, 9.81) * mm, "end": v(-4.18, 9.86) * mm});
            skLineSegment(sketch, "E100.14.39", {"start": v(-4.2, 9.95) * mm, "end": v(-4.2, 10) * mm});
            skLineSegment(sketch, "E100.14.40", {"start": v(-4.3, 9.44) * mm, "end": v(-4.29, 9.45) * mm});
            skLineSegment(sketch, "E100.14.41", {"start": v(-4.29, 9.45) * mm, "end": v(-4.27, 9.46) * mm});
            skLineSegment(sketch, "E100.14.42", {"start": v(-4.88, 9.8) * mm, "end": v(-4.91, 9.83) * mm});
            skLineSegment(sketch, "E100.14.43", {"start": v(-4.84, 9.76) * mm, "end": v(-4.88, 9.8) * mm});
            skLineSegment(sketch, "E100.14.44", {"start": v(-4.2, 10.15) * mm, "end": v(-4.21, 10.2) * mm});
            skLineSegment(sketch, "E100.14.45", {"start": v(-4.15, 9.56) * mm, "end": v(-4.15, 9.57) * mm});
            skLineSegment(sketch, "E100.14.46", {"start": v(-4.2, 9.49) * mm, "end": v(-4.19, 9.5) * mm});
            skLineSegment(sketch, "E100.14.47", {"start": v(-4.2, 10) * mm, "end": v(-4.2, 10.05) * mm});
            skLineSegment(sketch, "E100.14.48", {"start": v(-4.95, 9.86) * mm, "end": v(-4.99, 9.9) * mm});
            skLineSegment(sketch, "E100.14.49", {"start": v(-4.57, 9.45) * mm, "end": v(-4.58, 9.46) * mm});
            skLineSegment(sketch, "E100.14.50", {"start": v(-4.2, 10.05) * mm, "end": v(-4.2, 10.1) * mm});
            skLineSegment(sketch, "E100.14.51", {"start": v(-4.17, 9.76) * mm, "end": v(-4.18, 9.81) * mm});
            skLineSegment(sketch, "E100.14.52", {"start": v(-4.47, 9.38) * mm, "end": v(-4.48, 9.39) * mm});
            skLineSegment(sketch, "E100.14.53", {"start": v(-4.78, 9.69) * mm, "end": v(-4.8, 9.72) * mm});
            skLineSegment(sketch, "E100.14.54", {"start": v(-4.15, 9.65) * mm, "end": v(-4.15, 9.66) * mm});
            skLineSegment(sketch, "E100.14.55", {"start": v(-4.22, 9.48) * mm, "end": v(-4.2, 9.49) * mm});
            skLineSegment(sketch, "E100.14.56", {"start": v(-4.15, 9.6) * mm, "end": v(-4.15, 9.61) * mm});
            skLineSegment(sketch, "E100.14.57", {"start": v(-4.46, 9.38) * mm, "end": v(-4.47, 9.38) * mm});
            skLineSegment(sketch, "E100.14.58", {"start": v(-4.15, 9.68) * mm, "end": v(-4.16, 9.7) * mm});
            skLineSegment(sketch, "E100.14.59", {"start": v(-4.58, 9.46) * mm, "end": v(-4.6, 9.48) * mm});
            skLineSegment(sketch, "E100.14.60", {"start": v(-4.18, 9.86) * mm, "end": v(-4.19, 9.9) * mm});
            skLineSegment(sketch, "E100.14.61", {"start": v(-4.91, 9.83) * mm, "end": v(-4.95, 9.86) * mm});
            skLineSegment(sketch, "E100.14.62", {"start": v(-4.74, 9.65) * mm, "end": v(-4.78, 9.69) * mm});
            skLineSegment(sketch, "E100.14.63", {"start": v(-4.6, 9.5) * mm, "end": v(-4.62, 9.5) * mm});
            skLineSegment(sketch, "E100.14.64", {"start": v(-4.45, 9.38) * mm, "end": v(-4.46, 9.38) * mm});
            skLineSegment(sketch, "E100.14.65", {"start": v(-4.25, 9.47) * mm, "end": v(-4.22, 9.48) * mm});
            skLineSegment(sketch, "E100.14.66", {"start": v(-4.15, 9.66) * mm, "end": v(-4.15, 9.68) * mm});
            skLineSegment(sketch, "E100.14.67", {"start": v(-4.19, 9.9) * mm, "end": v(-4.2, 9.95) * mm});
            skLineSegment(sketch, "E100.14.68", {"start": v(-4.15, 9.59) * mm, "end": v(-4.15, 9.6) * mm});
            skLineSegment(sketch, "E100.14.69", {"start": v(-4.68, 9.58) * mm, "end": v(-4.71, 9.62) * mm});
            skLineSegment(sketch, "E100.14.70", {"start": v(-4.18, 9.5) * mm, "end": v(-4.18, 9.5) * mm});
            skLineSegment(sketch, "E100.14.71", {"start": v(-4.15, 9.63) * mm, "end": v(-4.15, 9.65) * mm});
            skLineSegment(sketch, "E100.14.72", {"start": v(-4.17, 9.51) * mm, "end": v(-4.17, 9.52) * mm});
            skLineSegment(sketch, "E100.14.73", {"start": v(-4.65, 9.54) * mm, "end": v(-4.68, 9.58) * mm});
            skLineSegment(sketch, "E100.14.74", {"start": v(-4.44, 9.38) * mm, "end": v(-4.45, 9.38) * mm});
            skLineSegment(sketch, "E100.14.75", {"start": v(-4.43, 9.38) * mm, "end": v(-4.44, 9.38) * mm});
            skLineSegment(sketch, "E100.14.76", {"start": v(-4.35, 9.42) * mm, "end": v(-4.37, 9.4) * mm});
            skLineSegment(sketch, "E100.14.77", {"start": v(-4.15, 9.57) * mm, "end": v(-4.15, 9.59) * mm});
            skLineSegment(sketch, "E100.14.78", {"start": v(-4.54, 9.42) * mm, "end": v(-4.55, 9.43) * mm});
            skLineSegment(sketch, "E100.14.79", {"start": v(-4.16, 9.72) * mm, "end": v(-4.17, 9.76) * mm});
            skLineSegment(sketch, "E100.14.80", {"start": v(-4.17, 9.52) * mm, "end": v(-4.16, 9.53) * mm});
            skLineSegment(sketch, "E100.14.81", {"start": v(-4.42, 9.39) * mm, "end": v(-4.43, 9.38) * mm});
            skLineSegment(sketch, "E100.14.82", {"start": v(-4.16, 9.7) * mm, "end": v(-4.16, 9.72) * mm});
            skLineSegment(sketch, "E100.14.83", {"start": v(-4.33, 9.43) * mm, "end": v(-4.35, 9.42) * mm});
            skLineSegment(sketch, "E100.14.84", {"start": v(-4.56, 9.44) * mm, "end": v(-4.57, 9.45) * mm});
            skLineSegment(sketch, "E100.14.85", {"start": v(-4.16, 9.55) * mm, "end": v(-4.15, 9.56) * mm});
            skLineSegment(sketch, "E100.14.86", {"start": v(-4.3, 9.44) * mm, "end": v(-4.33, 9.43) * mm});
            skLineSegment(sketch, "E100.14.87", {"start": v(-4.6, 9.48) * mm, "end": v(-4.6, 9.5) * mm});
            skLineSegment(sketch, "E100.14.88", {"start": v(-4.42, 9.39) * mm, "end": v(-4.42, 9.39) * mm});
            skLineSegment(sketch, "E100.14.89", {"start": v(-4.4, 9.4) * mm, "end": v(-4.42, 9.39) * mm});
            skLineSegment(sketch, "E100.14.90", {"start": v(-4.2, 9.49) * mm, "end": v(-4.2, 9.49) * mm});
            skLineSegment(sketch, "E100.14.91", {"start": v(-4.18, 9.5) * mm, "end": v(-4.17, 9.51) * mm});
            skLineSegment(sketch, "E100.14.92", {"start": v(-4.16, 9.54) * mm, "end": v(-4.16, 9.55) * mm});
            skLineSegment(sketch, "E100.14.93", {"start": v(-4.27, 9.46) * mm, "end": v(-4.25, 9.47) * mm});
            skLineSegment(sketch, "E100.14.94", {"start": v(-4.37, 9.4) * mm, "end": v(-4.4, 9.4) * mm});
            skLineSegment(sketch, "E100.14.95", {"start": v(-4.5, 9.4) * mm, "end": v(-4.5, 9.4) * mm});
            skLineSegment(sketch, "E100.14.96", {"start": v(-4.19, 9.5) * mm, "end": v(-4.18, 9.5) * mm});
            skLineSegment(sketch, "E100.14.97", {"start": v(-4.48, 9.4) * mm, "end": v(-4.5, 9.4) * mm});
            skLineSegment(sketch, "E100.14.98", {"start": v(-4.5, 9.4) * mm, "end": v(-4.52, 9.4) * mm});
            skLineSegment(sketch, "E100.14.99", {"start": v(-4.52, 9.4) * mm, "end": v(-4.53, 9.41) * mm});
            skLineSegment(sketch, "E100.15.0", {"start": v(-5.65, 10.02) * mm, "end": v(-5.61, 10.04) * mm});
            skLineSegment(sketch, "E100.15.1", {"start": v(-6.8, 9.27) * mm, "end": v(-6.83, 9.25) * mm});
            skLineSegment(sketch, "E100.15.2", {"start": v(-6.6, 9.24) * mm, "end": v(-6.65, 9.27) * mm});
            skLineSegment(sketch, "E100.15.3", {"start": v(-6.86, 9.23) * mm, "end": v(-6.9, 9.2) * mm});
            skLineSegment(sketch, "E100.15.4", {"start": v(-5.63, 9.55) * mm, "end": v(-5.64, 9.6) * mm});
            skLineSegment(sketch, "E100.15.5", {"start": v(-5.58, 10.06) * mm, "end": v(-5.55, 10.07) * mm});
            skLineSegment(sketch, "E100.15.6", {"start": v(-6.77, 9.3) * mm, "end": v(-6.8, 9.27) * mm});
            skLineSegment(sketch, "E100.15.7", {"start": v(-5.66, 9.8) * mm, "end": v(-5.67, 9.85) * mm});
            skLineSegment(sketch, "E100.15.8", {"start": v(-6.83, 9.25) * mm, "end": v(-6.86, 9.23) * mm});
            skLineSegment(sketch, "E100.15.9", {"start": v(-5.67, 9.85) * mm, "end": v(-5.67, 9.9) * mm});
            skLineSegment(sketch, "E100.15.10", {"start": v(-5.55, 10.07) * mm, "end": v(-5.51, 10.1) * mm});
            skLineSegment(sketch, "E100.15.11", {"start": v(-5.67, 9.9) * mm, "end": v(-5.68, 9.95) * mm});
            skLineSegment(sketch, "E100.15.12", {"start": v(-5.66, 9.74) * mm, "end": v(-5.66, 9.8) * mm});
            skLineSegment(sketch, "E100.15.13", {"start": v(-6.7, 9.3) * mm, "end": v(-6.74, 9.32) * mm});
            skLineSegment(sketch, "E100.15.14", {"start": v(-5.68, 10) * mm, "end": v(-5.65, 10.02) * mm});
            skLineSegment(sketch, "E100.15.15", {"start": v(-5.64, 9.6) * mm, "end": v(-5.64, 9.64) * mm});
            skLineSegment(sketch, "E100.15.16", {"start": v(-5.61, 10.04) * mm, "end": v(-5.58, 10.06) * mm});
            skLineSegment(sketch, "E100.15.17", {"start": v(-6.74, 9.32) * mm, "end": v(-6.77, 9.3) * mm});
            skLineSegment(sketch, "E100.15.18", {"start": v(-6.51, 9.2) * mm, "end": v(-6.56, 9.22) * mm});
            skLineSegment(sketch, "E100.15.19", {"start": v(-5.65, 9.7) * mm, "end": v(-5.66, 9.74) * mm});
            skLineSegment(sketch, "E100.15.20", {"start": v(-5.68, 9.95) * mm, "end": v(-5.68, 10) * mm});
            skLineSegment(sketch, "E100.15.21", {"start": v(-6.39, 9.11) * mm, "end": v(-6.43, 9.14) * mm});
            skLineSegment(sketch, "E100.15.22", {"start": v(-6.56, 9.22) * mm, "end": v(-6.6, 9.24) * mm});
            skLineSegment(sketch, "E100.15.23", {"start": v(-5.64, 9.64) * mm, "end": v(-5.65, 9.7) * mm});
            skLineSegment(sketch, "E100.15.24", {"start": v(-6.43, 9.14) * mm, "end": v(-6.47, 9.17) * mm});
            skLineSegment(sketch, "E100.15.25", {"start": v(-6.47, 9.17) * mm, "end": v(-6.51, 9.2) * mm});
            skLineSegment(sketch, "E100.15.26", {"start": v(-6.65, 9.27) * mm, "end": v(-6.7, 9.3) * mm});
            skLineSegment(sketch, "E100.15.27", {"start": v(-6.34, 9.08) * mm, "end": v(-6.39, 9.11) * mm});
            skLineSegment(sketch, "E100.15.28", {"start": v(-5.82, 8.67) * mm, "end": v(-5.83, 8.68) * mm});
            skLineSegment(sketch, "E100.15.29", {"start": v(-6.03, 8.85) * mm, "end": v(-6.07, 8.88) * mm});
            skLineSegment(sketch, "E100.15.30", {"start": v(-6.14, 8.94) * mm, "end": v(-6.18, 8.97) * mm});
            skLineSegment(sketch, "E100.15.31", {"start": v(-5.47, 8.93) * mm, "end": v(-5.48, 8.94) * mm});
            skLineSegment(sketch, "E100.15.32", {"start": v(-5.62, 9.5) * mm, "end": v(-5.63, 9.55) * mm});
            skLineSegment(sketch, "E100.15.33", {"start": v(-5.77, 8.65) * mm, "end": v(-5.78, 8.66) * mm});
            skLineSegment(sketch, "E100.15.34", {"start": v(-5.48, 8.84) * mm, "end": v(-5.47, 8.85) * mm});
            skLineSegment(sketch, "E100.15.35", {"start": v(-5.84, 8.69) * mm, "end": v(-5.86, 8.7) * mm});
            skLineSegment(sketch, "E100.15.36", {"start": v(-5.93, 8.75) * mm, "end": v(-5.96, 8.78) * mm});
            skLineSegment(sketch, "E100.15.37", {"start": v(-5.6, 9.4) * mm, "end": v(-5.61, 9.45) * mm});
            skLineSegment(sketch, "E100.15.38", {"start": v(-5.53, 9.12) * mm, "end": v(-5.54, 9.16) * mm});
            skLineSegment(sketch, "E100.15.39", {"start": v(-5.57, 9.26) * mm, "end": v(-5.58, 9.3) * mm});
            skLineSegment(sketch, "E100.15.40", {"start": v(-5.6, 8.73) * mm, "end": v(-5.59, 8.74) * mm});
            skLineSegment(sketch, "E100.15.41", {"start": v(-5.59, 8.74) * mm, "end": v(-5.57, 8.75) * mm});
            skLineSegment(sketch, "E100.15.42", {"start": v(-6.22, 9) * mm, "end": v(-6.26, 9.03) * mm});
            skLineSegment(sketch, "E100.15.43", {"start": v(-6.18, 8.97) * mm, "end": v(-6.22, 9) * mm});
            skLineSegment(sketch, "E100.15.44", {"start": v(-5.61, 9.45) * mm, "end": v(-5.62, 9.5) * mm});
            skLineSegment(sketch, "E100.15.45", {"start": v(-5.47, 8.87) * mm, "end": v(-5.47, 8.88) * mm});
            skLineSegment(sketch, "E100.15.46", {"start": v(-5.5, 8.8) * mm, "end": v(-5.5, 8.8) * mm});
            skLineSegment(sketch, "E100.15.47", {"start": v(-5.58, 9.3) * mm, "end": v(-5.6, 9.35) * mm});
            skLineSegment(sketch, "E100.15.48", {"start": v(-6.3, 9.06) * mm, "end": v(-6.34, 9.08) * mm});
            skLineSegment(sketch, "E100.15.49", {"start": v(-5.87, 8.7) * mm, "end": v(-5.88, 8.72) * mm});
            skLineSegment(sketch, "E100.15.50", {"start": v(-5.6, 9.35) * mm, "end": v(-5.6, 9.4) * mm});
            skLineSegment(sketch, "E100.15.51", {"start": v(-5.51, 9.07) * mm, "end": v(-5.53, 9.12) * mm});
            skLineSegment(sketch, "E100.15.52", {"start": v(-5.76, 8.65) * mm, "end": v(-5.77, 8.65) * mm});
            skLineSegment(sketch, "E100.15.53", {"start": v(-6.1, 8.91) * mm, "end": v(-6.14, 8.94) * mm});
            skLineSegment(sketch, "E100.15.54", {"start": v(-5.48, 8.96) * mm, "end": v(-5.48, 8.97) * mm});
            skLineSegment(sketch, "E100.15.55", {"start": v(-5.53, 8.78) * mm, "end": v(-5.51, 8.8) * mm});
            skLineSegment(sketch, "E100.15.56", {"start": v(-5.47, 8.91) * mm, "end": v(-5.47, 8.93) * mm});
            skLineSegment(sketch, "E100.15.57", {"start": v(-5.75, 8.65) * mm, "end": v(-5.76, 8.65) * mm});
            skLineSegment(sketch, "E100.15.58", {"start": v(-5.49, 8.99) * mm, "end": v(-5.5, 9) * mm});
            skLineSegment(sketch, "E100.15.59", {"start": v(-5.88, 8.72) * mm, "end": v(-5.9, 8.73) * mm});
            skLineSegment(sketch, "E100.15.60", {"start": v(-5.54, 9.16) * mm, "end": v(-5.56, 9.2) * mm});
            skLineSegment(sketch, "E100.15.61", {"start": v(-6.26, 9.03) * mm, "end": v(-6.3, 9.06) * mm});
            skLineSegment(sketch, "E100.15.62", {"start": v(-6.07, 8.88) * mm, "end": v(-6.1, 8.91) * mm});
            skLineSegment(sketch, "E100.15.63", {"start": v(-5.91, 8.74) * mm, "end": v(-5.93, 8.75) * mm});
            skLineSegment(sketch, "E100.15.64", {"start": v(-5.74, 8.65) * mm, "end": v(-5.75, 8.65) * mm});
            skLineSegment(sketch, "E100.15.65", {"start": v(-5.55, 8.77) * mm, "end": v(-5.53, 8.78) * mm});
            skLineSegment(sketch, "E100.15.66", {"start": v(-5.48, 8.97) * mm, "end": v(-5.49, 8.99) * mm});
            skLineSegment(sketch, "E100.15.67", {"start": v(-5.56, 9.2) * mm, "end": v(-5.57, 9.26) * mm});
            skLineSegment(sketch, "E100.15.68", {"start": v(-5.47, 8.9) * mm, "end": v(-5.47, 8.91) * mm});
            skLineSegment(sketch, "E100.15.69", {"start": v(-6, 8.82) * mm, "end": v(-6.03, 8.85) * mm});
            skLineSegment(sketch, "E100.15.70", {"start": v(-5.5, 8.8) * mm, "end": v(-5.49, 8.81) * mm});
            skLineSegment(sketch, "E100.15.71", {"start": v(-5.48, 8.94) * mm, "end": v(-5.48, 8.96) * mm});
            skLineSegment(sketch, "E100.15.72", {"start": v(-5.48, 8.82) * mm, "end": v(-5.48, 8.83) * mm});
            skLineSegment(sketch, "E100.15.73", {"start": v(-5.96, 8.78) * mm, "end": v(-6, 8.82) * mm});
            skLineSegment(sketch, "E100.15.74", {"start": v(-5.73, 8.65) * mm, "end": v(-5.74, 8.65) * mm});
            skLineSegment(sketch, "E100.15.75", {"start": v(-5.72, 8.66) * mm, "end": v(-5.73, 8.65) * mm});
            skLineSegment(sketch, "E100.15.76", {"start": v(-5.65, 8.7) * mm, "end": v(-5.67, 8.69) * mm});
            skLineSegment(sketch, "E100.15.77", {"start": v(-5.47, 8.88) * mm, "end": v(-5.47, 8.9) * mm});
            skLineSegment(sketch, "E100.15.78", {"start": v(-5.83, 8.68) * mm, "end": v(-5.84, 8.69) * mm});
            skLineSegment(sketch, "E100.15.79", {"start": v(-5.5, 9.03) * mm, "end": v(-5.51, 9.07) * mm});
            skLineSegment(sketch, "E100.15.80", {"start": v(-5.48, 8.83) * mm, "end": v(-5.48, 8.84) * mm});
            skLineSegment(sketch, "E100.15.81", {"start": v(-5.71, 8.66) * mm, "end": v(-5.72, 8.66) * mm});
            skLineSegment(sketch, "E100.15.82", {"start": v(-5.5, 9) * mm, "end": v(-5.5, 9.03) * mm});
            skLineSegment(sketch, "E100.15.83", {"start": v(-5.63, 8.72) * mm, "end": v(-5.65, 8.7) * mm});
            skLineSegment(sketch, "E100.15.84", {"start": v(-5.86, 8.7) * mm, "end": v(-5.87, 8.7) * mm});
            skLineSegment(sketch, "E100.15.85", {"start": v(-5.47, 8.86) * mm, "end": v(-5.47, 8.87) * mm});
            skLineSegment(sketch, "E100.15.86", {"start": v(-5.6, 8.73) * mm, "end": v(-5.63, 8.72) * mm});
            skLineSegment(sketch, "E100.15.87", {"start": v(-5.9, 8.73) * mm, "end": v(-5.91, 8.74) * mm});
            skLineSegment(sketch, "E100.15.88", {"start": v(-5.7, 8.66) * mm, "end": v(-5.71, 8.66) * mm});
            skLineSegment(sketch, "E100.15.89", {"start": v(-5.69, 8.68) * mm, "end": v(-5.7, 8.66) * mm});
            skLineSegment(sketch, "E100.15.90", {"start": v(-5.51, 8.8) * mm, "end": v(-5.5, 8.8) * mm});
            skLineSegment(sketch, "E100.15.91", {"start": v(-5.49, 8.81) * mm, "end": v(-5.48, 8.82) * mm});
            skLineSegment(sketch, "E100.15.92", {"start": v(-5.47, 8.85) * mm, "end": v(-5.47, 8.86) * mm});
            skLineSegment(sketch, "E100.15.93", {"start": v(-5.57, 8.75) * mm, "end": v(-5.55, 8.77) * mm});
            skLineSegment(sketch, "E100.15.94", {"start": v(-5.67, 8.69) * mm, "end": v(-5.69, 8.68) * mm});
            skLineSegment(sketch, "E100.15.95", {"start": v(-5.79, 8.66) * mm, "end": v(-5.8, 8.66) * mm});
            skLineSegment(sketch, "E100.15.96", {"start": v(-5.5, 8.8) * mm, "end": v(-5.5, 8.8) * mm});
            skLineSegment(sketch, "E100.15.97", {"start": v(-5.78, 8.66) * mm, "end": v(-5.79, 8.66) * mm});
            skLineSegment(sketch, "E100.15.98", {"start": v(-5.8, 8.66) * mm, "end": v(-5.8, 8.67) * mm});
            skLineSegment(sketch, "E100.15.99", {"start": v(-5.8, 8.67) * mm, "end": v(-5.82, 8.67) * mm});
            skLineSegment(sketch, "E100.16.0", {"start": v(-7.01, 9.11) * mm, "end": v(-6.98, 9.14) * mm});
            skLineSegment(sketch, "E100.16.1", {"start": v(-8.05, 8.21) * mm, "end": v(-8.08, 8.19) * mm});
            skLineSegment(sketch, "E100.16.2", {"start": v(-7.85, 8.21) * mm, "end": v(-7.9, 8.23) * mm});
            skLineSegment(sketch, "E100.16.3", {"start": v(-8.1, 8.16) * mm, "end": v(-8.13, 8.13) * mm});
            skLineSegment(sketch, "E100.16.4", {"start": v(-6.93, 8.65) * mm, "end": v(-6.94, 8.7) * mm});
            skLineSegment(sketch, "E100.16.5", {"start": v(-6.95, 9.16) * mm, "end": v(-6.92, 9.18) * mm});
            skLineSegment(sketch, "E100.16.6", {"start": v(-8.02, 8.24) * mm, "end": v(-8.05, 8.21) * mm});
            skLineSegment(sketch, "E100.16.7", {"start": v(-7, 8.89) * mm, "end": v(-7.01, 8.94) * mm});
            skLineSegment(sketch, "E100.16.8", {"start": v(-8.08, 8.19) * mm, "end": v(-8.1, 8.16) * mm});
            skLineSegment(sketch, "E100.16.9", {"start": v(-7.01, 8.94) * mm, "end": v(-7.02, 8.99) * mm});
            skLineSegment(sketch, "E100.16.10", {"start": v(-6.92, 9.18) * mm, "end": v(-6.9, 9.2) * mm});
            skLineSegment(sketch, "E100.16.11", {"start": v(-7.02, 8.99) * mm, "end": v(-7.03, 9.04) * mm});
            skLineSegment(sketch, "E100.16.12", {"start": v(-6.99, 8.84) * mm, "end": v(-7, 8.89) * mm});
            skLineSegment(sketch, "E100.16.13", {"start": v(-7.95, 8.25) * mm, "end": v(-8, 8.27) * mm});
            skLineSegment(sketch, "E100.16.14", {"start": v(-7.04, 9.09) * mm, "end": v(-7.01, 9.11) * mm});
            skLineSegment(sketch, "E100.16.15", {"start": v(-6.94, 8.7) * mm, "end": v(-6.96, 8.74) * mm});
            skLineSegment(sketch, "E100.16.16", {"start": v(-6.98, 9.14) * mm, "end": v(-6.95, 9.16) * mm});
            skLineSegment(sketch, "E100.16.17", {"start": v(-8, 8.27) * mm, "end": v(-8.02, 8.24) * mm});
            skLineSegment(sketch, "E100.16.18", {"start": v(-7.76, 8.17) * mm, "end": v(-7.8, 8.2) * mm});
            skLineSegment(sketch, "E100.16.19", {"start": v(-6.97, 8.8) * mm, "end": v(-6.99, 8.84) * mm});
            skLineSegment(sketch, "E100.16.20", {"start": v(-7.03, 9.04) * mm, "end": v(-7.04, 9.09) * mm});
            skLineSegment(sketch, "E100.16.21", {"start": v(-7.62, 8.11) * mm, "end": v(-7.66, 8.13) * mm});
            skLineSegment(sketch, "E100.16.22", {"start": v(-7.8, 8.2) * mm, "end": v(-7.85, 8.21) * mm});
            skLineSegment(sketch, "E100.16.23", {"start": v(-6.96, 8.74) * mm, "end": v(-6.97, 8.8) * mm});
            skLineSegment(sketch, "E100.16.24", {"start": v(-7.66, 8.13) * mm, "end": v(-7.71, 8.15) * mm});
            skLineSegment(sketch, "E100.16.25", {"start": v(-7.71, 8.15) * mm, "end": v(-7.76, 8.17) * mm});
            skLineSegment(sketch, "E100.16.26", {"start": v(-7.9, 8.23) * mm, "end": v(-7.95, 8.25) * mm});
            skLineSegment(sketch, "E100.16.27", {"start": v(-7.57, 8.09) * mm, "end": v(-7.62, 8.11) * mm});
            skLineSegment(sketch, "E100.16.28", {"start": v(-7, 7.76) * mm, "end": v(-7, 7.76) * mm});
            skLineSegment(sketch, "E100.16.29", {"start": v(-7.23, 7.9) * mm, "end": v(-7.27, 7.93) * mm});
            skLineSegment(sketch, "E100.16.30", {"start": v(-7.35, 7.97) * mm, "end": v(-7.4, 8) * mm});
            skLineSegment(sketch, "E100.16.31", {"start": v(-6.69, 8.06) * mm, "end": v(-6.7, 8.07) * mm});
            skLineSegment(sketch, "E100.16.32", {"start": v(-6.91, 8.6) * mm, "end": v(-6.93, 8.65) * mm});
            skLineSegment(sketch, "E100.16.33", {"start": v(-6.94, 7.75) * mm, "end": v(-6.95, 7.75) * mm});
            skLineSegment(sketch, "E100.16.34", {"start": v(-6.68, 7.97) * mm, "end": v(-6.68, 7.98) * mm});
            skLineSegment(sketch, "E100.16.35", {"start": v(-7.02, 7.77) * mm, "end": v(-7.04, 7.77) * mm});
            skLineSegment(sketch, "E100.16.36", {"start": v(-7.11, 7.82) * mm, "end": v(-7.15, 7.85) * mm});
            skLineSegment(sketch, "E100.16.37", {"start": v(-6.88, 8.5) * mm, "end": v(-6.9, 8.55) * mm});
            skLineSegment(sketch, "E100.16.38", {"start": v(-6.77, 8.24) * mm, "end": v(-6.8, 8.28) * mm});
            skLineSegment(sketch, "E100.16.39", {"start": v(-6.83, 8.37) * mm, "end": v(-6.85, 8.41) * mm});
            skLineSegment(sketch, "E100.16.40", {"start": v(-6.8, 7.84) * mm, "end": v(-6.78, 7.86) * mm});
            skLineSegment(sketch, "E100.16.41", {"start": v(-6.78, 7.86) * mm, "end": v(-6.76, 7.87) * mm});
            skLineSegment(sketch, "E100.16.42", {"start": v(-7.44, 8.02) * mm, "end": v(-7.48, 8.05) * mm});
            skLineSegment(sketch, "E100.16.43", {"start": v(-7.4, 8) * mm, "end": v(-7.44, 8.02) * mm});
            skLineSegment(sketch, "E100.16.44", {"start": v(-6.9, 8.55) * mm, "end": v(-6.91, 8.6) * mm});
            skLineSegment(sketch, "E100.16.45", {"start": v(-6.68, 8) * mm, "end": v(-6.68, 8.02) * mm});
            skLineSegment(sketch, "E100.16.46", {"start": v(-6.7, 7.92) * mm, "end": v(-6.7, 7.93) * mm});
            skLineSegment(sketch, "E100.16.47", {"start": v(-6.85, 8.41) * mm, "end": v(-6.86, 8.46) * mm});
            skLineSegment(sketch, "E100.16.48", {"start": v(-7.53, 8.07) * mm, "end": v(-7.57, 8.09) * mm});
            skLineSegment(sketch, "E100.16.49", {"start": v(-7.05, 7.78) * mm, "end": v(-7.06, 7.79) * mm});
            skLineSegment(sketch, "E100.16.50", {"start": v(-6.86, 8.46) * mm, "end": v(-6.88, 8.5) * mm});
            skLineSegment(sketch, "E100.16.51", {"start": v(-6.75, 8.2) * mm, "end": v(-6.77, 8.24) * mm});
            skLineSegment(sketch, "E100.16.52", {"start": v(-6.93, 7.75) * mm, "end": v(-6.94, 7.75) * mm});
            skLineSegment(sketch, "E100.16.53", {"start": v(-7.31, 7.95) * mm, "end": v(-7.35, 7.97) * mm});
            skLineSegment(sketch, "E100.16.54", {"start": v(-6.7, 8.09) * mm, "end": v(-6.7, 8.1) * mm});
            skLineSegment(sketch, "E100.16.55", {"start": v(-6.72, 7.9) * mm, "end": v(-6.7, 7.92) * mm});
            skLineSegment(sketch, "E100.16.56", {"start": v(-6.69, 8.04) * mm, "end": v(-6.69, 8.06) * mm});
            skLineSegment(sketch, "E100.16.57", {"start": v(-6.92, 7.75) * mm, "end": v(-6.93, 7.75) * mm});
            skLineSegment(sketch, "E100.16.58", {"start": v(-6.71, 8.12) * mm, "end": v(-6.72, 8.13) * mm});
            skLineSegment(sketch, "E100.16.59", {"start": v(-7.06, 7.79) * mm, "end": v(-7.08, 7.8) * mm});
            skLineSegment(sketch, "E100.16.60", {"start": v(-6.8, 8.28) * mm, "end": v(-6.81, 8.32) * mm});
            skLineSegment(sketch, "E100.16.61", {"start": v(-7.48, 8.05) * mm, "end": v(-7.53, 8.07) * mm});
            skLineSegment(sketch, "E100.16.62", {"start": v(-7.27, 7.93) * mm, "end": v(-7.31, 7.95) * mm});
            skLineSegment(sketch, "E100.16.63", {"start": v(-7.1, 7.8) * mm, "end": v(-7.11, 7.82) * mm});
            skLineSegment(sketch, "E100.16.64", {"start": v(-6.91, 7.75) * mm, "end": v(-6.92, 7.75) * mm});
            skLineSegment(sketch, "E100.16.65", {"start": v(-6.74, 7.89) * mm, "end": v(-6.72, 7.9) * mm});
            skLineSegment(sketch, "E100.16.66", {"start": v(-6.7, 8.1) * mm, "end": v(-6.71, 8.12) * mm});
            skLineSegment(sketch, "E100.16.67", {"start": v(-6.81, 8.32) * mm, "end": v(-6.83, 8.37) * mm});
            skLineSegment(sketch, "E100.16.68", {"start": v(-6.68, 8.03) * mm, "end": v(-6.69, 8.04) * mm});
            skLineSegment(sketch, "E100.16.69", {"start": v(-7.19, 7.87) * mm, "end": v(-7.23, 7.9) * mm});
            skLineSegment(sketch, "E100.16.70", {"start": v(-6.7, 7.94) * mm, "end": v(-6.69, 7.94) * mm});
            skLineSegment(sketch, "E100.16.71", {"start": v(-6.7, 8.07) * mm, "end": v(-6.7, 8.09) * mm});
            skLineSegment(sketch, "E100.16.72", {"start": v(-6.68, 7.95) * mm, "end": v(-6.68, 7.96) * mm});
            skLineSegment(sketch, "E100.16.73", {"start": v(-7.15, 7.85) * mm, "end": v(-7.19, 7.87) * mm});
            skLineSegment(sketch, "E100.16.74", {"start": v(-6.9, 7.75) * mm, "end": v(-6.91, 7.75) * mm});
            skLineSegment(sketch, "E100.16.75", {"start": v(-6.9, 7.75) * mm, "end": v(-6.9, 7.75) * mm});
            skLineSegment(sketch, "E100.16.76", {"start": v(-6.83, 7.81) * mm, "end": v(-6.85, 7.8) * mm});
            skLineSegment(sketch, "E100.16.77", {"start": v(-6.68, 8.02) * mm, "end": v(-6.68, 8.03) * mm});
            skLineSegment(sketch, "E100.16.78", {"start": v(-7, 7.76) * mm, "end": v(-7.02, 7.77) * mm});
            skLineSegment(sketch, "E100.16.79", {"start": v(-6.73, 8.15) * mm, "end": v(-6.75, 8.2) * mm});
            skLineSegment(sketch, "E100.16.80", {"start": v(-6.68, 7.96) * mm, "end": v(-6.68, 7.97) * mm});
            skLineSegment(sketch, "E100.16.81", {"start": v(-6.89, 7.76) * mm, "end": v(-6.9, 7.75) * mm});
            skLineSegment(sketch, "E100.16.82", {"start": v(-6.72, 8.13) * mm, "end": v(-6.73, 8.15) * mm});
            skLineSegment(sketch, "E100.16.83", {"start": v(-6.81, 7.83) * mm, "end": v(-6.83, 7.81) * mm});
            skLineSegment(sketch, "E100.16.84", {"start": v(-7.04, 7.77) * mm, "end": v(-7.05, 7.78) * mm});
            skLineSegment(sketch, "E100.16.85", {"start": v(-6.68, 8) * mm, "end": v(-6.68, 8) * mm});
            skLineSegment(sketch, "E100.16.86", {"start": v(-6.8, 7.84) * mm, "end": v(-6.81, 7.83) * mm});
            skLineSegment(sketch, "E100.16.87", {"start": v(-7.08, 7.8) * mm, "end": v(-7.1, 7.8) * mm});
            skLineSegment(sketch, "E100.16.88", {"start": v(-6.88, 7.76) * mm, "end": v(-6.89, 7.76) * mm});
            skLineSegment(sketch, "E100.16.89", {"start": v(-6.86, 7.78) * mm, "end": v(-6.88, 7.76) * mm});
            skLineSegment(sketch, "E100.16.90", {"start": v(-6.7, 7.92) * mm, "end": v(-6.7, 7.92) * mm});
            skLineSegment(sketch, "E100.16.91", {"start": v(-6.69, 7.94) * mm, "end": v(-6.68, 7.95) * mm});
            skLineSegment(sketch, "E100.16.92", {"start": v(-6.68, 7.98) * mm, "end": v(-6.68, 8) * mm});
            skLineSegment(sketch, "E100.16.93", {"start": v(-6.76, 7.87) * mm, "end": v(-6.74, 7.89) * mm});
            skLineSegment(sketch, "E100.16.94", {"start": v(-6.85, 7.8) * mm, "end": v(-6.86, 7.78) * mm});
            skLineSegment(sketch, "E100.16.95", {"start": v(-6.96, 7.75) * mm, "end": v(-6.97, 7.75) * mm});
            skLineSegment(sketch, "E100.16.96", {"start": v(-6.7, 7.93) * mm, "end": v(-6.7, 7.94) * mm});
            skLineSegment(sketch, "E100.16.97", {"start": v(-6.95, 7.75) * mm, "end": v(-6.96, 7.75) * mm});
            skLineSegment(sketch, "E100.16.98", {"start": v(-6.97, 7.75) * mm, "end": v(-6.98, 7.75) * mm});
            skLineSegment(sketch, "E100.16.99", {"start": v(-6.98, 7.75) * mm, "end": v(-7, 7.76) * mm});
            skLineSegment(sketch, "E100.17.0", {"start": v(-8.24, 8.02) * mm, "end": v(-8.21, 8.05) * mm});
            skLineSegment(sketch, "E100.17.1", {"start": v(-9.14, 6.98) * mm, "end": v(-9.16, 6.95) * mm});
            skLineSegment(sketch, "E100.17.2", {"start": v(-8.94, 7.01) * mm, "end": v(-8.99, 7.02) * mm});
            skLineSegment(sketch, "E100.17.3", {"start": v(-9.18, 6.92) * mm, "end": v(-9.2, 6.9) * mm});
            skLineSegment(sketch, "E100.17.4", {"start": v(-8.09, 7.57) * mm, "end": v(-8.11, 7.62) * mm});
            skLineSegment(sketch, "E100.17.5", {"start": v(-8.19, 8.08) * mm, "end": v(-8.16, 8.1) * mm});
            skLineSegment(sketch, "E100.17.6", {"start": v(-9.11, 7.01) * mm, "end": v(-9.14, 6.98) * mm});
            skLineSegment(sketch, "E100.17.7", {"start": v(-8.2, 7.8) * mm, "end": v(-8.21, 7.85) * mm});
            skLineSegment(sketch, "E100.17.8", {"start": v(-9.16, 6.95) * mm, "end": v(-9.18, 6.92) * mm});
            skLineSegment(sketch, "E100.17.9", {"start": v(-8.21, 7.85) * mm, "end": v(-8.23, 7.9) * mm});
            skLineSegment(sketch, "E100.17.10", {"start": v(-8.16, 8.1) * mm, "end": v(-8.13, 8.13) * mm});
            skLineSegment(sketch, "E100.17.11", {"start": v(-8.23, 7.9) * mm, "end": v(-8.25, 7.95) * mm});
            skLineSegment(sketch, "E100.17.12", {"start": v(-8.17, 7.76) * mm, "end": v(-8.2, 7.8) * mm});
            skLineSegment(sketch, "E100.17.13", {"start": v(-9.04, 7.03) * mm, "end": v(-9.09, 7.04) * mm});
            skLineSegment(sketch, "E100.17.14", {"start": v(-8.27, 8) * mm, "end": v(-8.24, 8.02) * mm});
            skLineSegment(sketch, "E100.17.15", {"start": v(-8.11, 7.62) * mm, "end": v(-8.13, 7.66) * mm});
            skLineSegment(sketch, "E100.17.16", {"start": v(-8.21, 8.05) * mm, "end": v(-8.19, 8.08) * mm});
            skLineSegment(sketch, "E100.17.17", {"start": v(-9.09, 7.04) * mm, "end": v(-9.11, 7.01) * mm});
            skLineSegment(sketch, "E100.17.18", {"start": v(-8.84, 6.99) * mm, "end": v(-8.89, 7) * mm});
            skLineSegment(sketch, "E100.17.19", {"start": v(-8.15, 7.71) * mm, "end": v(-8.17, 7.76) * mm});
            skLineSegment(sketch, "E100.17.20", {"start": v(-8.25, 7.95) * mm, "end": v(-8.27, 8) * mm});
            skLineSegment(sketch, "E100.17.21", {"start": v(-8.7, 6.94) * mm, "end": v(-8.74, 6.96) * mm});
            skLineSegment(sketch, "E100.17.22", {"start": v(-8.89, 7) * mm, "end": v(-8.94, 7.01) * mm});
            skLineSegment(sketch, "E100.17.23", {"start": v(-8.13, 7.66) * mm, "end": v(-8.15, 7.71) * mm});
            skLineSegment(sketch, "E100.17.24", {"start": v(-8.74, 6.96) * mm, "end": v(-8.8, 6.97) * mm});
            skLineSegment(sketch, "E100.17.25", {"start": v(-8.8, 6.97) * mm, "end": v(-8.84, 6.99) * mm});
            skLineSegment(sketch, "E100.17.26", {"start": v(-8.99, 7.02) * mm, "end": v(-9.04, 7.03) * mm});
            skLineSegment(sketch, "E100.17.27", {"start": v(-8.65, 6.93) * mm, "end": v(-8.7, 6.94) * mm});
            skLineSegment(sketch, "E100.17.28", {"start": v(-8.03, 6.68) * mm, "end": v(-8.04, 6.69) * mm});
            skLineSegment(sketch, "E100.17.29", {"start": v(-8.28, 6.8) * mm, "end": v(-8.32, 6.81) * mm});
            skLineSegment(sketch, "E100.17.30", {"start": v(-8.41, 6.85) * mm, "end": v(-8.46, 6.86) * mm});
            skLineSegment(sketch, "E100.17.31", {"start": v(-7.77, 7.02) * mm, "end": v(-7.77, 7.04) * mm});
            skLineSegment(sketch, "E100.17.32", {"start": v(-8.07, 7.53) * mm, "end": v(-8.09, 7.57) * mm});
            skLineSegment(sketch, "E100.17.33", {"start": v(-7.97, 6.68) * mm, "end": v(-7.98, 6.68) * mm});
            skLineSegment(sketch, "E100.17.34", {"start": v(-7.75, 6.94) * mm, "end": v(-7.75, 6.95) * mm});
            skLineSegment(sketch, "E100.17.35", {"start": v(-8.06, 6.69) * mm, "end": v(-8.07, 6.7) * mm});
            skLineSegment(sketch, "E100.17.36", {"start": v(-8.15, 6.73) * mm, "end": v(-8.2, 6.75) * mm});
            skLineSegment(sketch, "E100.17.37", {"start": v(-8.02, 7.44) * mm, "end": v(-8.05, 7.48) * mm});
            skLineSegment(sketch, "E100.17.38", {"start": v(-7.87, 7.19) * mm, "end": v(-7.9, 7.23) * mm});
            skLineSegment(sketch, "E100.17.39", {"start": v(-7.95, 7.31) * mm, "end": v(-7.97, 7.35) * mm});
            skLineSegment(sketch, "E100.17.40", {"start": v(-7.84, 6.8) * mm, "end": v(-7.83, 6.81) * mm});
            skLineSegment(sketch, "E100.17.41", {"start": v(-7.83, 6.81) * mm, "end": v(-7.81, 6.83) * mm});
            skLineSegment(sketch, "E100.17.42", {"start": v(-8.5, 6.88) * mm, "end": v(-8.55, 6.9) * mm});
            skLineSegment(sketch, "E100.17.43", {"start": v(-8.46, 6.86) * mm, "end": v(-8.5, 6.88) * mm});
            skLineSegment(sketch, "E100.17.44", {"start": v(-8.05, 7.48) * mm, "end": v(-8.07, 7.53) * mm});
            skLineSegment(sketch, "E100.17.45", {"start": v(-7.75, 6.97) * mm, "end": v(-7.75, 6.98) * mm});
            skLineSegment(sketch, "E100.17.46", {"start": v(-7.76, 6.89) * mm, "end": v(-7.75, 6.9) * mm});
            skLineSegment(sketch, "E100.17.47", {"start": v(-7.97, 7.35) * mm, "end": v(-8, 7.4) * mm});
            skLineSegment(sketch, "E100.17.48", {"start": v(-8.6, 6.91) * mm, "end": v(-8.65, 6.93) * mm});
            skLineSegment(sketch, "E100.17.49", {"start": v(-8.09, 6.7) * mm, "end": v(-8.1, 6.7) * mm});
            skLineSegment(sketch, "E100.17.50", {"start": v(-8, 7.4) * mm, "end": v(-8.02, 7.44) * mm});
            skLineSegment(sketch, "E100.17.51", {"start": v(-7.85, 7.15) * mm, "end": v(-7.87, 7.19) * mm});
            skLineSegment(sketch, "E100.17.52", {"start": v(-7.96, 6.68) * mm, "end": v(-7.97, 6.68) * mm});
            skLineSegment(sketch, "E100.17.53", {"start": v(-8.37, 6.83) * mm, "end": v(-8.41, 6.85) * mm});
            skLineSegment(sketch, "E100.17.54", {"start": v(-7.78, 7.05) * mm, "end": v(-7.79, 7.06) * mm});
            skLineSegment(sketch, "E100.17.55", {"start": v(-7.78, 6.86) * mm, "end": v(-7.76, 6.88) * mm});
            skLineSegment(sketch, "E100.17.56", {"start": v(-7.76, 7) * mm, "end": v(-7.77, 7.02) * mm});
            skLineSegment(sketch, "E100.17.57", {"start": v(-7.95, 6.68) * mm, "end": v(-7.96, 6.68) * mm});
            skLineSegment(sketch, "E100.17.58", {"start": v(-7.8, 7.08) * mm, "end": v(-7.8, 7.1) * mm});
            skLineSegment(sketch, "E100.17.59", {"start": v(-8.1, 6.7) * mm, "end": v(-8.12, 6.71) * mm});
            skLineSegment(sketch, "E100.17.60", {"start": v(-7.9, 7.23) * mm, "end": v(-7.93, 7.27) * mm});
            skLineSegment(sketch, "E100.17.61", {"start": v(-8.55, 6.9) * mm, "end": v(-8.6, 6.91) * mm});
            skLineSegment(sketch, "E100.17.62", {"start": v(-8.32, 6.81) * mm, "end": v(-8.37, 6.83) * mm});
            skLineSegment(sketch, "E100.17.63", {"start": v(-8.13, 6.72) * mm, "end": v(-8.15, 6.73) * mm});
            skLineSegment(sketch, "E100.17.64", {"start": v(-7.94, 6.69) * mm, "end": v(-7.95, 6.68) * mm});
            skLineSegment(sketch, "E100.17.65", {"start": v(-7.8, 6.85) * mm, "end": v(-7.78, 6.86) * mm});
            skLineSegment(sketch, "E100.17.66", {"start": v(-7.79, 7.06) * mm, "end": v(-7.8, 7.08) * mm});
            skLineSegment(sketch, "E100.17.67", {"start": v(-7.93, 7.27) * mm, "end": v(-7.95, 7.31) * mm});
            skLineSegment(sketch, "E100.17.68", {"start": v(-7.76, 7) * mm, "end": v(-7.76, 7) * mm});
            skLineSegment(sketch, "E100.17.69", {"start": v(-8.24, 6.77) * mm, "end": v(-8.28, 6.8) * mm});
            skLineSegment(sketch, "E100.17.70", {"start": v(-7.75, 6.9) * mm, "end": v(-7.75, 6.91) * mm});
            skLineSegment(sketch, "E100.17.71", {"start": v(-7.77, 7.04) * mm, "end": v(-7.78, 7.05) * mm});
            skLineSegment(sketch, "E100.17.72", {"start": v(-7.75, 6.92) * mm, "end": v(-7.75, 6.93) * mm});
            skLineSegment(sketch, "E100.17.73", {"start": v(-8.2, 6.75) * mm, "end": v(-8.24, 6.77) * mm});
            skLineSegment(sketch, "E100.17.74", {"start": v(-7.94, 6.7) * mm, "end": v(-7.94, 6.69) * mm});
            skLineSegment(sketch, "E100.17.75", {"start": v(-7.93, 6.7) * mm, "end": v(-7.94, 6.7) * mm});
            skLineSegment(sketch, "E100.17.76", {"start": v(-7.87, 6.76) * mm, "end": v(-7.89, 6.74) * mm});
            skLineSegment(sketch, "E100.17.77", {"start": v(-7.75, 6.98) * mm, "end": v(-7.76, 7) * mm});
            skLineSegment(sketch, "E100.17.78", {"start": v(-8.04, 6.69) * mm, "end": v(-8.06, 6.69) * mm});
            skLineSegment(sketch, "E100.17.79", {"start": v(-7.82, 7.11) * mm, "end": v(-7.85, 7.15) * mm});
            skLineSegment(sketch, "E100.17.80", {"start": v(-7.75, 6.93) * mm, "end": v(-7.75, 6.94) * mm});
            skLineSegment(sketch, "E100.17.81", {"start": v(-7.92, 6.7) * mm, "end": v(-7.93, 6.7) * mm});
            skLineSegment(sketch, "E100.17.82", {"start": v(-7.8, 7.1) * mm, "end": v(-7.82, 7.11) * mm});
            skLineSegment(sketch, "E100.17.83", {"start": v(-7.86, 6.78) * mm, "end": v(-7.87, 6.76) * mm});
            skLineSegment(sketch, "E100.17.84", {"start": v(-8.07, 6.7) * mm, "end": v(-8.09, 6.7) * mm});
            skLineSegment(sketch, "E100.17.85", {"start": v(-7.75, 6.96) * mm, "end": v(-7.75, 6.97) * mm});
            skLineSegment(sketch, "E100.17.86", {"start": v(-7.84, 6.8) * mm, "end": v(-7.86, 6.78) * mm});
            skLineSegment(sketch, "E100.17.87", {"start": v(-8.12, 6.71) * mm, "end": v(-8.13, 6.72) * mm});
            skLineSegment(sketch, "E100.17.88", {"start": v(-7.92, 6.7) * mm, "end": v(-7.92, 6.7) * mm});
            skLineSegment(sketch, "E100.17.89", {"start": v(-7.9, 6.72) * mm, "end": v(-7.92, 6.7) * mm});
            skLineSegment(sketch, "E100.17.90", {"start": v(-7.76, 6.88) * mm, "end": v(-7.76, 6.89) * mm});
            skLineSegment(sketch, "E100.17.91", {"start": v(-7.75, 6.91) * mm, "end": v(-7.75, 6.92) * mm});
            skLineSegment(sketch, "E100.17.92", {"start": v(-7.75, 6.95) * mm, "end": v(-7.75, 6.96) * mm});
            skLineSegment(sketch, "E100.17.93", {"start": v(-7.81, 6.83) * mm, "end": v(-7.8, 6.85) * mm});
            skLineSegment(sketch, "E100.17.94", {"start": v(-7.89, 6.74) * mm, "end": v(-7.9, 6.72) * mm});
            skLineSegment(sketch, "E100.17.95", {"start": v(-8, 6.68) * mm, "end": v(-8, 6.68) * mm});
            skLineSegment(sketch, "E100.17.96", {"start": v(-7.75, 6.9) * mm, "end": v(-7.75, 6.9) * mm});
            skLineSegment(sketch, "E100.17.97", {"start": v(-7.98, 6.68) * mm, "end": v(-8, 6.68) * mm});
            skLineSegment(sketch, "E100.17.98", {"start": v(-8, 6.68) * mm, "end": v(-8.02, 6.68) * mm});
            skLineSegment(sketch, "E100.17.99", {"start": v(-8.02, 6.68) * mm, "end": v(-8.03, 6.68) * mm});
            skLineSegment(sketch, "E100.18.0", {"start": v(-9.3, 6.77) * mm, "end": v(-9.27, 6.8) * mm});
            skLineSegment(sketch, "E100.18.1", {"start": v(-10.04, 5.61) * mm, "end": v(-10.06, 5.58) * mm});
            skLineSegment(sketch, "E100.18.2", {"start": v(-9.85, 5.67) * mm, "end": v(-9.9, 5.67) * mm});
            skLineSegment(sketch, "E100.18.3", {"start": v(-10.07, 5.55) * mm, "end": v(-10.1, 5.51) * mm});
            skLineSegment(sketch, "E100.18.4", {"start": v(-9.08, 6.34) * mm, "end": v(-9.11, 6.39) * mm});
            skLineSegment(sketch, "E100.18.5", {"start": v(-9.25, 6.83) * mm, "end": v(-9.23, 6.86) * mm});
            skLineSegment(sketch, "E100.18.6", {"start": v(-10.02, 5.65) * mm, "end": v(-10.04, 5.61) * mm});
            skLineSegment(sketch, "E100.18.7", {"start": v(-9.22, 6.56) * mm, "end": v(-9.24, 6.6) * mm});
            skLineSegment(sketch, "E100.18.8", {"start": v(-10.06, 5.58) * mm, "end": v(-10.07, 5.55) * mm});
            skLineSegment(sketch, "E100.18.9", {"start": v(-9.24, 6.6) * mm, "end": v(-9.27, 6.65) * mm});
            skLineSegment(sketch, "E100.18.10", {"start": v(-9.23, 6.86) * mm, "end": v(-9.2, 6.9) * mm});
            skLineSegment(sketch, "E100.18.11", {"start": v(-9.27, 6.65) * mm, "end": v(-9.3, 6.7) * mm});
            skLineSegment(sketch, "E100.18.12", {"start": v(-9.2, 6.51) * mm, "end": v(-9.22, 6.56) * mm});
            skLineSegment(sketch, "E100.18.13", {"start": v(-9.95, 5.68) * mm, "end": v(-10, 5.68) * mm});
            skLineSegment(sketch, "E100.18.14", {"start": v(-9.32, 6.74) * mm, "end": v(-9.3, 6.77) * mm});
            skLineSegment(sketch, "E100.18.15", {"start": v(-9.11, 6.39) * mm, "end": v(-9.14, 6.43) * mm});
            skLineSegment(sketch, "E100.18.16", {"start": v(-9.27, 6.8) * mm, "end": v(-9.25, 6.83) * mm});
            skLineSegment(sketch, "E100.18.17", {"start": v(-10, 5.68) * mm, "end": v(-10.02, 5.65) * mm});
            skLineSegment(sketch, "E100.18.18", {"start": v(-9.74, 5.66) * mm, "end": v(-9.8, 5.66) * mm});
            skLineSegment(sketch, "E100.18.19", {"start": v(-9.17, 6.47) * mm, "end": v(-9.2, 6.51) * mm});
            skLineSegment(sketch, "E100.18.20", {"start": v(-9.3, 6.7) * mm, "end": v(-9.32, 6.74) * mm});
            skLineSegment(sketch, "E100.18.21", {"start": v(-9.6, 5.64) * mm, "end": v(-9.64, 5.64) * mm});
            skLineSegment(sketch, "E100.18.22", {"start": v(-9.8, 5.66) * mm, "end": v(-9.85, 5.67) * mm});
            skLineSegment(sketch, "E100.18.23", {"start": v(-9.14, 6.43) * mm, "end": v(-9.17, 6.47) * mm});
            skLineSegment(sketch, "E100.18.24", {"start": v(-9.64, 5.64) * mm, "end": v(-9.7, 5.65) * mm});
            skLineSegment(sketch, "E100.18.25", {"start": v(-9.7, 5.65) * mm, "end": v(-9.74, 5.66) * mm});
            skLineSegment(sketch, "E100.18.26", {"start": v(-9.9, 5.67) * mm, "end": v(-9.95, 5.68) * mm});
            skLineSegment(sketch, "E100.18.27", {"start": v(-9.55, 5.63) * mm, "end": v(-9.6, 5.64) * mm});
            skLineSegment(sketch, "E100.18.28", {"start": v(-8.9, 5.47) * mm, "end": v(-8.91, 5.47) * mm});
            skLineSegment(sketch, "E100.18.29", {"start": v(-9.16, 5.54) * mm, "end": v(-9.2, 5.56) * mm});
            skLineSegment(sketch, "E100.18.30", {"start": v(-9.3, 5.58) * mm, "end": v(-9.35, 5.6) * mm});
            skLineSegment(sketch, "E100.18.31", {"start": v(-8.69, 5.84) * mm, "end": v(-8.7, 5.86) * mm});
            skLineSegment(sketch, "E100.18.32", {"start": v(-9.06, 6.3) * mm, "end": v(-9.08, 6.34) * mm});
            skLineSegment(sketch, "E100.18.33", {"start": v(-8.84, 5.48) * mm, "end": v(-8.85, 5.47) * mm});
            skLineSegment(sketch, "E100.18.34", {"start": v(-8.65, 5.77) * mm, "end": v(-8.66, 5.78) * mm});
            skLineSegment(sketch, "E100.18.35", {"start": v(-8.93, 5.47) * mm, "end": v(-8.94, 5.48) * mm});
            skLineSegment(sketch, "E100.18.36", {"start": v(-9.03, 5.5) * mm, "end": v(-9.07, 5.51) * mm});
            skLineSegment(sketch, "E100.18.37", {"start": v(-9, 6.22) * mm, "end": v(-9.03, 6.26) * mm});
            skLineSegment(sketch, "E100.18.38", {"start": v(-8.82, 6) * mm, "end": v(-8.85, 6.03) * mm});
            skLineSegment(sketch, "E100.18.39", {"start": v(-8.91, 6.1) * mm, "end": v(-8.94, 6.14) * mm});
            skLineSegment(sketch, "E100.18.40", {"start": v(-8.73, 5.6) * mm, "end": v(-8.72, 5.63) * mm});
            skLineSegment(sketch, "E100.18.41", {"start": v(-8.72, 5.63) * mm, "end": v(-8.7, 5.65) * mm});
            skLineSegment(sketch, "E100.18.42", {"start": v(-9.4, 5.6) * mm, "end": v(-9.45, 5.61) * mm});
            skLineSegment(sketch, "E100.18.43", {"start": v(-9.35, 5.6) * mm, "end": v(-9.4, 5.6) * mm});
            skLineSegment(sketch, "E100.18.44", {"start": v(-9.03, 6.26) * mm, "end": v(-9.06, 6.3) * mm});
            skLineSegment(sketch, "E100.18.45", {"start": v(-8.66, 5.8) * mm, "end": v(-8.67, 5.8) * mm});
            skLineSegment(sketch, "E100.18.46", {"start": v(-8.66, 5.71) * mm, "end": v(-8.66, 5.72) * mm});
            skLineSegment(sketch, "E100.18.47", {"start": v(-8.94, 6.14) * mm, "end": v(-8.97, 6.18) * mm});
            skLineSegment(sketch, "E100.18.48", {"start": v(-9.5, 5.62) * mm, "end": v(-9.55, 5.63) * mm});
            skLineSegment(sketch, "E100.18.49", {"start": v(-8.96, 5.48) * mm, "end": v(-8.97, 5.48) * mm});
            skLineSegment(sketch, "E100.18.50", {"start": v(-8.97, 6.18) * mm, "end": v(-9, 6.22) * mm});
            skLineSegment(sketch, "E100.18.51", {"start": v(-8.78, 5.96) * mm, "end": v(-8.82, 6) * mm});
            skLineSegment(sketch, "E100.18.52", {"start": v(-8.83, 5.48) * mm, "end": v(-8.84, 5.48) * mm});
            skLineSegment(sketch, "E100.18.53", {"start": v(-9.26, 5.57) * mm, "end": v(-9.3, 5.58) * mm});
            skLineSegment(sketch, "E100.18.54", {"start": v(-8.7, 5.87) * mm, "end": v(-8.72, 5.88) * mm});
            skLineSegment(sketch, "E100.18.55", {"start": v(-8.68, 5.69) * mm, "end": v(-8.66, 5.7) * mm});
            skLineSegment(sketch, "E100.18.56", {"start": v(-8.68, 5.83) * mm, "end": v(-8.69, 5.84) * mm});
            skLineSegment(sketch, "E100.18.57", {"start": v(-8.82, 5.48) * mm, "end": v(-8.83, 5.48) * mm});
            skLineSegment(sketch, "E100.18.58", {"start": v(-8.73, 5.9) * mm, "end": v(-8.74, 5.91) * mm});
            skLineSegment(sketch, "E100.18.59", {"start": v(-8.97, 5.48) * mm, "end": v(-8.99, 5.49) * mm});
            skLineSegment(sketch, "E100.18.60", {"start": v(-8.85, 6.03) * mm, "end": v(-8.88, 6.07) * mm});
            skLineSegment(sketch, "E100.18.61", {"start": v(-9.45, 5.61) * mm, "end": v(-9.5, 5.62) * mm});
            skLineSegment(sketch, "E100.18.62", {"start": v(-9.2, 5.56) * mm, "end": v(-9.26, 5.57) * mm});
            skLineSegment(sketch, "E100.18.63", {"start": v(-9, 5.5) * mm, "end": v(-9.03, 5.5) * mm});
            skLineSegment(sketch, "E100.18.64", {"start": v(-8.81, 5.49) * mm, "end": v(-8.82, 5.48) * mm});
            skLineSegment(sketch, "E100.18.65", {"start": v(-8.69, 5.67) * mm, "end": v(-8.68, 5.69) * mm});
            skLineSegment(sketch, "E100.18.66", {"start": v(-8.72, 5.88) * mm, "end": v(-8.73, 5.9) * mm});
            skLineSegment(sketch, "E100.18.67", {"start": v(-8.88, 6.07) * mm, "end": v(-8.91, 6.1) * mm});
            skLineSegment(sketch, "E100.18.68", {"start": v(-8.67, 5.82) * mm, "end": v(-8.68, 5.83) * mm});
            skLineSegment(sketch, "E100.18.69", {"start": v(-9.12, 5.53) * mm, "end": v(-9.16, 5.54) * mm});
            skLineSegment(sketch, "E100.18.70", {"start": v(-8.65, 5.73) * mm, "end": v(-8.65, 5.74) * mm});
            skLineSegment(sketch, "E100.18.71", {"start": v(-8.7, 5.86) * mm, "end": v(-8.7, 5.87) * mm});
            skLineSegment(sketch, "E100.18.72", {"start": v(-8.65, 5.75) * mm, "end": v(-8.65, 5.76) * mm});
            skLineSegment(sketch, "E100.18.73", {"start": v(-9.07, 5.51) * mm, "end": v(-9.12, 5.53) * mm});
            skLineSegment(sketch, "E100.18.74", {"start": v(-8.8, 5.5) * mm, "end": v(-8.81, 5.49) * mm});
            skLineSegment(sketch, "E100.18.75", {"start": v(-8.8, 5.5) * mm, "end": v(-8.8, 5.5) * mm});
            skLineSegment(sketch, "E100.18.76", {"start": v(-8.75, 5.57) * mm, "end": v(-8.77, 5.55) * mm});
            skLineSegment(sketch, "E100.18.77", {"start": v(-8.67, 5.8) * mm, "end": v(-8.67, 5.82) * mm});
            skLineSegment(sketch, "E100.18.78", {"start": v(-8.91, 5.47) * mm, "end": v(-8.93, 5.47) * mm});
            skLineSegment(sketch, "E100.18.79", {"start": v(-8.75, 5.93) * mm, "end": v(-8.78, 5.96) * mm});
            skLineSegment(sketch, "E100.18.80", {"start": v(-8.65, 5.76) * mm, "end": v(-8.65, 5.77) * mm});
            skLineSegment(sketch, "E100.18.81", {"start": v(-8.8, 5.5) * mm, "end": v(-8.8, 5.5) * mm});
            skLineSegment(sketch, "E100.18.82", {"start": v(-8.74, 5.91) * mm, "end": v(-8.75, 5.93) * mm});
            skLineSegment(sketch, "E100.18.83", {"start": v(-8.74, 5.59) * mm, "end": v(-8.75, 5.57) * mm});
            skLineSegment(sketch, "E100.18.84", {"start": v(-8.94, 5.48) * mm, "end": v(-8.96, 5.48) * mm});
            skLineSegment(sketch, "E100.18.85", {"start": v(-8.66, 5.79) * mm, "end": v(-8.66, 5.8) * mm});
            skLineSegment(sketch, "E100.18.86", {"start": v(-8.73, 5.6) * mm, "end": v(-8.74, 5.59) * mm});
            skLineSegment(sketch, "E100.18.87", {"start": v(-8.99, 5.49) * mm, "end": v(-9, 5.5) * mm});
            skLineSegment(sketch, "E100.18.88", {"start": v(-8.8, 5.51) * mm, "end": v(-8.8, 5.5) * mm});
            skLineSegment(sketch, "E100.18.89", {"start": v(-8.78, 5.53) * mm, "end": v(-8.8, 5.51) * mm});
            skLineSegment(sketch, "E100.18.90", {"start": v(-8.66, 5.7) * mm, "end": v(-8.66, 5.71) * mm});
            skLineSegment(sketch, "E100.18.91", {"start": v(-8.65, 5.74) * mm, "end": v(-8.65, 5.75) * mm});
            skLineSegment(sketch, "E100.18.92", {"start": v(-8.66, 5.78) * mm, "end": v(-8.66, 5.79) * mm});
            skLineSegment(sketch, "E100.18.93", {"start": v(-8.7, 5.65) * mm, "end": v(-8.69, 5.67) * mm});
            skLineSegment(sketch, "E100.18.94", {"start": v(-8.77, 5.55) * mm, "end": v(-8.78, 5.53) * mm});
            skLineSegment(sketch, "E100.18.95", {"start": v(-8.86, 5.47) * mm, "end": v(-8.87, 5.47) * mm});
            skLineSegment(sketch, "E100.18.96", {"start": v(-8.66, 5.72) * mm, "end": v(-8.65, 5.73) * mm});
            skLineSegment(sketch, "E100.18.97", {"start": v(-8.85, 5.47) * mm, "end": v(-8.86, 5.47) * mm});
            skLineSegment(sketch, "E100.18.98", {"start": v(-8.87, 5.47) * mm, "end": v(-8.88, 5.47) * mm});
            skLineSegment(sketch, "E100.18.99", {"start": v(-8.88, 5.47) * mm, "end": v(-8.9, 5.47) * mm});
            skLineSegment(sketch, "E100.19.0", {"start": v(-10.17, 5.38) * mm, "end": v(-10.15, 5.41) * mm});
            skLineSegment(sketch, "E100.19.1", {"start": v(-10.73, 4.13) * mm, "end": v(-10.75, 4.1) * mm});
            skLineSegment(sketch, "E100.19.2", {"start": v(-10.55, 4.2) * mm, "end": v(-10.6, 4.2) * mm});
            skLineSegment(sketch, "E100.19.3", {"start": v(-10.76, 4.05) * mm, "end": v(-10.77, 4.02) * mm});
            skLineSegment(sketch, "E100.19.4", {"start": v(-9.9, 4.99) * mm, "end": v(-9.93, 5.02) * mm});
            skLineSegment(sketch, "E100.19.5", {"start": v(-10.13, 5.44) * mm, "end": v(-10.11, 5.48) * mm});
            skLineSegment(sketch, "E100.19.6", {"start": v(-10.72, 4.16) * mm, "end": v(-10.73, 4.13) * mm});
            skLineSegment(sketch, "E100.19.7", {"start": v(-10.06, 5.18) * mm, "end": v(-10.1, 5.22) * mm});
            skLineSegment(sketch, "E100.19.8", {"start": v(-10.75, 4.1) * mm, "end": v(-10.76, 4.05) * mm});
            skLineSegment(sketch, "E100.19.9", {"start": v(-10.1, 5.22) * mm, "end": v(-10.12, 5.26) * mm});
            skLineSegment(sketch, "E100.19.10", {"start": v(-10.11, 5.48) * mm, "end": v(-10.1, 5.51) * mm});
            skLineSegment(sketch, "E100.19.11", {"start": v(-10.12, 5.26) * mm, "end": v(-10.15, 5.3) * mm});
            skLineSegment(sketch, "E100.19.12", {"start": v(-10.03, 5.14) * mm, "end": v(-10.06, 5.18) * mm});
            skLineSegment(sketch, "E100.19.13", {"start": v(-10.65, 4.2) * mm, "end": v(-10.7, 4.2) * mm});
            skLineSegment(sketch, "E100.19.14", {"start": v(-10.18, 5.34) * mm, "end": v(-10.17, 5.38) * mm});
            skLineSegment(sketch, "E100.19.15", {"start": v(-9.93, 5.02) * mm, "end": v(-9.96, 5.06) * mm});
            skLineSegment(sketch, "E100.19.16", {"start": v(-10.15, 5.41) * mm, "end": v(-10.13, 5.44) * mm});
            skLineSegment(sketch, "E100.19.17", {"start": v(-10.7, 4.2) * mm, "end": v(-10.72, 4.16) * mm});
            skLineSegment(sketch, "E100.19.18", {"start": v(-10.45, 4.21) * mm, "end": v(-10.5, 4.21) * mm});
            skLineSegment(sketch, "E100.19.19", {"start": v(-10, 5.1) * mm, "end": v(-10.03, 5.14) * mm});
            skLineSegment(sketch, "E100.19.20", {"start": v(-10.15, 5.3) * mm, "end": v(-10.18, 5.34) * mm});
            skLineSegment(sketch, "E100.19.21", {"start": v(-10.3, 4.21) * mm, "end": v(-10.35, 4.21) * mm});
            skLineSegment(sketch, "E100.19.22", {"start": v(-10.5, 4.21) * mm, "end": v(-10.55, 4.2) * mm});
            skLineSegment(sketch, "E100.19.23", {"start": v(-9.96, 5.06) * mm, "end": v(-10, 5.1) * mm});
            skLineSegment(sketch, "E100.19.24", {"start": v(-10.35, 4.21) * mm, "end": v(-10.4, 4.21) * mm});
            skLineSegment(sketch, "E100.19.25", {"start": v(-10.4, 4.21) * mm, "end": v(-10.45, 4.21) * mm});
            skLineSegment(sketch, "E100.19.26", {"start": v(-10.6, 4.2) * mm, "end": v(-10.65, 4.2) * mm});
            skLineSegment(sketch, "E100.19.27", {"start": v(-10.25, 4.21) * mm, "end": v(-10.3, 4.21) * mm});
            skLineSegment(sketch, "E100.19.28", {"start": v(-9.59, 4.15) * mm, "end": v(-9.6, 4.15) * mm});
            skLineSegment(sketch, "E100.19.29", {"start": v(-9.86, 4.18) * mm, "end": v(-9.9, 4.19) * mm});
            skLineSegment(sketch, "E100.19.30", {"start": v(-10, 4.2) * mm, "end": v(-10.05, 4.2) * mm});
            skLineSegment(sketch, "E100.19.31", {"start": v(-9.43, 4.55) * mm, "end": v(-9.44, 4.56) * mm});
            skLineSegment(sketch, "E100.19.32", {"start": v(-9.86, 4.95) * mm, "end": v(-9.9, 4.99) * mm});
            skLineSegment(sketch, "E100.19.33", {"start": v(-9.53, 4.16) * mm, "end": v(-9.54, 4.16) * mm});
            skLineSegment(sketch, "E100.19.34", {"start": v(-9.39, 4.48) * mm, "end": v(-9.4, 4.48) * mm});
            skLineSegment(sketch, "E100.19.35", {"start": v(-9.61, 4.15) * mm, "end": v(-9.63, 4.15) * mm});
            skLineSegment(sketch, "E100.19.36", {"start": v(-9.72, 4.16) * mm, "end": v(-9.76, 4.17) * mm});
            skLineSegment(sketch, "E100.19.37", {"start": v(-9.8, 4.88) * mm, "end": v(-9.83, 4.91) * mm});
            skLineSegment(sketch, "E100.19.38", {"start": v(-9.58, 4.68) * mm, "end": v(-9.62, 4.71) * mm});
            skLineSegment(sketch, "E100.19.39", {"start": v(-9.69, 4.78) * mm, "end": v(-9.72, 4.8) * mm});
            skLineSegment(sketch, "E100.19.40", {"start": v(-9.44, 4.3) * mm, "end": v(-9.43, 4.33) * mm});
            skLineSegment(sketch, "E100.19.41", {"start": v(-9.43, 4.33) * mm, "end": v(-9.42, 4.35) * mm});
            skLineSegment(sketch, "E100.19.42", {"start": v(-10.1, 4.2) * mm, "end": v(-10.15, 4.2) * mm});
            skLineSegment(sketch, "E100.19.43", {"start": v(-10.05, 4.2) * mm, "end": v(-10.1, 4.2) * mm});
            skLineSegment(sketch, "E100.19.44", {"start": v(-9.83, 4.91) * mm, "end": v(-9.86, 4.95) * mm});
            skLineSegment(sketch, "E100.19.45", {"start": v(-9.4, 4.5) * mm, "end": v(-9.4, 4.52) * mm});
            skLineSegment(sketch, "E100.19.46", {"start": v(-9.39, 4.42) * mm, "end": v(-9.38, 4.43) * mm});
            skLineSegment(sketch, "E100.19.47", {"start": v(-9.72, 4.8) * mm, "end": v(-9.76, 4.84) * mm});
            skLineSegment(sketch, "E100.19.48", {"start": v(-10.2, 4.21) * mm, "end": v(-10.25, 4.21) * mm});
            skLineSegment(sketch, "E100.19.49", {"start": v(-9.65, 4.15) * mm, "end": v(-9.66, 4.15) * mm});
            skLineSegment(sketch, "E100.19.50", {"start": v(-9.76, 4.84) * mm, "end": v(-9.8, 4.88) * mm});
            skLineSegment(sketch, "E100.19.51", {"start": v(-9.54, 4.65) * mm, "end": v(-9.58, 4.68) * mm});
            skLineSegment(sketch, "E100.19.52", {"start": v(-9.52, 4.17) * mm, "end": v(-9.53, 4.16) * mm});
            skLineSegment(sketch, "E100.19.53", {"start": v(-9.95, 4.2) * mm, "end": v(-10, 4.2) * mm});
            skLineSegment(sketch, "E100.19.54", {"start": v(-9.45, 4.57) * mm, "end": v(-9.46, 4.58) * mm});
            skLineSegment(sketch, "E100.19.55", {"start": v(-9.4, 4.4) * mm, "end": v(-9.39, 4.42) * mm});
            skLineSegment(sketch, "E100.19.56", {"start": v(-9.42, 4.54) * mm, "end": v(-9.43, 4.55) * mm});
            skLineSegment(sketch, "E100.19.57", {"start": v(-9.51, 4.17) * mm, "end": v(-9.52, 4.17) * mm});
            skLineSegment(sketch, "E100.19.58", {"start": v(-9.48, 4.6) * mm, "end": v(-9.5, 4.6) * mm});
            skLineSegment(sketch, "E100.19.59", {"start": v(-9.66, 4.15) * mm, "end": v(-9.68, 4.15) * mm});
            skLineSegment(sketch, "E100.19.60", {"start": v(-9.62, 4.71) * mm, "end": v(-9.65, 4.74) * mm});
            skLineSegment(sketch, "E100.19.61", {"start": v(-10.15, 4.2) * mm, "end": v(-10.2, 4.21) * mm});
            skLineSegment(sketch, "E100.19.62", {"start": v(-9.9, 4.19) * mm, "end": v(-9.95, 4.2) * mm});
            skLineSegment(sketch, "E100.19.63", {"start": v(-9.7, 4.16) * mm, "end": v(-9.72, 4.16) * mm});
            skLineSegment(sketch, "E100.19.64", {"start": v(-9.5, 4.18) * mm, "end": v(-9.51, 4.17) * mm});
            skLineSegment(sketch, "E100.19.65", {"start": v(-9.4, 4.37) * mm, "end": v(-9.4, 4.4) * mm});
            skLineSegment(sketch, "E100.19.66", {"start": v(-9.46, 4.58) * mm, "end": v(-9.48, 4.6) * mm});
            skLineSegment(sketch, "E100.19.67", {"start": v(-9.65, 4.74) * mm, "end": v(-9.69, 4.78) * mm});
            skLineSegment(sketch, "E100.19.68", {"start": v(-9.41, 4.53) * mm, "end": v(-9.42, 4.54) * mm});
            skLineSegment(sketch, "E100.19.69", {"start": v(-9.81, 4.18) * mm, "end": v(-9.86, 4.18) * mm});
            skLineSegment(sketch, "E100.19.70", {"start": v(-9.38, 4.44) * mm, "end": v(-9.38, 4.45) * mm});
            skLineSegment(sketch, "E100.19.71", {"start": v(-9.44, 4.56) * mm, "end": v(-9.45, 4.57) * mm});
            skLineSegment(sketch, "E100.19.72", {"start": v(-9.38, 4.46) * mm, "end": v(-9.38, 4.47) * mm});
            skLineSegment(sketch, "E100.19.73", {"start": v(-9.76, 4.17) * mm, "end": v(-9.81, 4.18) * mm});
            skLineSegment(sketch, "E100.19.74", {"start": v(-9.5, 4.18) * mm, "end": v(-9.5, 4.18) * mm});
            skLineSegment(sketch, "E100.19.75", {"start": v(-9.5, 4.19) * mm, "end": v(-9.5, 4.18) * mm});
            skLineSegment(sketch, "E100.19.76", {"start": v(-9.46, 4.27) * mm, "end": v(-9.47, 4.25) * mm});
            skLineSegment(sketch, "E100.19.77", {"start": v(-9.4, 4.52) * mm, "end": v(-9.41, 4.53) * mm});
            skLineSegment(sketch, "E100.19.78", {"start": v(-9.6, 4.15) * mm, "end": v(-9.61, 4.15) * mm});
            skLineSegment(sketch, "E100.19.79", {"start": v(-9.5, 4.62) * mm, "end": v(-9.54, 4.65) * mm});
            skLineSegment(sketch, "E100.19.80", {"start": v(-9.38, 4.47) * mm, "end": v(-9.39, 4.48) * mm});
            skLineSegment(sketch, "E100.19.81", {"start": v(-9.49, 4.2) * mm, "end": v(-9.5, 4.19) * mm});
            skLineSegment(sketch, "E100.19.82", {"start": v(-9.5, 4.6) * mm, "end": v(-9.5, 4.62) * mm});
            skLineSegment(sketch, "E100.19.83", {"start": v(-9.45, 4.29) * mm, "end": v(-9.46, 4.27) * mm});
            skLineSegment(sketch, "E100.19.84", {"start": v(-9.63, 4.15) * mm, "end": v(-9.65, 4.15) * mm});
            skLineSegment(sketch, "E100.19.85", {"start": v(-9.4, 4.5) * mm, "end": v(-9.4, 4.5) * mm});
            skLineSegment(sketch, "E100.19.86", {"start": v(-9.44, 4.3) * mm, "end": v(-9.45, 4.29) * mm});
            skLineSegment(sketch, "E100.19.87", {"start": v(-9.68, 4.15) * mm, "end": v(-9.7, 4.16) * mm});
            skLineSegment(sketch, "E100.19.88", {"start": v(-9.49, 4.2) * mm, "end": v(-9.49, 4.2) * mm});
            skLineSegment(sketch, "E100.19.89", {"start": v(-9.48, 4.22) * mm, "end": v(-9.49, 4.2) * mm});
            skLineSegment(sketch, "E100.19.90", {"start": v(-9.39, 4.42) * mm, "end": v(-9.39, 4.42) * mm});
            skLineSegment(sketch, "E100.19.91", {"start": v(-9.38, 4.45) * mm, "end": v(-9.38, 4.46) * mm});
            skLineSegment(sketch, "E100.19.92", {"start": v(-9.4, 4.48) * mm, "end": v(-9.4, 4.5) * mm});
            skLineSegment(sketch, "E100.19.93", {"start": v(-9.42, 4.35) * mm, "end": v(-9.4, 4.37) * mm});
            skLineSegment(sketch, "E100.19.94", {"start": v(-9.47, 4.25) * mm, "end": v(-9.48, 4.22) * mm});
            skLineSegment(sketch, "E100.19.95", {"start": v(-9.55, 4.16) * mm, "end": v(-9.56, 4.15) * mm});
            skLineSegment(sketch, "E100.19.96", {"start": v(-9.38, 4.43) * mm, "end": v(-9.38, 4.44) * mm});
            skLineSegment(sketch, "E100.19.97", {"start": v(-9.54, 4.16) * mm, "end": v(-9.55, 4.16) * mm});
            skLineSegment(sketch, "E100.19.98", {"start": v(-9.56, 4.15) * mm, "end": v(-9.57, 4.15) * mm});
            skLineSegment(sketch, "E100.19.99", {"start": v(-9.57, 4.15) * mm, "end": v(-9.59, 4.15) * mm});
            skLineSegment(sketch, "E100.20.0", {"start": v(-10.83, 3.87) * mm, "end": v(-10.81, 3.91) * mm});
            skLineSegment(sketch, "E100.20.1", {"start": v(-11.21, 2.56) * mm, "end": v(-11.22, 2.52) * mm});
            skLineSegment(sketch, "E100.20.2", {"start": v(-11.04, 2.66) * mm, "end": v(-11.1, 2.65) * mm});
            skLineSegment(sketch, "E100.20.3", {"start": v(-11.23, 2.48) * mm, "end": v(-11.24, 2.44) * mm});
            skLineSegment(sketch, "E100.20.4", {"start": v(-10.5, 3.53) * mm, "end": v(-10.54, 3.56) * mm});
            skLineSegment(sketch, "E100.20.5", {"start": v(-10.8, 3.95) * mm, "end": v(-10.79, 3.98) * mm});
            skLineSegment(sketch, "E100.20.6", {"start": v(-11.2, 2.6) * mm, "end": v(-11.21, 2.56) * mm});
            skLineSegment(sketch, "E100.20.7", {"start": v(-10.7, 3.7) * mm, "end": v(-10.73, 3.73) * mm});
            skLineSegment(sketch, "E100.20.8", {"start": v(-11.22, 2.52) * mm, "end": v(-11.23, 2.48) * mm});
            skLineSegment(sketch, "E100.20.9", {"start": v(-10.73, 3.73) * mm, "end": v(-10.77, 3.77) * mm});
            skLineSegment(sketch, "E100.20.10", {"start": v(-10.79, 3.98) * mm, "end": v(-10.77, 4.02) * mm});
            skLineSegment(sketch, "E100.20.11", {"start": v(-10.77, 3.77) * mm, "end": v(-10.8, 3.8) * mm});
            skLineSegment(sketch, "E100.20.12", {"start": v(-10.66, 3.66) * mm, "end": v(-10.7, 3.7) * mm});
            skLineSegment(sketch, "E100.20.13", {"start": v(-11.14, 2.64) * mm, "end": v(-11.2, 2.63) * mm});
            skLineSegment(sketch, "E100.20.14", {"start": v(-10.84, 3.84) * mm, "end": v(-10.83, 3.87) * mm});
            skLineSegment(sketch, "E100.20.15", {"start": v(-10.54, 3.56) * mm, "end": v(-10.58, 3.6) * mm});
            skLineSegment(sketch, "E100.20.16", {"start": v(-10.81, 3.91) * mm, "end": v(-10.8, 3.95) * mm});
            skLineSegment(sketch, "E100.20.17", {"start": v(-11.2, 2.63) * mm, "end": v(-11.2, 2.6) * mm});
            skLineSegment(sketch, "E100.20.18", {"start": v(-10.94, 2.68) * mm, "end": v(-11, 2.67) * mm});
            skLineSegment(sketch, "E100.20.19", {"start": v(-10.62, 3.63) * mm, "end": v(-10.66, 3.66) * mm});
            skLineSegment(sketch, "E100.20.20", {"start": v(-10.8, 3.8) * mm, "end": v(-10.84, 3.84) * mm});
            skLineSegment(sketch, "E100.20.21", {"start": v(-10.8, 2.7) * mm, "end": v(-10.84, 2.7) * mm});
            skLineSegment(sketch, "E100.20.22", {"start": v(-11, 2.67) * mm, "end": v(-11.04, 2.66) * mm});
            skLineSegment(sketch, "E100.20.23", {"start": v(-10.58, 3.6) * mm, "end": v(-10.62, 3.63) * mm});
            skLineSegment(sketch, "E100.20.24", {"start": v(-10.84, 2.7) * mm, "end": v(-10.9, 2.69) * mm});
            skLineSegment(sketch, "E100.20.25", {"start": v(-10.9, 2.69) * mm, "end": v(-10.94, 2.68) * mm});
            skLineSegment(sketch, "E100.20.26", {"start": v(-11.1, 2.65) * mm, "end": v(-11.14, 2.64) * mm});
            skLineSegment(sketch, "E100.20.27", {"start": v(-10.74, 2.71) * mm, "end": v(-10.8, 2.7) * mm});
            skLineSegment(sketch, "E100.20.28", {"start": v(-10.08, 2.74) * mm, "end": v(-10.1, 2.74) * mm});
            skLineSegment(sketch, "E100.20.29", {"start": v(-10.35, 2.74) * mm, "end": v(-10.4, 2.74) * mm});
            skLineSegment(sketch, "E100.20.30", {"start": v(-10.5, 2.73) * mm, "end": v(-10.55, 2.73) * mm});
            skLineSegment(sketch, "E100.20.31", {"start": v(-9.98, 3.16) * mm, "end": v(-10, 3.17) * mm});
            skLineSegment(sketch, "E100.20.32", {"start": v(-10.47, 3.5) * mm, "end": v(-10.5, 3.53) * mm});
            skLineSegment(sketch, "E100.20.33", {"start": v(-10.02, 2.76) * mm, "end": v(-10.03, 2.76) * mm});
            skLineSegment(sketch, "E100.20.34", {"start": v(-9.93, 3.1) * mm, "end": v(-9.93, 3.1) * mm});
            skLineSegment(sketch, "E100.20.35", {"start": v(-10.1, 2.74) * mm, "end": v(-10.12, 2.74) * mm});
            skLineSegment(sketch, "E100.20.36", {"start": v(-10.2, 2.73) * mm, "end": v(-10.26, 2.74) * mm});
            skLineSegment(sketch, "E100.20.37", {"start": v(-10.39, 3.44) * mm, "end": v(-10.43, 3.47) * mm});
            skLineSegment(sketch, "E100.20.38", {"start": v(-10.15, 3.27) * mm, "end": v(-10.19, 3.3) * mm});
            skLineSegment(sketch, "E100.20.39", {"start": v(-10.27, 3.35) * mm, "end": v(-10.3, 3.38) * mm});
            skLineSegment(sketch, "E100.20.40", {"start": v(-9.95, 2.92) * mm, "end": v(-9.95, 2.95) * mm});
            skLineSegment(sketch, "E100.20.41", {"start": v(-9.95, 2.95) * mm, "end": v(-9.94, 2.97) * mm});
            skLineSegment(sketch, "E100.20.42", {"start": v(-10.6, 2.73) * mm, "end": v(-10.65, 2.72) * mm});
            skLineSegment(sketch, "E100.20.43", {"start": v(-10.55, 2.73) * mm, "end": v(-10.6, 2.73) * mm});
            skLineSegment(sketch, "E100.20.44", {"start": v(-10.43, 3.47) * mm, "end": v(-10.47, 3.5) * mm});
            skLineSegment(sketch, "E100.20.45", {"start": v(-9.95, 3.12) * mm, "end": v(-9.95, 3.13) * mm});
            skLineSegment(sketch, "E100.20.46", {"start": v(-9.92, 3.04) * mm, "end": v(-9.92, 3.05) * mm});
            skLineSegment(sketch, "E100.20.47", {"start": v(-10.3, 3.38) * mm, "end": v(-10.35, 3.4) * mm});
            skLineSegment(sketch, "E100.20.48", {"start": v(-10.7, 2.72) * mm, "end": v(-10.74, 2.71) * mm});
            skLineSegment(sketch, "E100.20.49", {"start": v(-10.14, 2.73) * mm, "end": v(-10.15, 2.73) * mm});
            skLineSegment(sketch, "E100.20.50", {"start": v(-10.35, 3.4) * mm, "end": v(-10.39, 3.44) * mm});
            skLineSegment(sketch, "E100.20.51", {"start": v(-10.1, 3.24) * mm, "end": v(-10.15, 3.27) * mm});
            skLineSegment(sketch, "E100.20.52", {"start": v(-10.02, 2.77) * mm, "end": v(-10.02, 2.76) * mm});
            skLineSegment(sketch, "E100.20.53", {"start": v(-10.45, 2.73) * mm, "end": v(-10.5, 2.73) * mm});
            skLineSegment(sketch, "E100.20.54", {"start": v(-10, 3.18) * mm, "end": v(-10.02, 3.2) * mm});
            skLineSegment(sketch, "E100.20.55", {"start": v(-9.93, 3.01) * mm, "end": v(-9.92, 3.03) * mm});
            skLineSegment(sketch, "E100.20.56", {"start": v(-9.97, 3.15) * mm, "end": v(-9.98, 3.16) * mm});
            skLineSegment(sketch, "E100.20.57", {"start": v(-10, 2.78) * mm, "end": v(-10.02, 2.77) * mm});
            skLineSegment(sketch, "E100.20.58", {"start": v(-10.03, 3.2) * mm, "end": v(-10.05, 3.2) * mm});
            skLineSegment(sketch, "E100.20.59", {"start": v(-10.15, 2.73) * mm, "end": v(-10.17, 2.73) * mm});
            skLineSegment(sketch, "E100.20.60", {"start": v(-10.19, 3.3) * mm, "end": v(-10.23, 3.32) * mm});
            skLineSegment(sketch, "E100.20.61", {"start": v(-10.65, 2.72) * mm, "end": v(-10.7, 2.72) * mm});
            skLineSegment(sketch, "E100.20.62", {"start": v(-10.4, 2.74) * mm, "end": v(-10.45, 2.73) * mm});
            skLineSegment(sketch, "E100.20.63", {"start": v(-10.2, 2.73) * mm, "end": v(-10.2, 2.73) * mm});
            skLineSegment(sketch, "E100.20.64", {"start": v(-10, 2.78) * mm, "end": v(-10, 2.78) * mm});
            skLineSegment(sketch, "E100.20.65", {"start": v(-9.93, 3) * mm, "end": v(-9.93, 3.01) * mm});
            skLineSegment(sketch, "E100.20.66", {"start": v(-10.02, 3.2) * mm, "end": v(-10.03, 3.2) * mm});
            skLineSegment(sketch, "E100.20.67", {"start": v(-10.23, 3.32) * mm, "end": v(-10.27, 3.35) * mm});
            skLineSegment(sketch, "E100.20.68", {"start": v(-9.96, 3.14) * mm, "end": v(-9.97, 3.15) * mm});
            skLineSegment(sketch, "E100.20.69", {"start": v(-10.3, 2.74) * mm, "end": v(-10.35, 2.74) * mm});
            skLineSegment(sketch, "E100.20.70", {"start": v(-9.92, 3.06) * mm, "end": v(-9.92, 3.07) * mm});
            skLineSegment(sketch, "E100.20.71", {"start": v(-10, 3.17) * mm, "end": v(-10, 3.18) * mm});
            skLineSegment(sketch, "E100.20.72", {"start": v(-9.92, 3.08) * mm, "end": v(-9.92, 3.08) * mm});
            skLineSegment(sketch, "E100.20.73", {"start": v(-10.26, 2.74) * mm, "end": v(-10.3, 2.74) * mm});
            skLineSegment(sketch, "E100.20.74", {"start": v(-10, 2.79) * mm, "end": v(-10, 2.78) * mm});
            skLineSegment(sketch, "E100.20.75", {"start": v(-10, 2.8) * mm, "end": v(-10, 2.79) * mm});
            skLineSegment(sketch, "E100.20.76", {"start": v(-9.97, 2.88) * mm, "end": v(-9.97, 2.86) * mm});
            skLineSegment(sketch, "E100.20.77", {"start": v(-9.95, 3.13) * mm, "end": v(-9.96, 3.14) * mm});
            skLineSegment(sketch, "E100.20.78", {"start": v(-10.1, 2.74) * mm, "end": v(-10.1, 2.74) * mm});
            skLineSegment(sketch, "E100.20.79", {"start": v(-10.07, 3.22) * mm, "end": v(-10.1, 3.24) * mm});
            skLineSegment(sketch, "E100.20.80", {"start": v(-9.92, 3.08) * mm, "end": v(-9.93, 3.1) * mm});
            skLineSegment(sketch, "E100.20.81", {"start": v(-9.99, 2.8) * mm, "end": v(-10, 2.8) * mm});
            skLineSegment(sketch, "E100.20.82", {"start": v(-10.05, 3.2) * mm, "end": v(-10.07, 3.22) * mm});
            skLineSegment(sketch, "E100.20.83", {"start": v(-9.96, 2.9) * mm, "end": v(-9.97, 2.88) * mm});
            skLineSegment(sketch, "E100.20.84", {"start": v(-10.12, 2.74) * mm, "end": v(-10.14, 2.73) * mm});
            skLineSegment(sketch, "E100.20.85", {"start": v(-9.94, 3.11) * mm, "end": v(-9.95, 3.12) * mm});
            skLineSegment(sketch, "E100.20.86", {"start": v(-9.95, 2.92) * mm, "end": v(-9.96, 2.9) * mm});
            skLineSegment(sketch, "E100.20.87", {"start": v(-10.17, 2.73) * mm, "end": v(-10.2, 2.73) * mm});
            skLineSegment(sketch, "E100.20.88", {"start": v(-9.99, 2.81) * mm, "end": v(-9.99, 2.8) * mm});
            skLineSegment(sketch, "E100.20.89", {"start": v(-9.98, 2.83) * mm, "end": v(-9.99, 2.81) * mm});
            skLineSegment(sketch, "E100.20.90", {"start": v(-9.92, 3.03) * mm, "end": v(-9.92, 3.04) * mm});
            skLineSegment(sketch, "E100.20.91", {"start": v(-9.92, 3.07) * mm, "end": v(-9.92, 3.08) * mm});
            skLineSegment(sketch, "E100.20.92", {"start": v(-9.93, 3.1) * mm, "end": v(-9.94, 3.11) * mm});
            skLineSegment(sketch, "E100.20.93", {"start": v(-9.94, 2.97) * mm, "end": v(-9.93, 3) * mm});
            skLineSegment(sketch, "E100.20.94", {"start": v(-9.97, 2.86) * mm, "end": v(-9.98, 2.83) * mm});
            skLineSegment(sketch, "E100.20.95", {"start": v(-10.04, 2.76) * mm, "end": v(-10.05, 2.75) * mm});
            skLineSegment(sketch, "E100.20.96", {"start": v(-9.92, 3.05) * mm, "end": v(-9.92, 3.06) * mm});
            skLineSegment(sketch, "E100.20.97", {"start": v(-10.03, 2.76) * mm, "end": v(-10.04, 2.76) * mm});
            skLineSegment(sketch, "E100.20.98", {"start": v(-10.05, 2.75) * mm, "end": v(-10.07, 2.75) * mm});
            skLineSegment(sketch, "E100.20.99", {"start": v(-10.07, 2.75) * mm, "end": v(-10.08, 2.74) * mm});
            skLineSegment(sketch, "E100.21.0", {"start": v(-11.27, 2.3) * mm, "end": v(-11.26, 2.33) * mm});
            skLineSegment(sketch, "E100.21.1", {"start": v(-11.46, 0.94) * mm, "end": v(-11.46, 0.9) * mm});
            skLineSegment(sketch, "E100.21.2", {"start": v(-11.31, 1.06) * mm, "end": v(-11.36, 1.05) * mm});
            skLineSegment(sketch, "E100.21.3", {"start": v(-11.47, 0.86) * mm, "end": v(-11.47, 0.82) * mm});
            skLineSegment(sketch, "E100.21.4", {"start": v(-10.9, 2) * mm, "end": v(-10.94, 2.02) * mm});
            skLineSegment(sketch, "E100.21.5", {"start": v(-11.25, 2.37) * mm, "end": v(-11.25, 2.4) * mm});
            skLineSegment(sketch, "E100.21.6", {"start": v(-11.46, 0.97) * mm, "end": v(-11.46, 0.94) * mm});
            skLineSegment(sketch, "E100.21.7", {"start": v(-11.11, 2.14) * mm, "end": v(-11.15, 2.17) * mm});
            skLineSegment(sketch, "E100.21.8", {"start": v(-11.46, 0.9) * mm, "end": v(-11.47, 0.86) * mm});
            skLineSegment(sketch, "E100.21.9", {"start": v(-11.15, 2.17) * mm, "end": v(-11.2, 2.2) * mm});
            skLineSegment(sketch, "E100.21.10", {"start": v(-11.25, 2.4) * mm, "end": v(-11.24, 2.44) * mm});
            skLineSegment(sketch, "E100.21.11", {"start": v(-11.2, 2.2) * mm, "end": v(-11.24, 2.23) * mm});
            skLineSegment(sketch, "E100.21.12", {"start": v(-11.07, 2.1) * mm, "end": v(-11.11, 2.14) * mm});
            skLineSegment(sketch, "E100.21.13", {"start": v(-11.4, 1.03) * mm, "end": v(-11.46, 1.01) * mm});
            skLineSegment(sketch, "E100.21.14", {"start": v(-11.28, 2.26) * mm, "end": v(-11.27, 2.3) * mm});
            skLineSegment(sketch, "E100.21.15", {"start": v(-10.94, 2.02) * mm, "end": v(-10.98, 2.05) * mm});
            skLineSegment(sketch, "E100.21.16", {"start": v(-11.26, 2.33) * mm, "end": v(-11.25, 2.37) * mm});
            skLineSegment(sketch, "E100.21.17", {"start": v(-11.46, 1.01) * mm, "end": v(-11.46, 0.97) * mm});
            skLineSegment(sketch, "E100.21.18", {"start": v(-11.21, 1.1) * mm, "end": v(-11.26, 1.08) * mm});
            skLineSegment(sketch, "E100.21.19", {"start": v(-11.03, 2.08) * mm, "end": v(-11.07, 2.1) * mm});
            skLineSegment(sketch, "E100.21.20", {"start": v(-11.24, 2.23) * mm, "end": v(-11.28, 2.26) * mm});
            skLineSegment(sketch, "E100.21.21", {"start": v(-11.07, 1.14) * mm, "end": v(-11.12, 1.13) * mm});
            skLineSegment(sketch, "E100.21.22", {"start": v(-11.26, 1.08) * mm, "end": v(-11.31, 1.06) * mm});
            skLineSegment(sketch, "E100.21.23", {"start": v(-10.98, 2.05) * mm, "end": v(-11.03, 2.08) * mm});
            skLineSegment(sketch, "E100.21.24", {"start": v(-11.12, 1.13) * mm, "end": v(-11.17, 1.11) * mm});
            skLineSegment(sketch, "E100.21.25", {"start": v(-11.17, 1.11) * mm, "end": v(-11.21, 1.1) * mm});
            skLineSegment(sketch, "E100.21.26", {"start": v(-11.36, 1.05) * mm, "end": v(-11.4, 1.03) * mm});
            skLineSegment(sketch, "E100.21.27", {"start": v(-11.02, 1.15) * mm, "end": v(-11.07, 1.14) * mm});
            skLineSegment(sketch, "E100.21.28", {"start": v(-10.37, 1.28) * mm, "end": v(-10.38, 1.28) * mm});
            skLineSegment(sketch, "E100.21.29", {"start": v(-10.64, 1.24) * mm, "end": v(-10.69, 1.23) * mm});
            skLineSegment(sketch, "E100.21.30", {"start": v(-10.78, 1.21) * mm, "end": v(-10.83, 1.2) * mm});
            skLineSegment(sketch, "E100.21.31", {"start": v(-10.33, 1.7) * mm, "end": v(-10.34, 1.72) * mm});
            skLineSegment(sketch, "E100.21.32", {"start": v(-10.86, 1.97) * mm, "end": v(-10.9, 2) * mm});
            skLineSegment(sketch, "E100.21.33", {"start": v(-10.32, 1.31) * mm, "end": v(-10.32, 1.3) * mm});
            skLineSegment(sketch, "E100.21.34", {"start": v(-10.27, 1.65) * mm, "end": v(-10.27, 1.66) * mm});
            skLineSegment(sketch, "E100.21.35", {"start": v(-10.4, 1.27) * mm, "end": v(-10.4, 1.27) * mm});
            skLineSegment(sketch, "E100.21.36", {"start": v(-10.5, 1.25) * mm, "end": v(-10.54, 1.25) * mm});
            skLineSegment(sketch, "E100.21.37", {"start": v(-10.77, 1.92) * mm, "end": v(-10.81, 1.95) * mm});
            skLineSegment(sketch, "E100.21.38", {"start": v(-10.51, 1.8) * mm, "end": v(-10.55, 1.81) * mm});
            skLineSegment(sketch, "E100.21.39", {"start": v(-10.64, 1.85) * mm, "end": v(-10.69, 1.88) * mm});
            skLineSegment(sketch, "E100.21.40", {"start": v(-10.27, 1.48) * mm, "end": v(-10.27, 1.5) * mm});
            skLineSegment(sketch, "E100.21.41", {"start": v(-10.27, 1.5) * mm, "end": v(-10.26, 1.52) * mm});
            skLineSegment(sketch, "E100.21.42", {"start": v(-10.88, 1.2) * mm, "end": v(-10.92, 1.18) * mm});
            skLineSegment(sketch, "E100.21.43", {"start": v(-10.83, 1.2) * mm, "end": v(-10.88, 1.2) * mm});
            skLineSegment(sketch, "E100.21.44", {"start": v(-10.81, 1.95) * mm, "end": v(-10.86, 1.97) * mm});
            skLineSegment(sketch, "E100.21.45", {"start": v(-10.29, 1.67) * mm, "end": v(-10.3, 1.68) * mm});
            skLineSegment(sketch, "E100.21.46", {"start": v(-10.25, 1.6) * mm, "end": v(-10.25, 1.6) * mm});
            skLineSegment(sketch, "E100.21.47", {"start": v(-10.69, 1.88) * mm, "end": v(-10.73, 1.9) * mm});
            skLineSegment(sketch, "E100.21.48", {"start": v(-10.97, 1.17) * mm, "end": v(-11.02, 1.15) * mm});
            skLineSegment(sketch, "E100.21.49", {"start": v(-10.42, 1.26) * mm, "end": v(-10.44, 1.26) * mm});
            skLineSegment(sketch, "E100.21.50", {"start": v(-10.73, 1.9) * mm, "end": v(-10.77, 1.92) * mm});
            skLineSegment(sketch, "E100.21.51", {"start": v(-10.47, 1.77) * mm, "end": v(-10.51, 1.8) * mm});
            skLineSegment(sketch, "E100.21.52", {"start": v(-10.3, 1.32) * mm, "end": v(-10.32, 1.31) * mm});
            skLineSegment(sketch, "E100.21.53", {"start": v(-10.73, 1.22) * mm, "end": v(-10.78, 1.21) * mm});
            skLineSegment(sketch, "E100.21.54", {"start": v(-10.36, 1.72) * mm, "end": v(-10.37, 1.73) * mm});
            skLineSegment(sketch, "E100.21.55", {"start": v(-10.26, 1.57) * mm, "end": v(-10.25, 1.6) * mm});
            skLineSegment(sketch, "E100.21.56", {"start": v(-10.32, 1.7) * mm, "end": v(-10.33, 1.7) * mm});
            skLineSegment(sketch, "E100.21.57", {"start": v(-10.3, 1.32) * mm, "end": v(-10.3, 1.32) * mm});
            skLineSegment(sketch, "E100.21.58", {"start": v(-10.39, 1.74) * mm, "end": v(-10.4, 1.75) * mm});
            skLineSegment(sketch, "E100.21.59", {"start": v(-10.44, 1.26) * mm, "end": v(-10.46, 1.26) * mm});
            skLineSegment(sketch, "E100.21.60", {"start": v(-10.55, 1.81) * mm, "end": v(-10.6, 1.83) * mm});
            skLineSegment(sketch, "E100.21.61", {"start": v(-10.92, 1.18) * mm, "end": v(-10.97, 1.17) * mm});
            skLineSegment(sketch, "E100.21.62", {"start": v(-10.69, 1.23) * mm, "end": v(-10.73, 1.22) * mm});
            skLineSegment(sketch, "E100.21.63", {"start": v(-10.48, 1.26) * mm, "end": v(-10.5, 1.25) * mm});
            skLineSegment(sketch, "E100.21.64", {"start": v(-10.3, 1.33) * mm, "end": v(-10.3, 1.32) * mm});
            skLineSegment(sketch, "E100.21.65", {"start": v(-10.26, 1.55) * mm, "end": v(-10.26, 1.57) * mm});
            skLineSegment(sketch, "E100.21.66", {"start": v(-10.37, 1.73) * mm, "end": v(-10.39, 1.74) * mm});
            skLineSegment(sketch, "E100.21.67", {"start": v(-10.6, 1.83) * mm, "end": v(-10.64, 1.85) * mm});
            skLineSegment(sketch, "E100.21.68", {"start": v(-10.3, 1.7) * mm, "end": v(-10.32, 1.7) * mm});
            skLineSegment(sketch, "E100.21.69", {"start": v(-10.59, 1.24) * mm, "end": v(-10.64, 1.24) * mm});
            skLineSegment(sketch, "E100.21.70", {"start": v(-10.25, 1.62) * mm, "end": v(-10.26, 1.62) * mm});
            skLineSegment(sketch, "E100.21.71", {"start": v(-10.34, 1.72) * mm, "end": v(-10.36, 1.72) * mm});
            skLineSegment(sketch, "E100.21.72", {"start": v(-10.26, 1.63) * mm, "end": v(-10.26, 1.64) * mm});
            skLineSegment(sketch, "E100.21.73", {"start": v(-10.54, 1.25) * mm, "end": v(-10.59, 1.24) * mm});
            skLineSegment(sketch, "E100.21.74", {"start": v(-10.3, 1.34) * mm, "end": v(-10.3, 1.33) * mm});
            skLineSegment(sketch, "E100.21.75", {"start": v(-10.29, 1.35) * mm, "end": v(-10.3, 1.34) * mm});
            skLineSegment(sketch, "E100.21.76", {"start": v(-10.28, 1.43) * mm, "end": v(-10.28, 1.4) * mm});
            skLineSegment(sketch, "E100.21.77", {"start": v(-10.3, 1.68) * mm, "end": v(-10.3, 1.7) * mm});
            skLineSegment(sketch, "E100.21.78", {"start": v(-10.38, 1.28) * mm, "end": v(-10.4, 1.27) * mm});
            skLineSegment(sketch, "E100.21.79", {"start": v(-10.42, 1.75) * mm, "end": v(-10.47, 1.77) * mm});
            skLineSegment(sketch, "E100.21.80", {"start": v(-10.26, 1.64) * mm, "end": v(-10.27, 1.65) * mm});
            skLineSegment(sketch, "E100.21.81", {"start": v(-10.29, 1.35) * mm, "end": v(-10.29, 1.35) * mm});
            skLineSegment(sketch, "E100.21.82", {"start": v(-10.4, 1.75) * mm, "end": v(-10.42, 1.75) * mm});
            skLineSegment(sketch, "E100.21.83", {"start": v(-10.27, 1.45) * mm, "end": v(-10.28, 1.43) * mm});
            skLineSegment(sketch, "E100.21.84", {"start": v(-10.4, 1.27) * mm, "end": v(-10.42, 1.26) * mm});
            skLineSegment(sketch, "E100.21.85", {"start": v(-10.28, 1.67) * mm, "end": v(-10.29, 1.67) * mm});
            skLineSegment(sketch, "E100.21.86", {"start": v(-10.27, 1.48) * mm, "end": v(-10.27, 1.45) * mm});
            skLineSegment(sketch, "E100.21.87", {"start": v(-10.46, 1.26) * mm, "end": v(-10.48, 1.26) * mm});
            skLineSegment(sketch, "E100.21.88", {"start": v(-10.29, 1.36) * mm, "end": v(-10.29, 1.35) * mm});
            skLineSegment(sketch, "E100.21.89", {"start": v(-10.28, 1.38) * mm, "end": v(-10.29, 1.36) * mm});
            skLineSegment(sketch, "E100.21.90", {"start": v(-10.25, 1.6) * mm, "end": v(-10.25, 1.6) * mm});
            skLineSegment(sketch, "E100.21.91", {"start": v(-10.26, 1.62) * mm, "end": v(-10.26, 1.63) * mm});
            skLineSegment(sketch, "E100.21.92", {"start": v(-10.27, 1.66) * mm, "end": v(-10.28, 1.67) * mm});
            skLineSegment(sketch, "E100.21.93", {"start": v(-10.26, 1.52) * mm, "end": v(-10.26, 1.55) * mm});
            skLineSegment(sketch, "E100.21.94", {"start": v(-10.28, 1.4) * mm, "end": v(-10.28, 1.38) * mm});
            skLineSegment(sketch, "E100.21.95", {"start": v(-10.33, 1.3) * mm, "end": v(-10.34, 1.3) * mm});
            skLineSegment(sketch, "E100.21.96", {"start": v(-10.25, 1.6) * mm, "end": v(-10.25, 1.62) * mm});
            skLineSegment(sketch, "E100.21.97", {"start": v(-10.32, 1.3) * mm, "end": v(-10.33, 1.3) * mm});
            skLineSegment(sketch, "E100.21.98", {"start": v(-10.34, 1.3) * mm, "end": v(-10.35, 1.29) * mm});
            skLineSegment(sketch, "E100.21.99", {"start": v(-10.35, 1.29) * mm, "end": v(-10.37, 1.28) * mm});
            skLineSegment(sketch, "E100.22.0", {"start": v(-11.48, 0.67) * mm, "end": v(-11.48, 0.7) * mm});
            skLineSegment(sketch, "E100.22.1", {"start": v(-11.48, -0.7) * mm, "end": v(-11.48, -0.74) * mm});
            skLineSegment(sketch, "E100.22.2", {"start": v(-11.35, -0.56) * mm, "end": v(-11.4, -0.58) * mm});
            skLineSegment(sketch, "E100.22.3", {"start": v(-11.47, -0.78) * mm, "end": v(-11.47, -0.82) * mm});
            skLineSegment(sketch, "E100.22.4", {"start": v(-11.07, 0.43) * mm, "end": v(-11.12, 0.45) * mm});
            skLineSegment(sketch, "E100.22.5", {"start": v(-11.48, 0.74) * mm, "end": v(-11.47, 0.78) * mm});
            skLineSegment(sketch, "E100.22.6", {"start": v(-11.48, -0.67) * mm, "end": v(-11.48, -0.7) * mm});
            skLineSegment(sketch, "E100.22.7", {"start": v(-11.3, 0.53) * mm, "end": v(-11.35, 0.56) * mm});
            skLineSegment(sketch, "E100.22.8", {"start": v(-11.48, -0.74) * mm, "end": v(-11.47, -0.78) * mm});
            skLineSegment(sketch, "E100.22.9", {"start": v(-11.35, 0.56) * mm, "end": v(-11.4, 0.58) * mm});
            skLineSegment(sketch, "E100.22.10", {"start": v(-11.47, 0.78) * mm, "end": v(-11.47, 0.82) * mm});
            skLineSegment(sketch, "E100.22.11", {"start": v(-11.4, 0.58) * mm, "end": v(-11.44, 0.6) * mm});
            skLineSegment(sketch, "E100.22.12", {"start": v(-11.26, 0.51) * mm, "end": v(-11.3, 0.53) * mm});
            skLineSegment(sketch, "E100.22.13", {"start": v(-11.44, -0.6) * mm, "end": v(-11.48, -0.63) * mm});
            skLineSegment(sketch, "E100.22.14", {"start": v(-11.48, 0.63) * mm, "end": v(-11.48, 0.67) * mm});
            skLineSegment(sketch, "E100.22.15", {"start": v(-11.12, 0.45) * mm, "end": v(-11.16, 0.47) * mm});
            skLineSegment(sketch, "E100.22.16", {"start": v(-11.48, 0.7) * mm, "end": v(-11.48, 0.74) * mm});
            skLineSegment(sketch, "E100.22.17", {"start": v(-11.48, -0.63) * mm, "end": v(-11.48, -0.67) * mm});
            skLineSegment(sketch, "E100.22.18", {"start": v(-11.26, -0.51) * mm, "end": v(-11.3, -0.53) * mm});
            skLineSegment(sketch, "E100.22.19", {"start": v(-11.21, 0.49) * mm, "end": v(-11.26, 0.51) * mm});
            skLineSegment(sketch, "E100.22.20", {"start": v(-11.44, 0.6) * mm, "end": v(-11.48, 0.63) * mm});
            skLineSegment(sketch, "E100.22.21", {"start": v(-11.12, -0.45) * mm, "end": v(-11.16, -0.47) * mm});
            skLineSegment(sketch, "E100.22.22", {"start": v(-11.3, -0.53) * mm, "end": v(-11.35, -0.56) * mm});
            skLineSegment(sketch, "E100.22.23", {"start": v(-11.16, 0.47) * mm, "end": v(-11.21, 0.49) * mm});
            skLineSegment(sketch, "E100.22.24", {"start": v(-11.16, -0.47) * mm, "end": v(-11.21, -0.49) * mm});
            skLineSegment(sketch, "E100.22.25", {"start": v(-11.21, -0.49) * mm, "end": v(-11.26, -0.51) * mm});
            skLineSegment(sketch, "E100.22.26", {"start": v(-11.4, -0.58) * mm, "end": v(-11.44, -0.6) * mm});
            skLineSegment(sketch, "E100.22.27", {"start": v(-11.07, -0.43) * mm, "end": v(-11.12, -0.45) * mm});
            skLineSegment(sketch, "E100.22.28", {"start": v(-10.44, -0.2) * mm, "end": v(-10.46, -0.21) * mm});
            skLineSegment(sketch, "E100.22.29", {"start": v(-10.7, -0.3) * mm, "end": v(-10.75, -0.3) * mm});
            skLineSegment(sketch, "E100.22.30", {"start": v(-10.84, -0.34) * mm, "end": v(-10.89, -0.35) * mm});
            skLineSegment(sketch, "E100.22.31", {"start": v(-10.47, 0.22) * mm, "end": v(-10.48, 0.23) * mm});
            skLineSegment(sketch, "E100.22.32", {"start": v(-11.03, 0.4) * mm, "end": v(-11.07, 0.43) * mm});
            skLineSegment(sketch, "E100.22.33", {"start": v(-10.4, -0.17) * mm, "end": v(-10.4, -0.18) * mm});
            skLineSegment(sketch, "E100.22.34", {"start": v(-10.4, 0.17) * mm, "end": v(-10.4, 0.18) * mm});
            skLineSegment(sketch, "E100.22.35", {"start": v(-10.47, -0.22) * mm, "end": v(-10.48, -0.23) * mm});
            skLineSegment(sketch, "E100.22.36", {"start": v(-10.57, -0.25) * mm, "end": v(-10.61, -0.26) * mm});
            skLineSegment(sketch, "E100.22.37", {"start": v(-10.94, 0.37) * mm, "end": v(-10.98, 0.39) * mm});
            skLineSegment(sketch, "E100.22.38", {"start": v(-10.66, 0.28) * mm, "end": v(-10.7, 0.3) * mm});
            skLineSegment(sketch, "E100.22.39", {"start": v(-10.8, 0.32) * mm, "end": v(-10.84, 0.34) * mm});
            skLineSegment(sketch, "E100.22.40", {"start": v(-10.38, 0) * mm, "end": v(-10.37, 0.02) * mm});
            skLineSegment(sketch, "E100.22.41", {"start": v(-10.37, 0.02) * mm, "end": v(-10.37, 0.05) * mm});
            skLineSegment(sketch, "E100.22.42", {"start": v(-10.94, -0.37) * mm, "end": v(-10.98, -0.39) * mm});
            skLineSegment(sketch, "E100.22.43", {"start": v(-10.89, -0.35) * mm, "end": v(-10.94, -0.37) * mm});
            skLineSegment(sketch, "E100.22.44", {"start": v(-10.98, 0.39) * mm, "end": v(-11.03, 0.4) * mm});
            skLineSegment(sketch, "E100.22.45", {"start": v(-10.42, 0.2) * mm, "end": v(-10.43, 0.2) * mm});
            skLineSegment(sketch, "E100.22.46", {"start": v(-10.37, 0.12) * mm, "end": v(-10.38, 0.13) * mm});
            skLineSegment(sketch, "E100.22.47", {"start": v(-10.84, 0.34) * mm, "end": v(-10.89, 0.35) * mm});
            skLineSegment(sketch, "E100.22.48", {"start": v(-11.03, -0.4) * mm, "end": v(-11.07, -0.43) * mm});
            skLineSegment(sketch, "E100.22.49", {"start": v(-10.5, -0.23) * mm, "end": v(-10.51, -0.24) * mm});
            skLineSegment(sketch, "E100.22.50", {"start": v(-10.89, 0.35) * mm, "end": v(-10.94, 0.37) * mm});
            skLineSegment(sketch, "E100.22.51", {"start": v(-10.61, 0.26) * mm, "end": v(-10.66, 0.28) * mm});
            skLineSegment(sketch, "E100.22.52", {"start": v(-10.4, -0.16) * mm, "end": v(-10.4, -0.17) * mm});
            skLineSegment(sketch, "E100.22.53", {"start": v(-10.8, -0.32) * mm, "end": v(-10.84, -0.34) * mm});
            skLineSegment(sketch, "E100.22.54", {"start": v(-10.5, 0.23) * mm, "end": v(-10.51, 0.24) * mm});
            skLineSegment(sketch, "E100.22.55", {"start": v(-10.37, 0.1) * mm, "end": v(-10.37, 0.12) * mm});
            skLineSegment(sketch, "E100.22.56", {"start": v(-10.46, 0.21) * mm, "end": v(-10.47, 0.22) * mm});
            skLineSegment(sketch, "E100.22.57", {"start": v(-10.39, -0.16) * mm, "end": v(-10.4, -0.16) * mm});
            skLineSegment(sketch, "E100.22.58", {"start": v(-10.53, 0.24) * mm, "end": v(-10.55, 0.25) * mm});
            skLineSegment(sketch, "E100.22.59", {"start": v(-10.51, -0.24) * mm, "end": v(-10.53, -0.24) * mm});
            skLineSegment(sketch, "E100.22.60", {"start": v(-10.7, 0.3) * mm, "end": v(-10.75, 0.3) * mm});
            skLineSegment(sketch, "E100.22.61", {"start": v(-10.98, -0.39) * mm, "end": v(-11.03, -0.4) * mm});
            skLineSegment(sketch, "E100.22.62", {"start": v(-10.75, -0.3) * mm, "end": v(-10.8, -0.32) * mm});
            skLineSegment(sketch, "E100.22.63", {"start": v(-10.55, -0.25) * mm, "end": v(-10.57, -0.25) * mm});
            skLineSegment(sketch, "E100.22.64", {"start": v(-10.38, -0.15) * mm, "end": v(-10.39, -0.16) * mm});
            skLineSegment(sketch, "E100.22.65", {"start": v(-10.37, 0.07) * mm, "end": v(-10.37, 0.1) * mm});
            skLineSegment(sketch, "E100.22.66", {"start": v(-10.51, 0.24) * mm, "end": v(-10.53, 0.24) * mm});
            skLineSegment(sketch, "E100.22.67", {"start": v(-10.75, 0.3) * mm, "end": v(-10.8, 0.32) * mm});
            skLineSegment(sketch, "E100.22.68", {"start": v(-10.44, 0.2) * mm, "end": v(-10.46, 0.21) * mm});
            skLineSegment(sketch, "E100.22.69", {"start": v(-10.66, -0.28) * mm, "end": v(-10.7, -0.3) * mm});
            skLineSegment(sketch, "E100.22.70", {"start": v(-10.38, 0.14) * mm, "end": v(-10.38, 0.15) * mm});
            skLineSegment(sketch, "E100.22.71", {"start": v(-10.48, 0.23) * mm, "end": v(-10.5, 0.23) * mm});
            skLineSegment(sketch, "E100.22.72", {"start": v(-10.39, 0.16) * mm, "end": v(-10.4, 0.16) * mm});
            skLineSegment(sketch, "E100.22.73", {"start": v(-10.61, -0.26) * mm, "end": v(-10.66, -0.28) * mm});
            skLineSegment(sketch, "E100.22.74", {"start": v(-10.38, -0.14) * mm, "end": v(-10.38, -0.15) * mm});
            skLineSegment(sketch, "E100.22.75", {"start": v(-10.38, -0.13) * mm, "end": v(-10.38, -0.14) * mm});
            skLineSegment(sketch, "E100.22.76", {"start": v(-10.37, -0.05) * mm, "end": v(-10.37, -0.07) * mm});
            skLineSegment(sketch, "E100.22.77", {"start": v(-10.43, 0.2) * mm, "end": v(-10.44, 0.2) * mm});
            skLineSegment(sketch, "E100.22.78", {"start": v(-10.46, -0.21) * mm, "end": v(-10.47, -0.22) * mm});
            skLineSegment(sketch, "E100.22.79", {"start": v(-10.57, 0.25) * mm, "end": v(-10.61, 0.26) * mm});
            skLineSegment(sketch, "E100.22.80", {"start": v(-10.4, 0.16) * mm, "end": v(-10.4, 0.17) * mm});
            skLineSegment(sketch, "E100.22.81", {"start": v(-10.37, -0.12) * mm, "end": v(-10.38, -0.13) * mm});
            skLineSegment(sketch, "E100.22.82", {"start": v(-10.55, 0.25) * mm, "end": v(-10.57, 0.25) * mm});
            skLineSegment(sketch, "E100.22.83", {"start": v(-10.37, -0.02) * mm, "end": v(-10.37, -0.05) * mm});
            skLineSegment(sketch, "E100.22.84", {"start": v(-10.48, -0.23) * mm, "end": v(-10.5, -0.23) * mm});
            skLineSegment(sketch, "E100.22.85", {"start": v(-10.41, 0.19) * mm, "end": v(-10.42, 0.2) * mm});
            skLineSegment(sketch, "E100.22.86", {"start": v(-10.38, 0) * mm, "end": v(-10.37, -0.02) * mm});
            skLineSegment(sketch, "E100.22.87", {"start": v(-10.53, -0.24) * mm, "end": v(-10.55, -0.25) * mm});
            skLineSegment(sketch, "E100.22.88", {"start": v(-10.37, -0.12) * mm, "end": v(-10.37, -0.12) * mm});
            skLineSegment(sketch, "E100.22.89", {"start": v(-10.37, -0.1) * mm, "end": v(-10.37, -0.12) * mm});
            skLineSegment(sketch, "E100.22.90", {"start": v(-10.37, 0.12) * mm, "end": v(-10.37, 0.12) * mm});
            skLineSegment(sketch, "E100.22.91", {"start": v(-10.38, 0.15) * mm, "end": v(-10.39, 0.16) * mm});
            skLineSegment(sketch, "E100.22.92", {"start": v(-10.4, 0.18) * mm, "end": v(-10.41, 0.19) * mm});
            skLineSegment(sketch, "E100.22.93", {"start": v(-10.37, 0.05) * mm, "end": v(-10.37, 0.07) * mm});
            skLineSegment(sketch, "E100.22.94", {"start": v(-10.37, -0.07) * mm, "end": v(-10.37, -0.1) * mm});
            skLineSegment(sketch, "E100.22.95", {"start": v(-10.41, -0.19) * mm, "end": v(-10.42, -0.2) * mm});
            skLineSegment(sketch, "E100.22.96", {"start": v(-10.38, 0.13) * mm, "end": v(-10.38, 0.14) * mm});
            skLineSegment(sketch, "E100.22.97", {"start": v(-10.4, -0.18) * mm, "end": v(-10.41, -0.19) * mm});
            skLineSegment(sketch, "E100.22.98", {"start": v(-10.42, -0.2) * mm, "end": v(-10.43, -0.2) * mm});
            skLineSegment(sketch, "E100.22.99", {"start": v(-10.43, -0.2) * mm, "end": v(-10.44, -0.2) * mm});
            skLineSegment(sketch, "E100.23.0", {"start": v(-11.46, -0.97) * mm, "end": v(-11.46, -0.94) * mm});
            skLineSegment(sketch, "E100.23.1", {"start": v(-11.26, -2.33) * mm, "end": v(-11.25, -2.37) * mm});
            skLineSegment(sketch, "E100.23.2", {"start": v(-11.15, -2.17) * mm, "end": v(-11.2, -2.2) * mm});
            skLineSegment(sketch, "E100.23.3", {"start": v(-11.25, -2.4) * mm, "end": v(-11.24, -2.44) * mm});
            skLineSegment(sketch, "E100.23.4", {"start": v(-11.02, -1.15) * mm, "end": v(-11.07, -1.14) * mm});
            skLineSegment(sketch, "E100.23.5", {"start": v(-11.46, -0.9) * mm, "end": v(-11.47, -0.86) * mm});
            skLineSegment(sketch, "E100.23.6", {"start": v(-11.27, -2.3) * mm, "end": v(-11.26, -2.33) * mm});
            skLineSegment(sketch, "E100.23.7", {"start": v(-11.26, -1.08) * mm, "end": v(-11.31, -1.06) * mm});
            skLineSegment(sketch, "E100.23.8", {"start": v(-11.25, -2.37) * mm, "end": v(-11.25, -2.4) * mm});
            skLineSegment(sketch, "E100.23.9", {"start": v(-11.31, -1.06) * mm, "end": v(-11.36, -1.05) * mm});
            skLineSegment(sketch, "E100.23.10", {"start": v(-11.47, -0.86) * mm, "end": v(-11.47, -0.82) * mm});
            skLineSegment(sketch, "E100.23.11", {"start": v(-11.36, -1.05) * mm, "end": v(-11.4, -1.03) * mm});
            skLineSegment(sketch, "E100.23.12", {"start": v(-11.21, -1.1) * mm, "end": v(-11.26, -1.08) * mm});
            skLineSegment(sketch, "E100.23.13", {"start": v(-11.24, -2.23) * mm, "end": v(-11.28, -2.26) * mm});
            skLineSegment(sketch, "E100.23.14", {"start": v(-11.46, -1.01) * mm, "end": v(-11.46, -0.97) * mm});
            skLineSegment(sketch, "E100.23.15", {"start": v(-11.07, -1.14) * mm, "end": v(-11.12, -1.13) * mm});
            skLineSegment(sketch, "E100.23.16", {"start": v(-11.46, -0.94) * mm, "end": v(-11.46, -0.9) * mm});
            skLineSegment(sketch, "E100.23.17", {"start": v(-11.28, -2.26) * mm, "end": v(-11.27, -2.3) * mm});
            skLineSegment(sketch, "E100.23.18", {"start": v(-11.07, -2.1) * mm, "end": v(-11.11, -2.14) * mm});
            skLineSegment(sketch, "E100.23.19", {"start": v(-11.17, -1.11) * mm, "end": v(-11.21, -1.1) * mm});
            skLineSegment(sketch, "E100.23.20", {"start": v(-11.4, -1.03) * mm, "end": v(-11.46, -1.01) * mm});
            skLineSegment(sketch, "E100.23.21", {"start": v(-10.94, -2.02) * mm, "end": v(-10.98, -2.05) * mm});
            skLineSegment(sketch, "E100.23.22", {"start": v(-11.11, -2.14) * mm, "end": v(-11.15, -2.17) * mm});
            skLineSegment(sketch, "E100.23.23", {"start": v(-11.12, -1.13) * mm, "end": v(-11.17, -1.11) * mm});
            skLineSegment(sketch, "E100.23.24", {"start": v(-10.98, -2.05) * mm, "end": v(-11.03, -2.08) * mm});
            skLineSegment(sketch, "E100.23.25", {"start": v(-11.03, -2.08) * mm, "end": v(-11.07, -2.1) * mm});
            skLineSegment(sketch, "E100.23.26", {"start": v(-11.2, -2.2) * mm, "end": v(-11.24, -2.23) * mm});
            skLineSegment(sketch, "E100.23.27", {"start": v(-10.9, -2) * mm, "end": v(-10.94, -2.02) * mm});
            skLineSegment(sketch, "E100.23.28", {"start": v(-10.3, -1.7) * mm, "end": v(-10.32, -1.7) * mm});
            skLineSegment(sketch, "E100.23.29", {"start": v(-10.55, -1.81) * mm, "end": v(-10.6, -1.83) * mm});
            skLineSegment(sketch, "E100.23.30", {"start": v(-10.69, -1.88) * mm, "end": v(-10.73, -1.9) * mm});
            skLineSegment(sketch, "E100.23.31", {"start": v(-10.4, -1.27) * mm, "end": v(-10.4, -1.27) * mm});
            skLineSegment(sketch, "E100.23.32", {"start": v(-10.97, -1.17) * mm, "end": v(-11.02, -1.15) * mm});
            skLineSegment(sketch, "E100.23.33", {"start": v(-10.27, -1.65) * mm, "end": v(-10.27, -1.66) * mm});
            skLineSegment(sketch, "E100.23.34", {"start": v(-10.32, -1.31) * mm, "end": v(-10.32, -1.3) * mm});
            skLineSegment(sketch, "E100.23.35", {"start": v(-10.33, -1.7) * mm, "end": v(-10.34, -1.72) * mm});
            skLineSegment(sketch, "E100.23.36", {"start": v(-10.42, -1.75) * mm, "end": v(-10.47, -1.77) * mm});
            skLineSegment(sketch, "E100.23.37", {"start": v(-10.88, -1.2) * mm, "end": v(-10.92, -1.18) * mm});
            skLineSegment(sketch, "E100.23.38", {"start": v(-10.59, -1.24) * mm, "end": v(-10.64, -1.24) * mm});
            skLineSegment(sketch, "E100.23.39", {"start": v(-10.73, -1.22) * mm, "end": v(-10.78, -1.21) * mm});
            skLineSegment(sketch, "E100.23.40", {"start": v(-10.27, -1.48) * mm, "end": v(-10.27, -1.45) * mm});
            skLineSegment(sketch, "E100.23.41", {"start": v(-10.27, -1.45) * mm, "end": v(-10.28, -1.43) * mm});
            skLineSegment(sketch, "E100.23.42", {"start": v(-10.77, -1.92) * mm, "end": v(-10.81, -1.95) * mm});
            skLineSegment(sketch, "E100.23.43", {"start": v(-10.73, -1.9) * mm, "end": v(-10.77, -1.92) * mm});
            skLineSegment(sketch, "E100.23.44", {"start": v(-10.92, -1.18) * mm, "end": v(-10.97, -1.17) * mm});
            skLineSegment(sketch, "E100.23.45", {"start": v(-10.34, -1.3) * mm, "end": v(-10.35, -1.29) * mm});
            skLineSegment(sketch, "E100.23.46", {"start": v(-10.29, -1.35) * mm, "end": v(-10.29, -1.35) * mm});
            skLineSegment(sketch, "E100.23.47", {"start": v(-10.78, -1.21) * mm, "end": v(-10.83, -1.2) * mm});
            skLineSegment(sketch, "E100.23.48", {"start": v(-10.86, -1.97) * mm, "end": v(-10.9, -2) * mm});
            skLineSegment(sketch, "E100.23.49", {"start": v(-10.36, -1.72) * mm, "end": v(-10.37, -1.73) * mm});
            skLineSegment(sketch, "E100.23.50", {"start": v(-10.83, -1.2) * mm, "end": v(-10.88, -1.2) * mm});
            skLineSegment(sketch, "E100.23.51", {"start": v(-10.54, -1.25) * mm, "end": v(-10.59, -1.24) * mm});
            skLineSegment(sketch, "E100.23.52", {"start": v(-10.26, -1.64) * mm, "end": v(-10.27, -1.65) * mm});
            skLineSegment(sketch, "E100.23.53", {"start": v(-10.64, -1.85) * mm, "end": v(-10.69, -1.88) * mm});
            skLineSegment(sketch, "E100.23.54", {"start": v(-10.42, -1.26) * mm, "end": v(-10.44, -1.26) * mm});
            skLineSegment(sketch, "E100.23.55", {"start": v(-10.28, -1.38) * mm, "end": v(-10.29, -1.36) * mm});
            skLineSegment(sketch, "E100.23.56", {"start": v(-10.38, -1.28) * mm, "end": v(-10.4, -1.27) * mm});
            skLineSegment(sketch, "E100.23.57", {"start": v(-10.26, -1.63) * mm, "end": v(-10.26, -1.64) * mm});
            skLineSegment(sketch, "E100.23.58", {"start": v(-10.46, -1.26) * mm, "end": v(-10.48, -1.26) * mm});
            skLineSegment(sketch, "E100.23.59", {"start": v(-10.37, -1.73) * mm, "end": v(-10.39, -1.74) * mm});
            skLineSegment(sketch, "E100.23.60", {"start": v(-10.64, -1.24) * mm, "end": v(-10.69, -1.23) * mm});
            skLineSegment(sketch, "E100.23.61", {"start": v(-10.81, -1.95) * mm, "end": v(-10.86, -1.97) * mm});
            skLineSegment(sketch, "E100.23.62", {"start": v(-10.6, -1.83) * mm, "end": v(-10.64, -1.85) * mm});
            skLineSegment(sketch, "E100.23.63", {"start": v(-10.4, -1.75) * mm, "end": v(-10.42, -1.75) * mm});
            skLineSegment(sketch, "E100.23.64", {"start": v(-10.26, -1.62) * mm, "end": v(-10.26, -1.63) * mm});
            skLineSegment(sketch, "E100.23.65", {"start": v(-10.28, -1.4) * mm, "end": v(-10.28, -1.38) * mm});
            skLineSegment(sketch, "E100.23.66", {"start": v(-10.44, -1.26) * mm, "end": v(-10.46, -1.26) * mm});
            skLineSegment(sketch, "E100.23.67", {"start": v(-10.69, -1.23) * mm, "end": v(-10.73, -1.22) * mm});
            skLineSegment(sketch, "E100.23.68", {"start": v(-10.37, -1.28) * mm, "end": v(-10.38, -1.28) * mm});
            skLineSegment(sketch, "E100.23.69", {"start": v(-10.51, -1.8) * mm, "end": v(-10.55, -1.81) * mm});
            skLineSegment(sketch, "E100.23.70", {"start": v(-10.3, -1.34) * mm, "end": v(-10.3, -1.33) * mm});
            skLineSegment(sketch, "E100.23.71", {"start": v(-10.4, -1.27) * mm, "end": v(-10.42, -1.26) * mm});
            skLineSegment(sketch, "E100.23.72", {"start": v(-10.3, -1.32) * mm, "end": v(-10.3, -1.32) * mm});
            skLineSegment(sketch, "E100.23.73", {"start": v(-10.47, -1.77) * mm, "end": v(-10.51, -1.8) * mm});
            skLineSegment(sketch, "E100.23.74", {"start": v(-10.25, -1.62) * mm, "end": v(-10.26, -1.62) * mm});
            skLineSegment(sketch, "E100.23.75", {"start": v(-10.25, -1.6) * mm, "end": v(-10.25, -1.62) * mm});
            skLineSegment(sketch, "E100.23.76", {"start": v(-10.26, -1.52) * mm, "end": v(-10.26, -1.55) * mm});
            skLineSegment(sketch, "E100.23.77", {"start": v(-10.35, -1.29) * mm, "end": v(-10.37, -1.28) * mm});
            skLineSegment(sketch, "E100.23.78", {"start": v(-10.32, -1.7) * mm, "end": v(-10.33, -1.7) * mm});
            skLineSegment(sketch, "E100.23.79", {"start": v(-10.5, -1.25) * mm, "end": v(-10.54, -1.25) * mm});
            skLineSegment(sketch, "E100.23.80", {"start": v(-10.3, -1.32) * mm, "end": v(-10.32, -1.31) * mm});
            skLineSegment(sketch, "E100.23.81", {"start": v(-10.25, -1.6) * mm, "end": v(-10.25, -1.6) * mm});
            skLineSegment(sketch, "E100.23.82", {"start": v(-10.48, -1.26) * mm, "end": v(-10.5, -1.25) * mm});
            skLineSegment(sketch, "E100.23.83", {"start": v(-10.27, -1.5) * mm, "end": v(-10.26, -1.52) * mm});
            skLineSegment(sketch, "E100.23.84", {"start": v(-10.34, -1.72) * mm, "end": v(-10.36, -1.72) * mm});
            skLineSegment(sketch, "E100.23.85", {"start": v(-10.33, -1.3) * mm, "end": v(-10.34, -1.3) * mm});
            skLineSegment(sketch, "E100.23.86", {"start": v(-10.27, -1.48) * mm, "end": v(-10.27, -1.5) * mm});
            skLineSegment(sketch, "E100.23.87", {"start": v(-10.39, -1.74) * mm, "end": v(-10.4, -1.75) * mm});
            skLineSegment(sketch, "E100.23.88", {"start": v(-10.25, -1.6) * mm, "end": v(-10.25, -1.6) * mm});
            skLineSegment(sketch, "E100.23.89", {"start": v(-10.26, -1.57) * mm, "end": v(-10.25, -1.6) * mm});
            skLineSegment(sketch, "E100.23.90", {"start": v(-10.29, -1.36) * mm, "end": v(-10.29, -1.35) * mm});
            skLineSegment(sketch, "E100.23.91", {"start": v(-10.3, -1.33) * mm, "end": v(-10.3, -1.32) * mm});
            skLineSegment(sketch, "E100.23.92", {"start": v(-10.32, -1.3) * mm, "end": v(-10.33, -1.3) * mm});
            skLineSegment(sketch, "E100.23.93", {"start": v(-10.28, -1.43) * mm, "end": v(-10.28, -1.4) * mm});
            skLineSegment(sketch, "E100.23.94", {"start": v(-10.26, -1.55) * mm, "end": v(-10.26, -1.57) * mm});
            skLineSegment(sketch, "E100.23.95", {"start": v(-10.28, -1.67) * mm, "end": v(-10.29, -1.67) * mm});
            skLineSegment(sketch, "E100.23.96", {"start": v(-10.29, -1.35) * mm, "end": v(-10.3, -1.34) * mm});
            skLineSegment(sketch, "E100.23.97", {"start": v(-10.27, -1.66) * mm, "end": v(-10.28, -1.67) * mm});
            skLineSegment(sketch, "E100.23.98", {"start": v(-10.29, -1.67) * mm, "end": v(-10.3, -1.68) * mm});
            skLineSegment(sketch, "E100.23.99", {"start": v(-10.3, -1.68) * mm, "end": v(-10.3, -1.7) * mm});
            skLineSegment(sketch, "E100.24.0", {"start": v(-11.2, -2.6) * mm, "end": v(-11.21, -2.56) * mm});
            skLineSegment(sketch, "E100.24.1", {"start": v(-10.81, -3.91) * mm, "end": v(-10.8, -3.95) * mm});
            skLineSegment(sketch, "E100.24.2", {"start": v(-10.73, -3.73) * mm, "end": v(-10.77, -3.77) * mm});
            skLineSegment(sketch, "E100.24.3", {"start": v(-10.79, -3.98) * mm, "end": v(-10.77, -4.02) * mm});
            skLineSegment(sketch, "E100.24.4", {"start": v(-10.74, -2.71) * mm, "end": v(-10.8, -2.7) * mm});
            skLineSegment(sketch, "E100.24.5", {"start": v(-11.22, -2.52) * mm, "end": v(-11.23, -2.48) * mm});
            skLineSegment(sketch, "E100.24.6", {"start": v(-10.83, -3.87) * mm, "end": v(-10.81, -3.91) * mm});
            skLineSegment(sketch, "E100.24.7", {"start": v(-11, -2.67) * mm, "end": v(-11.04, -2.66) * mm});
            skLineSegment(sketch, "E100.24.8", {"start": v(-10.8, -3.95) * mm, "end": v(-10.79, -3.98) * mm});
            skLineSegment(sketch, "E100.24.9", {"start": v(-11.04, -2.66) * mm, "end": v(-11.1, -2.65) * mm});
            skLineSegment(sketch, "E100.24.10", {"start": v(-11.23, -2.48) * mm, "end": v(-11.24, -2.44) * mm});
            skLineSegment(sketch, "E100.24.11", {"start": v(-11.1, -2.65) * mm, "end": v(-11.14, -2.64) * mm});
            skLineSegment(sketch, "E100.24.12", {"start": v(-10.94, -2.68) * mm, "end": v(-11, -2.67) * mm});
            skLineSegment(sketch, "E100.24.13", {"start": v(-10.8, -3.8) * mm, "end": v(-10.84, -3.84) * mm});
            skLineSegment(sketch, "E100.24.14", {"start": v(-11.2, -2.63) * mm, "end": v(-11.2, -2.6) * mm});
            skLineSegment(sketch, "E100.24.15", {"start": v(-10.8, -2.7) * mm, "end": v(-10.84, -2.7) * mm});
            skLineSegment(sketch, "E100.24.16", {"start": v(-11.21, -2.56) * mm, "end": v(-11.22, -2.52) * mm});
            skLineSegment(sketch, "E100.24.17", {"start": v(-10.84, -3.84) * mm, "end": v(-10.83, -3.87) * mm});
            skLineSegment(sketch, "E100.24.18", {"start": v(-10.66, -3.66) * mm, "end": v(-10.7, -3.7) * mm});
            skLineSegment(sketch, "E100.24.19", {"start": v(-10.9, -2.69) * mm, "end": v(-10.94, -2.68) * mm});
            skLineSegment(sketch, "E100.24.20", {"start": v(-11.14, -2.64) * mm, "end": v(-11.2, -2.63) * mm});
            skLineSegment(sketch, "E100.24.21", {"start": v(-10.54, -3.56) * mm, "end": v(-10.58, -3.6) * mm});
            skLineSegment(sketch, "E100.24.22", {"start": v(-10.7, -3.7) * mm, "end": v(-10.73, -3.73) * mm});
            skLineSegment(sketch, "E100.24.23", {"start": v(-10.84, -2.7) * mm, "end": v(-10.9, -2.69) * mm});
            skLineSegment(sketch, "E100.24.24", {"start": v(-10.58, -3.6) * mm, "end": v(-10.62, -3.63) * mm});
            skLineSegment(sketch, "E100.24.25", {"start": v(-10.62, -3.63) * mm, "end": v(-10.66, -3.66) * mm});
            skLineSegment(sketch, "E100.24.26", {"start": v(-10.77, -3.77) * mm, "end": v(-10.8, -3.8) * mm});
            skLineSegment(sketch, "E100.24.27", {"start": v(-10.5, -3.53) * mm, "end": v(-10.54, -3.56) * mm});
            skLineSegment(sketch, "E100.24.28", {"start": v(-9.96, -3.14) * mm, "end": v(-9.97, -3.15) * mm});
            skLineSegment(sketch, "E100.24.29", {"start": v(-10.19, -3.3) * mm, "end": v(-10.23, -3.32) * mm});
            skLineSegment(sketch, "E100.24.30", {"start": v(-10.3, -3.38) * mm, "end": v(-10.35, -3.4) * mm});
            skLineSegment(sketch, "E100.24.31", {"start": v(-10.1, -2.74) * mm, "end": v(-10.12, -2.74) * mm});
            skLineSegment(sketch, "E100.24.32", {"start": v(-10.7, -2.72) * mm, "end": v(-10.74, -2.71) * mm});
            skLineSegment(sketch, "E100.24.33", {"start": v(-9.93, -3.1) * mm, "end": v(-9.93, -3.1) * mm});
            skLineSegment(sketch, "E100.24.34", {"start": v(-10.02, -2.76) * mm, "end": v(-10.03, -2.76) * mm});
            skLineSegment(sketch, "E100.24.35", {"start": v(-9.98, -3.16) * mm, "end": v(-10, -3.17) * mm});
            skLineSegment(sketch, "E100.24.36", {"start": v(-10.07, -3.22) * mm, "end": v(-10.1, -3.24) * mm});
            skLineSegment(sketch, "E100.24.37", {"start": v(-10.6, -2.73) * mm, "end": v(-10.65, -2.72) * mm});
            skLineSegment(sketch, "E100.24.38", {"start": v(-10.3, -2.74) * mm, "end": v(-10.35, -2.74) * mm});
            skLineSegment(sketch, "E100.24.39", {"start": v(-10.45, -2.73) * mm, "end": v(-10.5, -2.73) * mm});
            skLineSegment(sketch, "E100.24.40", {"start": v(-9.95, -2.92) * mm, "end": v(-9.96, -2.9) * mm});
            skLineSegment(sketch, "E100.24.41", {"start": v(-9.96, -2.9) * mm, "end": v(-9.97, -2.88) * mm});
            skLineSegment(sketch, "E100.24.42", {"start": v(-10.39, -3.44) * mm, "end": v(-10.43, -3.47) * mm});
            skLineSegment(sketch, "E100.24.43", {"start": v(-10.35, -3.4) * mm, "end": v(-10.39, -3.44) * mm});
            skLineSegment(sketch, "E100.24.44", {"start": v(-10.65, -2.72) * mm, "end": v(-10.7, -2.72) * mm});
            skLineSegment(sketch, "E100.24.45", {"start": v(-10.05, -2.75) * mm, "end": v(-10.07, -2.75) * mm});
            skLineSegment(sketch, "E100.24.46", {"start": v(-9.99, -2.8) * mm, "end": v(-10, -2.8) * mm});
            skLineSegment(sketch, "E100.24.47", {"start": v(-10.5, -2.73) * mm, "end": v(-10.55, -2.73) * mm});
            skLineSegment(sketch, "E100.24.48", {"start": v(-10.47, -3.5) * mm, "end": v(-10.5, -3.53) * mm});
            skLineSegment(sketch, "E100.24.49", {"start": v(-10, -3.18) * mm, "end": v(-10.02, -3.2) * mm});
            skLineSegment(sketch, "E100.24.50", {"start": v(-10.55, -2.73) * mm, "end": v(-10.6, -2.73) * mm});
            skLineSegment(sketch, "E100.24.51", {"start": v(-10.26, -2.74) * mm, "end": v(-10.3, -2.74) * mm});
            skLineSegment(sketch, "E100.24.52", {"start": v(-9.92, -3.08) * mm, "end": v(-9.93, -3.1) * mm});
            skLineSegment(sketch, "E100.24.53", {"start": v(-10.27, -3.35) * mm, "end": v(-10.3, -3.38) * mm});
            skLineSegment(sketch, "E100.24.54", {"start": v(-10.14, -2.73) * mm, "end": v(-10.15, -2.73) * mm});
            skLineSegment(sketch, "E100.24.55", {"start": v(-9.98, -2.83) * mm, "end": v(-9.99, -2.81) * mm});
            skLineSegment(sketch, "E100.24.56", {"start": v(-10.1, -2.74) * mm, "end": v(-10.1, -2.74) * mm});
            skLineSegment(sketch, "E100.24.57", {"start": v(-9.92, -3.08) * mm, "end": v(-9.92, -3.08) * mm});
            skLineSegment(sketch, "E100.24.58", {"start": v(-10.17, -2.73) * mm, "end": v(-10.2, -2.73) * mm});
            skLineSegment(sketch, "E100.24.59", {"start": v(-10.02, -3.2) * mm, "end": v(-10.03, -3.2) * mm});
            skLineSegment(sketch, "E100.24.60", {"start": v(-10.35, -2.74) * mm, "end": v(-10.4, -2.74) * mm});
            skLineSegment(sketch, "E100.24.61", {"start": v(-10.43, -3.47) * mm, "end": v(-10.47, -3.5) * mm});
            skLineSegment(sketch, "E100.24.62", {"start": v(-10.23, -3.32) * mm, "end": v(-10.27, -3.35) * mm});
            skLineSegment(sketch, "E100.24.63", {"start": v(-10.05, -3.2) * mm, "end": v(-10.07, -3.22) * mm});
            skLineSegment(sketch, "E100.24.64", {"start": v(-9.92, -3.07) * mm, "end": v(-9.92, -3.08) * mm});
            skLineSegment(sketch, "E100.24.65", {"start": v(-9.97, -2.86) * mm, "end": v(-9.98, -2.83) * mm});
            skLineSegment(sketch, "E100.24.66", {"start": v(-10.15, -2.73) * mm, "end": v(-10.17, -2.73) * mm});
            skLineSegment(sketch, "E100.24.67", {"start": v(-10.4, -2.74) * mm, "end": v(-10.45, -2.73) * mm});
            skLineSegment(sketch, "E100.24.68", {"start": v(-10.08, -2.74) * mm, "end": v(-10.1, -2.74) * mm});
            skLineSegment(sketch, "E100.24.69", {"start": v(-10.15, -3.27) * mm, "end": v(-10.19, -3.3) * mm});
            skLineSegment(sketch, "E100.24.70", {"start": v(-10, -2.79) * mm, "end": v(-10, -2.78) * mm});
            skLineSegment(sketch, "E100.24.71", {"start": v(-10.12, -2.74) * mm, "end": v(-10.14, -2.73) * mm});
            skLineSegment(sketch, "E100.24.72", {"start": v(-10, -2.78) * mm, "end": v(-10.02, -2.77) * mm});
            skLineSegment(sketch, "E100.24.73", {"start": v(-10.1, -3.24) * mm, "end": v(-10.15, -3.27) * mm});
            skLineSegment(sketch, "E100.24.74", {"start": v(-9.92, -3.06) * mm, "end": v(-9.92, -3.07) * mm});
            skLineSegment(sketch, "E100.24.75", {"start": v(-9.92, -3.05) * mm, "end": v(-9.92, -3.06) * mm});
            skLineSegment(sketch, "E100.24.76", {"start": v(-9.94, -2.97) * mm, "end": v(-9.93, -3) * mm});
            skLineSegment(sketch, "E100.24.77", {"start": v(-10.07, -2.75) * mm, "end": v(-10.08, -2.74) * mm});
            skLineSegment(sketch, "E100.24.78", {"start": v(-9.97, -3.15) * mm, "end": v(-9.98, -3.16) * mm});
            skLineSegment(sketch, "E100.24.79", {"start": v(-10.2, -2.73) * mm, "end": v(-10.26, -2.74) * mm});
            skLineSegment(sketch, "E100.24.80", {"start": v(-10.02, -2.77) * mm, "end": v(-10.02, -2.76) * mm});
            skLineSegment(sketch, "E100.24.81", {"start": v(-9.92, -3.04) * mm, "end": v(-9.92, -3.05) * mm});
            skLineSegment(sketch, "E100.24.82", {"start": v(-10.2, -2.73) * mm, "end": v(-10.2, -2.73) * mm});
            skLineSegment(sketch, "E100.24.83", {"start": v(-9.95, -2.95) * mm, "end": v(-9.94, -2.97) * mm});
            skLineSegment(sketch, "E100.24.84", {"start": v(-10, -3.17) * mm, "end": v(-10, -3.18) * mm});
            skLineSegment(sketch, "E100.24.85", {"start": v(-10.04, -2.76) * mm, "end": v(-10.05, -2.75) * mm});
            skLineSegment(sketch, "E100.24.86", {"start": v(-9.95, -2.92) * mm, "end": v(-9.95, -2.95) * mm});
            skLineSegment(sketch, "E100.24.87", {"start": v(-10.03, -3.2) * mm, "end": v(-10.05, -3.2) * mm});
            skLineSegment(sketch, "E100.24.88", {"start": v(-9.92, -3.03) * mm, "end": v(-9.92, -3.04) * mm});
            skLineSegment(sketch, "E100.24.89", {"start": v(-9.93, -3.01) * mm, "end": v(-9.92, -3.03) * mm});
            skLineSegment(sketch, "E100.24.90", {"start": v(-9.99, -2.81) * mm, "end": v(-9.99, -2.8) * mm});
            skLineSegment(sketch, "E100.24.91", {"start": v(-10, -2.78) * mm, "end": v(-10, -2.78) * mm});
            skLineSegment(sketch, "E100.24.92", {"start": v(-10.03, -2.76) * mm, "end": v(-10.04, -2.76) * mm});
            skLineSegment(sketch, "E100.24.93", {"start": v(-9.97, -2.88) * mm, "end": v(-9.97, -2.86) * mm});
            skLineSegment(sketch, "E100.24.94", {"start": v(-9.93, -3) * mm, "end": v(-9.93, -3.01) * mm});
            skLineSegment(sketch, "E100.24.95", {"start": v(-9.94, -3.11) * mm, "end": v(-9.95, -3.12) * mm});
            skLineSegment(sketch, "E100.24.96", {"start": v(-10, -2.8) * mm, "end": v(-10, -2.79) * mm});
            skLineSegment(sketch, "E100.24.97", {"start": v(-9.93, -3.1) * mm, "end": v(-9.94, -3.11) * mm});
            skLineSegment(sketch, "E100.24.98", {"start": v(-9.95, -3.12) * mm, "end": v(-9.95, -3.13) * mm});
            skLineSegment(sketch, "E100.24.99", {"start": v(-9.95, -3.13) * mm, "end": v(-9.96, -3.14) * mm});
            skLineSegment(sketch, "E100.25.0", {"start": v(-10.72, -4.16) * mm, "end": v(-10.73, -4.13) * mm});
            skLineSegment(sketch, "E100.25.1", {"start": v(-10.15, -5.41) * mm, "end": v(-10.13, -5.44) * mm});
            skLineSegment(sketch, "E100.25.2", {"start": v(-10.1, -5.22) * mm, "end": v(-10.12, -5.26) * mm});
            skLineSegment(sketch, "E100.25.3", {"start": v(-10.11, -5.48) * mm, "end": v(-10.1, -5.51) * mm});
            skLineSegment(sketch, "E100.25.4", {"start": v(-10.25, -4.21) * mm, "end": v(-10.3, -4.21) * mm});
            skLineSegment(sketch, "E100.25.5", {"start": v(-10.75, -4.1) * mm, "end": v(-10.76, -4.05) * mm});
            skLineSegment(sketch, "E100.25.6", {"start": v(-10.17, -5.38) * mm, "end": v(-10.15, -5.41) * mm});
            skLineSegment(sketch, "E100.25.7", {"start": v(-10.5, -4.21) * mm, "end": v(-10.55, -4.2) * mm});
            skLineSegment(sketch, "E100.25.8", {"start": v(-10.13, -5.44) * mm, "end": v(-10.11, -5.48) * mm});
            skLineSegment(sketch, "E100.25.9", {"start": v(-10.55, -4.2) * mm, "end": v(-10.6, -4.2) * mm});
            skLineSegment(sketch, "E100.25.10", {"start": v(-10.76, -4.05) * mm, "end": v(-10.77, -4.02) * mm});
            skLineSegment(sketch, "E100.25.11", {"start": v(-10.6, -4.2) * mm, "end": v(-10.65, -4.2) * mm});
            skLineSegment(sketch, "E100.25.12", {"start": v(-10.45, -4.21) * mm, "end": v(-10.5, -4.21) * mm});
            skLineSegment(sketch, "E100.25.13", {"start": v(-10.15, -5.3) * mm, "end": v(-10.18, -5.34) * mm});
            skLineSegment(sketch, "E100.25.14", {"start": v(-10.7, -4.2) * mm, "end": v(-10.72, -4.16) * mm});
            skLineSegment(sketch, "E100.25.15", {"start": v(-10.3, -4.21) * mm, "end": v(-10.35, -4.21) * mm});
            skLineSegment(sketch, "E100.25.16", {"start": v(-10.73, -4.13) * mm, "end": v(-10.75, -4.1) * mm});
            skLineSegment(sketch, "E100.25.17", {"start": v(-10.18, -5.34) * mm, "end": v(-10.17, -5.38) * mm});
            skLineSegment(sketch, "E100.25.18", {"start": v(-10.03, -5.14) * mm, "end": v(-10.06, -5.18) * mm});
            skLineSegment(sketch, "E100.25.19", {"start": v(-10.4, -4.21) * mm, "end": v(-10.45, -4.21) * mm});
            skLineSegment(sketch, "E100.25.20", {"start": v(-10.65, -4.2) * mm, "end": v(-10.7, -4.2) * mm});
            skLineSegment(sketch, "E100.25.21", {"start": v(-9.93, -5.02) * mm, "end": v(-9.96, -5.06) * mm});
            skLineSegment(sketch, "E100.25.22", {"start": v(-10.06, -5.18) * mm, "end": v(-10.1, -5.22) * mm});
            skLineSegment(sketch, "E100.25.23", {"start": v(-10.35, -4.21) * mm, "end": v(-10.4, -4.21) * mm});
            skLineSegment(sketch, "E100.25.24", {"start": v(-9.96, -5.06) * mm, "end": v(-10, -5.1) * mm});
            skLineSegment(sketch, "E100.25.25", {"start": v(-10, -5.1) * mm, "end": v(-10.03, -5.14) * mm});
            skLineSegment(sketch, "E100.25.26", {"start": v(-10.12, -5.26) * mm, "end": v(-10.15, -5.3) * mm});
            skLineSegment(sketch, "E100.25.27", {"start": v(-9.9, -4.99) * mm, "end": v(-9.93, -5.02) * mm});
            skLineSegment(sketch, "E100.25.28", {"start": v(-9.41, -4.53) * mm, "end": v(-9.42, -4.54) * mm});
            skLineSegment(sketch, "E100.25.29", {"start": v(-9.62, -4.71) * mm, "end": v(-9.65, -4.74) * mm});
            skLineSegment(sketch, "E100.25.30", {"start": v(-9.72, -4.8) * mm, "end": v(-9.76, -4.84) * mm});
            skLineSegment(sketch, "E100.25.31", {"start": v(-9.61, -4.15) * mm, "end": v(-9.63, -4.15) * mm});
            skLineSegment(sketch, "E100.25.32", {"start": v(-10.2, -4.21) * mm, "end": v(-10.25, -4.21) * mm});
            skLineSegment(sketch, "E100.25.33", {"start": v(-9.39, -4.48) * mm, "end": v(-9.4, -4.48) * mm});
            skLineSegment(sketch, "E100.25.34", {"start": v(-9.53, -4.16) * mm, "end": v(-9.54, -4.16) * mm});
            skLineSegment(sketch, "E100.25.35", {"start": v(-9.43, -4.55) * mm, "end": v(-9.44, -4.56) * mm});
            skLineSegment(sketch, "E100.25.36", {"start": v(-9.5, -4.62) * mm, "end": v(-9.54, -4.65) * mm});
            skLineSegment(sketch, "E100.25.37", {"start": v(-10.1, -4.2) * mm, "end": v(-10.15, -4.2) * mm});
            skLineSegment(sketch, "E100.25.38", {"start": v(-9.81, -4.18) * mm, "end": v(-9.86, -4.18) * mm});
            skLineSegment(sketch, "E100.25.39", {"start": v(-9.95, -4.2) * mm, "end": v(-10, -4.2) * mm});
            skLineSegment(sketch, "E100.25.40", {"start": v(-9.44, -4.3) * mm, "end": v(-9.45, -4.29) * mm});
            skLineSegment(sketch, "E100.25.41", {"start": v(-9.45, -4.29) * mm, "end": v(-9.46, -4.27) * mm});
            skLineSegment(sketch, "E100.25.42", {"start": v(-9.8, -4.88) * mm, "end": v(-9.83, -4.91) * mm});
            skLineSegment(sketch, "E100.25.43", {"start": v(-9.76, -4.84) * mm, "end": v(-9.8, -4.88) * mm});
            skLineSegment(sketch, "E100.25.44", {"start": v(-10.15, -4.2) * mm, "end": v(-10.2, -4.21) * mm});
            skLineSegment(sketch, "E100.25.45", {"start": v(-9.56, -4.15) * mm, "end": v(-9.57, -4.15) * mm});
            skLineSegment(sketch, "E100.25.46", {"start": v(-9.49, -4.2) * mm, "end": v(-9.5, -4.19) * mm});
            skLineSegment(sketch, "E100.25.47", {"start": v(-10, -4.2) * mm, "end": v(-10.05, -4.2) * mm});
            skLineSegment(sketch, "E100.25.48", {"start": v(-9.86, -4.95) * mm, "end": v(-9.9, -4.99) * mm});
            skLineSegment(sketch, "E100.25.49", {"start": v(-9.45, -4.57) * mm, "end": v(-9.46, -4.58) * mm});
            skLineSegment(sketch, "E100.25.50", {"start": v(-10.05, -4.2) * mm, "end": v(-10.1, -4.2) * mm});
            skLineSegment(sketch, "E100.25.51", {"start": v(-9.76, -4.17) * mm, "end": v(-9.81, -4.18) * mm});
            skLineSegment(sketch, "E100.25.52", {"start": v(-9.38, -4.47) * mm, "end": v(-9.39, -4.48) * mm});
            skLineSegment(sketch, "E100.25.53", {"start": v(-9.69, -4.78) * mm, "end": v(-9.72, -4.8) * mm});
            skLineSegment(sketch, "E100.25.54", {"start": v(-9.65, -4.15) * mm, "end": v(-9.66, -4.15) * mm});
            skLineSegment(sketch, "E100.25.55", {"start": v(-9.48, -4.22) * mm, "end": v(-9.49, -4.2) * mm});
            skLineSegment(sketch, "E100.25.56", {"start": v(-9.6, -4.15) * mm, "end": v(-9.61, -4.15) * mm});
            skLineSegment(sketch, "E100.25.57", {"start": v(-9.38, -4.46) * mm, "end": v(-9.38, -4.47) * mm});
            skLineSegment(sketch, "E100.25.58", {"start": v(-9.68, -4.15) * mm, "end": v(-9.7, -4.16) * mm});
            skLineSegment(sketch, "E100.25.59", {"start": v(-9.46, -4.58) * mm, "end": v(-9.48, -4.6) * mm});
            skLineSegment(sketch, "E100.25.60", {"start": v(-9.86, -4.18) * mm, "end": v(-9.9, -4.19) * mm});
            skLineSegment(sketch, "E100.25.61", {"start": v(-9.83, -4.91) * mm, "end": v(-9.86, -4.95) * mm});
            skLineSegment(sketch, "E100.25.62", {"start": v(-9.65, -4.74) * mm, "end": v(-9.69, -4.78) * mm});
            skLineSegment(sketch, "E100.25.63", {"start": v(-9.5, -4.6) * mm, "end": v(-9.5, -4.62) * mm});
            skLineSegment(sketch, "E100.25.64", {"start": v(-9.38, -4.45) * mm, "end": v(-9.38, -4.46) * mm});
            skLineSegment(sketch, "E100.25.65", {"start": v(-9.47, -4.25) * mm, "end": v(-9.48, -4.22) * mm});
            skLineSegment(sketch, "E100.25.66", {"start": v(-9.66, -4.15) * mm, "end": v(-9.68, -4.15) * mm});
            skLineSegment(sketch, "E100.25.67", {"start": v(-9.9, -4.19) * mm, "end": v(-9.95, -4.2) * mm});
            skLineSegment(sketch, "E100.25.68", {"start": v(-9.59, -4.15) * mm, "end": v(-9.6, -4.15) * mm});
            skLineSegment(sketch, "E100.25.69", {"start": v(-9.58, -4.68) * mm, "end": v(-9.62, -4.71) * mm});
            skLineSegment(sketch, "E100.25.70", {"start": v(-9.5, -4.18) * mm, "end": v(-9.5, -4.18) * mm});
            skLineSegment(sketch, "E100.25.71", {"start": v(-9.63, -4.15) * mm, "end": v(-9.65, -4.15) * mm});
            skLineSegment(sketch, "E100.25.72", {"start": v(-9.51, -4.17) * mm, "end": v(-9.52, -4.17) * mm});
            skLineSegment(sketch, "E100.25.73", {"start": v(-9.54, -4.65) * mm, "end": v(-9.58, -4.68) * mm});
            skLineSegment(sketch, "E100.25.74", {"start": v(-9.38, -4.44) * mm, "end": v(-9.38, -4.45) * mm});
            skLineSegment(sketch, "E100.25.75", {"start": v(-9.38, -4.43) * mm, "end": v(-9.38, -4.44) * mm});
            skLineSegment(sketch, "E100.25.76", {"start": v(-9.42, -4.35) * mm, "end": v(-9.4, -4.37) * mm});
            skLineSegment(sketch, "E100.25.77", {"start": v(-9.57, -4.15) * mm, "end": v(-9.59, -4.15) * mm});
            skLineSegment(sketch, "E100.25.78", {"start": v(-9.42, -4.54) * mm, "end": v(-9.43, -4.55) * mm});
            skLineSegment(sketch, "E100.25.79", {"start": v(-9.72, -4.16) * mm, "end": v(-9.76, -4.17) * mm});
            skLineSegment(sketch, "E100.25.80", {"start": v(-9.52, -4.17) * mm, "end": v(-9.53, -4.16) * mm});
            skLineSegment(sketch, "E100.25.81", {"start": v(-9.39, -4.42) * mm, "end": v(-9.38, -4.43) * mm});
            skLineSegment(sketch, "E100.25.82", {"start": v(-9.7, -4.16) * mm, "end": v(-9.72, -4.16) * mm});
            skLineSegment(sketch, "E100.25.83", {"start": v(-9.43, -4.33) * mm, "end": v(-9.42, -4.35) * mm});
            skLineSegment(sketch, "E100.25.84", {"start": v(-9.44, -4.56) * mm, "end": v(-9.45, -4.57) * mm});
            skLineSegment(sketch, "E100.25.85", {"start": v(-9.55, -4.16) * mm, "end": v(-9.56, -4.15) * mm});
            skLineSegment(sketch, "E100.25.86", {"start": v(-9.44, -4.3) * mm, "end": v(-9.43, -4.33) * mm});
            skLineSegment(sketch, "E100.25.87", {"start": v(-9.48, -4.6) * mm, "end": v(-9.5, -4.6) * mm});
            skLineSegment(sketch, "E100.25.88", {"start": v(-9.39, -4.42) * mm, "end": v(-9.39, -4.42) * mm});
            skLineSegment(sketch, "E100.25.89", {"start": v(-9.4, -4.4) * mm, "end": v(-9.39, -4.42) * mm});
            skLineSegment(sketch, "E100.25.90", {"start": v(-9.49, -4.2) * mm, "end": v(-9.49, -4.2) * mm});
            skLineSegment(sketch, "E100.25.91", {"start": v(-9.5, -4.18) * mm, "end": v(-9.51, -4.17) * mm});
            skLineSegment(sketch, "E100.25.92", {"start": v(-9.54, -4.16) * mm, "end": v(-9.55, -4.16) * mm});
            skLineSegment(sketch, "E100.25.93", {"start": v(-9.46, -4.27) * mm, "end": v(-9.47, -4.25) * mm});
            skLineSegment(sketch, "E100.25.94", {"start": v(-9.4, -4.37) * mm, "end": v(-9.4, -4.4) * mm});
            skLineSegment(sketch, "E100.25.95", {"start": v(-9.4, -4.5) * mm, "end": v(-9.4, -4.5) * mm});
            skLineSegment(sketch, "E100.25.96", {"start": v(-9.5, -4.19) * mm, "end": v(-9.5, -4.18) * mm});
            skLineSegment(sketch, "E100.25.97", {"start": v(-9.4, -4.48) * mm, "end": v(-9.4, -4.5) * mm});
            skLineSegment(sketch, "E100.25.98", {"start": v(-9.4, -4.5) * mm, "end": v(-9.4, -4.52) * mm});
            skLineSegment(sketch, "E100.25.99", {"start": v(-9.4, -4.52) * mm, "end": v(-9.41, -4.53) * mm});
            skLineSegment(sketch, "E100.26.0", {"start": v(-10.02, -5.65) * mm, "end": v(-10.04, -5.61) * mm});
            skLineSegment(sketch, "E100.26.1", {"start": v(-9.27, -6.8) * mm, "end": v(-9.25, -6.83) * mm});
            skLineSegment(sketch, "E100.26.2", {"start": v(-9.24, -6.6) * mm, "end": v(-9.27, -6.65) * mm});
            skLineSegment(sketch, "E100.26.3", {"start": v(-9.23, -6.86) * mm, "end": v(-9.2, -6.9) * mm});
            skLineSegment(sketch, "E100.26.4", {"start": v(-9.55, -5.63) * mm, "end": v(-9.6, -5.64) * mm});
            skLineSegment(sketch, "E100.26.5", {"start": v(-10.06, -5.58) * mm, "end": v(-10.07, -5.55) * mm});
            skLineSegment(sketch, "E100.26.6", {"start": v(-9.3, -6.77) * mm, "end": v(-9.27, -6.8) * mm});
            skLineSegment(sketch, "E100.26.7", {"start": v(-9.8, -5.66) * mm, "end": v(-9.85, -5.67) * mm});
            skLineSegment(sketch, "E100.26.8", {"start": v(-9.25, -6.83) * mm, "end": v(-9.23, -6.86) * mm});
            skLineSegment(sketch, "E100.26.9", {"start": v(-9.85, -5.67) * mm, "end": v(-9.9, -5.67) * mm});
            skLineSegment(sketch, "E100.26.10", {"start": v(-10.07, -5.55) * mm, "end": v(-10.1, -5.51) * mm});
            skLineSegment(sketch, "E100.26.11", {"start": v(-9.9, -5.67) * mm, "end": v(-9.95, -5.68) * mm});
            skLineSegment(sketch, "E100.26.12", {"start": v(-9.74, -5.66) * mm, "end": v(-9.8, -5.66) * mm});
            skLineSegment(sketch, "E100.26.13", {"start": v(-9.3, -6.7) * mm, "end": v(-9.32, -6.74) * mm});
            skLineSegment(sketch, "E100.26.14", {"start": v(-10, -5.68) * mm, "end": v(-10.02, -5.65) * mm});
            skLineSegment(sketch, "E100.26.15", {"start": v(-9.6, -5.64) * mm, "end": v(-9.64, -5.64) * mm});
            skLineSegment(sketch, "E100.26.16", {"start": v(-10.04, -5.61) * mm, "end": v(-10.06, -5.58) * mm});
            skLineSegment(sketch, "E100.26.17", {"start": v(-9.32, -6.74) * mm, "end": v(-9.3, -6.77) * mm});
            skLineSegment(sketch, "E100.26.18", {"start": v(-9.2, -6.51) * mm, "end": v(-9.22, -6.56) * mm});
            skLineSegment(sketch, "E100.26.19", {"start": v(-9.7, -5.65) * mm, "end": v(-9.74, -5.66) * mm});
            skLineSegment(sketch, "E100.26.20", {"start": v(-9.95, -5.68) * mm, "end": v(-10, -5.68) * mm});
            skLineSegment(sketch, "E100.26.21", {"start": v(-9.11, -6.39) * mm, "end": v(-9.14, -6.43) * mm});
            skLineSegment(sketch, "E100.26.22", {"start": v(-9.22, -6.56) * mm, "end": v(-9.24, -6.6) * mm});
            skLineSegment(sketch, "E100.26.23", {"start": v(-9.64, -5.64) * mm, "end": v(-9.7, -5.65) * mm});
            skLineSegment(sketch, "E100.26.24", {"start": v(-9.14, -6.43) * mm, "end": v(-9.17, -6.47) * mm});
            skLineSegment(sketch, "E100.26.25", {"start": v(-9.17, -6.47) * mm, "end": v(-9.2, -6.51) * mm});
            skLineSegment(sketch, "E100.26.26", {"start": v(-9.27, -6.65) * mm, "end": v(-9.3, -6.7) * mm});
            skLineSegment(sketch, "E100.26.27", {"start": v(-9.08, -6.34) * mm, "end": v(-9.11, -6.39) * mm});
            skLineSegment(sketch, "E100.26.28", {"start": v(-8.67, -5.82) * mm, "end": v(-8.68, -5.83) * mm});
            skLineSegment(sketch, "E100.26.29", {"start": v(-8.85, -6.03) * mm, "end": v(-8.88, -6.07) * mm});
            skLineSegment(sketch, "E100.26.30", {"start": v(-8.94, -6.14) * mm, "end": v(-8.97, -6.18) * mm});
            skLineSegment(sketch, "E100.26.31", {"start": v(-8.93, -5.47) * mm, "end": v(-8.94, -5.48) * mm});
            skLineSegment(sketch, "E100.26.32", {"start": v(-9.5, -5.62) * mm, "end": v(-9.55, -5.63) * mm});
            skLineSegment(sketch, "E100.26.33", {"start": v(-8.65, -5.77) * mm, "end": v(-8.66, -5.78) * mm});
            skLineSegment(sketch, "E100.26.34", {"start": v(-8.84, -5.48) * mm, "end": v(-8.85, -5.47) * mm});
            skLineSegment(sketch, "E100.26.35", {"start": v(-8.69, -5.84) * mm, "end": v(-8.7, -5.86) * mm});
            skLineSegment(sketch, "E100.26.36", {"start": v(-8.75, -5.93) * mm, "end": v(-8.78, -5.96) * mm});
            skLineSegment(sketch, "E100.26.37", {"start": v(-9.4, -5.6) * mm, "end": v(-9.45, -5.61) * mm});
            skLineSegment(sketch, "E100.26.38", {"start": v(-9.12, -5.53) * mm, "end": v(-9.16, -5.54) * mm});
            skLineSegment(sketch, "E100.26.39", {"start": v(-9.26, -5.57) * mm, "end": v(-9.3, -5.58) * mm});
            skLineSegment(sketch, "E100.26.40", {"start": v(-8.73, -5.6) * mm, "end": v(-8.74, -5.59) * mm});
            skLineSegment(sketch, "E100.26.41", {"start": v(-8.74, -5.59) * mm, "end": v(-8.75, -5.57) * mm});
            skLineSegment(sketch, "E100.26.42", {"start": v(-9, -6.22) * mm, "end": v(-9.03, -6.26) * mm});
            skLineSegment(sketch, "E100.26.43", {"start": v(-8.97, -6.18) * mm, "end": v(-9, -6.22) * mm});
            skLineSegment(sketch, "E100.26.44", {"start": v(-9.45, -5.61) * mm, "end": v(-9.5, -5.62) * mm});
            skLineSegment(sketch, "E100.26.45", {"start": v(-8.87, -5.47) * mm, "end": v(-8.88, -5.47) * mm});
            skLineSegment(sketch, "E100.26.46", {"start": v(-8.8, -5.5) * mm, "end": v(-8.8, -5.5) * mm});
            skLineSegment(sketch, "E100.26.47", {"start": v(-9.3, -5.58) * mm, "end": v(-9.35, -5.6) * mm});
            skLineSegment(sketch, "E100.26.48", {"start": v(-9.06, -6.3) * mm, "end": v(-9.08, -6.34) * mm});
            skLineSegment(sketch, "E100.26.49", {"start": v(-8.7, -5.87) * mm, "end": v(-8.72, -5.88) * mm});
            skLineSegment(sketch, "E100.26.50", {"start": v(-9.35, -5.6) * mm, "end": v(-9.4, -5.6) * mm});
            skLineSegment(sketch, "E100.26.51", {"start": v(-9.07, -5.51) * mm, "end": v(-9.12, -5.53) * mm});
            skLineSegment(sketch, "E100.26.52", {"start": v(-8.65, -5.76) * mm, "end": v(-8.65, -5.77) * mm});
            skLineSegment(sketch, "E100.26.53", {"start": v(-8.91, -6.1) * mm, "end": v(-8.94, -6.14) * mm});
            skLineSegment(sketch, "E100.26.54", {"start": v(-8.96, -5.48) * mm, "end": v(-8.97, -5.48) * mm});
            skLineSegment(sketch, "E100.26.55", {"start": v(-8.78, -5.53) * mm, "end": v(-8.8, -5.51) * mm});
            skLineSegment(sketch, "E100.26.56", {"start": v(-8.91, -5.47) * mm, "end": v(-8.93, -5.47) * mm});
            skLineSegment(sketch, "E100.26.57", {"start": v(-8.65, -5.75) * mm, "end": v(-8.65, -5.76) * mm});
            skLineSegment(sketch, "E100.26.58", {"start": v(-8.99, -5.49) * mm, "end": v(-9, -5.5) * mm});
            skLineSegment(sketch, "E100.26.59", {"start": v(-8.72, -5.88) * mm, "end": v(-8.73, -5.9) * mm});
            skLineSegment(sketch, "E100.26.60", {"start": v(-9.16, -5.54) * mm, "end": v(-9.2, -5.56) * mm});
            skLineSegment(sketch, "E100.26.61", {"start": v(-9.03, -6.26) * mm, "end": v(-9.06, -6.3) * mm});
            skLineSegment(sketch, "E100.26.62", {"start": v(-8.88, -6.07) * mm, "end": v(-8.91, -6.1) * mm});
            skLineSegment(sketch, "E100.26.63", {"start": v(-8.74, -5.91) * mm, "end": v(-8.75, -5.93) * mm});
            skLineSegment(sketch, "E100.26.64", {"start": v(-8.65, -5.74) * mm, "end": v(-8.65, -5.75) * mm});
            skLineSegment(sketch, "E100.26.65", {"start": v(-8.77, -5.55) * mm, "end": v(-8.78, -5.53) * mm});
            skLineSegment(sketch, "E100.26.66", {"start": v(-8.97, -5.48) * mm, "end": v(-8.99, -5.49) * mm});
            skLineSegment(sketch, "E100.26.67", {"start": v(-9.2, -5.56) * mm, "end": v(-9.26, -5.57) * mm});
            skLineSegment(sketch, "E100.26.68", {"start": v(-8.9, -5.47) * mm, "end": v(-8.91, -5.47) * mm});
            skLineSegment(sketch, "E100.26.69", {"start": v(-8.82, -6) * mm, "end": v(-8.85, -6.03) * mm});
            skLineSegment(sketch, "E100.26.70", {"start": v(-8.8, -5.5) * mm, "end": v(-8.81, -5.49) * mm});
            skLineSegment(sketch, "E100.26.71", {"start": v(-8.94, -5.48) * mm, "end": v(-8.96, -5.48) * mm});
            skLineSegment(sketch, "E100.26.72", {"start": v(-8.82, -5.48) * mm, "end": v(-8.83, -5.48) * mm});
            skLineSegment(sketch, "E100.26.73", {"start": v(-8.78, -5.96) * mm, "end": v(-8.82, -6) * mm});
            skLineSegment(sketch, "E100.26.74", {"start": v(-8.65, -5.73) * mm, "end": v(-8.65, -5.74) * mm});
            skLineSegment(sketch, "E100.26.75", {"start": v(-8.66, -5.72) * mm, "end": v(-8.65, -5.73) * mm});
            skLineSegment(sketch, "E100.26.76", {"start": v(-8.7, -5.65) * mm, "end": v(-8.69, -5.67) * mm});
            skLineSegment(sketch, "E100.26.77", {"start": v(-8.88, -5.47) * mm, "end": v(-8.9, -5.47) * mm});
            skLineSegment(sketch, "E100.26.78", {"start": v(-8.68, -5.83) * mm, "end": v(-8.69, -5.84) * mm});
            skLineSegment(sketch, "E100.26.79", {"start": v(-9.03, -5.5) * mm, "end": v(-9.07, -5.51) * mm});
            skLineSegment(sketch, "E100.26.80", {"start": v(-8.83, -5.48) * mm, "end": v(-8.84, -5.48) * mm});
            skLineSegment(sketch, "E100.26.81", {"start": v(-8.66, -5.71) * mm, "end": v(-8.66, -5.72) * mm});
            skLineSegment(sketch, "E100.26.82", {"start": v(-9, -5.5) * mm, "end": v(-9.03, -5.5) * mm});
            skLineSegment(sketch, "E100.26.83", {"start": v(-8.72, -5.63) * mm, "end": v(-8.7, -5.65) * mm});
            skLineSegment(sketch, "E100.26.84", {"start": v(-8.7, -5.86) * mm, "end": v(-8.7, -5.87) * mm});
            skLineSegment(sketch, "E100.26.85", {"start": v(-8.86, -5.47) * mm, "end": v(-8.87, -5.47) * mm});
            skLineSegment(sketch, "E100.26.86", {"start": v(-8.73, -5.6) * mm, "end": v(-8.72, -5.63) * mm});
            skLineSegment(sketch, "E100.26.87", {"start": v(-8.73, -5.9) * mm, "end": v(-8.74, -5.91) * mm});
            skLineSegment(sketch, "E100.26.88", {"start": v(-8.66, -5.7) * mm, "end": v(-8.66, -5.71) * mm});
            skLineSegment(sketch, "E100.26.89", {"start": v(-8.68, -5.69) * mm, "end": v(-8.66, -5.7) * mm});
            skLineSegment(sketch, "E100.26.90", {"start": v(-8.8, -5.51) * mm, "end": v(-8.8, -5.5) * mm});
            skLineSegment(sketch, "E100.26.91", {"start": v(-8.81, -5.49) * mm, "end": v(-8.82, -5.48) * mm});
            skLineSegment(sketch, "E100.26.92", {"start": v(-8.85, -5.47) * mm, "end": v(-8.86, -5.47) * mm});
            skLineSegment(sketch, "E100.26.93", {"start": v(-8.75, -5.57) * mm, "end": v(-8.77, -5.55) * mm});
            skLineSegment(sketch, "E100.26.94", {"start": v(-8.69, -5.67) * mm, "end": v(-8.68, -5.69) * mm});
            skLineSegment(sketch, "E100.26.95", {"start": v(-8.66, -5.79) * mm, "end": v(-8.66, -5.8) * mm});
            skLineSegment(sketch, "E100.26.96", {"start": v(-8.8, -5.5) * mm, "end": v(-8.8, -5.5) * mm});
            skLineSegment(sketch, "E100.26.97", {"start": v(-8.66, -5.78) * mm, "end": v(-8.66, -5.79) * mm});
            skLineSegment(sketch, "E100.26.98", {"start": v(-8.66, -5.8) * mm, "end": v(-8.67, -5.8) * mm});
            skLineSegment(sketch, "E100.26.99", {"start": v(-8.67, -5.8) * mm, "end": v(-8.67, -5.82) * mm});
            skLineSegment(sketch, "E100.27.0", {"start": v(-9.11, -7.01) * mm, "end": v(-9.14, -6.98) * mm});
            skLineSegment(sketch, "E100.27.1", {"start": v(-8.21, -8.05) * mm, "end": v(-8.19, -8.08) * mm});
            skLineSegment(sketch, "E100.27.2", {"start": v(-8.21, -7.85) * mm, "end": v(-8.23, -7.9) * mm});
            skLineSegment(sketch, "E100.27.3", {"start": v(-8.16, -8.1) * mm, "end": v(-8.13, -8.13) * mm});
            skLineSegment(sketch, "E100.27.4", {"start": v(-8.65, -6.93) * mm, "end": v(-8.7, -6.94) * mm});
            skLineSegment(sketch, "E100.27.5", {"start": v(-9.16, -6.95) * mm, "end": v(-9.18, -6.92) * mm});
            skLineSegment(sketch, "E100.27.6", {"start": v(-8.24, -8.02) * mm, "end": v(-8.21, -8.05) * mm});
            skLineSegment(sketch, "E100.27.7", {"start": v(-8.89, -7) * mm, "end": v(-8.94, -7.01) * mm});
            skLineSegment(sketch, "E100.27.8", {"start": v(-8.19, -8.08) * mm, "end": v(-8.16, -8.1) * mm});
            skLineSegment(sketch, "E100.27.9", {"start": v(-8.94, -7.01) * mm, "end": v(-8.99, -7.02) * mm});
            skLineSegment(sketch, "E100.27.10", {"start": v(-9.18, -6.92) * mm, "end": v(-9.2, -6.9) * mm});
            skLineSegment(sketch, "E100.27.11", {"start": v(-8.99, -7.02) * mm, "end": v(-9.04, -7.03) * mm});
            skLineSegment(sketch, "E100.27.12", {"start": v(-8.84, -6.99) * mm, "end": v(-8.89, -7) * mm});
            skLineSegment(sketch, "E100.27.13", {"start": v(-8.25, -7.95) * mm, "end": v(-8.27, -8) * mm});
            skLineSegment(sketch, "E100.27.14", {"start": v(-9.09, -7.04) * mm, "end": v(-9.11, -7.01) * mm});
            skLineSegment(sketch, "E100.27.15", {"start": v(-8.7, -6.94) * mm, "end": v(-8.74, -6.96) * mm});
            skLineSegment(sketch, "E100.27.16", {"start": v(-9.14, -6.98) * mm, "end": v(-9.16, -6.95) * mm});
            skLineSegment(sketch, "E100.27.17", {"start": v(-8.27, -8) * mm, "end": v(-8.24, -8.02) * mm});
            skLineSegment(sketch, "E100.27.18", {"start": v(-8.17, -7.76) * mm, "end": v(-8.2, -7.8) * mm});
            skLineSegment(sketch, "E100.27.19", {"start": v(-8.8, -6.97) * mm, "end": v(-8.84, -6.99) * mm});
            skLineSegment(sketch, "E100.27.20", {"start": v(-9.04, -7.03) * mm, "end": v(-9.09, -7.04) * mm});
            skLineSegment(sketch, "E100.27.21", {"start": v(-8.11, -7.62) * mm, "end": v(-8.13, -7.66) * mm});
            skLineSegment(sketch, "E100.27.22", {"start": v(-8.2, -7.8) * mm, "end": v(-8.21, -7.85) * mm});
            skLineSegment(sketch, "E100.27.23", {"start": v(-8.74, -6.96) * mm, "end": v(-8.8, -6.97) * mm});
            skLineSegment(sketch, "E100.27.24", {"start": v(-8.13, -7.66) * mm, "end": v(-8.15, -7.71) * mm});
            skLineSegment(sketch, "E100.27.25", {"start": v(-8.15, -7.71) * mm, "end": v(-8.17, -7.76) * mm});
            skLineSegment(sketch, "E100.27.26", {"start": v(-8.23, -7.9) * mm, "end": v(-8.25, -7.95) * mm});
            skLineSegment(sketch, "E100.27.27", {"start": v(-8.09, -7.57) * mm, "end": v(-8.11, -7.62) * mm});
            skLineSegment(sketch, "E100.27.28", {"start": v(-7.76, -7) * mm, "end": v(-7.76, -7) * mm});
            skLineSegment(sketch, "E100.27.29", {"start": v(-7.9, -7.23) * mm, "end": v(-7.93, -7.27) * mm});
            skLineSegment(sketch, "E100.27.30", {"start": v(-7.97, -7.35) * mm, "end": v(-8, -7.4) * mm});
            skLineSegment(sketch, "E100.27.31", {"start": v(-8.06, -6.69) * mm, "end": v(-8.07, -6.7) * mm});
            skLineSegment(sketch, "E100.27.32", {"start": v(-8.6, -6.91) * mm, "end": v(-8.65, -6.93) * mm});
            skLineSegment(sketch, "E100.27.33", {"start": v(-7.75, -6.94) * mm, "end": v(-7.75, -6.95) * mm});
            skLineSegment(sketch, "E100.27.34", {"start": v(-7.97, -6.68) * mm, "end": v(-7.98, -6.68) * mm});
            skLineSegment(sketch, "E100.27.35", {"start": v(-7.77, -7.02) * mm, "end": v(-7.77, -7.04) * mm});
            skLineSegment(sketch, "E100.27.36", {"start": v(-7.82, -7.11) * mm, "end": v(-7.85, -7.15) * mm});
            skLineSegment(sketch, "E100.27.37", {"start": v(-8.5, -6.88) * mm, "end": v(-8.55, -6.9) * mm});
            skLineSegment(sketch, "E100.27.38", {"start": v(-8.24, -6.77) * mm, "end": v(-8.28, -6.8) * mm});
            skLineSegment(sketch, "E100.27.39", {"start": v(-8.37, -6.83) * mm, "end": v(-8.41, -6.85) * mm});
            skLineSegment(sketch, "E100.27.40", {"start": v(-7.84, -6.8) * mm, "end": v(-7.86, -6.78) * mm});
            skLineSegment(sketch, "E100.27.41", {"start": v(-7.86, -6.78) * mm, "end": v(-7.87, -6.76) * mm});
            skLineSegment(sketch, "E100.27.42", {"start": v(-8.02, -7.44) * mm, "end": v(-8.05, -7.48) * mm});
            skLineSegment(sketch, "E100.27.43", {"start": v(-8, -7.4) * mm, "end": v(-8.02, -7.44) * mm});
            skLineSegment(sketch, "E100.27.44", {"start": v(-8.55, -6.9) * mm, "end": v(-8.6, -6.91) * mm});
            skLineSegment(sketch, "E100.27.45", {"start": v(-8, -6.68) * mm, "end": v(-8.02, -6.68) * mm});
            skLineSegment(sketch, "E100.27.46", {"start": v(-7.92, -6.7) * mm, "end": v(-7.93, -6.7) * mm});
            skLineSegment(sketch, "E100.27.47", {"start": v(-8.41, -6.85) * mm, "end": v(-8.46, -6.86) * mm});
            skLineSegment(sketch, "E100.27.48", {"start": v(-8.07, -7.53) * mm, "end": v(-8.09, -7.57) * mm});
            skLineSegment(sketch, "E100.27.49", {"start": v(-7.78, -7.05) * mm, "end": v(-7.79, -7.06) * mm});
            skLineSegment(sketch, "E100.27.50", {"start": v(-8.46, -6.86) * mm, "end": v(-8.5, -6.88) * mm});
            skLineSegment(sketch, "E100.27.51", {"start": v(-8.2, -6.75) * mm, "end": v(-8.24, -6.77) * mm});
            skLineSegment(sketch, "E100.27.52", {"start": v(-7.75, -6.93) * mm, "end": v(-7.75, -6.94) * mm});
            skLineSegment(sketch, "E100.27.53", {"start": v(-7.95, -7.31) * mm, "end": v(-7.97, -7.35) * mm});
            skLineSegment(sketch, "E100.27.54", {"start": v(-8.09, -6.7) * mm, "end": v(-8.1, -6.7) * mm});
            skLineSegment(sketch, "E100.27.55", {"start": v(-7.9, -6.72) * mm, "end": v(-7.92, -6.7) * mm});
            skLineSegment(sketch, "E100.27.56", {"start": v(-8.04, -6.69) * mm, "end": v(-8.06, -6.69) * mm});
            skLineSegment(sketch, "E100.27.57", {"start": v(-7.75, -6.92) * mm, "end": v(-7.75, -6.93) * mm});
            skLineSegment(sketch, "E100.27.58", {"start": v(-8.12, -6.71) * mm, "end": v(-8.13, -6.72) * mm});
            skLineSegment(sketch, "E100.27.59", {"start": v(-7.79, -7.06) * mm, "end": v(-7.8, -7.08) * mm});
            skLineSegment(sketch, "E100.27.60", {"start": v(-8.28, -6.8) * mm, "end": v(-8.32, -6.81) * mm});
            skLineSegment(sketch, "E100.27.61", {"start": v(-8.05, -7.48) * mm, "end": v(-8.07, -7.53) * mm});
            skLineSegment(sketch, "E100.27.62", {"start": v(-7.93, -7.27) * mm, "end": v(-7.95, -7.31) * mm});
            skLineSegment(sketch, "E100.27.63", {"start": v(-7.8, -7.1) * mm, "end": v(-7.82, -7.11) * mm});
            skLineSegment(sketch, "E100.27.64", {"start": v(-7.75, -6.91) * mm, "end": v(-7.75, -6.92) * mm});
            skLineSegment(sketch, "E100.27.65", {"start": v(-7.89, -6.74) * mm, "end": v(-7.9, -6.72) * mm});
            skLineSegment(sketch, "E100.27.66", {"start": v(-8.1, -6.7) * mm, "end": v(-8.12, -6.71) * mm});
            skLineSegment(sketch, "E100.27.67", {"start": v(-8.32, -6.81) * mm, "end": v(-8.37, -6.83) * mm});
            skLineSegment(sketch, "E100.27.68", {"start": v(-8.03, -6.68) * mm, "end": v(-8.04, -6.69) * mm});
            skLineSegment(sketch, "E100.27.69", {"start": v(-7.87, -7.19) * mm, "end": v(-7.9, -7.23) * mm});
            skLineSegment(sketch, "E100.27.70", {"start": v(-7.94, -6.7) * mm, "end": v(-7.94, -6.69) * mm});
            skLineSegment(sketch, "E100.27.71", {"start": v(-8.07, -6.7) * mm, "end": v(-8.09, -6.7) * mm});
            skLineSegment(sketch, "E100.27.72", {"start": v(-7.95, -6.68) * mm, "end": v(-7.96, -6.68) * mm});
            skLineSegment(sketch, "E100.27.73", {"start": v(-7.85, -7.15) * mm, "end": v(-7.87, -7.19) * mm});
            skLineSegment(sketch, "E100.27.74", {"start": v(-7.75, -6.9) * mm, "end": v(-7.75, -6.91) * mm});
            skLineSegment(sketch, "E100.27.75", {"start": v(-7.75, -6.9) * mm, "end": v(-7.75, -6.9) * mm});
            skLineSegment(sketch, "E100.27.76", {"start": v(-7.81, -6.83) * mm, "end": v(-7.8, -6.85) * mm});
            skLineSegment(sketch, "E100.27.77", {"start": v(-8.02, -6.68) * mm, "end": v(-8.03, -6.68) * mm});
            skLineSegment(sketch, "E100.27.78", {"start": v(-7.76, -7) * mm, "end": v(-7.77, -7.02) * mm});
            skLineSegment(sketch, "E100.27.79", {"start": v(-8.15, -6.73) * mm, "end": v(-8.2, -6.75) * mm});
            skLineSegment(sketch, "E100.27.80", {"start": v(-7.96, -6.68) * mm, "end": v(-7.97, -6.68) * mm});
            skLineSegment(sketch, "E100.27.81", {"start": v(-7.76, -6.89) * mm, "end": v(-7.75, -6.9) * mm});
            skLineSegment(sketch, "E100.27.82", {"start": v(-8.13, -6.72) * mm, "end": v(-8.15, -6.73) * mm});
            skLineSegment(sketch, "E100.27.83", {"start": v(-7.83, -6.81) * mm, "end": v(-7.81, -6.83) * mm});
            skLineSegment(sketch, "E100.27.84", {"start": v(-7.77, -7.04) * mm, "end": v(-7.78, -7.05) * mm});
            skLineSegment(sketch, "E100.27.85", {"start": v(-8, -6.68) * mm, "end": v(-8, -6.68) * mm});
            skLineSegment(sketch, "E100.27.86", {"start": v(-7.84, -6.8) * mm, "end": v(-7.83, -6.81) * mm});
            skLineSegment(sketch, "E100.27.87", {"start": v(-7.8, -7.08) * mm, "end": v(-7.8, -7.1) * mm});
            skLineSegment(sketch, "E100.27.88", {"start": v(-7.76, -6.88) * mm, "end": v(-7.76, -6.89) * mm});
            skLineSegment(sketch, "E100.27.89", {"start": v(-7.78, -6.86) * mm, "end": v(-7.76, -6.88) * mm});
            skLineSegment(sketch, "E100.27.90", {"start": v(-7.92, -6.7) * mm, "end": v(-7.92, -6.7) * mm});
            skLineSegment(sketch, "E100.27.91", {"start": v(-7.94, -6.69) * mm, "end": v(-7.95, -6.68) * mm});
            skLineSegment(sketch, "E100.27.92", {"start": v(-7.98, -6.68) * mm, "end": v(-8, -6.68) * mm});
            skLineSegment(sketch, "E100.27.93", {"start": v(-7.87, -6.76) * mm, "end": v(-7.89, -6.74) * mm});
            skLineSegment(sketch, "E100.27.94", {"start": v(-7.8, -6.85) * mm, "end": v(-7.78, -6.86) * mm});
            skLineSegment(sketch, "E100.27.95", {"start": v(-7.75, -6.96) * mm, "end": v(-7.75, -6.97) * mm});
            skLineSegment(sketch, "E100.27.96", {"start": v(-7.93, -6.7) * mm, "end": v(-7.94, -6.7) * mm});
            skLineSegment(sketch, "E100.27.97", {"start": v(-7.75, -6.95) * mm, "end": v(-7.75, -6.96) * mm});
            skLineSegment(sketch, "E100.27.98", {"start": v(-7.75, -6.97) * mm, "end": v(-7.75, -6.98) * mm});
            skLineSegment(sketch, "E100.27.99", {"start": v(-7.75, -6.98) * mm, "end": v(-7.76, -7) * mm});
            skLineSegment(sketch, "E100.28.0", {"start": v(-8.02, -8.24) * mm, "end": v(-8.05, -8.21) * mm});
            skLineSegment(sketch, "E100.28.1", {"start": v(-6.98, -9.14) * mm, "end": v(-6.95, -9.16) * mm});
            skLineSegment(sketch, "E100.28.2", {"start": v(-7.01, -8.94) * mm, "end": v(-7.02, -8.99) * mm});
            skLineSegment(sketch, "E100.28.3", {"start": v(-6.92, -9.18) * mm, "end": v(-6.9, -9.2) * mm});
            skLineSegment(sketch, "E100.28.4", {"start": v(-7.57, -8.09) * mm, "end": v(-7.62, -8.11) * mm});
            skLineSegment(sketch, "E100.28.5", {"start": v(-8.08, -8.19) * mm, "end": v(-8.1, -8.16) * mm});
            skLineSegment(sketch, "E100.28.6", {"start": v(-7.01, -9.11) * mm, "end": v(-6.98, -9.14) * mm});
            skLineSegment(sketch, "E100.28.7", {"start": v(-7.8, -8.2) * mm, "end": v(-7.85, -8.21) * mm});
            skLineSegment(sketch, "E100.28.8", {"start": v(-6.95, -9.16) * mm, "end": v(-6.92, -9.18) * mm});
            skLineSegment(sketch, "E100.28.9", {"start": v(-7.85, -8.21) * mm, "end": v(-7.9, -8.23) * mm});
            skLineSegment(sketch, "E100.28.10", {"start": v(-8.1, -8.16) * mm, "end": v(-8.13, -8.13) * mm});
            skLineSegment(sketch, "E100.28.11", {"start": v(-7.9, -8.23) * mm, "end": v(-7.95, -8.25) * mm});
            skLineSegment(sketch, "E100.28.12", {"start": v(-7.76, -8.17) * mm, "end": v(-7.8, -8.2) * mm});
            skLineSegment(sketch, "E100.28.13", {"start": v(-7.03, -9.04) * mm, "end": v(-7.04, -9.09) * mm});
            skLineSegment(sketch, "E100.28.14", {"start": v(-8, -8.27) * mm, "end": v(-8.02, -8.24) * mm});
            skLineSegment(sketch, "E100.28.15", {"start": v(-7.62, -8.11) * mm, "end": v(-7.66, -8.13) * mm});
            skLineSegment(sketch, "E100.28.16", {"start": v(-8.05, -8.21) * mm, "end": v(-8.08, -8.19) * mm});
            skLineSegment(sketch, "E100.28.17", {"start": v(-7.04, -9.09) * mm, "end": v(-7.01, -9.11) * mm});
            skLineSegment(sketch, "E100.28.18", {"start": v(-6.99, -8.84) * mm, "end": v(-7, -8.89) * mm});
            skLineSegment(sketch, "E100.28.19", {"start": v(-7.71, -8.15) * mm, "end": v(-7.76, -8.17) * mm});
            skLineSegment(sketch, "E100.28.20", {"start": v(-7.95, -8.25) * mm, "end": v(-8, -8.27) * mm});
            skLineSegment(sketch, "E100.28.21", {"start": v(-6.94, -8.7) * mm, "end": v(-6.96, -8.74) * mm});
            skLineSegment(sketch, "E100.28.22", {"start": v(-7, -8.89) * mm, "end": v(-7.01, -8.94) * mm});
            skLineSegment(sketch, "E100.28.23", {"start": v(-7.66, -8.13) * mm, "end": v(-7.71, -8.15) * mm});
            skLineSegment(sketch, "E100.28.24", {"start": v(-6.96, -8.74) * mm, "end": v(-6.97, -8.8) * mm});
            skLineSegment(sketch, "E100.28.25", {"start": v(-6.97, -8.8) * mm, "end": v(-6.99, -8.84) * mm});
            skLineSegment(sketch, "E100.28.26", {"start": v(-7.02, -8.99) * mm, "end": v(-7.03, -9.04) * mm});
            skLineSegment(sketch, "E100.28.27", {"start": v(-6.93, -8.65) * mm, "end": v(-6.94, -8.7) * mm});
            skLineSegment(sketch, "E100.28.28", {"start": v(-6.68, -8.03) * mm, "end": v(-6.69, -8.04) * mm});
            skLineSegment(sketch, "E100.28.29", {"start": v(-6.8, -8.28) * mm, "end": v(-6.81, -8.32) * mm});
            skLineSegment(sketch, "E100.28.30", {"start": v(-6.85, -8.41) * mm, "end": v(-6.86, -8.46) * mm});
            skLineSegment(sketch, "E100.28.31", {"start": v(-7.02, -7.77) * mm, "end": v(-7.04, -7.77) * mm});
            skLineSegment(sketch, "E100.28.32", {"start": v(-7.53, -8.07) * mm, "end": v(-7.57, -8.09) * mm});
            skLineSegment(sketch, "E100.28.33", {"start": v(-6.68, -7.97) * mm, "end": v(-6.68, -7.98) * mm});
            skLineSegment(sketch, "E100.28.34", {"start": v(-6.94, -7.75) * mm, "end": v(-6.95, -7.75) * mm});
            skLineSegment(sketch, "E100.28.35", {"start": v(-6.69, -8.06) * mm, "end": v(-6.7, -8.07) * mm});
            skLineSegment(sketch, "E100.28.36", {"start": v(-6.73, -8.15) * mm, "end": v(-6.75, -8.2) * mm});
            skLineSegment(sketch, "E100.28.37", {"start": v(-7.44, -8.02) * mm, "end": v(-7.48, -8.05) * mm});
            skLineSegment(sketch, "E100.28.38", {"start": v(-7.19, -7.87) * mm, "end": v(-7.23, -7.9) * mm});
            skLineSegment(sketch, "E100.28.39", {"start": v(-7.31, -7.95) * mm, "end": v(-7.35, -7.97) * mm});
            skLineSegment(sketch, "E100.28.40", {"start": v(-6.8, -7.84) * mm, "end": v(-6.81, -7.83) * mm});
            skLineSegment(sketch, "E100.28.41", {"start": v(-6.81, -7.83) * mm, "end": v(-6.83, -7.81) * mm});
            skLineSegment(sketch, "E100.28.42", {"start": v(-6.88, -8.5) * mm, "end": v(-6.9, -8.55) * mm});
            skLineSegment(sketch, "E100.28.43", {"start": v(-6.86, -8.46) * mm, "end": v(-6.88, -8.5) * mm});
            skLineSegment(sketch, "E100.28.44", {"start": v(-7.48, -8.05) * mm, "end": v(-7.53, -8.07) * mm});
            skLineSegment(sketch, "E100.28.45", {"start": v(-6.97, -7.75) * mm, "end": v(-6.98, -7.75) * mm});
            skLineSegment(sketch, "E100.28.46", {"start": v(-6.89, -7.76) * mm, "end": v(-6.9, -7.75) * mm});
            skLineSegment(sketch, "E100.28.47", {"start": v(-7.35, -7.97) * mm, "end": v(-7.4, -8) * mm});
            skLineSegment(sketch, "E100.28.48", {"start": v(-6.91, -8.6) * mm, "end": v(-6.93, -8.65) * mm});
            skLineSegment(sketch, "E100.28.49", {"start": v(-6.7, -8.09) * mm, "end": v(-6.7, -8.1) * mm});
            skLineSegment(sketch, "E100.28.50", {"start": v(-7.4, -8) * mm, "end": v(-7.44, -8.02) * mm});
            skLineSegment(sketch, "E100.28.51", {"start": v(-7.15, -7.85) * mm, "end": v(-7.19, -7.87) * mm});
            skLineSegment(sketch, "E100.28.52", {"start": v(-6.68, -7.96) * mm, "end": v(-6.68, -7.97) * mm});
            skLineSegment(sketch, "E100.28.53", {"start": v(-6.83, -8.37) * mm, "end": v(-6.85, -8.41) * mm});
            skLineSegment(sketch, "E100.28.54", {"start": v(-7.05, -7.78) * mm, "end": v(-7.06, -7.79) * mm});
            skLineSegment(sketch, "E100.28.55", {"start": v(-6.86, -7.78) * mm, "end": v(-6.88, -7.76) * mm});
            skLineSegment(sketch, "E100.28.56", {"start": v(-7, -7.76) * mm, "end": v(-7.02, -7.77) * mm});
            skLineSegment(sketch, "E100.28.57", {"start": v(-6.68, -7.95) * mm, "end": v(-6.68, -7.96) * mm});
            skLineSegment(sketch, "E100.28.58", {"start": v(-7.08, -7.8) * mm, "end": v(-7.1, -7.8) * mm});
            skLineSegment(sketch, "E100.28.59", {"start": v(-6.7, -8.1) * mm, "end": v(-6.71, -8.12) * mm});
            skLineSegment(sketch, "E100.28.60", {"start": v(-7.23, -7.9) * mm, "end": v(-7.27, -7.93) * mm});
            skLineSegment(sketch, "E100.28.61", {"start": v(-6.9, -8.55) * mm, "end": v(-6.91, -8.6) * mm});
            skLineSegment(sketch, "E100.28.62", {"start": v(-6.81, -8.32) * mm, "end": v(-6.83, -8.37) * mm});
            skLineSegment(sketch, "E100.28.63", {"start": v(-6.72, -8.13) * mm, "end": v(-6.73, -8.15) * mm});
            skLineSegment(sketch, "E100.28.64", {"start": v(-6.69, -7.94) * mm, "end": v(-6.68, -7.95) * mm});
            skLineSegment(sketch, "E100.28.65", {"start": v(-6.85, -7.8) * mm, "end": v(-6.86, -7.78) * mm});
            skLineSegment(sketch, "E100.28.66", {"start": v(-7.06, -7.79) * mm, "end": v(-7.08, -7.8) * mm});
            skLineSegment(sketch, "E100.28.67", {"start": v(-7.27, -7.93) * mm, "end": v(-7.31, -7.95) * mm});
            skLineSegment(sketch, "E100.28.68", {"start": v(-7, -7.76) * mm, "end": v(-7, -7.76) * mm});
            skLineSegment(sketch, "E100.28.69", {"start": v(-6.77, -8.24) * mm, "end": v(-6.8, -8.28) * mm});
            skLineSegment(sketch, "E100.28.70", {"start": v(-6.9, -7.75) * mm, "end": v(-6.91, -7.75) * mm});
            skLineSegment(sketch, "E100.28.71", {"start": v(-7.04, -7.77) * mm, "end": v(-7.05, -7.78) * mm});
            skLineSegment(sketch, "E100.28.72", {"start": v(-6.92, -7.75) * mm, "end": v(-6.93, -7.75) * mm});
            skLineSegment(sketch, "E100.28.73", {"start": v(-6.75, -8.2) * mm, "end": v(-6.77, -8.24) * mm});
            skLineSegment(sketch, "E100.28.74", {"start": v(-6.7, -7.94) * mm, "end": v(-6.69, -7.94) * mm});
            skLineSegment(sketch, "E100.28.75", {"start": v(-6.7, -7.93) * mm, "end": v(-6.7, -7.94) * mm});
            skLineSegment(sketch, "E100.28.76", {"start": v(-6.76, -7.87) * mm, "end": v(-6.74, -7.89) * mm});
            skLineSegment(sketch, "E100.28.77", {"start": v(-6.98, -7.75) * mm, "end": v(-7, -7.76) * mm});
            skLineSegment(sketch, "E100.28.78", {"start": v(-6.69, -8.04) * mm, "end": v(-6.69, -8.06) * mm});
            skLineSegment(sketch, "E100.28.79", {"start": v(-7.11, -7.82) * mm, "end": v(-7.15, -7.85) * mm});
            skLineSegment(sketch, "E100.28.80", {"start": v(-6.93, -7.75) * mm, "end": v(-6.94, -7.75) * mm});
            skLineSegment(sketch, "E100.28.81", {"start": v(-6.7, -7.92) * mm, "end": v(-6.7, -7.93) * mm});
            skLineSegment(sketch, "E100.28.82", {"start": v(-7.1, -7.8) * mm, "end": v(-7.11, -7.82) * mm});
            skLineSegment(sketch, "E100.28.83", {"start": v(-6.78, -7.86) * mm, "end": v(-6.76, -7.87) * mm});
            skLineSegment(sketch, "E100.28.84", {"start": v(-6.7, -8.07) * mm, "end": v(-6.7, -8.09) * mm});
            skLineSegment(sketch, "E100.28.85", {"start": v(-6.96, -7.75) * mm, "end": v(-6.97, -7.75) * mm});
            skLineSegment(sketch, "E100.28.86", {"start": v(-6.8, -7.84) * mm, "end": v(-6.78, -7.86) * mm});
            skLineSegment(sketch, "E100.28.87", {"start": v(-6.71, -8.12) * mm, "end": v(-6.72, -8.13) * mm});
            skLineSegment(sketch, "E100.28.88", {"start": v(-6.7, -7.92) * mm, "end": v(-6.7, -7.92) * mm});
            skLineSegment(sketch, "E100.28.89", {"start": v(-6.72, -7.9) * mm, "end": v(-6.7, -7.92) * mm});
            skLineSegment(sketch, "E100.28.90", {"start": v(-6.88, -7.76) * mm, "end": v(-6.89, -7.76) * mm});
            skLineSegment(sketch, "E100.28.91", {"start": v(-6.91, -7.75) * mm, "end": v(-6.92, -7.75) * mm});
            skLineSegment(sketch, "E100.28.92", {"start": v(-6.95, -7.75) * mm, "end": v(-6.96, -7.75) * mm});
            skLineSegment(sketch, "E100.28.93", {"start": v(-6.83, -7.81) * mm, "end": v(-6.85, -7.8) * mm});
            skLineSegment(sketch, "E100.28.94", {"start": v(-6.74, -7.89) * mm, "end": v(-6.72, -7.9) * mm});
            skLineSegment(sketch, "E100.28.95", {"start": v(-6.68, -8) * mm, "end": v(-6.68, -8) * mm});
            skLineSegment(sketch, "E100.28.96", {"start": v(-6.9, -7.75) * mm, "end": v(-6.9, -7.75) * mm});
            skLineSegment(sketch, "E100.28.97", {"start": v(-6.68, -7.98) * mm, "end": v(-6.68, -8) * mm});
            skLineSegment(sketch, "E100.28.98", {"start": v(-6.68, -8) * mm, "end": v(-6.68, -8.02) * mm});
            skLineSegment(sketch, "E100.28.99", {"start": v(-6.68, -8.02) * mm, "end": v(-6.68, -8.03) * mm});
            skLineSegment(sketch, "E100.29.0", {"start": v(-6.77, -9.3) * mm, "end": v(-6.8, -9.27) * mm});
            skLineSegment(sketch, "E100.29.1", {"start": v(-5.61, -10.04) * mm, "end": v(-5.58, -10.06) * mm});
            skLineSegment(sketch, "E100.29.2", {"start": v(-5.67, -9.85) * mm, "end": v(-5.67, -9.9) * mm});
            skLineSegment(sketch, "E100.29.3", {"start": v(-5.55, -10.07) * mm, "end": v(-5.51, -10.1) * mm});
            skLineSegment(sketch, "E100.29.4", {"start": v(-6.34, -9.08) * mm, "end": v(-6.39, -9.11) * mm});
            skLineSegment(sketch, "E100.29.5", {"start": v(-6.83, -9.25) * mm, "end": v(-6.86, -9.23) * mm});
            skLineSegment(sketch, "E100.29.6", {"start": v(-5.65, -10.02) * mm, "end": v(-5.61, -10.04) * mm});
            skLineSegment(sketch, "E100.29.7", {"start": v(-6.56, -9.22) * mm, "end": v(-6.6, -9.24) * mm});
            skLineSegment(sketch, "E100.29.8", {"start": v(-5.58, -10.06) * mm, "end": v(-5.55, -10.07) * mm});
            skLineSegment(sketch, "E100.29.9", {"start": v(-6.6, -9.24) * mm, "end": v(-6.65, -9.27) * mm});
            skLineSegment(sketch, "E100.29.10", {"start": v(-6.86, -9.23) * mm, "end": v(-6.9, -9.2) * mm});
            skLineSegment(sketch, "E100.29.11", {"start": v(-6.65, -9.27) * mm, "end": v(-6.7, -9.3) * mm});
            skLineSegment(sketch, "E100.29.12", {"start": v(-6.51, -9.2) * mm, "end": v(-6.56, -9.22) * mm});
            skLineSegment(sketch, "E100.29.13", {"start": v(-5.68, -9.95) * mm, "end": v(-5.68, -10) * mm});
            skLineSegment(sketch, "E100.29.14", {"start": v(-6.74, -9.32) * mm, "end": v(-6.77, -9.3) * mm});
            skLineSegment(sketch, "E100.29.15", {"start": v(-6.39, -9.11) * mm, "end": v(-6.43, -9.14) * mm});
            skLineSegment(sketch, "E100.29.16", {"start": v(-6.8, -9.27) * mm, "end": v(-6.83, -9.25) * mm});
            skLineSegment(sketch, "E100.29.17", {"start": v(-5.68, -10) * mm, "end": v(-5.65, -10.02) * mm});
            skLineSegment(sketch, "E100.29.18", {"start": v(-5.66, -9.74) * mm, "end": v(-5.66, -9.8) * mm});
            skLineSegment(sketch, "E100.29.19", {"start": v(-6.47, -9.17) * mm, "end": v(-6.51, -9.2) * mm});
            skLineSegment(sketch, "E100.29.20", {"start": v(-6.7, -9.3) * mm, "end": v(-6.74, -9.32) * mm});
            skLineSegment(sketch, "E100.29.21", {"start": v(-5.64, -9.6) * mm, "end": v(-5.64, -9.64) * mm});
            skLineSegment(sketch, "E100.29.22", {"start": v(-5.66, -9.8) * mm, "end": v(-5.67, -9.85) * mm});
            skLineSegment(sketch, "E100.29.23", {"start": v(-6.43, -9.14) * mm, "end": v(-6.47, -9.17) * mm});
            skLineSegment(sketch, "E100.29.24", {"start": v(-5.64, -9.64) * mm, "end": v(-5.65, -9.7) * mm});
            skLineSegment(sketch, "E100.29.25", {"start": v(-5.65, -9.7) * mm, "end": v(-5.66, -9.74) * mm});
            skLineSegment(sketch, "E100.29.26", {"start": v(-5.67, -9.9) * mm, "end": v(-5.68, -9.95) * mm});
            skLineSegment(sketch, "E100.29.27", {"start": v(-5.63, -9.55) * mm, "end": v(-5.64, -9.6) * mm});
            skLineSegment(sketch, "E100.29.28", {"start": v(-5.47, -8.9) * mm, "end": v(-5.47, -8.91) * mm});
            skLineSegment(sketch, "E100.29.29", {"start": v(-5.54, -9.16) * mm, "end": v(-5.56, -9.2) * mm});
            skLineSegment(sketch, "E100.29.30", {"start": v(-5.58, -9.3) * mm, "end": v(-5.6, -9.35) * mm});
            skLineSegment(sketch, "E100.29.31", {"start": v(-5.84, -8.69) * mm, "end": v(-5.86, -8.7) * mm});
            skLineSegment(sketch, "E100.29.32", {"start": v(-6.3, -9.06) * mm, "end": v(-6.34, -9.08) * mm});
            skLineSegment(sketch, "E100.29.33", {"start": v(-5.48, -8.84) * mm, "end": v(-5.47, -8.85) * mm});
            skLineSegment(sketch, "E100.29.34", {"start": v(-5.77, -8.65) * mm, "end": v(-5.78, -8.66) * mm});
            skLineSegment(sketch, "E100.29.35", {"start": v(-5.47, -8.93) * mm, "end": v(-5.48, -8.94) * mm});
            skLineSegment(sketch, "E100.29.36", {"start": v(-5.5, -9.03) * mm, "end": v(-5.51, -9.07) * mm});
            skLineSegment(sketch, "E100.29.37", {"start": v(-6.22, -9) * mm, "end": v(-6.26, -9.03) * mm});
            skLineSegment(sketch, "E100.29.38", {"start": v(-6, -8.82) * mm, "end": v(-6.03, -8.85) * mm});
            skLineSegment(sketch, "E100.29.39", {"start": v(-6.1, -8.91) * mm, "end": v(-6.14, -8.94) * mm});
            skLineSegment(sketch, "E100.29.40", {"start": v(-5.6, -8.73) * mm, "end": v(-5.63, -8.72) * mm});
            skLineSegment(sketch, "E100.29.41", {"start": v(-5.63, -8.72) * mm, "end": v(-5.65, -8.7) * mm});
            skLineSegment(sketch, "E100.29.42", {"start": v(-5.6, -9.4) * mm, "end": v(-5.61, -9.45) * mm});
            skLineSegment(sketch, "E100.29.43", {"start": v(-5.6, -9.35) * mm, "end": v(-5.6, -9.4) * mm});
            skLineSegment(sketch, "E100.29.44", {"start": v(-6.26, -9.03) * mm, "end": v(-6.3, -9.06) * mm});
            skLineSegment(sketch, "E100.29.45", {"start": v(-5.8, -8.66) * mm, "end": v(-5.8, -8.67) * mm});
            skLineSegment(sketch, "E100.29.46", {"start": v(-5.71, -8.66) * mm, "end": v(-5.72, -8.66) * mm});
            skLineSegment(sketch, "E100.29.47", {"start": v(-6.14, -8.94) * mm, "end": v(-6.18, -8.97) * mm});
            skLineSegment(sketch, "E100.29.48", {"start": v(-5.62, -9.5) * mm, "end": v(-5.63, -9.55) * mm});
            skLineSegment(sketch, "E100.29.49", {"start": v(-5.48, -8.96) * mm, "end": v(-5.48, -8.97) * mm});
            skLineSegment(sketch, "E100.29.50", {"start": v(-6.18, -8.97) * mm, "end": v(-6.22, -9) * mm});
            skLineSegment(sketch, "E100.29.51", {"start": v(-5.96, -8.78) * mm, "end": v(-6, -8.82) * mm});
            skLineSegment(sketch, "E100.29.52", {"start": v(-5.48, -8.83) * mm, "end": v(-5.48, -8.84) * mm});
            skLineSegment(sketch, "E100.29.53", {"start": v(-5.57, -9.26) * mm, "end": v(-5.58, -9.3) * mm});
            skLineSegment(sketch, "E100.29.54", {"start": v(-5.87, -8.7) * mm, "end": v(-5.88, -8.72) * mm});
            skLineSegment(sketch, "E100.29.55", {"start": v(-5.69, -8.68) * mm, "end": v(-5.7, -8.66) * mm});
            skLineSegment(sketch, "E100.29.56", {"start": v(-5.83, -8.68) * mm, "end": v(-5.84, -8.69) * mm});
            skLineSegment(sketch, "E100.29.57", {"start": v(-5.48, -8.82) * mm, "end": v(-5.48, -8.83) * mm});
            skLineSegment(sketch, "E100.29.58", {"start": v(-5.9, -8.73) * mm, "end": v(-5.91, -8.74) * mm});
            skLineSegment(sketch, "E100.29.59", {"start": v(-5.48, -8.97) * mm, "end": v(-5.49, -8.99) * mm});
            skLineSegment(sketch, "E100.29.60", {"start": v(-6.03, -8.85) * mm, "end": v(-6.07, -8.88) * mm});
            skLineSegment(sketch, "E100.29.61", {"start": v(-5.61, -9.45) * mm, "end": v(-5.62, -9.5) * mm});
            skLineSegment(sketch, "E100.29.62", {"start": v(-5.56, -9.2) * mm, "end": v(-5.57, -9.26) * mm});
            skLineSegment(sketch, "E100.29.63", {"start": v(-5.5, -9) * mm, "end": v(-5.5, -9.03) * mm});
            skLineSegment(sketch, "E100.29.64", {"start": v(-5.49, -8.81) * mm, "end": v(-5.48, -8.82) * mm});
            skLineSegment(sketch, "E100.29.65", {"start": v(-5.67, -8.69) * mm, "end": v(-5.69, -8.68) * mm});
            skLineSegment(sketch, "E100.29.66", {"start": v(-5.88, -8.72) * mm, "end": v(-5.9, -8.73) * mm});
            skLineSegment(sketch, "E100.29.67", {"start": v(-6.07, -8.88) * mm, "end": v(-6.1, -8.91) * mm});
            skLineSegment(sketch, "E100.29.68", {"start": v(-5.82, -8.67) * mm, "end": v(-5.83, -8.68) * mm});
            skLineSegment(sketch, "E100.29.69", {"start": v(-5.53, -9.12) * mm, "end": v(-5.54, -9.16) * mm});
            skLineSegment(sketch, "E100.29.70", {"start": v(-5.73, -8.65) * mm, "end": v(-5.74, -8.65) * mm});
            skLineSegment(sketch, "E100.29.71", {"start": v(-5.86, -8.7) * mm, "end": v(-5.87, -8.7) * mm});
            skLineSegment(sketch, "E100.29.72", {"start": v(-5.75, -8.65) * mm, "end": v(-5.76, -8.65) * mm});
            skLineSegment(sketch, "E100.29.73", {"start": v(-5.51, -9.07) * mm, "end": v(-5.53, -9.12) * mm});
            skLineSegment(sketch, "E100.29.74", {"start": v(-5.5, -8.8) * mm, "end": v(-5.49, -8.81) * mm});
            skLineSegment(sketch, "E100.29.75", {"start": v(-5.5, -8.8) * mm, "end": v(-5.5, -8.8) * mm});
            skLineSegment(sketch, "E100.29.76", {"start": v(-5.57, -8.75) * mm, "end": v(-5.55, -8.77) * mm});
            skLineSegment(sketch, "E100.29.77", {"start": v(-5.8, -8.67) * mm, "end": v(-5.82, -8.67) * mm});
            skLineSegment(sketch, "E100.29.78", {"start": v(-5.47, -8.91) * mm, "end": v(-5.47, -8.93) * mm});
            skLineSegment(sketch, "E100.29.79", {"start": v(-5.93, -8.75) * mm, "end": v(-5.96, -8.78) * mm});
            skLineSegment(sketch, "E100.29.80", {"start": v(-5.76, -8.65) * mm, "end": v(-5.77, -8.65) * mm});
            skLineSegment(sketch, "E100.29.81", {"start": v(-5.5, -8.8) * mm, "end": v(-5.5, -8.8) * mm});
            skLineSegment(sketch, "E100.29.82", {"start": v(-5.91, -8.74) * mm, "end": v(-5.93, -8.75) * mm});
            skLineSegment(sketch, "E100.29.83", {"start": v(-5.59, -8.74) * mm, "end": v(-5.57, -8.75) * mm});
            skLineSegment(sketch, "E100.29.84", {"start": v(-5.48, -8.94) * mm, "end": v(-5.48, -8.96) * mm});
            skLineSegment(sketch, "E100.29.85", {"start": v(-5.79, -8.66) * mm, "end": v(-5.8, -8.66) * mm});
            skLineSegment(sketch, "E100.29.86", {"start": v(-5.6, -8.73) * mm, "end": v(-5.59, -8.74) * mm});
            skLineSegment(sketch, "E100.29.87", {"start": v(-5.49, -8.99) * mm, "end": v(-5.5, -9) * mm});
            skLineSegment(sketch, "E100.29.88", {"start": v(-5.51, -8.8) * mm, "end": v(-5.5, -8.8) * mm});
            skLineSegment(sketch, "E100.29.89", {"start": v(-5.53, -8.78) * mm, "end": v(-5.51, -8.8) * mm});
            skLineSegment(sketch, "E100.29.90", {"start": v(-5.7, -8.66) * mm, "end": v(-5.71, -8.66) * mm});
            skLineSegment(sketch, "E100.29.91", {"start": v(-5.74, -8.65) * mm, "end": v(-5.75, -8.65) * mm});
            skLineSegment(sketch, "E100.29.92", {"start": v(-5.78, -8.66) * mm, "end": v(-5.79, -8.66) * mm});
            skLineSegment(sketch, "E100.29.93", {"start": v(-5.65, -8.7) * mm, "end": v(-5.67, -8.69) * mm});
            skLineSegment(sketch, "E100.29.94", {"start": v(-5.55, -8.77) * mm, "end": v(-5.53, -8.78) * mm});
            skLineSegment(sketch, "E100.29.95", {"start": v(-5.47, -8.86) * mm, "end": v(-5.47, -8.87) * mm});
            skLineSegment(sketch, "E100.29.96", {"start": v(-5.72, -8.66) * mm, "end": v(-5.73, -8.65) * mm});
            skLineSegment(sketch, "E100.29.97", {"start": v(-5.47, -8.85) * mm, "end": v(-5.47, -8.86) * mm});
            skLineSegment(sketch, "E100.29.98", {"start": v(-5.47, -8.87) * mm, "end": v(-5.47, -8.88) * mm});
            skLineSegment(sketch, "E100.29.99", {"start": v(-5.47, -8.88) * mm, "end": v(-5.47, -8.9) * mm});
            skLineSegment(sketch, "E100.30.0", {"start": v(-5.38, -10.17) * mm, "end": v(-5.41, -10.15) * mm});
            skLineSegment(sketch, "E100.30.1", {"start": v(-4.13, -10.73) * mm, "end": v(-4.1, -10.75) * mm});
            skLineSegment(sketch, "E100.30.2", {"start": v(-4.2, -10.55) * mm, "end": v(-4.2, -10.6) * mm});
            skLineSegment(sketch, "E100.30.3", {"start": v(-4.05, -10.76) * mm, "end": v(-4.02, -10.77) * mm});
            skLineSegment(sketch, "E100.30.4", {"start": v(-4.99, -9.9) * mm, "end": v(-5.02, -9.93) * mm});
            skLineSegment(sketch, "E100.30.5", {"start": v(-5.44, -10.13) * mm, "end": v(-5.48, -10.11) * mm});
            skLineSegment(sketch, "E100.30.6", {"start": v(-4.16, -10.72) * mm, "end": v(-4.13, -10.73) * mm});
            skLineSegment(sketch, "E100.30.7", {"start": v(-5.18, -10.06) * mm, "end": v(-5.22, -10.1) * mm});
            skLineSegment(sketch, "E100.30.8", {"start": v(-4.1, -10.75) * mm, "end": v(-4.05, -10.76) * mm});
            skLineSegment(sketch, "E100.30.9", {"start": v(-5.22, -10.1) * mm, "end": v(-5.26, -10.12) * mm});
            skLineSegment(sketch, "E100.30.10", {"start": v(-5.48, -10.11) * mm, "end": v(-5.51, -10.1) * mm});
            skLineSegment(sketch, "E100.30.11", {"start": v(-5.26, -10.12) * mm, "end": v(-5.3, -10.15) * mm});
            skLineSegment(sketch, "E100.30.12", {"start": v(-5.14, -10.03) * mm, "end": v(-5.18, -10.06) * mm});
            skLineSegment(sketch, "E100.30.13", {"start": v(-4.2, -10.65) * mm, "end": v(-4.2, -10.7) * mm});
            skLineSegment(sketch, "E100.30.14", {"start": v(-5.34, -10.18) * mm, "end": v(-5.38, -10.17) * mm});
            skLineSegment(sketch, "E100.30.15", {"start": v(-5.02, -9.93) * mm, "end": v(-5.06, -9.96) * mm});
            skLineSegment(sketch, "E100.30.16", {"start": v(-5.41, -10.15) * mm, "end": v(-5.44, -10.13) * mm});
            skLineSegment(sketch, "E100.30.17", {"start": v(-4.2, -10.7) * mm, "end": v(-4.16, -10.72) * mm});
            skLineSegment(sketch, "E100.30.18", {"start": v(-4.21, -10.45) * mm, "end": v(-4.21, -10.5) * mm});
            skLineSegment(sketch, "E100.30.19", {"start": v(-5.1, -10) * mm, "end": v(-5.14, -10.03) * mm});
            skLineSegment(sketch, "E100.30.20", {"start": v(-5.3, -10.15) * mm, "end": v(-5.34, -10.18) * mm});
            skLineSegment(sketch, "E100.30.21", {"start": v(-4.21, -10.3) * mm, "end": v(-4.21, -10.35) * mm});
            skLineSegment(sketch, "E100.30.22", {"start": v(-4.21, -10.5) * mm, "end": v(-4.2, -10.55) * mm});
            skLineSegment(sketch, "E100.30.23", {"start": v(-5.06, -9.96) * mm, "end": v(-5.1, -10) * mm});
            skLineSegment(sketch, "E100.30.24", {"start": v(-4.21, -10.35) * mm, "end": v(-4.21, -10.4) * mm});
            skLineSegment(sketch, "E100.30.25", {"start": v(-4.21, -10.4) * mm, "end": v(-4.21, -10.45) * mm});
            skLineSegment(sketch, "E100.30.26", {"start": v(-4.2, -10.6) * mm, "end": v(-4.2, -10.65) * mm});
            skLineSegment(sketch, "E100.30.27", {"start": v(-4.21, -10.25) * mm, "end": v(-4.21, -10.3) * mm});
            skLineSegment(sketch, "E100.30.28", {"start": v(-4.15, -9.59) * mm, "end": v(-4.15, -9.6) * mm});
            skLineSegment(sketch, "E100.30.29", {"start": v(-4.18, -9.86) * mm, "end": v(-4.19, -9.9) * mm});
            skLineSegment(sketch, "E100.30.30", {"start": v(-4.2, -10) * mm, "end": v(-4.2, -10.05) * mm});
            skLineSegment(sketch, "E100.30.31", {"start": v(-4.55, -9.43) * mm, "end": v(-4.56, -9.44) * mm});
            skLineSegment(sketch, "E100.30.32", {"start": v(-4.95, -9.86) * mm, "end": v(-4.99, -9.9) * mm});
            skLineSegment(sketch, "E100.30.33", {"start": v(-4.16, -9.53) * mm, "end": v(-4.16, -9.54) * mm});
            skLineSegment(sketch, "E100.30.34", {"start": v(-4.48, -9.39) * mm, "end": v(-4.48, -9.4) * mm});
            skLineSegment(sketch, "E100.30.35", {"start": v(-4.15, -9.61) * mm, "end": v(-4.15, -9.63) * mm});
            skLineSegment(sketch, "E100.30.36", {"start": v(-4.16, -9.72) * mm, "end": v(-4.17, -9.76) * mm});
            skLineSegment(sketch, "E100.30.37", {"start": v(-4.88, -9.8) * mm, "end": v(-4.91, -9.83) * mm});
            skLineSegment(sketch, "E100.30.38", {"start": v(-4.68, -9.58) * mm, "end": v(-4.71, -9.62) * mm});
            skLineSegment(sketch, "E100.30.39", {"start": v(-4.78, -9.69) * mm, "end": v(-4.8, -9.72) * mm});
            skLineSegment(sketch, "E100.30.40", {"start": v(-4.3, -9.44) * mm, "end": v(-4.33, -9.43) * mm});
            skLineSegment(sketch, "E100.30.41", {"start": v(-4.33, -9.43) * mm, "end": v(-4.35, -9.42) * mm});
            skLineSegment(sketch, "E100.30.42", {"start": v(-4.2, -10.1) * mm, "end": v(-4.2, -10.15) * mm});
            skLineSegment(sketch, "E100.30.43", {"start": v(-4.2, -10.05) * mm, "end": v(-4.2, -10.1) * mm});
            skLineSegment(sketch, "E100.30.44", {"start": v(-4.91, -9.83) * mm, "end": v(-4.95, -9.86) * mm});
            skLineSegment(sketch, "E100.30.45", {"start": v(-4.5, -9.4) * mm, "end": v(-4.52, -9.4) * mm});
            skLineSegment(sketch, "E100.30.46", {"start": v(-4.42, -9.39) * mm, "end": v(-4.43, -9.38) * mm});
            skLineSegment(sketch, "E100.30.47", {"start": v(-4.8, -9.72) * mm, "end": v(-4.84, -9.76) * mm});
            skLineSegment(sketch, "E100.30.48", {"start": v(-4.21, -10.2) * mm, "end": v(-4.21, -10.25) * mm});
            skLineSegment(sketch, "E100.30.49", {"start": v(-4.15, -9.65) * mm, "end": v(-4.15, -9.66) * mm});
            skLineSegment(sketch, "E100.30.50", {"start": v(-4.84, -9.76) * mm, "end": v(-4.88, -9.8) * mm});
            skLineSegment(sketch, "E100.30.51", {"start": v(-4.65, -9.54) * mm, "end": v(-4.68, -9.58) * mm});
            skLineSegment(sketch, "E100.30.52", {"start": v(-4.17, -9.52) * mm, "end": v(-4.16, -9.53) * mm});
            skLineSegment(sketch, "E100.30.53", {"start": v(-4.2, -9.95) * mm, "end": v(-4.2, -10) * mm});
            skLineSegment(sketch, "E100.30.54", {"start": v(-4.57, -9.45) * mm, "end": v(-4.58, -9.46) * mm});
            skLineSegment(sketch, "E100.30.55", {"start": v(-4.4, -9.4) * mm, "end": v(-4.42, -9.39) * mm});
            skLineSegment(sketch, "E100.30.56", {"start": v(-4.54, -9.42) * mm, "end": v(-4.55, -9.43) * mm});
            skLineSegment(sketch, "E100.30.57", {"start": v(-4.17, -9.51) * mm, "end": v(-4.17, -9.52) * mm});
            skLineSegment(sketch, "E100.30.58", {"start": v(-4.6, -9.48) * mm, "end": v(-4.6, -9.5) * mm});
            skLineSegment(sketch, "E100.30.59", {"start": v(-4.15, -9.66) * mm, "end": v(-4.15, -9.68) * mm});
            skLineSegment(sketch, "E100.30.60", {"start": v(-4.71, -9.62) * mm, "end": v(-4.74, -9.65) * mm});
            skLineSegment(sketch, "E100.30.61", {"start": v(-4.2, -10.15) * mm, "end": v(-4.21, -10.2) * mm});
            skLineSegment(sketch, "E100.30.62", {"start": v(-4.19, -9.9) * mm, "end": v(-4.2, -9.95) * mm});
            skLineSegment(sketch, "E100.30.63", {"start": v(-4.16, -9.7) * mm, "end": v(-4.16, -9.72) * mm});
            skLineSegment(sketch, "E100.30.64", {"start": v(-4.18, -9.5) * mm, "end": v(-4.17, -9.51) * mm});
            skLineSegment(sketch, "E100.30.65", {"start": v(-4.37, -9.4) * mm, "end": v(-4.4, -9.4) * mm});
            skLineSegment(sketch, "E100.30.66", {"start": v(-4.58, -9.46) * mm, "end": v(-4.6, -9.48) * mm});
            skLineSegment(sketch, "E100.30.67", {"start": v(-4.74, -9.65) * mm, "end": v(-4.78, -9.69) * mm});
            skLineSegment(sketch, "E100.30.68", {"start": v(-4.53, -9.41) * mm, "end": v(-4.54, -9.42) * mm});
            skLineSegment(sketch, "E100.30.69", {"start": v(-4.18, -9.81) * mm, "end": v(-4.18, -9.86) * mm});
            skLineSegment(sketch, "E100.30.70", {"start": v(-4.44, -9.38) * mm, "end": v(-4.45, -9.38) * mm});
            skLineSegment(sketch, "E100.30.71", {"start": v(-4.56, -9.44) * mm, "end": v(-4.57, -9.45) * mm});
            skLineSegment(sketch, "E100.30.72", {"start": v(-4.46, -9.38) * mm, "end": v(-4.47, -9.38) * mm});
            skLineSegment(sketch, "E100.30.73", {"start": v(-4.17, -9.76) * mm, "end": v(-4.18, -9.81) * mm});
            skLineSegment(sketch, "E100.30.74", {"start": v(-4.18, -9.5) * mm, "end": v(-4.18, -9.5) * mm});
            skLineSegment(sketch, "E100.30.75", {"start": v(-4.19, -9.5) * mm, "end": v(-4.18, -9.5) * mm});
            skLineSegment(sketch, "E100.30.76", {"start": v(-4.27, -9.46) * mm, "end": v(-4.25, -9.47) * mm});
            skLineSegment(sketch, "E100.30.77", {"start": v(-4.52, -9.4) * mm, "end": v(-4.53, -9.41) * mm});
            skLineSegment(sketch, "E100.30.78", {"start": v(-4.15, -9.6) * mm, "end": v(-4.15, -9.61) * mm});
            skLineSegment(sketch, "E100.30.79", {"start": v(-4.62, -9.5) * mm, "end": v(-4.65, -9.54) * mm});
            skLineSegment(sketch, "E100.30.80", {"start": v(-4.47, -9.38) * mm, "end": v(-4.48, -9.39) * mm});
            skLineSegment(sketch, "E100.30.81", {"start": v(-4.2, -9.49) * mm, "end": v(-4.19, -9.5) * mm});
            skLineSegment(sketch, "E100.30.82", {"start": v(-4.6, -9.5) * mm, "end": v(-4.62, -9.5) * mm});
            skLineSegment(sketch, "E100.30.83", {"start": v(-4.29, -9.45) * mm, "end": v(-4.27, -9.46) * mm});
            skLineSegment(sketch, "E100.30.84", {"start": v(-4.15, -9.63) * mm, "end": v(-4.15, -9.65) * mm});
            skLineSegment(sketch, "E100.30.85", {"start": v(-4.5, -9.4) * mm, "end": v(-4.5, -9.4) * mm});
            skLineSegment(sketch, "E100.30.86", {"start": v(-4.3, -9.44) * mm, "end": v(-4.29, -9.45) * mm});
            skLineSegment(sketch, "E100.30.87", {"start": v(-4.15, -9.68) * mm, "end": v(-4.16, -9.7) * mm});
            skLineSegment(sketch, "E100.30.88", {"start": v(-4.2, -9.49) * mm, "end": v(-4.2, -9.49) * mm});
            skLineSegment(sketch, "E100.30.89", {"start": v(-4.22, -9.48) * mm, "end": v(-4.2, -9.49) * mm});
            skLineSegment(sketch, "E100.30.90", {"start": v(-4.42, -9.39) * mm, "end": v(-4.42, -9.39) * mm});
            skLineSegment(sketch, "E100.30.91", {"start": v(-4.45, -9.38) * mm, "end": v(-4.46, -9.38) * mm});
            skLineSegment(sketch, "E100.30.92", {"start": v(-4.48, -9.4) * mm, "end": v(-4.5, -9.4) * mm});
            skLineSegment(sketch, "E100.30.93", {"start": v(-4.35, -9.42) * mm, "end": v(-4.37, -9.4) * mm});
            skLineSegment(sketch, "E100.30.94", {"start": v(-4.25, -9.47) * mm, "end": v(-4.22, -9.48) * mm});
            skLineSegment(sketch, "E100.30.95", {"start": v(-4.16, -9.55) * mm, "end": v(-4.15, -9.56) * mm});
            skLineSegment(sketch, "E100.30.96", {"start": v(-4.43, -9.38) * mm, "end": v(-4.44, -9.38) * mm});
            skLineSegment(sketch, "E100.30.97", {"start": v(-4.16, -9.54) * mm, "end": v(-4.16, -9.55) * mm});
            skLineSegment(sketch, "E100.30.98", {"start": v(-4.15, -9.56) * mm, "end": v(-4.15, -9.57) * mm});
            skLineSegment(sketch, "E100.30.99", {"start": v(-4.15, -9.57) * mm, "end": v(-4.15, -9.59) * mm});
            skLineSegment(sketch, "E100.31.0", {"start": v(-3.87, -10.83) * mm, "end": v(-3.91, -10.81) * mm});
            skLineSegment(sketch, "E100.31.1", {"start": v(-2.56, -11.21) * mm, "end": v(-2.52, -11.22) * mm});
            skLineSegment(sketch, "E100.31.2", {"start": v(-2.66, -11.04) * mm, "end": v(-2.65, -11.1) * mm});
            skLineSegment(sketch, "E100.31.3", {"start": v(-2.48, -11.23) * mm, "end": v(-2.44, -11.24) * mm});
            skLineSegment(sketch, "E100.31.4", {"start": v(-3.53, -10.5) * mm, "end": v(-3.56, -10.54) * mm});
            skLineSegment(sketch, "E100.31.5", {"start": v(-3.95, -10.8) * mm, "end": v(-3.98, -10.79) * mm});
            skLineSegment(sketch, "E100.31.6", {"start": v(-2.6, -11.2) * mm, "end": v(-2.56, -11.21) * mm});
            skLineSegment(sketch, "E100.31.7", {"start": v(-3.7, -10.7) * mm, "end": v(-3.73, -10.73) * mm});
            skLineSegment(sketch, "E100.31.8", {"start": v(-2.52, -11.22) * mm, "end": v(-2.48, -11.23) * mm});
            skLineSegment(sketch, "E100.31.9", {"start": v(-3.73, -10.73) * mm, "end": v(-3.77, -10.77) * mm});
            skLineSegment(sketch, "E100.31.10", {"start": v(-3.98, -10.79) * mm, "end": v(-4.02, -10.77) * mm});
            skLineSegment(sketch, "E100.31.11", {"start": v(-3.77, -10.77) * mm, "end": v(-3.8, -10.8) * mm});
            skLineSegment(sketch, "E100.31.12", {"start": v(-3.66, -10.66) * mm, "end": v(-3.7, -10.7) * mm});
            skLineSegment(sketch, "E100.31.13", {"start": v(-2.64, -11.14) * mm, "end": v(-2.63, -11.2) * mm});
            skLineSegment(sketch, "E100.31.14", {"start": v(-3.84, -10.84) * mm, "end": v(-3.87, -10.83) * mm});
            skLineSegment(sketch, "E100.31.15", {"start": v(-3.56, -10.54) * mm, "end": v(-3.6, -10.58) * mm});
            skLineSegment(sketch, "E100.31.16", {"start": v(-3.91, -10.81) * mm, "end": v(-3.95, -10.8) * mm});
            skLineSegment(sketch, "E100.31.17", {"start": v(-2.63, -11.2) * mm, "end": v(-2.6, -11.2) * mm});
            skLineSegment(sketch, "E100.31.18", {"start": v(-2.68, -10.94) * mm, "end": v(-2.67, -11) * mm});
            skLineSegment(sketch, "E100.31.19", {"start": v(-3.63, -10.62) * mm, "end": v(-3.66, -10.66) * mm});
            skLineSegment(sketch, "E100.31.20", {"start": v(-3.8, -10.8) * mm, "end": v(-3.84, -10.84) * mm});
            skLineSegment(sketch, "E100.31.21", {"start": v(-2.7, -10.8) * mm, "end": v(-2.7, -10.84) * mm});
            skLineSegment(sketch, "E100.31.22", {"start": v(-2.67, -11) * mm, "end": v(-2.66, -11.04) * mm});
            skLineSegment(sketch, "E100.31.23", {"start": v(-3.6, -10.58) * mm, "end": v(-3.63, -10.62) * mm});
            skLineSegment(sketch, "E100.31.24", {"start": v(-2.7, -10.84) * mm, "end": v(-2.69, -10.9) * mm});
            skLineSegment(sketch, "E100.31.25", {"start": v(-2.69, -10.9) * mm, "end": v(-2.68, -10.94) * mm});
            skLineSegment(sketch, "E100.31.26", {"start": v(-2.65, -11.1) * mm, "end": v(-2.64, -11.14) * mm});
            skLineSegment(sketch, "E100.31.27", {"start": v(-2.71, -10.74) * mm, "end": v(-2.7, -10.8) * mm});
            skLineSegment(sketch, "E100.31.28", {"start": v(-2.74, -10.08) * mm, "end": v(-2.74, -10.1) * mm});
            skLineSegment(sketch, "E100.31.29", {"start": v(-2.74, -10.35) * mm, "end": v(-2.74, -10.4) * mm});
            skLineSegment(sketch, "E100.31.30", {"start": v(-2.73, -10.5) * mm, "end": v(-2.73, -10.55) * mm});
            skLineSegment(sketch, "E100.31.31", {"start": v(-3.16, -9.98) * mm, "end": v(-3.17, -10) * mm});
            skLineSegment(sketch, "E100.31.32", {"start": v(-3.5, -10.47) * mm, "end": v(-3.53, -10.5) * mm});
            skLineSegment(sketch, "E100.31.33", {"start": v(-2.76, -10.02) * mm, "end": v(-2.76, -10.03) * mm});
            skLineSegment(sketch, "E100.31.34", {"start": v(-3.1, -9.93) * mm, "end": v(-3.1, -9.93) * mm});
            skLineSegment(sketch, "E100.31.35", {"start": v(-2.74, -10.1) * mm, "end": v(-2.74, -10.12) * mm});
            skLineSegment(sketch, "E100.31.36", {"start": v(-2.73, -10.2) * mm, "end": v(-2.74, -10.26) * mm});
            skLineSegment(sketch, "E100.31.37", {"start": v(-3.44, -10.39) * mm, "end": v(-3.47, -10.43) * mm});
            skLineSegment(sketch, "E100.31.38", {"start": v(-3.27, -10.15) * mm, "end": v(-3.3, -10.19) * mm});
            skLineSegment(sketch, "E100.31.39", {"start": v(-3.35, -10.27) * mm, "end": v(-3.38, -10.3) * mm});
            skLineSegment(sketch, "E100.31.40", {"start": v(-2.92, -9.95) * mm, "end": v(-2.95, -9.95) * mm});
            skLineSegment(sketch, "E100.31.41", {"start": v(-2.95, -9.95) * mm, "end": v(-2.97, -9.94) * mm});
            skLineSegment(sketch, "E100.31.42", {"start": v(-2.73, -10.6) * mm, "end": v(-2.72, -10.65) * mm});
            skLineSegment(sketch, "E100.31.43", {"start": v(-2.73, -10.55) * mm, "end": v(-2.73, -10.6) * mm});
            skLineSegment(sketch, "E100.31.44", {"start": v(-3.47, -10.43) * mm, "end": v(-3.5, -10.47) * mm});
            skLineSegment(sketch, "E100.31.45", {"start": v(-3.12, -9.95) * mm, "end": v(-3.13, -9.95) * mm});
            skLineSegment(sketch, "E100.31.46", {"start": v(-3.04, -9.92) * mm, "end": v(-3.05, -9.92) * mm});
            skLineSegment(sketch, "E100.31.47", {"start": v(-3.38, -10.3) * mm, "end": v(-3.4, -10.35) * mm});
            skLineSegment(sketch, "E100.31.48", {"start": v(-2.72, -10.7) * mm, "end": v(-2.71, -10.74) * mm});
            skLineSegment(sketch, "E100.31.49", {"start": v(-2.73, -10.14) * mm, "end": v(-2.73, -10.15) * mm});
            skLineSegment(sketch, "E100.31.50", {"start": v(-3.4, -10.35) * mm, "end": v(-3.44, -10.39) * mm});
            skLineSegment(sketch, "E100.31.51", {"start": v(-3.24, -10.1) * mm, "end": v(-3.27, -10.15) * mm});
            skLineSegment(sketch, "E100.31.52", {"start": v(-2.77, -10.02) * mm, "end": v(-2.76, -10.02) * mm});
            skLineSegment(sketch, "E100.31.53", {"start": v(-2.73, -10.45) * mm, "end": v(-2.73, -10.5) * mm});
            skLineSegment(sketch, "E100.31.54", {"start": v(-3.18, -10) * mm, "end": v(-3.2, -10.02) * mm});
            skLineSegment(sketch, "E100.31.55", {"start": v(-3.01, -9.93) * mm, "end": v(-3.03, -9.92) * mm});
            skLineSegment(sketch, "E100.31.56", {"start": v(-3.15, -9.97) * mm, "end": v(-3.16, -9.98) * mm});
            skLineSegment(sketch, "E100.31.57", {"start": v(-2.78, -10) * mm, "end": v(-2.77, -10.02) * mm});
            skLineSegment(sketch, "E100.31.58", {"start": v(-3.2, -10.03) * mm, "end": v(-3.2, -10.05) * mm});
            skLineSegment(sketch, "E100.31.59", {"start": v(-2.73, -10.15) * mm, "end": v(-2.73, -10.17) * mm});
            skLineSegment(sketch, "E100.31.60", {"start": v(-3.3, -10.19) * mm, "end": v(-3.32, -10.23) * mm});
            skLineSegment(sketch, "E100.31.61", {"start": v(-2.72, -10.65) * mm, "end": v(-2.72, -10.7) * mm});
            skLineSegment(sketch, "E100.31.62", {"start": v(-2.74, -10.4) * mm, "end": v(-2.73, -10.45) * mm});
            skLineSegment(sketch, "E100.31.63", {"start": v(-2.73, -10.2) * mm, "end": v(-2.73, -10.2) * mm});
            skLineSegment(sketch, "E100.31.64", {"start": v(-2.78, -10) * mm, "end": v(-2.78, -10) * mm});
            skLineSegment(sketch, "E100.31.65", {"start": v(-3, -9.93) * mm, "end": v(-3.01, -9.93) * mm});
            skLineSegment(sketch, "E100.31.66", {"start": v(-3.2, -10.02) * mm, "end": v(-3.2, -10.03) * mm});
            skLineSegment(sketch, "E100.31.67", {"start": v(-3.32, -10.23) * mm, "end": v(-3.35, -10.27) * mm});
            skLineSegment(sketch, "E100.31.68", {"start": v(-3.14, -9.96) * mm, "end": v(-3.15, -9.97) * mm});
            skLineSegment(sketch, "E100.31.69", {"start": v(-2.74, -10.3) * mm, "end": v(-2.74, -10.35) * mm});
            skLineSegment(sketch, "E100.31.70", {"start": v(-3.06, -9.92) * mm, "end": v(-3.07, -9.92) * mm});
            skLineSegment(sketch, "E100.31.71", {"start": v(-3.17, -10) * mm, "end": v(-3.18, -10) * mm});
            skLineSegment(sketch, "E100.31.72", {"start": v(-3.08, -9.92) * mm, "end": v(-3.08, -9.92) * mm});
            skLineSegment(sketch, "E100.31.73", {"start": v(-2.74, -10.26) * mm, "end": v(-2.74, -10.3) * mm});
            skLineSegment(sketch, "E100.31.74", {"start": v(-2.79, -10) * mm, "end": v(-2.78, -10) * mm});
            skLineSegment(sketch, "E100.31.75", {"start": v(-2.8, -10) * mm, "end": v(-2.79, -10) * mm});
            skLineSegment(sketch, "E100.31.76", {"start": v(-2.88, -9.97) * mm, "end": v(-2.86, -9.97) * mm});
            skLineSegment(sketch, "E100.31.77", {"start": v(-3.13, -9.95) * mm, "end": v(-3.14, -9.96) * mm});
            skLineSegment(sketch, "E100.31.78", {"start": v(-2.74, -10.1) * mm, "end": v(-2.74, -10.1) * mm});
            skLineSegment(sketch, "E100.31.79", {"start": v(-3.22, -10.07) * mm, "end": v(-3.24, -10.1) * mm});
            skLineSegment(sketch, "E100.31.80", {"start": v(-3.08, -9.92) * mm, "end": v(-3.1, -9.93) * mm});
            skLineSegment(sketch, "E100.31.81", {"start": v(-2.8, -9.99) * mm, "end": v(-2.8, -10) * mm});
            skLineSegment(sketch, "E100.31.82", {"start": v(-3.2, -10.05) * mm, "end": v(-3.22, -10.07) * mm});
            skLineSegment(sketch, "E100.31.83", {"start": v(-2.9, -9.96) * mm, "end": v(-2.88, -9.97) * mm});
            skLineSegment(sketch, "E100.31.84", {"start": v(-2.74, -10.12) * mm, "end": v(-2.73, -10.14) * mm});
            skLineSegment(sketch, "E100.31.85", {"start": v(-3.11, -9.94) * mm, "end": v(-3.12, -9.95) * mm});
            skLineSegment(sketch, "E100.31.86", {"start": v(-2.92, -9.95) * mm, "end": v(-2.9, -9.96) * mm});
            skLineSegment(sketch, "E100.31.87", {"start": v(-2.73, -10.17) * mm, "end": v(-2.73, -10.2) * mm});
            skLineSegment(sketch, "E100.31.88", {"start": v(-2.81, -9.99) * mm, "end": v(-2.8, -9.99) * mm});
            skLineSegment(sketch, "E100.31.89", {"start": v(-2.83, -9.98) * mm, "end": v(-2.81, -9.99) * mm});
            skLineSegment(sketch, "E100.31.90", {"start": v(-3.03, -9.92) * mm, "end": v(-3.04, -9.92) * mm});
            skLineSegment(sketch, "E100.31.91", {"start": v(-3.07, -9.92) * mm, "end": v(-3.08, -9.92) * mm});
            skLineSegment(sketch, "E100.31.92", {"start": v(-3.1, -9.93) * mm, "end": v(-3.11, -9.94) * mm});
            skLineSegment(sketch, "E100.31.93", {"start": v(-2.97, -9.94) * mm, "end": v(-3, -9.93) * mm});
            skLineSegment(sketch, "E100.31.94", {"start": v(-2.86, -9.97) * mm, "end": v(-2.83, -9.98) * mm});
            skLineSegment(sketch, "E100.31.95", {"start": v(-2.76, -10.04) * mm, "end": v(-2.75, -10.05) * mm});
            skLineSegment(sketch, "E100.31.96", {"start": v(-3.05, -9.92) * mm, "end": v(-3.06, -9.92) * mm});
            skLineSegment(sketch, "E100.31.97", {"start": v(-2.76, -10.03) * mm, "end": v(-2.76, -10.04) * mm});
            skLineSegment(sketch, "E100.31.98", {"start": v(-2.75, -10.05) * mm, "end": v(-2.75, -10.07) * mm});
            skLineSegment(sketch, "E100.31.99", {"start": v(-2.75, -10.07) * mm, "end": v(-2.74, -10.08) * mm});
            skLineSegment(sketch, "E100.32.0", {"start": v(-2.3, -11.27) * mm, "end": v(-2.33, -11.26) * mm});
            skLineSegment(sketch, "E100.32.1", {"start": v(-0.94, -11.46) * mm, "end": v(-0.9, -11.46) * mm});
            skLineSegment(sketch, "E100.32.2", {"start": v(-1.06, -11.31) * mm, "end": v(-1.05, -11.36) * mm});
            skLineSegment(sketch, "E100.32.3", {"start": v(-0.86, -11.47) * mm, "end": v(-0.82, -11.47) * mm});
            skLineSegment(sketch, "E100.32.4", {"start": v(-2, -10.9) * mm, "end": v(-2.02, -10.94) * mm});
            skLineSegment(sketch, "E100.32.5", {"start": v(-2.37, -11.25) * mm, "end": v(-2.4, -11.25) * mm});
            skLineSegment(sketch, "E100.32.6", {"start": v(-0.97, -11.46) * mm, "end": v(-0.94, -11.46) * mm});
            skLineSegment(sketch, "E100.32.7", {"start": v(-2.14, -11.11) * mm, "end": v(-2.17, -11.15) * mm});
            skLineSegment(sketch, "E100.32.8", {"start": v(-0.9, -11.46) * mm, "end": v(-0.86, -11.47) * mm});
            skLineSegment(sketch, "E100.32.9", {"start": v(-2.17, -11.15) * mm, "end": v(-2.2, -11.2) * mm});
            skLineSegment(sketch, "E100.32.10", {"start": v(-2.4, -11.25) * mm, "end": v(-2.44, -11.24) * mm});
            skLineSegment(sketch, "E100.32.11", {"start": v(-2.2, -11.2) * mm, "end": v(-2.23, -11.24) * mm});
            skLineSegment(sketch, "E100.32.12", {"start": v(-2.1, -11.07) * mm, "end": v(-2.14, -11.11) * mm});
            skLineSegment(sketch, "E100.32.13", {"start": v(-1.03, -11.4) * mm, "end": v(-1.01, -11.46) * mm});
            skLineSegment(sketch, "E100.32.14", {"start": v(-2.26, -11.28) * mm, "end": v(-2.3, -11.27) * mm});
            skLineSegment(sketch, "E100.32.15", {"start": v(-2.02, -10.94) * mm, "end": v(-2.05, -10.98) * mm});
            skLineSegment(sketch, "E100.32.16", {"start": v(-2.33, -11.26) * mm, "end": v(-2.37, -11.25) * mm});
            skLineSegment(sketch, "E100.32.17", {"start": v(-1.01, -11.46) * mm, "end": v(-0.97, -11.46) * mm});
            skLineSegment(sketch, "E100.32.18", {"start": v(-1.1, -11.21) * mm, "end": v(-1.08, -11.26) * mm});
            skLineSegment(sketch, "E100.32.19", {"start": v(-2.08, -11.03) * mm, "end": v(-2.1, -11.07) * mm});
            skLineSegment(sketch, "E100.32.20", {"start": v(-2.23, -11.24) * mm, "end": v(-2.26, -11.28) * mm});
            skLineSegment(sketch, "E100.32.21", {"start": v(-1.14, -11.07) * mm, "end": v(-1.13, -11.12) * mm});
            skLineSegment(sketch, "E100.32.22", {"start": v(-1.08, -11.26) * mm, "end": v(-1.06, -11.31) * mm});
            skLineSegment(sketch, "E100.32.23", {"start": v(-2.05, -10.98) * mm, "end": v(-2.08, -11.03) * mm});
            skLineSegment(sketch, "E100.32.24", {"start": v(-1.13, -11.12) * mm, "end": v(-1.11, -11.17) * mm});
            skLineSegment(sketch, "E100.32.25", {"start": v(-1.11, -11.17) * mm, "end": v(-1.1, -11.21) * mm});
            skLineSegment(sketch, "E100.32.26", {"start": v(-1.05, -11.36) * mm, "end": v(-1.03, -11.4) * mm});
            skLineSegment(sketch, "E100.32.27", {"start": v(-1.15, -11.02) * mm, "end": v(-1.14, -11.07) * mm});
            skLineSegment(sketch, "E100.32.28", {"start": v(-1.28, -10.37) * mm, "end": v(-1.28, -10.38) * mm});
            skLineSegment(sketch, "E100.32.29", {"start": v(-1.24, -10.64) * mm, "end": v(-1.23, -10.69) * mm});
            skLineSegment(sketch, "E100.32.30", {"start": v(-1.21, -10.78) * mm, "end": v(-1.2, -10.83) * mm});
            skLineSegment(sketch, "E100.32.31", {"start": v(-1.7, -10.33) * mm, "end": v(-1.72, -10.34) * mm});
            skLineSegment(sketch, "E100.32.32", {"start": v(-1.97, -10.86) * mm, "end": v(-2, -10.9) * mm});
            skLineSegment(sketch, "E100.32.33", {"start": v(-1.31, -10.32) * mm, "end": v(-1.3, -10.32) * mm});
            skLineSegment(sketch, "E100.32.34", {"start": v(-1.65, -10.27) * mm, "end": v(-1.66, -10.27) * mm});
            skLineSegment(sketch, "E100.32.35", {"start": v(-1.27, -10.4) * mm, "end": v(-1.27, -10.4) * mm});
            skLineSegment(sketch, "E100.32.36", {"start": v(-1.25, -10.5) * mm, "end": v(-1.25, -10.54) * mm});
            skLineSegment(sketch, "E100.32.37", {"start": v(-1.92, -10.77) * mm, "end": v(-1.95, -10.81) * mm});
            skLineSegment(sketch, "E100.32.38", {"start": v(-1.8, -10.51) * mm, "end": v(-1.81, -10.55) * mm});
            skLineSegment(sketch, "E100.32.39", {"start": v(-1.85, -10.64) * mm, "end": v(-1.88, -10.69) * mm});
            skLineSegment(sketch, "E100.32.40", {"start": v(-1.48, -10.27) * mm, "end": v(-1.5, -10.27) * mm});
            skLineSegment(sketch, "E100.32.41", {"start": v(-1.5, -10.27) * mm, "end": v(-1.52, -10.26) * mm});
            skLineSegment(sketch, "E100.32.42", {"start": v(-1.2, -10.88) * mm, "end": v(-1.18, -10.92) * mm});
            skLineSegment(sketch, "E100.32.43", {"start": v(-1.2, -10.83) * mm, "end": v(-1.2, -10.88) * mm});
            skLineSegment(sketch, "E100.32.44", {"start": v(-1.95, -10.81) * mm, "end": v(-1.97, -10.86) * mm});
            skLineSegment(sketch, "E100.32.45", {"start": v(-1.67, -10.29) * mm, "end": v(-1.68, -10.3) * mm});
            skLineSegment(sketch, "E100.32.46", {"start": v(-1.6, -10.25) * mm, "end": v(-1.6, -10.25) * mm});
            skLineSegment(sketch, "E100.32.47", {"start": v(-1.88, -10.69) * mm, "end": v(-1.9, -10.73) * mm});
            skLineSegment(sketch, "E100.32.48", {"start": v(-1.17, -10.97) * mm, "end": v(-1.15, -11.02) * mm});
            skLineSegment(sketch, "E100.32.49", {"start": v(-1.26, -10.42) * mm, "end": v(-1.26, -10.44) * mm});
            skLineSegment(sketch, "E100.32.50", {"start": v(-1.9, -10.73) * mm, "end": v(-1.92, -10.77) * mm});
            skLineSegment(sketch, "E100.32.51", {"start": v(-1.77, -10.47) * mm, "end": v(-1.8, -10.51) * mm});
            skLineSegment(sketch, "E100.32.52", {"start": v(-1.32, -10.3) * mm, "end": v(-1.31, -10.32) * mm});
            skLineSegment(sketch, "E100.32.53", {"start": v(-1.22, -10.73) * mm, "end": v(-1.21, -10.78) * mm});
            skLineSegment(sketch, "E100.32.54", {"start": v(-1.72, -10.36) * mm, "end": v(-1.73, -10.37) * mm});
            skLineSegment(sketch, "E100.32.55", {"start": v(-1.57, -10.26) * mm, "end": v(-1.6, -10.25) * mm});
            skLineSegment(sketch, "E100.32.56", {"start": v(-1.7, -10.32) * mm, "end": v(-1.7, -10.33) * mm});
            skLineSegment(sketch, "E100.32.57", {"start": v(-1.32, -10.3) * mm, "end": v(-1.32, -10.3) * mm});
            skLineSegment(sketch, "E100.32.58", {"start": v(-1.74, -10.39) * mm, "end": v(-1.75, -10.4) * mm});
            skLineSegment(sketch, "E100.32.59", {"start": v(-1.26, -10.44) * mm, "end": v(-1.26, -10.46) * mm});
            skLineSegment(sketch, "E100.32.60", {"start": v(-1.81, -10.55) * mm, "end": v(-1.83, -10.6) * mm});
            skLineSegment(sketch, "E100.32.61", {"start": v(-1.18, -10.92) * mm, "end": v(-1.17, -10.97) * mm});
            skLineSegment(sketch, "E100.32.62", {"start": v(-1.23, -10.69) * mm, "end": v(-1.22, -10.73) * mm});
            skLineSegment(sketch, "E100.32.63", {"start": v(-1.26, -10.48) * mm, "end": v(-1.25, -10.5) * mm});
            skLineSegment(sketch, "E100.32.64", {"start": v(-1.33, -10.3) * mm, "end": v(-1.32, -10.3) * mm});
            skLineSegment(sketch, "E100.32.65", {"start": v(-1.55, -10.26) * mm, "end": v(-1.57, -10.26) * mm});
            skLineSegment(sketch, "E100.32.66", {"start": v(-1.73, -10.37) * mm, "end": v(-1.74, -10.39) * mm});
            skLineSegment(sketch, "E100.32.67", {"start": v(-1.83, -10.6) * mm, "end": v(-1.85, -10.64) * mm});
            skLineSegment(sketch, "E100.32.68", {"start": v(-1.7, -10.3) * mm, "end": v(-1.7, -10.32) * mm});
            skLineSegment(sketch, "E100.32.69", {"start": v(-1.24, -10.59) * mm, "end": v(-1.24, -10.64) * mm});
            skLineSegment(sketch, "E100.32.70", {"start": v(-1.62, -10.25) * mm, "end": v(-1.62, -10.26) * mm});
            skLineSegment(sketch, "E100.32.71", {"start": v(-1.72, -10.34) * mm, "end": v(-1.72, -10.36) * mm});
            skLineSegment(sketch, "E100.32.72", {"start": v(-1.63, -10.26) * mm, "end": v(-1.64, -10.26) * mm});
            skLineSegment(sketch, "E100.32.73", {"start": v(-1.25, -10.54) * mm, "end": v(-1.24, -10.59) * mm});
            skLineSegment(sketch, "E100.32.74", {"start": v(-1.34, -10.3) * mm, "end": v(-1.33, -10.3) * mm});
            skLineSegment(sketch, "E100.32.75", {"start": v(-1.35, -10.29) * mm, "end": v(-1.34, -10.3) * mm});
            skLineSegment(sketch, "E100.32.76", {"start": v(-1.43, -10.28) * mm, "end": v(-1.4, -10.28) * mm});
            skLineSegment(sketch, "E100.32.77", {"start": v(-1.68, -10.3) * mm, "end": v(-1.7, -10.3) * mm});
            skLineSegment(sketch, "E100.32.78", {"start": v(-1.28, -10.38) * mm, "end": v(-1.27, -10.4) * mm});
            skLineSegment(sketch, "E100.32.79", {"start": v(-1.75, -10.42) * mm, "end": v(-1.77, -10.47) * mm});
            skLineSegment(sketch, "E100.32.80", {"start": v(-1.64, -10.26) * mm, "end": v(-1.65, -10.27) * mm});
            skLineSegment(sketch, "E100.32.81", {"start": v(-1.35, -10.29) * mm, "end": v(-1.35, -10.29) * mm});
            skLineSegment(sketch, "E100.32.82", {"start": v(-1.75, -10.4) * mm, "end": v(-1.75, -10.42) * mm});
            skLineSegment(sketch, "E100.32.83", {"start": v(-1.45, -10.27) * mm, "end": v(-1.43, -10.28) * mm});
            skLineSegment(sketch, "E100.32.84", {"start": v(-1.27, -10.4) * mm, "end": v(-1.26, -10.42) * mm});
            skLineSegment(sketch, "E100.32.85", {"start": v(-1.67, -10.28) * mm, "end": v(-1.67, -10.29) * mm});
            skLineSegment(sketch, "E100.32.86", {"start": v(-1.48, -10.27) * mm, "end": v(-1.45, -10.27) * mm});
            skLineSegment(sketch, "E100.32.87", {"start": v(-1.26, -10.46) * mm, "end": v(-1.26, -10.48) * mm});
            skLineSegment(sketch, "E100.32.88", {"start": v(-1.36, -10.29) * mm, "end": v(-1.35, -10.29) * mm});
            skLineSegment(sketch, "E100.32.89", {"start": v(-1.38, -10.28) * mm, "end": v(-1.36, -10.29) * mm});
            skLineSegment(sketch, "E100.32.90", {"start": v(-1.6, -10.25) * mm, "end": v(-1.6, -10.25) * mm});
            skLineSegment(sketch, "E100.32.91", {"start": v(-1.62, -10.26) * mm, "end": v(-1.63, -10.26) * mm});
            skLineSegment(sketch, "E100.32.92", {"start": v(-1.66, -10.27) * mm, "end": v(-1.67, -10.28) * mm});
            skLineSegment(sketch, "E100.32.93", {"start": v(-1.52, -10.26) * mm, "end": v(-1.55, -10.26) * mm});
            skLineSegment(sketch, "E100.32.94", {"start": v(-1.4, -10.28) * mm, "end": v(-1.38, -10.28) * mm});
            skLineSegment(sketch, "E100.32.95", {"start": v(-1.3, -10.33) * mm, "end": v(-1.3, -10.34) * mm});
            skLineSegment(sketch, "E100.32.96", {"start": v(-1.6, -10.25) * mm, "end": v(-1.62, -10.25) * mm});
            skLineSegment(sketch, "E100.32.97", {"start": v(-1.3, -10.32) * mm, "end": v(-1.3, -10.33) * mm});
            skLineSegment(sketch, "E100.32.98", {"start": v(-1.3, -10.34) * mm, "end": v(-1.29, -10.35) * mm});
            skLineSegment(sketch, "E100.32.99", {"start": v(-1.29, -10.35) * mm, "end": v(-1.28, -10.37) * mm});
            skLineSegment(sketch, "E100.33.0", {"start": v(-0.67, -11.48) * mm, "end": v(-0.7, -11.48) * mm});
            skLineSegment(sketch, "E100.33.1", {"start": v(0.7, -11.48) * mm, "end": v(0.74, -11.48) * mm});
            skLineSegment(sketch, "E100.33.2", {"start": v(0.56, -11.35) * mm, "end": v(0.58, -11.4) * mm});
            skLineSegment(sketch, "E100.33.3", {"start": v(0.78, -11.47) * mm, "end": v(0.82, -11.47) * mm});
            skLineSegment(sketch, "E100.33.4", {"start": v(-0.43, -11.07) * mm, "end": v(-0.45, -11.12) * mm});
            skLineSegment(sketch, "E100.33.5", {"start": v(-0.74, -11.48) * mm, "end": v(-0.78, -11.47) * mm});
            skLineSegment(sketch, "E100.33.6", {"start": v(0.67, -11.48) * mm, "end": v(0.7, -11.48) * mm});
            skLineSegment(sketch, "E100.33.7", {"start": v(-0.53, -11.3) * mm, "end": v(-0.56, -11.35) * mm});
            skLineSegment(sketch, "E100.33.8", {"start": v(0.74, -11.48) * mm, "end": v(0.78, -11.47) * mm});
            skLineSegment(sketch, "E100.33.9", {"start": v(-0.56, -11.35) * mm, "end": v(-0.58, -11.4) * mm});
            skLineSegment(sketch, "E100.33.10", {"start": v(-0.78, -11.47) * mm, "end": v(-0.82, -11.47) * mm});
            skLineSegment(sketch, "E100.33.11", {"start": v(-0.58, -11.4) * mm, "end": v(-0.6, -11.44) * mm});
            skLineSegment(sketch, "E100.33.12", {"start": v(-0.51, -11.26) * mm, "end": v(-0.53, -11.3) * mm});
            skLineSegment(sketch, "E100.33.13", {"start": v(0.6, -11.44) * mm, "end": v(0.63, -11.48) * mm});
            skLineSegment(sketch, "E100.33.14", {"start": v(-0.63, -11.48) * mm, "end": v(-0.67, -11.48) * mm});
            skLineSegment(sketch, "E100.33.15", {"start": v(-0.45, -11.12) * mm, "end": v(-0.47, -11.16) * mm});
            skLineSegment(sketch, "E100.33.16", {"start": v(-0.7, -11.48) * mm, "end": v(-0.74, -11.48) * mm});
            skLineSegment(sketch, "E100.33.17", {"start": v(0.63, -11.48) * mm, "end": v(0.67, -11.48) * mm});
            skLineSegment(sketch, "E100.33.18", {"start": v(0.51, -11.26) * mm, "end": v(0.53, -11.3) * mm});
            skLineSegment(sketch, "E100.33.19", {"start": v(-0.49, -11.21) * mm, "end": v(-0.51, -11.26) * mm});
            skLineSegment(sketch, "E100.33.20", {"start": v(-0.6, -11.44) * mm, "end": v(-0.63, -11.48) * mm});
            skLineSegment(sketch, "E100.33.21", {"start": v(0.45, -11.12) * mm, "end": v(0.47, -11.16) * mm});
            skLineSegment(sketch, "E100.33.22", {"start": v(0.53, -11.3) * mm, "end": v(0.56, -11.35) * mm});
            skLineSegment(sketch, "E100.33.23", {"start": v(-0.47, -11.16) * mm, "end": v(-0.49, -11.21) * mm});
            skLineSegment(sketch, "E100.33.24", {"start": v(0.47, -11.16) * mm, "end": v(0.49, -11.21) * mm});
            skLineSegment(sketch, "E100.33.25", {"start": v(0.49, -11.21) * mm, "end": v(0.51, -11.26) * mm});
            skLineSegment(sketch, "E100.33.26", {"start": v(0.58, -11.4) * mm, "end": v(0.6, -11.44) * mm});
            skLineSegment(sketch, "E100.33.27", {"start": v(0.43, -11.07) * mm, "end": v(0.45, -11.12) * mm});
            skLineSegment(sketch, "E100.33.28", {"start": v(0.2, -10.44) * mm, "end": v(0.21, -10.46) * mm});
            skLineSegment(sketch, "E100.33.29", {"start": v(0.3, -10.7) * mm, "end": v(0.3, -10.75) * mm});
            skLineSegment(sketch, "E100.33.30", {"start": v(0.34, -10.84) * mm, "end": v(0.35, -10.89) * mm});
            skLineSegment(sketch, "E100.33.31", {"start": v(-0.22, -10.47) * mm, "end": v(-0.23, -10.48) * mm});
            skLineSegment(sketch, "E100.33.32", {"start": v(-0.4, -11.03) * mm, "end": v(-0.43, -11.07) * mm});
            skLineSegment(sketch, "E100.33.33", {"start": v(0.17, -10.4) * mm, "end": v(0.18, -10.4) * mm});
            skLineSegment(sketch, "E100.33.34", {"start": v(-0.17, -10.4) * mm, "end": v(-0.18, -10.4) * mm});
            skLineSegment(sketch, "E100.33.35", {"start": v(0.22, -10.47) * mm, "end": v(0.23, -10.48) * mm});
            skLineSegment(sketch, "E100.33.36", {"start": v(0.25, -10.57) * mm, "end": v(0.26, -10.61) * mm});
            skLineSegment(sketch, "E100.33.37", {"start": v(-0.37, -10.94) * mm, "end": v(-0.39, -10.98) * mm});
            skLineSegment(sketch, "E100.33.38", {"start": v(-0.28, -10.66) * mm, "end": v(-0.3, -10.7) * mm});
            skLineSegment(sketch, "E100.33.39", {"start": v(-0.32, -10.8) * mm, "end": v(-0.34, -10.84) * mm});
            skLineSegment(sketch, "E100.33.40", {"start": v(0, -10.38) * mm, "end": v(-0.02, -10.37) * mm});
            skLineSegment(sketch, "E100.33.41", {"start": v(-0.02, -10.37) * mm, "end": v(-0.05, -10.37) * mm});
            skLineSegment(sketch, "E100.33.42", {"start": v(0.37, -10.94) * mm, "end": v(0.39, -10.98) * mm});
            skLineSegment(sketch, "E100.33.43", {"start": v(0.35, -10.89) * mm, "end": v(0.37, -10.94) * mm});
            skLineSegment(sketch, "E100.33.44", {"start": v(-0.39, -10.98) * mm, "end": v(-0.4, -11.03) * mm});
            skLineSegment(sketch, "E100.33.45", {"start": v(-0.2, -10.42) * mm, "end": v(-0.2, -10.43) * mm});
            skLineSegment(sketch, "E100.33.46", {"start": v(-0.12, -10.37) * mm, "end": v(-0.13, -10.38) * mm});
            skLineSegment(sketch, "E100.33.47", {"start": v(-0.34, -10.84) * mm, "end": v(-0.35, -10.89) * mm});
            skLineSegment(sketch, "E100.33.48", {"start": v(0.4, -11.03) * mm, "end": v(0.43, -11.07) * mm});
            skLineSegment(sketch, "E100.33.49", {"start": v(0.23, -10.5) * mm, "end": v(0.24, -10.51) * mm});
            skLineSegment(sketch, "E100.33.50", {"start": v(-0.35, -10.89) * mm, "end": v(-0.37, -10.94) * mm});
            skLineSegment(sketch, "E100.33.51", {"start": v(-0.26, -10.61) * mm, "end": v(-0.28, -10.66) * mm});
            skLineSegment(sketch, "E100.33.52", {"start": v(0.16, -10.4) * mm, "end": v(0.17, -10.4) * mm});
            skLineSegment(sketch, "E100.33.53", {"start": v(0.32, -10.8) * mm, "end": v(0.34, -10.84) * mm});
            skLineSegment(sketch, "E100.33.54", {"start": v(-0.23, -10.5) * mm, "end": v(-0.24, -10.51) * mm});
            skLineSegment(sketch, "E100.33.55", {"start": v(-0.1, -10.37) * mm, "end": v(-0.12, -10.37) * mm});
            skLineSegment(sketch, "E100.33.56", {"start": v(-0.21, -10.46) * mm, "end": v(-0.22, -10.47) * mm});
            skLineSegment(sketch, "E100.33.57", {"start": v(0.16, -10.39) * mm, "end": v(0.16, -10.4) * mm});
            skLineSegment(sketch, "E100.33.58", {"start": v(-0.24, -10.53) * mm, "end": v(-0.25, -10.55) * mm});
            skLineSegment(sketch, "E100.33.59", {"start": v(0.24, -10.51) * mm, "end": v(0.24, -10.53) * mm});
            skLineSegment(sketch, "E100.33.60", {"start": v(-0.3, -10.7) * mm, "end": v(-0.3, -10.75) * mm});
            skLineSegment(sketch, "E100.33.61", {"start": v(0.39, -10.98) * mm, "end": v(0.4, -11.03) * mm});
            skLineSegment(sketch, "E100.33.62", {"start": v(0.3, -10.75) * mm, "end": v(0.32, -10.8) * mm});
            skLineSegment(sketch, "E100.33.63", {"start": v(0.25, -10.55) * mm, "end": v(0.25, -10.57) * mm});
            skLineSegment(sketch, "E100.33.64", {"start": v(0.15, -10.38) * mm, "end": v(0.16, -10.39) * mm});
            skLineSegment(sketch, "E100.33.65", {"start": v(-0.07, -10.37) * mm, "end": v(-0.1, -10.37) * mm});
            skLineSegment(sketch, "E100.33.66", {"start": v(-0.24, -10.51) * mm, "end": v(-0.24, -10.53) * mm});
            skLineSegment(sketch, "E100.33.67", {"start": v(-0.3, -10.75) * mm, "end": v(-0.32, -10.8) * mm});
            skLineSegment(sketch, "E100.33.68", {"start": v(-0.2, -10.44) * mm, "end": v(-0.21, -10.46) * mm});
            skLineSegment(sketch, "E100.33.69", {"start": v(0.28, -10.66) * mm, "end": v(0.3, -10.7) * mm});
            skLineSegment(sketch, "E100.33.70", {"start": v(-0.14, -10.38) * mm, "end": v(-0.15, -10.38) * mm});
            skLineSegment(sketch, "E100.33.71", {"start": v(-0.23, -10.48) * mm, "end": v(-0.23, -10.5) * mm});
            skLineSegment(sketch, "E100.33.72", {"start": v(-0.16, -10.39) * mm, "end": v(-0.16, -10.4) * mm});
            skLineSegment(sketch, "E100.33.73", {"start": v(0.26, -10.61) * mm, "end": v(0.28, -10.66) * mm});
            skLineSegment(sketch, "E100.33.74", {"start": v(0.14, -10.38) * mm, "end": v(0.15, -10.38) * mm});
            skLineSegment(sketch, "E100.33.75", {"start": v(0.13, -10.38) * mm, "end": v(0.14, -10.38) * mm});
            skLineSegment(sketch, "E100.33.76", {"start": v(0.05, -10.37) * mm, "end": v(0.07, -10.37) * mm});
            skLineSegment(sketch, "E100.33.77", {"start": v(-0.2, -10.43) * mm, "end": v(-0.2, -10.44) * mm});
            skLineSegment(sketch, "E100.33.78", {"start": v(0.21, -10.46) * mm, "end": v(0.22, -10.47) * mm});
            skLineSegment(sketch, "E100.33.79", {"start": v(-0.25, -10.57) * mm, "end": v(-0.26, -10.61) * mm});
            skLineSegment(sketch, "E100.33.80", {"start": v(-0.16, -10.4) * mm, "end": v(-0.17, -10.4) * mm});
            skLineSegment(sketch, "E100.33.81", {"start": v(0.12, -10.37) * mm, "end": v(0.13, -10.38) * mm});
            skLineSegment(sketch, "E100.33.82", {"start": v(-0.25, -10.55) * mm, "end": v(-0.25, -10.57) * mm});
            skLineSegment(sketch, "E100.33.83", {"start": v(0.02, -10.37) * mm, "end": v(0.05, -10.37) * mm});
            skLineSegment(sketch, "E100.33.84", {"start": v(0.23, -10.48) * mm, "end": v(0.23, -10.5) * mm});
            skLineSegment(sketch, "E100.33.85", {"start": v(-0.19, -10.41) * mm, "end": v(-0.2, -10.42) * mm});
            skLineSegment(sketch, "E100.33.86", {"start": v(0, -10.38) * mm, "end": v(0.02, -10.37) * mm});
            skLineSegment(sketch, "E100.33.87", {"start": v(0.24, -10.53) * mm, "end": v(0.25, -10.55) * mm});
            skLineSegment(sketch, "E100.33.88", {"start": v(0.12, -10.37) * mm, "end": v(0.12, -10.37) * mm});
            skLineSegment(sketch, "E100.33.89", {"start": v(0.1, -10.37) * mm, "end": v(0.12, -10.37) * mm});
            skLineSegment(sketch, "E100.33.90", {"start": v(-0.12, -10.37) * mm, "end": v(-0.12, -10.37) * mm});
            skLineSegment(sketch, "E100.33.91", {"start": v(-0.15, -10.38) * mm, "end": v(-0.16, -10.39) * mm});
            skLineSegment(sketch, "E100.33.92", {"start": v(-0.18, -10.4) * mm, "end": v(-0.19, -10.41) * mm});
            skLineSegment(sketch, "E100.33.93", {"start": v(-0.05, -10.37) * mm, "end": v(-0.07, -10.37) * mm});
            skLineSegment(sketch, "E100.33.94", {"start": v(0.07, -10.37) * mm, "end": v(0.1, -10.37) * mm});
            skLineSegment(sketch, "E100.33.95", {"start": v(0.19, -10.41) * mm, "end": v(0.2, -10.42) * mm});
            skLineSegment(sketch, "E100.33.96", {"start": v(-0.13, -10.38) * mm, "end": v(-0.14, -10.38) * mm});
            skLineSegment(sketch, "E100.33.97", {"start": v(0.18, -10.4) * mm, "end": v(0.19, -10.41) * mm});
            skLineSegment(sketch, "E100.33.98", {"start": v(0.2, -10.42) * mm, "end": v(0.2, -10.43) * mm});
            skLineSegment(sketch, "E100.33.99", {"start": v(0.2, -10.43) * mm, "end": v(0.2, -10.44) * mm});
            skLineSegment(sketch, "E100.34.0", {"start": v(0.97, -11.46) * mm, "end": v(0.94, -11.46) * mm});
            skLineSegment(sketch, "E100.34.1", {"start": v(2.33, -11.26) * mm, "end": v(2.37, -11.25) * mm});
            skLineSegment(sketch, "E100.34.2", {"start": v(2.17, -11.15) * mm, "end": v(2.2, -11.2) * mm});
            skLineSegment(sketch, "E100.34.3", {"start": v(2.4, -11.25) * mm, "end": v(2.44, -11.24) * mm});
            skLineSegment(sketch, "E100.34.4", {"start": v(1.15, -11.02) * mm, "end": v(1.14, -11.07) * mm});
            skLineSegment(sketch, "E100.34.5", {"start": v(0.9, -11.46) * mm, "end": v(0.86, -11.47) * mm});
            skLineSegment(sketch, "E100.34.6", {"start": v(2.3, -11.27) * mm, "end": v(2.33, -11.26) * mm});
            skLineSegment(sketch, "E100.34.7", {"start": v(1.08, -11.26) * mm, "end": v(1.06, -11.31) * mm});
            skLineSegment(sketch, "E100.34.8", {"start": v(2.37, -11.25) * mm, "end": v(2.4, -11.25) * mm});
            skLineSegment(sketch, "E100.34.9", {"start": v(1.06, -11.31) * mm, "end": v(1.05, -11.36) * mm});
            skLineSegment(sketch, "E100.34.10", {"start": v(0.86, -11.47) * mm, "end": v(0.82, -11.47) * mm});
            skLineSegment(sketch, "E100.34.11", {"start": v(1.05, -11.36) * mm, "end": v(1.03, -11.4) * mm});
            skLineSegment(sketch, "E100.34.12", {"start": v(1.1, -11.21) * mm, "end": v(1.08, -11.26) * mm});
            skLineSegment(sketch, "E100.34.13", {"start": v(2.23, -11.24) * mm, "end": v(2.26, -11.28) * mm});
            skLineSegment(sketch, "E100.34.14", {"start": v(1.01, -11.46) * mm, "end": v(0.97, -11.46) * mm});
            skLineSegment(sketch, "E100.34.15", {"start": v(1.14, -11.07) * mm, "end": v(1.13, -11.12) * mm});
            skLineSegment(sketch, "E100.34.16", {"start": v(0.94, -11.46) * mm, "end": v(0.9, -11.46) * mm});
            skLineSegment(sketch, "E100.34.17", {"start": v(2.26, -11.28) * mm, "end": v(2.3, -11.27) * mm});
            skLineSegment(sketch, "E100.34.18", {"start": v(2.1, -11.07) * mm, "end": v(2.14, -11.11) * mm});
            skLineSegment(sketch, "E100.34.19", {"start": v(1.11, -11.17) * mm, "end": v(1.1, -11.21) * mm});
            skLineSegment(sketch, "E100.34.20", {"start": v(1.03, -11.4) * mm, "end": v(1.01, -11.46) * mm});
            skLineSegment(sketch, "E100.34.21", {"start": v(2.02, -10.94) * mm, "end": v(2.05, -10.98) * mm});
            skLineSegment(sketch, "E100.34.22", {"start": v(2.14, -11.11) * mm, "end": v(2.17, -11.15) * mm});
            skLineSegment(sketch, "E100.34.23", {"start": v(1.13, -11.12) * mm, "end": v(1.11, -11.17) * mm});
            skLineSegment(sketch, "E100.34.24", {"start": v(2.05, -10.98) * mm, "end": v(2.08, -11.03) * mm});
            skLineSegment(sketch, "E100.34.25", {"start": v(2.08, -11.03) * mm, "end": v(2.1, -11.07) * mm});
            skLineSegment(sketch, "E100.34.26", {"start": v(2.2, -11.2) * mm, "end": v(2.23, -11.24) * mm});
            skLineSegment(sketch, "E100.34.27", {"start": v(2, -10.9) * mm, "end": v(2.02, -10.94) * mm});
            skLineSegment(sketch, "E100.34.28", {"start": v(1.7, -10.3) * mm, "end": v(1.7, -10.32) * mm});
            skLineSegment(sketch, "E100.34.29", {"start": v(1.81, -10.55) * mm, "end": v(1.83, -10.6) * mm});
            skLineSegment(sketch, "E100.34.30", {"start": v(1.88, -10.69) * mm, "end": v(1.9, -10.73) * mm});
            skLineSegment(sketch, "E100.34.31", {"start": v(1.27, -10.4) * mm, "end": v(1.27, -10.4) * mm});
            skLineSegment(sketch, "E100.34.32", {"start": v(1.17, -10.97) * mm, "end": v(1.15, -11.02) * mm});
            skLineSegment(sketch, "E100.34.33", {"start": v(1.65, -10.27) * mm, "end": v(1.66, -10.27) * mm});
            skLineSegment(sketch, "E100.34.34", {"start": v(1.31, -10.32) * mm, "end": v(1.3, -10.32) * mm});
            skLineSegment(sketch, "E100.34.35", {"start": v(1.7, -10.33) * mm, "end": v(1.72, -10.34) * mm});
            skLineSegment(sketch, "E100.34.36", {"start": v(1.75, -10.42) * mm, "end": v(1.77, -10.47) * mm});
            skLineSegment(sketch, "E100.34.37", {"start": v(1.2, -10.88) * mm, "end": v(1.18, -10.92) * mm});
            skLineSegment(sketch, "E100.34.38", {"start": v(1.24, -10.59) * mm, "end": v(1.24, -10.64) * mm});
            skLineSegment(sketch, "E100.34.39", {"start": v(1.22, -10.73) * mm, "end": v(1.21, -10.78) * mm});
            skLineSegment(sketch, "E100.34.40", {"start": v(1.48, -10.27) * mm, "end": v(1.45, -10.27) * mm});
            skLineSegment(sketch, "E100.34.41", {"start": v(1.45, -10.27) * mm, "end": v(1.43, -10.28) * mm});
            skLineSegment(sketch, "E100.34.42", {"start": v(1.92, -10.77) * mm, "end": v(1.95, -10.81) * mm});
            skLineSegment(sketch, "E100.34.43", {"start": v(1.9, -10.73) * mm, "end": v(1.92, -10.77) * mm});
            skLineSegment(sketch, "E100.34.44", {"start": v(1.18, -10.92) * mm, "end": v(1.17, -10.97) * mm});
            skLineSegment(sketch, "E100.34.45", {"start": v(1.3, -10.34) * mm, "end": v(1.29, -10.35) * mm});
            skLineSegment(sketch, "E100.34.46", {"start": v(1.35, -10.29) * mm, "end": v(1.35, -10.29) * mm});
            skLineSegment(sketch, "E100.34.47", {"start": v(1.21, -10.78) * mm, "end": v(1.2, -10.83) * mm});
            skLineSegment(sketch, "E100.34.48", {"start": v(1.97, -10.86) * mm, "end": v(2, -10.9) * mm});
            skLineSegment(sketch, "E100.34.49", {"start": v(1.72, -10.36) * mm, "end": v(1.73, -10.37) * mm});
            skLineSegment(sketch, "E100.34.50", {"start": v(1.2, -10.83) * mm, "end": v(1.2, -10.88) * mm});
            skLineSegment(sketch, "E100.34.51", {"start": v(1.25, -10.54) * mm, "end": v(1.24, -10.59) * mm});
            skLineSegment(sketch, "E100.34.52", {"start": v(1.64, -10.26) * mm, "end": v(1.65, -10.27) * mm});
            skLineSegment(sketch, "E100.34.53", {"start": v(1.85, -10.64) * mm, "end": v(1.88, -10.69) * mm});
            skLineSegment(sketch, "E100.34.54", {"start": v(1.26, -10.42) * mm, "end": v(1.26, -10.44) * mm});
            skLineSegment(sketch, "E100.34.55", {"start": v(1.38, -10.28) * mm, "end": v(1.36, -10.29) * mm});
            skLineSegment(sketch, "E100.34.56", {"start": v(1.28, -10.38) * mm, "end": v(1.27, -10.4) * mm});
            skLineSegment(sketch, "E100.34.57", {"start": v(1.63, -10.26) * mm, "end": v(1.64, -10.26) * mm});
            skLineSegment(sketch, "E100.34.58", {"start": v(1.26, -10.46) * mm, "end": v(1.26, -10.48) * mm});
            skLineSegment(sketch, "E100.34.59", {"start": v(1.73, -10.37) * mm, "end": v(1.74, -10.39) * mm});
            skLineSegment(sketch, "E100.34.60", {"start": v(1.24, -10.64) * mm, "end": v(1.23, -10.69) * mm});
            skLineSegment(sketch, "E100.34.61", {"start": v(1.95, -10.81) * mm, "end": v(1.97, -10.86) * mm});
            skLineSegment(sketch, "E100.34.62", {"start": v(1.83, -10.6) * mm, "end": v(1.85, -10.64) * mm});
            skLineSegment(sketch, "E100.34.63", {"start": v(1.75, -10.4) * mm, "end": v(1.75, -10.42) * mm});
            skLineSegment(sketch, "E100.34.64", {"start": v(1.62, -10.26) * mm, "end": v(1.63, -10.26) * mm});
            skLineSegment(sketch, "E100.34.65", {"start": v(1.4, -10.28) * mm, "end": v(1.38, -10.28) * mm});
            skLineSegment(sketch, "E100.34.66", {"start": v(1.26, -10.44) * mm, "end": v(1.26, -10.46) * mm});
            skLineSegment(sketch, "E100.34.67", {"start": v(1.23, -10.69) * mm, "end": v(1.22, -10.73) * mm});
            skLineSegment(sketch, "E100.34.68", {"start": v(1.28, -10.37) * mm, "end": v(1.28, -10.38) * mm});
            skLineSegment(sketch, "E100.34.69", {"start": v(1.8, -10.51) * mm, "end": v(1.81, -10.55) * mm});
            skLineSegment(sketch, "E100.34.70", {"start": v(1.34, -10.3) * mm, "end": v(1.33, -10.3) * mm});
            skLineSegment(sketch, "E100.34.71", {"start": v(1.27, -10.4) * mm, "end": v(1.26, -10.42) * mm});
            skLineSegment(sketch, "E100.34.72", {"start": v(1.32, -10.3) * mm, "end": v(1.32, -10.3) * mm});
            skLineSegment(sketch, "E100.34.73", {"start": v(1.77, -10.47) * mm, "end": v(1.8, -10.51) * mm});
            skLineSegment(sketch, "E100.34.74", {"start": v(1.62, -10.25) * mm, "end": v(1.62, -10.26) * mm});
            skLineSegment(sketch, "E100.34.75", {"start": v(1.6, -10.25) * mm, "end": v(1.62, -10.25) * mm});
            skLineSegment(sketch, "E100.34.76", {"start": v(1.52, -10.26) * mm, "end": v(1.55, -10.26) * mm});
            skLineSegment(sketch, "E100.34.77", {"start": v(1.29, -10.35) * mm, "end": v(1.28, -10.37) * mm});
            skLineSegment(sketch, "E100.34.78", {"start": v(1.7, -10.32) * mm, "end": v(1.7, -10.33) * mm});
            skLineSegment(sketch, "E100.34.79", {"start": v(1.25, -10.5) * mm, "end": v(1.25, -10.54) * mm});
            skLineSegment(sketch, "E100.34.80", {"start": v(1.32, -10.3) * mm, "end": v(1.31, -10.32) * mm});
            skLineSegment(sketch, "E100.34.81", {"start": v(1.6, -10.25) * mm, "end": v(1.6, -10.25) * mm});
            skLineSegment(sketch, "E100.34.82", {"start": v(1.26, -10.48) * mm, "end": v(1.25, -10.5) * mm});
            skLineSegment(sketch, "E100.34.83", {"start": v(1.5, -10.27) * mm, "end": v(1.52, -10.26) * mm});
            skLineSegment(sketch, "E100.34.84", {"start": v(1.72, -10.34) * mm, "end": v(1.72, -10.36) * mm});
            skLineSegment(sketch, "E100.34.85", {"start": v(1.3, -10.33) * mm, "end": v(1.3, -10.34) * mm});
            skLineSegment(sketch, "E100.34.86", {"start": v(1.48, -10.27) * mm, "end": v(1.5, -10.27) * mm});
            skLineSegment(sketch, "E100.34.87", {"start": v(1.74, -10.39) * mm, "end": v(1.75, -10.4) * mm});
            skLineSegment(sketch, "E100.34.88", {"start": v(1.6, -10.25) * mm, "end": v(1.6, -10.25) * mm});
            skLineSegment(sketch, "E100.34.89", {"start": v(1.57, -10.26) * mm, "end": v(1.6, -10.25) * mm});
            skLineSegment(sketch, "E100.34.90", {"start": v(1.36, -10.29) * mm, "end": v(1.35, -10.29) * mm});
            skLineSegment(sketch, "E100.34.91", {"start": v(1.33, -10.3) * mm, "end": v(1.32, -10.3) * mm});
            skLineSegment(sketch, "E100.34.92", {"start": v(1.3, -10.32) * mm, "end": v(1.3, -10.33) * mm});
            skLineSegment(sketch, "E100.34.93", {"start": v(1.43, -10.28) * mm, "end": v(1.4, -10.28) * mm});
            skLineSegment(sketch, "E100.34.94", {"start": v(1.55, -10.26) * mm, "end": v(1.57, -10.26) * mm});
            skLineSegment(sketch, "E100.34.95", {"start": v(1.67, -10.28) * mm, "end": v(1.67, -10.29) * mm});
            skLineSegment(sketch, "E100.34.96", {"start": v(1.35, -10.29) * mm, "end": v(1.34, -10.3) * mm});
            skLineSegment(sketch, "E100.34.97", {"start": v(1.66, -10.27) * mm, "end": v(1.67, -10.28) * mm});
            skLineSegment(sketch, "E100.34.98", {"start": v(1.67, -10.29) * mm, "end": v(1.68, -10.3) * mm});
            skLineSegment(sketch, "E100.34.99", {"start": v(1.68, -10.3) * mm, "end": v(1.7, -10.3) * mm});
            skLineSegment(sketch, "E100.35.0", {"start": v(2.6, -11.2) * mm, "end": v(2.56, -11.21) * mm});
            skLineSegment(sketch, "E100.35.1", {"start": v(3.91, -10.81) * mm, "end": v(3.95, -10.8) * mm});
            skLineSegment(sketch, "E100.35.2", {"start": v(3.73, -10.73) * mm, "end": v(3.77, -10.77) * mm});
            skLineSegment(sketch, "E100.35.3", {"start": v(3.98, -10.79) * mm, "end": v(4.02, -10.77) * mm});
            skLineSegment(sketch, "E100.35.4", {"start": v(2.71, -10.74) * mm, "end": v(2.7, -10.8) * mm});
            skLineSegment(sketch, "E100.35.5", {"start": v(2.52, -11.22) * mm, "end": v(2.48, -11.23) * mm});
            skLineSegment(sketch, "E100.35.6", {"start": v(3.87, -10.83) * mm, "end": v(3.91, -10.81) * mm});
            skLineSegment(sketch, "E100.35.7", {"start": v(2.67, -11) * mm, "end": v(2.66, -11.04) * mm});
            skLineSegment(sketch, "E100.35.8", {"start": v(3.95, -10.8) * mm, "end": v(3.98, -10.79) * mm});
            skLineSegment(sketch, "E100.35.9", {"start": v(2.66, -11.04) * mm, "end": v(2.65, -11.1) * mm});
            skLineSegment(sketch, "E100.35.10", {"start": v(2.48, -11.23) * mm, "end": v(2.44, -11.24) * mm});
            skLineSegment(sketch, "E100.35.11", {"start": v(2.65, -11.1) * mm, "end": v(2.64, -11.14) * mm});
            skLineSegment(sketch, "E100.35.12", {"start": v(2.68, -10.94) * mm, "end": v(2.67, -11) * mm});
            skLineSegment(sketch, "E100.35.13", {"start": v(3.8, -10.8) * mm, "end": v(3.84, -10.84) * mm});
            skLineSegment(sketch, "E100.35.14", {"start": v(2.63, -11.2) * mm, "end": v(2.6, -11.2) * mm});
            skLineSegment(sketch, "E100.35.15", {"start": v(2.7, -10.8) * mm, "end": v(2.7, -10.84) * mm});
            skLineSegment(sketch, "E100.35.16", {"start": v(2.56, -11.21) * mm, "end": v(2.52, -11.22) * mm});
            skLineSegment(sketch, "E100.35.17", {"start": v(3.84, -10.84) * mm, "end": v(3.87, -10.83) * mm});
            skLineSegment(sketch, "E100.35.18", {"start": v(3.66, -10.66) * mm, "end": v(3.7, -10.7) * mm});
            skLineSegment(sketch, "E100.35.19", {"start": v(2.69, -10.9) * mm, "end": v(2.68, -10.94) * mm});
            skLineSegment(sketch, "E100.35.20", {"start": v(2.64, -11.14) * mm, "end": v(2.63, -11.2) * mm});
            skLineSegment(sketch, "E100.35.21", {"start": v(3.56, -10.54) * mm, "end": v(3.6, -10.58) * mm});
            skLineSegment(sketch, "E100.35.22", {"start": v(3.7, -10.7) * mm, "end": v(3.73, -10.73) * mm});
            skLineSegment(sketch, "E100.35.23", {"start": v(2.7, -10.84) * mm, "end": v(2.69, -10.9) * mm});
            skLineSegment(sketch, "E100.35.24", {"start": v(3.6, -10.58) * mm, "end": v(3.63, -10.62) * mm});
            skLineSegment(sketch, "E100.35.25", {"start": v(3.63, -10.62) * mm, "end": v(3.66, -10.66) * mm});
            skLineSegment(sketch, "E100.35.26", {"start": v(3.77, -10.77) * mm, "end": v(3.8, -10.8) * mm});
            skLineSegment(sketch, "E100.35.27", {"start": v(3.53, -10.5) * mm, "end": v(3.56, -10.54) * mm});
            skLineSegment(sketch, "E100.35.28", {"start": v(3.14, -9.96) * mm, "end": v(3.15, -9.97) * mm});
            skLineSegment(sketch, "E100.35.29", {"start": v(3.3, -10.19) * mm, "end": v(3.32, -10.23) * mm});
            skLineSegment(sketch, "E100.35.30", {"start": v(3.38, -10.3) * mm, "end": v(3.4, -10.35) * mm});
            skLineSegment(sketch, "E100.35.31", {"start": v(2.74, -10.1) * mm, "end": v(2.74, -10.12) * mm});
            skLineSegment(sketch, "E100.35.32", {"start": v(2.72, -10.7) * mm, "end": v(2.71, -10.74) * mm});
            skLineSegment(sketch, "E100.35.33", {"start": v(3.1, -9.93) * mm, "end": v(3.1, -9.93) * mm});
            skLineSegment(sketch, "E100.35.34", {"start": v(2.76, -10.02) * mm, "end": v(2.76, -10.03) * mm});
            skLineSegment(sketch, "E100.35.35", {"start": v(3.16, -9.98) * mm, "end": v(3.17, -10) * mm});
            skLineSegment(sketch, "E100.35.36", {"start": v(3.22, -10.07) * mm, "end": v(3.24, -10.1) * mm});
            skLineSegment(sketch, "E100.35.37", {"start": v(2.73, -10.6) * mm, "end": v(2.72, -10.65) * mm});
            skLineSegment(sketch, "E100.35.38", {"start": v(2.74, -10.3) * mm, "end": v(2.74, -10.35) * mm});
            skLineSegment(sketch, "E100.35.39", {"start": v(2.73, -10.45) * mm, "end": v(2.73, -10.5) * mm});
            skLineSegment(sketch, "E100.35.40", {"start": v(2.92, -9.95) * mm, "end": v(2.9, -9.96) * mm});
            skLineSegment(sketch, "E100.35.41", {"start": v(2.9, -9.96) * mm, "end": v(2.88, -9.97) * mm});
            skLineSegment(sketch, "E100.35.42", {"start": v(3.44, -10.39) * mm, "end": v(3.47, -10.43) * mm});
            skLineSegment(sketch, "E100.35.43", {"start": v(3.4, -10.35) * mm, "end": v(3.44, -10.39) * mm});
            skLineSegment(sketch, "E100.35.44", {"start": v(2.72, -10.65) * mm, "end": v(2.72, -10.7) * mm});
            skLineSegment(sketch, "E100.35.45", {"start": v(2.75, -10.05) * mm, "end": v(2.75, -10.07) * mm});
            skLineSegment(sketch, "E100.35.46", {"start": v(2.8, -9.99) * mm, "end": v(2.8, -10) * mm});
            skLineSegment(sketch, "E100.35.47", {"start": v(2.73, -10.5) * mm, "end": v(2.73, -10.55) * mm});
            skLineSegment(sketch, "E100.35.48", {"start": v(3.5, -10.47) * mm, "end": v(3.53, -10.5) * mm});
            skLineSegment(sketch, "E100.35.49", {"start": v(3.18, -10) * mm, "end": v(3.2, -10.02) * mm});
            skLineSegment(sketch, "E100.35.50", {"start": v(2.73, -10.55) * mm, "end": v(2.73, -10.6) * mm});
            skLineSegment(sketch, "E100.35.51", {"start": v(2.74, -10.26) * mm, "end": v(2.74, -10.3) * mm});
            skLineSegment(sketch, "E100.35.52", {"start": v(3.08, -9.92) * mm, "end": v(3.1, -9.93) * mm});
            skLineSegment(sketch, "E100.35.53", {"start": v(3.35, -10.27) * mm, "end": v(3.38, -10.3) * mm});
            skLineSegment(sketch, "E100.35.54", {"start": v(2.73, -10.14) * mm, "end": v(2.73, -10.15) * mm});
            skLineSegment(sketch, "E100.35.55", {"start": v(2.83, -9.98) * mm, "end": v(2.81, -9.99) * mm});
            skLineSegment(sketch, "E100.35.56", {"start": v(2.74, -10.1) * mm, "end": v(2.74, -10.1) * mm});
            skLineSegment(sketch, "E100.35.57", {"start": v(3.08, -9.92) * mm, "end": v(3.08, -9.92) * mm});
            skLineSegment(sketch, "E100.35.58", {"start": v(2.73, -10.17) * mm, "end": v(2.73, -10.2) * mm});
            skLineSegment(sketch, "E100.35.59", {"start": v(3.2, -10.02) * mm, "end": v(3.2, -10.03) * mm});
            skLineSegment(sketch, "E100.35.60", {"start": v(2.74, -10.35) * mm, "end": v(2.74, -10.4) * mm});
            skLineSegment(sketch, "E100.35.61", {"start": v(3.47, -10.43) * mm, "end": v(3.5, -10.47) * mm});
            skLineSegment(sketch, "E100.35.62", {"start": v(3.32, -10.23) * mm, "end": v(3.35, -10.27) * mm});
            skLineSegment(sketch, "E100.35.63", {"start": v(3.2, -10.05) * mm, "end": v(3.22, -10.07) * mm});
            skLineSegment(sketch, "E100.35.64", {"start": v(3.07, -9.92) * mm, "end": v(3.08, -9.92) * mm});
            skLineSegment(sketch, "E100.35.65", {"start": v(2.86, -9.97) * mm, "end": v(2.83, -9.98) * mm});
            skLineSegment(sketch, "E100.35.66", {"start": v(2.73, -10.15) * mm, "end": v(2.73, -10.17) * mm});
            skLineSegment(sketch, "E100.35.67", {"start": v(2.74, -10.4) * mm, "end": v(2.73, -10.45) * mm});
            skLineSegment(sketch, "E100.35.68", {"start": v(2.74, -10.08) * mm, "end": v(2.74, -10.1) * mm});
            skLineSegment(sketch, "E100.35.69", {"start": v(3.27, -10.15) * mm, "end": v(3.3, -10.19) * mm});
            skLineSegment(sketch, "E100.35.70", {"start": v(2.79, -10) * mm, "end": v(2.78, -10) * mm});
            skLineSegment(sketch, "E100.35.71", {"start": v(2.74, -10.12) * mm, "end": v(2.73, -10.14) * mm});
            skLineSegment(sketch, "E100.35.72", {"start": v(2.78, -10) * mm, "end": v(2.77, -10.02) * mm});
            skLineSegment(sketch, "E100.35.73", {"start": v(3.24, -10.1) * mm, "end": v(3.27, -10.15) * mm});
            skLineSegment(sketch, "E100.35.74", {"start": v(3.06, -9.92) * mm, "end": v(3.07, -9.92) * mm});
            skLineSegment(sketch, "E100.35.75", {"start": v(3.05, -9.92) * mm, "end": v(3.06, -9.92) * mm});
            skLineSegment(sketch, "E100.35.76", {"start": v(2.97, -9.94) * mm, "end": v(3, -9.93) * mm});
            skLineSegment(sketch, "E100.35.77", {"start": v(2.75, -10.07) * mm, "end": v(2.74, -10.08) * mm});
            skLineSegment(sketch, "E100.35.78", {"start": v(3.15, -9.97) * mm, "end": v(3.16, -9.98) * mm});
            skLineSegment(sketch, "E100.35.79", {"start": v(2.73, -10.2) * mm, "end": v(2.74, -10.26) * mm});
            skLineSegment(sketch, "E100.35.80", {"start": v(2.77, -10.02) * mm, "end": v(2.76, -10.02) * mm});
            skLineSegment(sketch, "E100.35.81", {"start": v(3.04, -9.92) * mm, "end": v(3.05, -9.92) * mm});
            skLineSegment(sketch, "E100.35.82", {"start": v(2.73, -10.2) * mm, "end": v(2.73, -10.2) * mm});
            skLineSegment(sketch, "E100.35.83", {"start": v(2.95, -9.95) * mm, "end": v(2.97, -9.94) * mm});
            skLineSegment(sketch, "E100.35.84", {"start": v(3.17, -10) * mm, "end": v(3.18, -10) * mm});
            skLineSegment(sketch, "E100.35.85", {"start": v(2.76, -10.04) * mm, "end": v(2.75, -10.05) * mm});
            skLineSegment(sketch, "E100.35.86", {"start": v(2.92, -9.95) * mm, "end": v(2.95, -9.95) * mm});
            skLineSegment(sketch, "E100.35.87", {"start": v(3.2, -10.03) * mm, "end": v(3.2, -10.05) * mm});
            skLineSegment(sketch, "E100.35.88", {"start": v(3.03, -9.92) * mm, "end": v(3.04, -9.92) * mm});
            skLineSegment(sketch, "E100.35.89", {"start": v(3.01, -9.93) * mm, "end": v(3.03, -9.92) * mm});
            skLineSegment(sketch, "E100.35.90", {"start": v(2.81, -9.99) * mm, "end": v(2.8, -9.99) * mm});
            skLineSegment(sketch, "E100.35.91", {"start": v(2.78, -10) * mm, "end": v(2.78, -10) * mm});
            skLineSegment(sketch, "E100.35.92", {"start": v(2.76, -10.03) * mm, "end": v(2.76, -10.04) * mm});
            skLineSegment(sketch, "E100.35.93", {"start": v(2.88, -9.97) * mm, "end": v(2.86, -9.97) * mm});
            skLineSegment(sketch, "E100.35.94", {"start": v(3, -9.93) * mm, "end": v(3.01, -9.93) * mm});
            skLineSegment(sketch, "E100.35.95", {"start": v(3.11, -9.94) * mm, "end": v(3.12, -9.95) * mm});
            skLineSegment(sketch, "E100.35.96", {"start": v(2.8, -10) * mm, "end": v(2.79, -10) * mm});
            skLineSegment(sketch, "E100.35.97", {"start": v(3.1, -9.93) * mm, "end": v(3.11, -9.94) * mm});
            skLineSegment(sketch, "E100.35.98", {"start": v(3.12, -9.95) * mm, "end": v(3.13, -9.95) * mm});
            skLineSegment(sketch, "E100.35.99", {"start": v(3.13, -9.95) * mm, "end": v(3.14, -9.96) * mm});
            skLineSegment(sketch, "E100.36.0", {"start": v(4.16, -10.72) * mm, "end": v(4.13, -10.73) * mm});
            skLineSegment(sketch, "E100.36.1", {"start": v(5.41, -10.15) * mm, "end": v(5.44, -10.13) * mm});
            skLineSegment(sketch, "E100.36.2", {"start": v(5.22, -10.1) * mm, "end": v(5.26, -10.12) * mm});
            skLineSegment(sketch, "E100.36.3", {"start": v(5.48, -10.11) * mm, "end": v(5.51, -10.1) * mm});
            skLineSegment(sketch, "E100.36.4", {"start": v(4.21, -10.25) * mm, "end": v(4.21, -10.3) * mm});
            skLineSegment(sketch, "E100.36.5", {"start": v(4.1, -10.75) * mm, "end": v(4.05, -10.76) * mm});
            skLineSegment(sketch, "E100.36.6", {"start": v(5.38, -10.17) * mm, "end": v(5.41, -10.15) * mm});
            skLineSegment(sketch, "E100.36.7", {"start": v(4.21, -10.5) * mm, "end": v(4.2, -10.55) * mm});
            skLineSegment(sketch, "E100.36.8", {"start": v(5.44, -10.13) * mm, "end": v(5.48, -10.11) * mm});
            skLineSegment(sketch, "E100.36.9", {"start": v(4.2, -10.55) * mm, "end": v(4.2, -10.6) * mm});
            skLineSegment(sketch, "E100.36.10", {"start": v(4.05, -10.76) * mm, "end": v(4.02, -10.77) * mm});
            skLineSegment(sketch, "E100.36.11", {"start": v(4.2, -10.6) * mm, "end": v(4.2, -10.65) * mm});
            skLineSegment(sketch, "E100.36.12", {"start": v(4.21, -10.45) * mm, "end": v(4.21, -10.5) * mm});
            skLineSegment(sketch, "E100.36.13", {"start": v(5.3, -10.15) * mm, "end": v(5.34, -10.18) * mm});
            skLineSegment(sketch, "E100.36.14", {"start": v(4.2, -10.7) * mm, "end": v(4.16, -10.72) * mm});
            skLineSegment(sketch, "E100.36.15", {"start": v(4.21, -10.3) * mm, "end": v(4.21, -10.35) * mm});
            skLineSegment(sketch, "E100.36.16", {"start": v(4.13, -10.73) * mm, "end": v(4.1, -10.75) * mm});
            skLineSegment(sketch, "E100.36.17", {"start": v(5.34, -10.18) * mm, "end": v(5.38, -10.17) * mm});
            skLineSegment(sketch, "E100.36.18", {"start": v(5.14, -10.03) * mm, "end": v(5.18, -10.06) * mm});
            skLineSegment(sketch, "E100.36.19", {"start": v(4.21, -10.4) * mm, "end": v(4.21, -10.45) * mm});
            skLineSegment(sketch, "E100.36.20", {"start": v(4.2, -10.65) * mm, "end": v(4.2, -10.7) * mm});
            skLineSegment(sketch, "E100.36.21", {"start": v(5.02, -9.93) * mm, "end": v(5.06, -9.96) * mm});
            skLineSegment(sketch, "E100.36.22", {"start": v(5.18, -10.06) * mm, "end": v(5.22, -10.1) * mm});
            skLineSegment(sketch, "E100.36.23", {"start": v(4.21, -10.35) * mm, "end": v(4.21, -10.4) * mm});
            skLineSegment(sketch, "E100.36.24", {"start": v(5.06, -9.96) * mm, "end": v(5.1, -10) * mm});
            skLineSegment(sketch, "E100.36.25", {"start": v(5.1, -10) * mm, "end": v(5.14, -10.03) * mm});
            skLineSegment(sketch, "E100.36.26", {"start": v(5.26, -10.12) * mm, "end": v(5.3, -10.15) * mm});
            skLineSegment(sketch, "E100.36.27", {"start": v(4.99, -9.9) * mm, "end": v(5.02, -9.93) * mm});
            skLineSegment(sketch, "E100.36.28", {"start": v(4.53, -9.41) * mm, "end": v(4.54, -9.42) * mm});
            skLineSegment(sketch, "E100.36.29", {"start": v(4.71, -9.62) * mm, "end": v(4.74, -9.65) * mm});
            skLineSegment(sketch, "E100.36.30", {"start": v(4.8, -9.72) * mm, "end": v(4.84, -9.76) * mm});
            skLineSegment(sketch, "E100.36.31", {"start": v(4.15, -9.61) * mm, "end": v(4.15, -9.63) * mm});
            skLineSegment(sketch, "E100.36.32", {"start": v(4.21, -10.2) * mm, "end": v(4.21, -10.25) * mm});
            skLineSegment(sketch, "E100.36.33", {"start": v(4.48, -9.39) * mm, "end": v(4.48, -9.4) * mm});
            skLineSegment(sketch, "E100.36.34", {"start": v(4.16, -9.53) * mm, "end": v(4.16, -9.54) * mm});
            skLineSegment(sketch, "E100.36.35", {"start": v(4.55, -9.43) * mm, "end": v(4.56, -9.44) * mm});
            skLineSegment(sketch, "E100.36.36", {"start": v(4.62, -9.5) * mm, "end": v(4.65, -9.54) * mm});
            skLineSegment(sketch, "E100.36.37", {"start": v(4.2, -10.1) * mm, "end": v(4.2, -10.15) * mm});
            skLineSegment(sketch, "E100.36.38", {"start": v(4.18, -9.81) * mm, "end": v(4.18, -9.86) * mm});
            skLineSegment(sketch, "E100.36.39", {"start": v(4.2, -9.95) * mm, "end": v(4.2, -10) * mm});
            skLineSegment(sketch, "E100.36.40", {"start": v(4.3, -9.44) * mm, "end": v(4.29, -9.45) * mm});
            skLineSegment(sketch, "E100.36.41", {"start": v(4.29, -9.45) * mm, "end": v(4.27, -9.46) * mm});
            skLineSegment(sketch, "E100.36.42", {"start": v(4.88, -9.8) * mm, "end": v(4.91, -9.83) * mm});
            skLineSegment(sketch, "E100.36.43", {"start": v(4.84, -9.76) * mm, "end": v(4.88, -9.8) * mm});
            skLineSegment(sketch, "E100.36.44", {"start": v(4.2, -10.15) * mm, "end": v(4.21, -10.2) * mm});
            skLineSegment(sketch, "E100.36.45", {"start": v(4.15, -9.56) * mm, "end": v(4.15, -9.57) * mm});
            skLineSegment(sketch, "E100.36.46", {"start": v(4.2, -9.49) * mm, "end": v(4.19, -9.5) * mm});
            skLineSegment(sketch, "E100.36.47", {"start": v(4.2, -10) * mm, "end": v(4.2, -10.05) * mm});
            skLineSegment(sketch, "E100.36.48", {"start": v(4.95, -9.86) * mm, "end": v(4.99, -9.9) * mm});
            skLineSegment(sketch, "E100.36.49", {"start": v(4.57, -9.45) * mm, "end": v(4.58, -9.46) * mm});
            skLineSegment(sketch, "E100.36.50", {"start": v(4.2, -10.05) * mm, "end": v(4.2, -10.1) * mm});
            skLineSegment(sketch, "E100.36.51", {"start": v(4.17, -9.76) * mm, "end": v(4.18, -9.81) * mm});
            skLineSegment(sketch, "E100.36.52", {"start": v(4.47, -9.38) * mm, "end": v(4.48, -9.39) * mm});
            skLineSegment(sketch, "E100.36.53", {"start": v(4.78, -9.69) * mm, "end": v(4.8, -9.72) * mm});
            skLineSegment(sketch, "E100.36.54", {"start": v(4.15, -9.65) * mm, "end": v(4.15, -9.66) * mm});
            skLineSegment(sketch, "E100.36.55", {"start": v(4.22, -9.48) * mm, "end": v(4.2, -9.49) * mm});
            skLineSegment(sketch, "E100.36.56", {"start": v(4.15, -9.6) * mm, "end": v(4.15, -9.61) * mm});
            skLineSegment(sketch, "E100.36.57", {"start": v(4.46, -9.38) * mm, "end": v(4.47, -9.38) * mm});
            skLineSegment(sketch, "E100.36.58", {"start": v(4.15, -9.68) * mm, "end": v(4.16, -9.7) * mm});
            skLineSegment(sketch, "E100.36.59", {"start": v(4.58, -9.46) * mm, "end": v(4.6, -9.48) * mm});
            skLineSegment(sketch, "E100.36.60", {"start": v(4.18, -9.86) * mm, "end": v(4.19, -9.9) * mm});
            skLineSegment(sketch, "E100.36.61", {"start": v(4.91, -9.83) * mm, "end": v(4.95, -9.86) * mm});
            skLineSegment(sketch, "E100.36.62", {"start": v(4.74, -9.65) * mm, "end": v(4.78, -9.69) * mm});
            skLineSegment(sketch, "E100.36.63", {"start": v(4.6, -9.5) * mm, "end": v(4.62, -9.5) * mm});
            skLineSegment(sketch, "E100.36.64", {"start": v(4.45, -9.38) * mm, "end": v(4.46, -9.38) * mm});
            skLineSegment(sketch, "E100.36.65", {"start": v(4.25, -9.47) * mm, "end": v(4.22, -9.48) * mm});
            skLineSegment(sketch, "E100.36.66", {"start": v(4.15, -9.66) * mm, "end": v(4.15, -9.68) * mm});
            skLineSegment(sketch, "E100.36.67", {"start": v(4.19, -9.9) * mm, "end": v(4.2, -9.95) * mm});
            skLineSegment(sketch, "E100.36.68", {"start": v(4.15, -9.59) * mm, "end": v(4.15, -9.6) * mm});
            skLineSegment(sketch, "E100.36.69", {"start": v(4.68, -9.58) * mm, "end": v(4.71, -9.62) * mm});
            skLineSegment(sketch, "E100.36.70", {"start": v(4.18, -9.5) * mm, "end": v(4.18, -9.5) * mm});
            skLineSegment(sketch, "E100.36.71", {"start": v(4.15, -9.63) * mm, "end": v(4.15, -9.65) * mm});
            skLineSegment(sketch, "E100.36.72", {"start": v(4.17, -9.51) * mm, "end": v(4.17, -9.52) * mm});
            skLineSegment(sketch, "E100.36.73", {"start": v(4.65, -9.54) * mm, "end": v(4.68, -9.58) * mm});
            skLineSegment(sketch, "E100.36.74", {"start": v(4.44, -9.38) * mm, "end": v(4.45, -9.38) * mm});
            skLineSegment(sketch, "E100.36.75", {"start": v(4.43, -9.38) * mm, "end": v(4.44, -9.38) * mm});
            skLineSegment(sketch, "E100.36.76", {"start": v(4.35, -9.42) * mm, "end": v(4.37, -9.4) * mm});
            skLineSegment(sketch, "E100.36.77", {"start": v(4.15, -9.57) * mm, "end": v(4.15, -9.59) * mm});
            skLineSegment(sketch, "E100.36.78", {"start": v(4.54, -9.42) * mm, "end": v(4.55, -9.43) * mm});
            skLineSegment(sketch, "E100.36.79", {"start": v(4.16, -9.72) * mm, "end": v(4.17, -9.76) * mm});
            skLineSegment(sketch, "E100.36.80", {"start": v(4.17, -9.52) * mm, "end": v(4.16, -9.53) * mm});
            skLineSegment(sketch, "E100.36.81", {"start": v(4.42, -9.39) * mm, "end": v(4.43, -9.38) * mm});
            skLineSegment(sketch, "E100.36.82", {"start": v(4.16, -9.7) * mm, "end": v(4.16, -9.72) * mm});
            skLineSegment(sketch, "E100.36.83", {"start": v(4.33, -9.43) * mm, "end": v(4.35, -9.42) * mm});
            skLineSegment(sketch, "E100.36.84", {"start": v(4.56, -9.44) * mm, "end": v(4.57, -9.45) * mm});
            skLineSegment(sketch, "E100.36.85", {"start": v(4.16, -9.55) * mm, "end": v(4.15, -9.56) * mm});
            skLineSegment(sketch, "E100.36.86", {"start": v(4.3, -9.44) * mm, "end": v(4.33, -9.43) * mm});
            skLineSegment(sketch, "E100.36.87", {"start": v(4.6, -9.48) * mm, "end": v(4.6, -9.5) * mm});
            skLineSegment(sketch, "E100.36.88", {"start": v(4.42, -9.39) * mm, "end": v(4.42, -9.39) * mm});
            skLineSegment(sketch, "E100.36.89", {"start": v(4.4, -9.4) * mm, "end": v(4.42, -9.39) * mm});
            skLineSegment(sketch, "E100.36.90", {"start": v(4.2, -9.49) * mm, "end": v(4.2, -9.49) * mm});
            skLineSegment(sketch, "E100.36.91", {"start": v(4.18, -9.5) * mm, "end": v(4.17, -9.51) * mm});
            skLineSegment(sketch, "E100.36.92", {"start": v(4.16, -9.54) * mm, "end": v(4.16, -9.55) * mm});
            skLineSegment(sketch, "E100.36.93", {"start": v(4.27, -9.46) * mm, "end": v(4.25, -9.47) * mm});
            skLineSegment(sketch, "E100.36.94", {"start": v(4.37, -9.4) * mm, "end": v(4.4, -9.4) * mm});
            skLineSegment(sketch, "E100.36.95", {"start": v(4.5, -9.4) * mm, "end": v(4.5, -9.4) * mm});
            skLineSegment(sketch, "E100.36.96", {"start": v(4.19, -9.5) * mm, "end": v(4.18, -9.5) * mm});
            skLineSegment(sketch, "E100.36.97", {"start": v(4.48, -9.4) * mm, "end": v(4.5, -9.4) * mm});
            skLineSegment(sketch, "E100.36.98", {"start": v(4.5, -9.4) * mm, "end": v(4.52, -9.4) * mm});
            skLineSegment(sketch, "E100.36.99", {"start": v(4.52, -9.4) * mm, "end": v(4.53, -9.41) * mm});
            skLineSegment(sketch, "E100.37.0", {"start": v(5.65, -10.02) * mm, "end": v(5.61, -10.04) * mm});
            skLineSegment(sketch, "E100.37.1", {"start": v(6.8, -9.27) * mm, "end": v(6.83, -9.25) * mm});
            skLineSegment(sketch, "E100.37.2", {"start": v(6.6, -9.24) * mm, "end": v(6.65, -9.27) * mm});
            skLineSegment(sketch, "E100.37.3", {"start": v(6.86, -9.23) * mm, "end": v(6.9, -9.2) * mm});
            skLineSegment(sketch, "E100.37.4", {"start": v(5.63, -9.55) * mm, "end": v(5.64, -9.6) * mm});
            skLineSegment(sketch, "E100.37.5", {"start": v(5.58, -10.06) * mm, "end": v(5.55, -10.07) * mm});
            skLineSegment(sketch, "E100.37.6", {"start": v(6.77, -9.3) * mm, "end": v(6.8, -9.27) * mm});
            skLineSegment(sketch, "E100.37.7", {"start": v(5.66, -9.8) * mm, "end": v(5.67, -9.85) * mm});
            skLineSegment(sketch, "E100.37.8", {"start": v(6.83, -9.25) * mm, "end": v(6.86, -9.23) * mm});
            skLineSegment(sketch, "E100.37.9", {"start": v(5.67, -9.85) * mm, "end": v(5.67, -9.9) * mm});
            skLineSegment(sketch, "E100.37.10", {"start": v(5.55, -10.07) * mm, "end": v(5.51, -10.1) * mm});
            skLineSegment(sketch, "E100.37.11", {"start": v(5.67, -9.9) * mm, "end": v(5.68, -9.95) * mm});
            skLineSegment(sketch, "E100.37.12", {"start": v(5.66, -9.74) * mm, "end": v(5.66, -9.8) * mm});
            skLineSegment(sketch, "E100.37.13", {"start": v(6.7, -9.3) * mm, "end": v(6.74, -9.32) * mm});
            skLineSegment(sketch, "E100.37.14", {"start": v(5.68, -10) * mm, "end": v(5.65, -10.02) * mm});
            skLineSegment(sketch, "E100.37.15", {"start": v(5.64, -9.6) * mm, "end": v(5.64, -9.64) * mm});
            skLineSegment(sketch, "E100.37.16", {"start": v(5.61, -10.04) * mm, "end": v(5.58, -10.06) * mm});
            skLineSegment(sketch, "E100.37.17", {"start": v(6.74, -9.32) * mm, "end": v(6.77, -9.3) * mm});
            skLineSegment(sketch, "E100.37.18", {"start": v(6.51, -9.2) * mm, "end": v(6.56, -9.22) * mm});
            skLineSegment(sketch, "E100.37.19", {"start": v(5.65, -9.7) * mm, "end": v(5.66, -9.74) * mm});
            skLineSegment(sketch, "E100.37.20", {"start": v(5.68, -9.95) * mm, "end": v(5.68, -10) * mm});
            skLineSegment(sketch, "E100.37.21", {"start": v(6.39, -9.11) * mm, "end": v(6.43, -9.14) * mm});
            skLineSegment(sketch, "E100.37.22", {"start": v(6.56, -9.22) * mm, "end": v(6.6, -9.24) * mm});
            skLineSegment(sketch, "E100.37.23", {"start": v(5.64, -9.64) * mm, "end": v(5.65, -9.7) * mm});
            skLineSegment(sketch, "E100.37.24", {"start": v(6.43, -9.14) * mm, "end": v(6.47, -9.17) * mm});
            skLineSegment(sketch, "E100.37.25", {"start": v(6.47, -9.17) * mm, "end": v(6.51, -9.2) * mm});
            skLineSegment(sketch, "E100.37.26", {"start": v(6.65, -9.27) * mm, "end": v(6.7, -9.3) * mm});
            skLineSegment(sketch, "E100.37.27", {"start": v(6.34, -9.08) * mm, "end": v(6.39, -9.11) * mm});
            skLineSegment(sketch, "E100.37.28", {"start": v(5.82, -8.67) * mm, "end": v(5.83, -8.68) * mm});
            skLineSegment(sketch, "E100.37.29", {"start": v(6.03, -8.85) * mm, "end": v(6.07, -8.88) * mm});
            skLineSegment(sketch, "E100.37.30", {"start": v(6.14, -8.94) * mm, "end": v(6.18, -8.97) * mm});
            skLineSegment(sketch, "E100.37.31", {"start": v(5.47, -8.93) * mm, "end": v(5.48, -8.94) * mm});
            skLineSegment(sketch, "E100.37.32", {"start": v(5.62, -9.5) * mm, "end": v(5.63, -9.55) * mm});
            skLineSegment(sketch, "E100.37.33", {"start": v(5.77, -8.65) * mm, "end": v(5.78, -8.66) * mm});
            skLineSegment(sketch, "E100.37.34", {"start": v(5.48, -8.84) * mm, "end": v(5.47, -8.85) * mm});
            skLineSegment(sketch, "E100.37.35", {"start": v(5.84, -8.69) * mm, "end": v(5.86, -8.7) * mm});
            skLineSegment(sketch, "E100.37.36", {"start": v(5.93, -8.75) * mm, "end": v(5.96, -8.78) * mm});
            skLineSegment(sketch, "E100.37.37", {"start": v(5.6, -9.4) * mm, "end": v(5.61, -9.45) * mm});
            skLineSegment(sketch, "E100.37.38", {"start": v(5.53, -9.12) * mm, "end": v(5.54, -9.16) * mm});
            skLineSegment(sketch, "E100.37.39", {"start": v(5.57, -9.26) * mm, "end": v(5.58, -9.3) * mm});
            skLineSegment(sketch, "E100.37.40", {"start": v(5.6, -8.73) * mm, "end": v(5.59, -8.74) * mm});
            skLineSegment(sketch, "E100.37.41", {"start": v(5.59, -8.74) * mm, "end": v(5.57, -8.75) * mm});
            skLineSegment(sketch, "E100.37.42", {"start": v(6.22, -9) * mm, "end": v(6.26, -9.03) * mm});
            skLineSegment(sketch, "E100.37.43", {"start": v(6.18, -8.97) * mm, "end": v(6.22, -9) * mm});
            skLineSegment(sketch, "E100.37.44", {"start": v(5.61, -9.45) * mm, "end": v(5.62, -9.5) * mm});
            skLineSegment(sketch, "E100.37.45", {"start": v(5.47, -8.87) * mm, "end": v(5.47, -8.88) * mm});
            skLineSegment(sketch, "E100.37.46", {"start": v(5.5, -8.8) * mm, "end": v(5.5, -8.8) * mm});
            skLineSegment(sketch, "E100.37.47", {"start": v(5.58, -9.3) * mm, "end": v(5.6, -9.35) * mm});
            skLineSegment(sketch, "E100.37.48", {"start": v(6.3, -9.06) * mm, "end": v(6.34, -9.08) * mm});
            skLineSegment(sketch, "E100.37.49", {"start": v(5.87, -8.7) * mm, "end": v(5.88, -8.72) * mm});
            skLineSegment(sketch, "E100.37.50", {"start": v(5.6, -9.35) * mm, "end": v(5.6, -9.4) * mm});
            skLineSegment(sketch, "E100.37.51", {"start": v(5.51, -9.07) * mm, "end": v(5.53, -9.12) * mm});
            skLineSegment(sketch, "E100.37.52", {"start": v(5.76, -8.65) * mm, "end": v(5.77, -8.65) * mm});
            skLineSegment(sketch, "E100.37.53", {"start": v(6.1, -8.91) * mm, "end": v(6.14, -8.94) * mm});
            skLineSegment(sketch, "E100.37.54", {"start": v(5.48, -8.96) * mm, "end": v(5.48, -8.97) * mm});
            skLineSegment(sketch, "E100.37.55", {"start": v(5.53, -8.78) * mm, "end": v(5.51, -8.8) * mm});
            skLineSegment(sketch, "E100.37.56", {"start": v(5.47, -8.91) * mm, "end": v(5.47, -8.93) * mm});
            skLineSegment(sketch, "E100.37.57", {"start": v(5.75, -8.65) * mm, "end": v(5.76, -8.65) * mm});
            skLineSegment(sketch, "E100.37.58", {"start": v(5.49, -8.99) * mm, "end": v(5.5, -9) * mm});
            skLineSegment(sketch, "E100.37.59", {"start": v(5.88, -8.72) * mm, "end": v(5.9, -8.73) * mm});
            skLineSegment(sketch, "E100.37.60", {"start": v(5.54, -9.16) * mm, "end": v(5.56, -9.2) * mm});
            skLineSegment(sketch, "E100.37.61", {"start": v(6.26, -9.03) * mm, "end": v(6.3, -9.06) * mm});
            skLineSegment(sketch, "E100.37.62", {"start": v(6.07, -8.88) * mm, "end": v(6.1, -8.91) * mm});
            skLineSegment(sketch, "E100.37.63", {"start": v(5.91, -8.74) * mm, "end": v(5.93, -8.75) * mm});
            skLineSegment(sketch, "E100.37.64", {"start": v(5.74, -8.65) * mm, "end": v(5.75, -8.65) * mm});
            skLineSegment(sketch, "E100.37.65", {"start": v(5.55, -8.77) * mm, "end": v(5.53, -8.78) * mm});
            skLineSegment(sketch, "E100.37.66", {"start": v(5.48, -8.97) * mm, "end": v(5.49, -8.99) * mm});
            skLineSegment(sketch, "E100.37.67", {"start": v(5.56, -9.2) * mm, "end": v(5.57, -9.26) * mm});
            skLineSegment(sketch, "E100.37.68", {"start": v(5.47, -8.9) * mm, "end": v(5.47, -8.91) * mm});
            skLineSegment(sketch, "E100.37.69", {"start": v(6, -8.82) * mm, "end": v(6.03, -8.85) * mm});
            skLineSegment(sketch, "E100.37.70", {"start": v(5.5, -8.8) * mm, "end": v(5.49, -8.81) * mm});
            skLineSegment(sketch, "E100.37.71", {"start": v(5.48, -8.94) * mm, "end": v(5.48, -8.96) * mm});
            skLineSegment(sketch, "E100.37.72", {"start": v(5.48, -8.82) * mm, "end": v(5.48, -8.83) * mm});
            skLineSegment(sketch, "E100.37.73", {"start": v(5.96, -8.78) * mm, "end": v(6, -8.82) * mm});
            skLineSegment(sketch, "E100.37.74", {"start": v(5.73, -8.65) * mm, "end": v(5.74, -8.65) * mm});
            skLineSegment(sketch, "E100.37.75", {"start": v(5.72, -8.66) * mm, "end": v(5.73, -8.65) * mm});
            skLineSegment(sketch, "E100.37.76", {"start": v(5.65, -8.7) * mm, "end": v(5.67, -8.69) * mm});
            skLineSegment(sketch, "E100.37.77", {"start": v(5.47, -8.88) * mm, "end": v(5.47, -8.9) * mm});
            skLineSegment(sketch, "E100.37.78", {"start": v(5.83, -8.68) * mm, "end": v(5.84, -8.69) * mm});
            skLineSegment(sketch, "E100.37.79", {"start": v(5.5, -9.03) * mm, "end": v(5.51, -9.07) * mm});
            skLineSegment(sketch, "E100.37.80", {"start": v(5.48, -8.83) * mm, "end": v(5.48, -8.84) * mm});
            skLineSegment(sketch, "E100.37.81", {"start": v(5.71, -8.66) * mm, "end": v(5.72, -8.66) * mm});
            skLineSegment(sketch, "E100.37.82", {"start": v(5.5, -9) * mm, "end": v(5.5, -9.03) * mm});
            skLineSegment(sketch, "E100.37.83", {"start": v(5.63, -8.72) * mm, "end": v(5.65, -8.7) * mm});
            skLineSegment(sketch, "E100.37.84", {"start": v(5.86, -8.7) * mm, "end": v(5.87, -8.7) * mm});
            skLineSegment(sketch, "E100.37.85", {"start": v(5.47, -8.86) * mm, "end": v(5.47, -8.87) * mm});
            skLineSegment(sketch, "E100.37.86", {"start": v(5.6, -8.73) * mm, "end": v(5.63, -8.72) * mm});
            skLineSegment(sketch, "E100.37.87", {"start": v(5.9, -8.73) * mm, "end": v(5.91, -8.74) * mm});
            skLineSegment(sketch, "E100.37.88", {"start": v(5.7, -8.66) * mm, "end": v(5.71, -8.66) * mm});
            skLineSegment(sketch, "E100.37.89", {"start": v(5.69, -8.68) * mm, "end": v(5.7, -8.66) * mm});
            skLineSegment(sketch, "E100.37.90", {"start": v(5.51, -8.8) * mm, "end": v(5.5, -8.8) * mm});
            skLineSegment(sketch, "E100.37.91", {"start": v(5.49, -8.81) * mm, "end": v(5.48, -8.82) * mm});
            skLineSegment(sketch, "E100.37.92", {"start": v(5.47, -8.85) * mm, "end": v(5.47, -8.86) * mm});
            skLineSegment(sketch, "E100.37.93", {"start": v(5.57, -8.75) * mm, "end": v(5.55, -8.77) * mm});
            skLineSegment(sketch, "E100.37.94", {"start": v(5.67, -8.69) * mm, "end": v(5.69, -8.68) * mm});
            skLineSegment(sketch, "E100.37.95", {"start": v(5.79, -8.66) * mm, "end": v(5.8, -8.66) * mm});
            skLineSegment(sketch, "E100.37.96", {"start": v(5.5, -8.8) * mm, "end": v(5.5, -8.8) * mm});
            skLineSegment(sketch, "E100.37.97", {"start": v(5.78, -8.66) * mm, "end": v(5.79, -8.66) * mm});
            skLineSegment(sketch, "E100.37.98", {"start": v(5.8, -8.66) * mm, "end": v(5.8, -8.67) * mm});
            skLineSegment(sketch, "E100.37.99", {"start": v(5.8, -8.67) * mm, "end": v(5.82, -8.67) * mm});
            skLineSegment(sketch, "E100.38.0", {"start": v(7.01, -9.11) * mm, "end": v(6.98, -9.14) * mm});
            skLineSegment(sketch, "E100.38.1", {"start": v(8.05, -8.21) * mm, "end": v(8.08, -8.19) * mm});
            skLineSegment(sketch, "E100.38.2", {"start": v(7.85, -8.21) * mm, "end": v(7.9, -8.23) * mm});
            skLineSegment(sketch, "E100.38.3", {"start": v(8.1, -8.16) * mm, "end": v(8.13, -8.13) * mm});
            skLineSegment(sketch, "E100.38.4", {"start": v(6.93, -8.65) * mm, "end": v(6.94, -8.7) * mm});
            skLineSegment(sketch, "E100.38.5", {"start": v(6.95, -9.16) * mm, "end": v(6.92, -9.18) * mm});
            skLineSegment(sketch, "E100.38.6", {"start": v(8.02, -8.24) * mm, "end": v(8.05, -8.21) * mm});
            skLineSegment(sketch, "E100.38.7", {"start": v(7, -8.89) * mm, "end": v(7.01, -8.94) * mm});
            skLineSegment(sketch, "E100.38.8", {"start": v(8.08, -8.19) * mm, "end": v(8.1, -8.16) * mm});
            skLineSegment(sketch, "E100.38.9", {"start": v(7.01, -8.94) * mm, "end": v(7.02, -8.99) * mm});
            skLineSegment(sketch, "E100.38.10", {"start": v(6.92, -9.18) * mm, "end": v(6.9, -9.2) * mm});
            skLineSegment(sketch, "E100.38.11", {"start": v(7.02, -8.99) * mm, "end": v(7.03, -9.04) * mm});
            skLineSegment(sketch, "E100.38.12", {"start": v(6.99, -8.84) * mm, "end": v(7, -8.89) * mm});
            skLineSegment(sketch, "E100.38.13", {"start": v(7.95, -8.25) * mm, "end": v(8, -8.27) * mm});
            skLineSegment(sketch, "E100.38.14", {"start": v(7.04, -9.09) * mm, "end": v(7.01, -9.11) * mm});
            skLineSegment(sketch, "E100.38.15", {"start": v(6.94, -8.7) * mm, "end": v(6.96, -8.74) * mm});
            skLineSegment(sketch, "E100.38.16", {"start": v(6.98, -9.14) * mm, "end": v(6.95, -9.16) * mm});
            skLineSegment(sketch, "E100.38.17", {"start": v(8, -8.27) * mm, "end": v(8.02, -8.24) * mm});
            skLineSegment(sketch, "E100.38.18", {"start": v(7.76, -8.17) * mm, "end": v(7.8, -8.2) * mm});
            skLineSegment(sketch, "E100.38.19", {"start": v(6.97, -8.8) * mm, "end": v(6.99, -8.84) * mm});
            skLineSegment(sketch, "E100.38.20", {"start": v(7.03, -9.04) * mm, "end": v(7.04, -9.09) * mm});
            skLineSegment(sketch, "E100.38.21", {"start": v(7.62, -8.11) * mm, "end": v(7.66, -8.13) * mm});
            skLineSegment(sketch, "E100.38.22", {"start": v(7.8, -8.2) * mm, "end": v(7.85, -8.21) * mm});
            skLineSegment(sketch, "E100.38.23", {"start": v(6.96, -8.74) * mm, "end": v(6.97, -8.8) * mm});
            skLineSegment(sketch, "E100.38.24", {"start": v(7.66, -8.13) * mm, "end": v(7.71, -8.15) * mm});
            skLineSegment(sketch, "E100.38.25", {"start": v(7.71, -8.15) * mm, "end": v(7.76, -8.17) * mm});
            skLineSegment(sketch, "E100.38.26", {"start": v(7.9, -8.23) * mm, "end": v(7.95, -8.25) * mm});
            skLineSegment(sketch, "E100.38.27", {"start": v(7.57, -8.09) * mm, "end": v(7.62, -8.11) * mm});
            skLineSegment(sketch, "E100.38.28", {"start": v(7, -7.76) * mm, "end": v(7, -7.76) * mm});
            skLineSegment(sketch, "E100.38.29", {"start": v(7.23, -7.9) * mm, "end": v(7.27, -7.93) * mm});
            skLineSegment(sketch, "E100.38.30", {"start": v(7.35, -7.97) * mm, "end": v(7.4, -8) * mm});
            skLineSegment(sketch, "E100.38.31", {"start": v(6.69, -8.06) * mm, "end": v(6.7, -8.07) * mm});
            skLineSegment(sketch, "E100.38.32", {"start": v(6.91, -8.6) * mm, "end": v(6.93, -8.65) * mm});
            skLineSegment(sketch, "E100.38.33", {"start": v(6.94, -7.75) * mm, "end": v(6.95, -7.75) * mm});
            skLineSegment(sketch, "E100.38.34", {"start": v(6.68, -7.97) * mm, "end": v(6.68, -7.98) * mm});
            skLineSegment(sketch, "E100.38.35", {"start": v(7.02, -7.77) * mm, "end": v(7.04, -7.77) * mm});
            skLineSegment(sketch, "E100.38.36", {"start": v(7.11, -7.82) * mm, "end": v(7.15, -7.85) * mm});
            skLineSegment(sketch, "E100.38.37", {"start": v(6.88, -8.5) * mm, "end": v(6.9, -8.55) * mm});
            skLineSegment(sketch, "E100.38.38", {"start": v(6.77, -8.24) * mm, "end": v(6.8, -8.28) * mm});
            skLineSegment(sketch, "E100.38.39", {"start": v(6.83, -8.37) * mm, "end": v(6.85, -8.41) * mm});
            skLineSegment(sketch, "E100.38.40", {"start": v(6.8, -7.84) * mm, "end": v(6.78, -7.86) * mm});
            skLineSegment(sketch, "E100.38.41", {"start": v(6.78, -7.86) * mm, "end": v(6.76, -7.87) * mm});
            skLineSegment(sketch, "E100.38.42", {"start": v(7.44, -8.02) * mm, "end": v(7.48, -8.05) * mm});
            skLineSegment(sketch, "E100.38.43", {"start": v(7.4, -8) * mm, "end": v(7.44, -8.02) * mm});
            skLineSegment(sketch, "E100.38.44", {"start": v(6.9, -8.55) * mm, "end": v(6.91, -8.6) * mm});
            skLineSegment(sketch, "E100.38.45", {"start": v(6.68, -8) * mm, "end": v(6.68, -8.02) * mm});
            skLineSegment(sketch, "E100.38.46", {"start": v(6.7, -7.92) * mm, "end": v(6.7, -7.93) * mm});
            skLineSegment(sketch, "E100.38.47", {"start": v(6.85, -8.41) * mm, "end": v(6.86, -8.46) * mm});
            skLineSegment(sketch, "E100.38.48", {"start": v(7.53, -8.07) * mm, "end": v(7.57, -8.09) * mm});
            skLineSegment(sketch, "E100.38.49", {"start": v(7.05, -7.78) * mm, "end": v(7.06, -7.79) * mm});
            skLineSegment(sketch, "E100.38.50", {"start": v(6.86, -8.46) * mm, "end": v(6.88, -8.5) * mm});
            skLineSegment(sketch, "E100.38.51", {"start": v(6.75, -8.2) * mm, "end": v(6.77, -8.24) * mm});
            skLineSegment(sketch, "E100.38.52", {"start": v(6.93, -7.75) * mm, "end": v(6.94, -7.75) * mm});
            skLineSegment(sketch, "E100.38.53", {"start": v(7.31, -7.95) * mm, "end": v(7.35, -7.97) * mm});
            skLineSegment(sketch, "E100.38.54", {"start": v(6.7, -8.09) * mm, "end": v(6.7, -8.1) * mm});
            skLineSegment(sketch, "E100.38.55", {"start": v(6.72, -7.9) * mm, "end": v(6.7, -7.92) * mm});
            skLineSegment(sketch, "E100.38.56", {"start": v(6.69, -8.04) * mm, "end": v(6.69, -8.06) * mm});
            skLineSegment(sketch, "E100.38.57", {"start": v(6.92, -7.75) * mm, "end": v(6.93, -7.75) * mm});
            skLineSegment(sketch, "E100.38.58", {"start": v(6.71, -8.12) * mm, "end": v(6.72, -8.13) * mm});
            skLineSegment(sketch, "E100.38.59", {"start": v(7.06, -7.79) * mm, "end": v(7.08, -7.8) * mm});
            skLineSegment(sketch, "E100.38.60", {"start": v(6.8, -8.28) * mm, "end": v(6.81, -8.32) * mm});
            skLineSegment(sketch, "E100.38.61", {"start": v(7.48, -8.05) * mm, "end": v(7.53, -8.07) * mm});
            skLineSegment(sketch, "E100.38.62", {"start": v(7.27, -7.93) * mm, "end": v(7.31, -7.95) * mm});
            skLineSegment(sketch, "E100.38.63", {"start": v(7.1, -7.8) * mm, "end": v(7.11, -7.82) * mm});
            skLineSegment(sketch, "E100.38.64", {"start": v(6.91, -7.75) * mm, "end": v(6.92, -7.75) * mm});
            skLineSegment(sketch, "E100.38.65", {"start": v(6.74, -7.89) * mm, "end": v(6.72, -7.9) * mm});
            skLineSegment(sketch, "E100.38.66", {"start": v(6.7, -8.1) * mm, "end": v(6.71, -8.12) * mm});
            skLineSegment(sketch, "E100.38.67", {"start": v(6.81, -8.32) * mm, "end": v(6.83, -8.37) * mm});
            skLineSegment(sketch, "E100.38.68", {"start": v(6.68, -8.03) * mm, "end": v(6.69, -8.04) * mm});
            skLineSegment(sketch, "E100.38.69", {"start": v(7.19, -7.87) * mm, "end": v(7.23, -7.9) * mm});
            skLineSegment(sketch, "E100.38.70", {"start": v(6.7, -7.94) * mm, "end": v(6.69, -7.94) * mm});
            skLineSegment(sketch, "E100.38.71", {"start": v(6.7, -8.07) * mm, "end": v(6.7, -8.09) * mm});
            skLineSegment(sketch, "E100.38.72", {"start": v(6.68, -7.95) * mm, "end": v(6.68, -7.96) * mm});
            skLineSegment(sketch, "E100.38.73", {"start": v(7.15, -7.85) * mm, "end": v(7.19, -7.87) * mm});
            skLineSegment(sketch, "E100.38.74", {"start": v(6.9, -7.75) * mm, "end": v(6.91, -7.75) * mm});
            skLineSegment(sketch, "E100.38.75", {"start": v(6.9, -7.75) * mm, "end": v(6.9, -7.75) * mm});
            skLineSegment(sketch, "E100.38.76", {"start": v(6.83, -7.81) * mm, "end": v(6.85, -7.8) * mm});
            skLineSegment(sketch, "E100.38.77", {"start": v(6.68, -8.02) * mm, "end": v(6.68, -8.03) * mm});
            skLineSegment(sketch, "E100.38.78", {"start": v(7, -7.76) * mm, "end": v(7.02, -7.77) * mm});
            skLineSegment(sketch, "E100.38.79", {"start": v(6.73, -8.15) * mm, "end": v(6.75, -8.2) * mm});
            skLineSegment(sketch, "E100.38.80", {"start": v(6.68, -7.96) * mm, "end": v(6.68, -7.97) * mm});
            skLineSegment(sketch, "E100.38.81", {"start": v(6.89, -7.76) * mm, "end": v(6.9, -7.75) * mm});
            skLineSegment(sketch, "E100.38.82", {"start": v(6.72, -8.13) * mm, "end": v(6.73, -8.15) * mm});
            skLineSegment(sketch, "E100.38.83", {"start": v(6.81, -7.83) * mm, "end": v(6.83, -7.81) * mm});
            skLineSegment(sketch, "E100.38.84", {"start": v(7.04, -7.77) * mm, "end": v(7.05, -7.78) * mm});
            skLineSegment(sketch, "E100.38.85", {"start": v(6.68, -8) * mm, "end": v(6.68, -8) * mm});
            skLineSegment(sketch, "E100.38.86", {"start": v(6.8, -7.84) * mm, "end": v(6.81, -7.83) * mm});
            skLineSegment(sketch, "E100.38.87", {"start": v(7.08, -7.8) * mm, "end": v(7.1, -7.8) * mm});
            skLineSegment(sketch, "E100.38.88", {"start": v(6.88, -7.76) * mm, "end": v(6.89, -7.76) * mm});
            skLineSegment(sketch, "E100.38.89", {"start": v(6.86, -7.78) * mm, "end": v(6.88, -7.76) * mm});
            skLineSegment(sketch, "E100.38.90", {"start": v(6.7, -7.92) * mm, "end": v(6.7, -7.92) * mm});
            skLineSegment(sketch, "E100.38.91", {"start": v(6.69, -7.94) * mm, "end": v(6.68, -7.95) * mm});
            skLineSegment(sketch, "E100.38.92", {"start": v(6.68, -7.98) * mm, "end": v(6.68, -8) * mm});
            skLineSegment(sketch, "E100.38.93", {"start": v(6.76, -7.87) * mm, "end": v(6.74, -7.89) * mm});
            skLineSegment(sketch, "E100.38.94", {"start": v(6.85, -7.8) * mm, "end": v(6.86, -7.78) * mm});
            skLineSegment(sketch, "E100.38.95", {"start": v(6.96, -7.75) * mm, "end": v(6.97, -7.75) * mm});
            skLineSegment(sketch, "E100.38.96", {"start": v(6.7, -7.93) * mm, "end": v(6.7, -7.94) * mm});
            skLineSegment(sketch, "E100.38.97", {"start": v(6.95, -7.75) * mm, "end": v(6.96, -7.75) * mm});
            skLineSegment(sketch, "E100.38.98", {"start": v(6.97, -7.75) * mm, "end": v(6.98, -7.75) * mm});
            skLineSegment(sketch, "E100.38.99", {"start": v(6.98, -7.75) * mm, "end": v(7, -7.76) * mm});
            skLineSegment(sketch, "E100.39.0", {"start": v(8.24, -8.02) * mm, "end": v(8.21, -8.05) * mm});
            skLineSegment(sketch, "E100.39.1", {"start": v(9.14, -6.98) * mm, "end": v(9.16, -6.95) * mm});
            skLineSegment(sketch, "E100.39.2", {"start": v(8.94, -7.01) * mm, "end": v(8.99, -7.02) * mm});
            skLineSegment(sketch, "E100.39.3", {"start": v(9.18, -6.92) * mm, "end": v(9.2, -6.9) * mm});
            skLineSegment(sketch, "E100.39.4", {"start": v(8.09, -7.57) * mm, "end": v(8.11, -7.62) * mm});
            skLineSegment(sketch, "E100.39.5", {"start": v(8.19, -8.08) * mm, "end": v(8.16, -8.1) * mm});
            skLineSegment(sketch, "E100.39.6", {"start": v(9.11, -7.01) * mm, "end": v(9.14, -6.98) * mm});
            skLineSegment(sketch, "E100.39.7", {"start": v(8.2, -7.8) * mm, "end": v(8.21, -7.85) * mm});
            skLineSegment(sketch, "E100.39.8", {"start": v(9.16, -6.95) * mm, "end": v(9.18, -6.92) * mm});
            skLineSegment(sketch, "E100.39.9", {"start": v(8.21, -7.85) * mm, "end": v(8.23, -7.9) * mm});
            skLineSegment(sketch, "E100.39.10", {"start": v(8.16, -8.1) * mm, "end": v(8.13, -8.13) * mm});
            skLineSegment(sketch, "E100.39.11", {"start": v(8.23, -7.9) * mm, "end": v(8.25, -7.95) * mm});
            skLineSegment(sketch, "E100.39.12", {"start": v(8.17, -7.76) * mm, "end": v(8.2, -7.8) * mm});
            skLineSegment(sketch, "E100.39.13", {"start": v(9.04, -7.03) * mm, "end": v(9.09, -7.04) * mm});
            skLineSegment(sketch, "E100.39.14", {"start": v(8.27, -8) * mm, "end": v(8.24, -8.02) * mm});
            skLineSegment(sketch, "E100.39.15", {"start": v(8.11, -7.62) * mm, "end": v(8.13, -7.66) * mm});
            skLineSegment(sketch, "E100.39.16", {"start": v(8.21, -8.05) * mm, "end": v(8.19, -8.08) * mm});
            skLineSegment(sketch, "E100.39.17", {"start": v(9.09, -7.04) * mm, "end": v(9.11, -7.01) * mm});
            skLineSegment(sketch, "E100.39.18", {"start": v(8.84, -6.99) * mm, "end": v(8.89, -7) * mm});
            skLineSegment(sketch, "E100.39.19", {"start": v(8.15, -7.71) * mm, "end": v(8.17, -7.76) * mm});
            skLineSegment(sketch, "E100.39.20", {"start": v(8.25, -7.95) * mm, "end": v(8.27, -8) * mm});
            skLineSegment(sketch, "E100.39.21", {"start": v(8.7, -6.94) * mm, "end": v(8.74, -6.96) * mm});
            skLineSegment(sketch, "E100.39.22", {"start": v(8.89, -7) * mm, "end": v(8.94, -7.01) * mm});
            skLineSegment(sketch, "E100.39.23", {"start": v(8.13, -7.66) * mm, "end": v(8.15, -7.71) * mm});
            skLineSegment(sketch, "E100.39.24", {"start": v(8.74, -6.96) * mm, "end": v(8.8, -6.97) * mm});
            skLineSegment(sketch, "E100.39.25", {"start": v(8.8, -6.97) * mm, "end": v(8.84, -6.99) * mm});
            skLineSegment(sketch, "E100.39.26", {"start": v(8.99, -7.02) * mm, "end": v(9.04, -7.03) * mm});
            skLineSegment(sketch, "E100.39.27", {"start": v(8.65, -6.93) * mm, "end": v(8.7, -6.94) * mm});
            skLineSegment(sketch, "E100.39.28", {"start": v(8.03, -6.68) * mm, "end": v(8.04, -6.69) * mm});
            skLineSegment(sketch, "E100.39.29", {"start": v(8.28, -6.8) * mm, "end": v(8.32, -6.81) * mm});
            skLineSegment(sketch, "E100.39.30", {"start": v(8.41, -6.85) * mm, "end": v(8.46, -6.86) * mm});
            skLineSegment(sketch, "E100.39.31", {"start": v(7.77, -7.02) * mm, "end": v(7.77, -7.04) * mm});
            skLineSegment(sketch, "E100.39.32", {"start": v(8.07, -7.53) * mm, "end": v(8.09, -7.57) * mm});
            skLineSegment(sketch, "E100.39.33", {"start": v(7.97, -6.68) * mm, "end": v(7.98, -6.68) * mm});
            skLineSegment(sketch, "E100.39.34", {"start": v(7.75, -6.94) * mm, "end": v(7.75, -6.95) * mm});
            skLineSegment(sketch, "E100.39.35", {"start": v(8.06, -6.69) * mm, "end": v(8.07, -6.7) * mm});
            skLineSegment(sketch, "E100.39.36", {"start": v(8.15, -6.73) * mm, "end": v(8.2, -6.75) * mm});
            skLineSegment(sketch, "E100.39.37", {"start": v(8.02, -7.44) * mm, "end": v(8.05, -7.48) * mm});
            skLineSegment(sketch, "E100.39.38", {"start": v(7.87, -7.19) * mm, "end": v(7.9, -7.23) * mm});
            skLineSegment(sketch, "E100.39.39", {"start": v(7.95, -7.31) * mm, "end": v(7.97, -7.35) * mm});
            skLineSegment(sketch, "E100.39.40", {"start": v(7.84, -6.8) * mm, "end": v(7.83, -6.81) * mm});
            skLineSegment(sketch, "E100.39.41", {"start": v(7.83, -6.81) * mm, "end": v(7.81, -6.83) * mm});
            skLineSegment(sketch, "E100.39.42", {"start": v(8.5, -6.88) * mm, "end": v(8.55, -6.9) * mm});
            skLineSegment(sketch, "E100.39.43", {"start": v(8.46, -6.86) * mm, "end": v(8.5, -6.88) * mm});
            skLineSegment(sketch, "E100.39.44", {"start": v(8.05, -7.48) * mm, "end": v(8.07, -7.53) * mm});
            skLineSegment(sketch, "E100.39.45", {"start": v(7.75, -6.97) * mm, "end": v(7.75, -6.98) * mm});
            skLineSegment(sketch, "E100.39.46", {"start": v(7.76, -6.89) * mm, "end": v(7.75, -6.9) * mm});
            skLineSegment(sketch, "E100.39.47", {"start": v(7.97, -7.35) * mm, "end": v(8, -7.4) * mm});
            skLineSegment(sketch, "E100.39.48", {"start": v(8.6, -6.91) * mm, "end": v(8.65, -6.93) * mm});
            skLineSegment(sketch, "E100.39.49", {"start": v(8.09, -6.7) * mm, "end": v(8.1, -6.7) * mm});
            skLineSegment(sketch, "E100.39.50", {"start": v(8, -7.4) * mm, "end": v(8.02, -7.44) * mm});
            skLineSegment(sketch, "E100.39.51", {"start": v(7.85, -7.15) * mm, "end": v(7.87, -7.19) * mm});
            skLineSegment(sketch, "E100.39.52", {"start": v(7.96, -6.68) * mm, "end": v(7.97, -6.68) * mm});
            skLineSegment(sketch, "E100.39.53", {"start": v(8.37, -6.83) * mm, "end": v(8.41, -6.85) * mm});
            skLineSegment(sketch, "E100.39.54", {"start": v(7.78, -7.05) * mm, "end": v(7.79, -7.06) * mm});
            skLineSegment(sketch, "E100.39.55", {"start": v(7.78, -6.86) * mm, "end": v(7.76, -6.88) * mm});
            skLineSegment(sketch, "E100.39.56", {"start": v(7.76, -7) * mm, "end": v(7.77, -7.02) * mm});
            skLineSegment(sketch, "E100.39.57", {"start": v(7.95, -6.68) * mm, "end": v(7.96, -6.68) * mm});
            skLineSegment(sketch, "E100.39.58", {"start": v(7.8, -7.08) * mm, "end": v(7.8, -7.1) * mm});
            skLineSegment(sketch, "E100.39.59", {"start": v(8.1, -6.7) * mm, "end": v(8.12, -6.71) * mm});
            skLineSegment(sketch, "E100.39.60", {"start": v(7.9, -7.23) * mm, "end": v(7.93, -7.27) * mm});
            skLineSegment(sketch, "E100.39.61", {"start": v(8.55, -6.9) * mm, "end": v(8.6, -6.91) * mm});
            skLineSegment(sketch, "E100.39.62", {"start": v(8.32, -6.81) * mm, "end": v(8.37, -6.83) * mm});
            skLineSegment(sketch, "E100.39.63", {"start": v(8.13, -6.72) * mm, "end": v(8.15, -6.73) * mm});
            skLineSegment(sketch, "E100.39.64", {"start": v(7.94, -6.69) * mm, "end": v(7.95, -6.68) * mm});
            skLineSegment(sketch, "E100.39.65", {"start": v(7.8, -6.85) * mm, "end": v(7.78, -6.86) * mm});
            skLineSegment(sketch, "E100.39.66", {"start": v(7.79, -7.06) * mm, "end": v(7.8, -7.08) * mm});
            skLineSegment(sketch, "E100.39.67", {"start": v(7.93, -7.27) * mm, "end": v(7.95, -7.31) * mm});
            skLineSegment(sketch, "E100.39.68", {"start": v(7.76, -7) * mm, "end": v(7.76, -7) * mm});
            skLineSegment(sketch, "E100.39.69", {"start": v(8.24, -6.77) * mm, "end": v(8.28, -6.8) * mm});
            skLineSegment(sketch, "E100.39.70", {"start": v(7.75, -6.9) * mm, "end": v(7.75, -6.91) * mm});
            skLineSegment(sketch, "E100.39.71", {"start": v(7.77, -7.04) * mm, "end": v(7.78, -7.05) * mm});
            skLineSegment(sketch, "E100.39.72", {"start": v(7.75, -6.92) * mm, "end": v(7.75, -6.93) * mm});
            skLineSegment(sketch, "E100.39.73", {"start": v(8.2, -6.75) * mm, "end": v(8.24, -6.77) * mm});
            skLineSegment(sketch, "E100.39.74", {"start": v(7.94, -6.7) * mm, "end": v(7.94, -6.69) * mm});
            skLineSegment(sketch, "E100.39.75", {"start": v(7.93, -6.7) * mm, "end": v(7.94, -6.7) * mm});
            skLineSegment(sketch, "E100.39.76", {"start": v(7.87, -6.76) * mm, "end": v(7.89, -6.74) * mm});
            skLineSegment(sketch, "E100.39.77", {"start": v(7.75, -6.98) * mm, "end": v(7.76, -7) * mm});
            skLineSegment(sketch, "E100.39.78", {"start": v(8.04, -6.69) * mm, "end": v(8.06, -6.69) * mm});
            skLineSegment(sketch, "E100.39.79", {"start": v(7.82, -7.11) * mm, "end": v(7.85, -7.15) * mm});
            skLineSegment(sketch, "E100.39.80", {"start": v(7.75, -6.93) * mm, "end": v(7.75, -6.94) * mm});
            skLineSegment(sketch, "E100.39.81", {"start": v(7.92, -6.7) * mm, "end": v(7.93, -6.7) * mm});
            skLineSegment(sketch, "E100.39.82", {"start": v(7.8, -7.1) * mm, "end": v(7.82, -7.11) * mm});
            skLineSegment(sketch, "E100.39.83", {"start": v(7.86, -6.78) * mm, "end": v(7.87, -6.76) * mm});
            skLineSegment(sketch, "E100.39.84", {"start": v(8.07, -6.7) * mm, "end": v(8.09, -6.7) * mm});
            skLineSegment(sketch, "E100.39.85", {"start": v(7.75, -6.96) * mm, "end": v(7.75, -6.97) * mm});
            skLineSegment(sketch, "E100.39.86", {"start": v(7.84, -6.8) * mm, "end": v(7.86, -6.78) * mm});
            skLineSegment(sketch, "E100.39.87", {"start": v(8.12, -6.71) * mm, "end": v(8.13, -6.72) * mm});
            skLineSegment(sketch, "E100.39.88", {"start": v(7.92, -6.7) * mm, "end": v(7.92, -6.7) * mm});
            skLineSegment(sketch, "E100.39.89", {"start": v(7.9, -6.72) * mm, "end": v(7.92, -6.7) * mm});
            skLineSegment(sketch, "E100.39.90", {"start": v(7.76, -6.88) * mm, "end": v(7.76, -6.89) * mm});
            skLineSegment(sketch, "E100.39.91", {"start": v(7.75, -6.91) * mm, "end": v(7.75, -6.92) * mm});
            skLineSegment(sketch, "E100.39.92", {"start": v(7.75, -6.95) * mm, "end": v(7.75, -6.96) * mm});
            skLineSegment(sketch, "E100.39.93", {"start": v(7.81, -6.83) * mm, "end": v(7.8, -6.85) * mm});
            skLineSegment(sketch, "E100.39.94", {"start": v(7.89, -6.74) * mm, "end": v(7.9, -6.72) * mm});
            skLineSegment(sketch, "E100.39.95", {"start": v(8, -6.68) * mm, "end": v(8, -6.68) * mm});
            skLineSegment(sketch, "E100.39.96", {"start": v(7.75, -6.9) * mm, "end": v(7.75, -6.9) * mm});
            skLineSegment(sketch, "E100.39.97", {"start": v(7.98, -6.68) * mm, "end": v(8, -6.68) * mm});
            skLineSegment(sketch, "E100.39.98", {"start": v(8, -6.68) * mm, "end": v(8.02, -6.68) * mm});
            skLineSegment(sketch, "E100.39.99", {"start": v(8.02, -6.68) * mm, "end": v(8.03, -6.68) * mm});
            skLineSegment(sketch, "E100.40.0", {"start": v(9.3, -6.77) * mm, "end": v(9.27, -6.8) * mm});
            skLineSegment(sketch, "E100.40.1", {"start": v(10.04, -5.61) * mm, "end": v(10.06, -5.58) * mm});
            skLineSegment(sketch, "E100.40.2", {"start": v(9.85, -5.67) * mm, "end": v(9.9, -5.67) * mm});
            skLineSegment(sketch, "E100.40.3", {"start": v(10.07, -5.55) * mm, "end": v(10.1, -5.51) * mm});
            skLineSegment(sketch, "E100.40.4", {"start": v(9.08, -6.34) * mm, "end": v(9.11, -6.39) * mm});
            skLineSegment(sketch, "E100.40.5", {"start": v(9.25, -6.83) * mm, "end": v(9.23, -6.86) * mm});
            skLineSegment(sketch, "E100.40.6", {"start": v(10.02, -5.65) * mm, "end": v(10.04, -5.61) * mm});
            skLineSegment(sketch, "E100.40.7", {"start": v(9.22, -6.56) * mm, "end": v(9.24, -6.6) * mm});
            skLineSegment(sketch, "E100.40.8", {"start": v(10.06, -5.58) * mm, "end": v(10.07, -5.55) * mm});
            skLineSegment(sketch, "E100.40.9", {"start": v(9.24, -6.6) * mm, "end": v(9.27, -6.65) * mm});
            skLineSegment(sketch, "E100.40.10", {"start": v(9.23, -6.86) * mm, "end": v(9.2, -6.9) * mm});
            skLineSegment(sketch, "E100.40.11", {"start": v(9.27, -6.65) * mm, "end": v(9.3, -6.7) * mm});
            skLineSegment(sketch, "E100.40.12", {"start": v(9.2, -6.51) * mm, "end": v(9.22, -6.56) * mm});
            skLineSegment(sketch, "E100.40.13", {"start": v(9.95, -5.68) * mm, "end": v(10, -5.68) * mm});
            skLineSegment(sketch, "E100.40.14", {"start": v(9.32, -6.74) * mm, "end": v(9.3, -6.77) * mm});
            skLineSegment(sketch, "E100.40.15", {"start": v(9.11, -6.39) * mm, "end": v(9.14, -6.43) * mm});
            skLineSegment(sketch, "E100.40.16", {"start": v(9.27, -6.8) * mm, "end": v(9.25, -6.83) * mm});
            skLineSegment(sketch, "E100.40.17", {"start": v(10, -5.68) * mm, "end": v(10.02, -5.65) * mm});
            skLineSegment(sketch, "E100.40.18", {"start": v(9.74, -5.66) * mm, "end": v(9.8, -5.66) * mm});
            skLineSegment(sketch, "E100.40.19", {"start": v(9.17, -6.47) * mm, "end": v(9.2, -6.51) * mm});
            skLineSegment(sketch, "E100.40.20", {"start": v(9.3, -6.7) * mm, "end": v(9.32, -6.74) * mm});
            skLineSegment(sketch, "E100.40.21", {"start": v(9.6, -5.64) * mm, "end": v(9.64, -5.64) * mm});
            skLineSegment(sketch, "E100.40.22", {"start": v(9.8, -5.66) * mm, "end": v(9.85, -5.67) * mm});
            skLineSegment(sketch, "E100.40.23", {"start": v(9.14, -6.43) * mm, "end": v(9.17, -6.47) * mm});
            skLineSegment(sketch, "E100.40.24", {"start": v(9.64, -5.64) * mm, "end": v(9.7, -5.65) * mm});
            skLineSegment(sketch, "E100.40.25", {"start": v(9.7, -5.65) * mm, "end": v(9.74, -5.66) * mm});
            skLineSegment(sketch, "E100.40.26", {"start": v(9.9, -5.67) * mm, "end": v(9.95, -5.68) * mm});
            skLineSegment(sketch, "E100.40.27", {"start": v(9.55, -5.63) * mm, "end": v(9.6, -5.64) * mm});
            skLineSegment(sketch, "E100.40.28", {"start": v(8.9, -5.47) * mm, "end": v(8.91, -5.47) * mm});
            skLineSegment(sketch, "E100.40.29", {"start": v(9.16, -5.54) * mm, "end": v(9.2, -5.56) * mm});
            skLineSegment(sketch, "E100.40.30", {"start": v(9.3, -5.58) * mm, "end": v(9.35, -5.6) * mm});
            skLineSegment(sketch, "E100.40.31", {"start": v(8.69, -5.84) * mm, "end": v(8.7, -5.86) * mm});
            skLineSegment(sketch, "E100.40.32", {"start": v(9.06, -6.3) * mm, "end": v(9.08, -6.34) * mm});
            skLineSegment(sketch, "E100.40.33", {"start": v(8.84, -5.48) * mm, "end": v(8.85, -5.47) * mm});
            skLineSegment(sketch, "E100.40.34", {"start": v(8.65, -5.77) * mm, "end": v(8.66, -5.78) * mm});
            skLineSegment(sketch, "E100.40.35", {"start": v(8.93, -5.47) * mm, "end": v(8.94, -5.48) * mm});
            skLineSegment(sketch, "E100.40.36", {"start": v(9.03, -5.5) * mm, "end": v(9.07, -5.51) * mm});
            skLineSegment(sketch, "E100.40.37", {"start": v(9, -6.22) * mm, "end": v(9.03, -6.26) * mm});
            skLineSegment(sketch, "E100.40.38", {"start": v(8.82, -6) * mm, "end": v(8.85, -6.03) * mm});
            skLineSegment(sketch, "E100.40.39", {"start": v(8.91, -6.1) * mm, "end": v(8.94, -6.14) * mm});
            skLineSegment(sketch, "E100.40.40", {"start": v(8.73, -5.6) * mm, "end": v(8.72, -5.63) * mm});
            skLineSegment(sketch, "E100.40.41", {"start": v(8.72, -5.63) * mm, "end": v(8.7, -5.65) * mm});
            skLineSegment(sketch, "E100.40.42", {"start": v(9.4, -5.6) * mm, "end": v(9.45, -5.61) * mm});
            skLineSegment(sketch, "E100.40.43", {"start": v(9.35, -5.6) * mm, "end": v(9.4, -5.6) * mm});
            skLineSegment(sketch, "E100.40.44", {"start": v(9.03, -6.26) * mm, "end": v(9.06, -6.3) * mm});
            skLineSegment(sketch, "E100.40.45", {"start": v(8.66, -5.8) * mm, "end": v(8.67, -5.8) * mm});
            skLineSegment(sketch, "E100.40.46", {"start": v(8.66, -5.71) * mm, "end": v(8.66, -5.72) * mm});
            skLineSegment(sketch, "E100.40.47", {"start": v(8.94, -6.14) * mm, "end": v(8.97, -6.18) * mm});
            skLineSegment(sketch, "E100.40.48", {"start": v(9.5, -5.62) * mm, "end": v(9.55, -5.63) * mm});
            skLineSegment(sketch, "E100.40.49", {"start": v(8.96, -5.48) * mm, "end": v(8.97, -5.48) * mm});
            skLineSegment(sketch, "E100.40.50", {"start": v(8.97, -6.18) * mm, "end": v(9, -6.22) * mm});
            skLineSegment(sketch, "E100.40.51", {"start": v(8.78, -5.96) * mm, "end": v(8.82, -6) * mm});
            skLineSegment(sketch, "E100.40.52", {"start": v(8.83, -5.48) * mm, "end": v(8.84, -5.48) * mm});
            skLineSegment(sketch, "E100.40.53", {"start": v(9.26, -5.57) * mm, "end": v(9.3, -5.58) * mm});
            skLineSegment(sketch, "E100.40.54", {"start": v(8.7, -5.87) * mm, "end": v(8.72, -5.88) * mm});
            skLineSegment(sketch, "E100.40.55", {"start": v(8.68, -5.69) * mm, "end": v(8.66, -5.7) * mm});
            skLineSegment(sketch, "E100.40.56", {"start": v(8.68, -5.83) * mm, "end": v(8.69, -5.84) * mm});
            skLineSegment(sketch, "E100.40.57", {"start": v(8.82, -5.48) * mm, "end": v(8.83, -5.48) * mm});
            skLineSegment(sketch, "E100.40.58", {"start": v(8.73, -5.9) * mm, "end": v(8.74, -5.91) * mm});
            skLineSegment(sketch, "E100.40.59", {"start": v(8.97, -5.48) * mm, "end": v(8.99, -5.49) * mm});
            skLineSegment(sketch, "E100.40.60", {"start": v(8.85, -6.03) * mm, "end": v(8.88, -6.07) * mm});
            skLineSegment(sketch, "E100.40.61", {"start": v(9.45, -5.61) * mm, "end": v(9.5, -5.62) * mm});
            skLineSegment(sketch, "E100.40.62", {"start": v(9.2, -5.56) * mm, "end": v(9.26, -5.57) * mm});
            skLineSegment(sketch, "E100.40.63", {"start": v(9, -5.5) * mm, "end": v(9.03, -5.5) * mm});
            skLineSegment(sketch, "E100.40.64", {"start": v(8.81, -5.49) * mm, "end": v(8.82, -5.48) * mm});
            skLineSegment(sketch, "E100.40.65", {"start": v(8.69, -5.67) * mm, "end": v(8.68, -5.69) * mm});
            skLineSegment(sketch, "E100.40.66", {"start": v(8.72, -5.88) * mm, "end": v(8.73, -5.9) * mm});
            skLineSegment(sketch, "E100.40.67", {"start": v(8.88, -6.07) * mm, "end": v(8.91, -6.1) * mm});
            skLineSegment(sketch, "E100.40.68", {"start": v(8.67, -5.82) * mm, "end": v(8.68, -5.83) * mm});
            skLineSegment(sketch, "E100.40.69", {"start": v(9.12, -5.53) * mm, "end": v(9.16, -5.54) * mm});
            skLineSegment(sketch, "E100.40.70", {"start": v(8.65, -5.73) * mm, "end": v(8.65, -5.74) * mm});
            skLineSegment(sketch, "E100.40.71", {"start": v(8.7, -5.86) * mm, "end": v(8.7, -5.87) * mm});
            skLineSegment(sketch, "E100.40.72", {"start": v(8.65, -5.75) * mm, "end": v(8.65, -5.76) * mm});
            skLineSegment(sketch, "E100.40.73", {"start": v(9.07, -5.51) * mm, "end": v(9.12, -5.53) * mm});
            skLineSegment(sketch, "E100.40.74", {"start": v(8.8, -5.5) * mm, "end": v(8.81, -5.49) * mm});
            skLineSegment(sketch, "E100.40.75", {"start": v(8.8, -5.5) * mm, "end": v(8.8, -5.5) * mm});
            skLineSegment(sketch, "E100.40.76", {"start": v(8.75, -5.57) * mm, "end": v(8.77, -5.55) * mm});
            skLineSegment(sketch, "E100.40.77", {"start": v(8.67, -5.8) * mm, "end": v(8.67, -5.82) * mm});
            skLineSegment(sketch, "E100.40.78", {"start": v(8.91, -5.47) * mm, "end": v(8.93, -5.47) * mm});
            skLineSegment(sketch, "E100.40.79", {"start": v(8.75, -5.93) * mm, "end": v(8.78, -5.96) * mm});
            skLineSegment(sketch, "E100.40.80", {"start": v(8.65, -5.76) * mm, "end": v(8.65, -5.77) * mm});
            skLineSegment(sketch, "E100.40.81", {"start": v(8.8, -5.5) * mm, "end": v(8.8, -5.5) * mm});
            skLineSegment(sketch, "E100.40.82", {"start": v(8.74, -5.91) * mm, "end": v(8.75, -5.93) * mm});
            skLineSegment(sketch, "E100.40.83", {"start": v(8.74, -5.59) * mm, "end": v(8.75, -5.57) * mm});
            skLineSegment(sketch, "E100.40.84", {"start": v(8.94, -5.48) * mm, "end": v(8.96, -5.48) * mm});
            skLineSegment(sketch, "E100.40.85", {"start": v(8.66, -5.79) * mm, "end": v(8.66, -5.8) * mm});
            skLineSegment(sketch, "E100.40.86", {"start": v(8.73, -5.6) * mm, "end": v(8.74, -5.59) * mm});
            skLineSegment(sketch, "E100.40.87", {"start": v(8.99, -5.49) * mm, "end": v(9, -5.5) * mm});
            skLineSegment(sketch, "E100.40.88", {"start": v(8.8, -5.51) * mm, "end": v(8.8, -5.5) * mm});
            skLineSegment(sketch, "E100.40.89", {"start": v(8.78, -5.53) * mm, "end": v(8.8, -5.51) * mm});
            skLineSegment(sketch, "E100.40.90", {"start": v(8.66, -5.7) * mm, "end": v(8.66, -5.71) * mm});
            skLineSegment(sketch, "E100.40.91", {"start": v(8.65, -5.74) * mm, "end": v(8.65, -5.75) * mm});
            skLineSegment(sketch, "E100.40.92", {"start": v(8.66, -5.78) * mm, "end": v(8.66, -5.79) * mm});
            skLineSegment(sketch, "E100.40.93", {"start": v(8.7, -5.65) * mm, "end": v(8.69, -5.67) * mm});
            skLineSegment(sketch, "E100.40.94", {"start": v(8.77, -5.55) * mm, "end": v(8.78, -5.53) * mm});
            skLineSegment(sketch, "E100.40.95", {"start": v(8.86, -5.47) * mm, "end": v(8.87, -5.47) * mm});
            skLineSegment(sketch, "E100.40.96", {"start": v(8.66, -5.72) * mm, "end": v(8.65, -5.73) * mm});
            skLineSegment(sketch, "E100.40.97", {"start": v(8.85, -5.47) * mm, "end": v(8.86, -5.47) * mm});
            skLineSegment(sketch, "E100.40.98", {"start": v(8.87, -5.47) * mm, "end": v(8.88, -5.47) * mm});
            skLineSegment(sketch, "E100.40.99", {"start": v(8.88, -5.47) * mm, "end": v(8.9, -5.47) * mm});
            skLineSegment(sketch, "E100.41.0", {"start": v(10.17, -5.38) * mm, "end": v(10.15, -5.41) * mm});
            skLineSegment(sketch, "E100.41.1", {"start": v(10.73, -4.13) * mm, "end": v(10.75, -4.1) * mm});
            skLineSegment(sketch, "E100.41.2", {"start": v(10.55, -4.2) * mm, "end": v(10.6, -4.2) * mm});
            skLineSegment(sketch, "E100.41.3", {"start": v(10.76, -4.05) * mm, "end": v(10.77, -4.02) * mm});
            skLineSegment(sketch, "E100.41.4", {"start": v(9.9, -4.99) * mm, "end": v(9.93, -5.02) * mm});
            skLineSegment(sketch, "E100.41.5", {"start": v(10.13, -5.44) * mm, "end": v(10.11, -5.48) * mm});
            skLineSegment(sketch, "E100.41.6", {"start": v(10.72, -4.16) * mm, "end": v(10.73, -4.13) * mm});
            skLineSegment(sketch, "E100.41.7", {"start": v(10.06, -5.18) * mm, "end": v(10.1, -5.22) * mm});
            skLineSegment(sketch, "E100.41.8", {"start": v(10.75, -4.1) * mm, "end": v(10.76, -4.05) * mm});
            skLineSegment(sketch, "E100.41.9", {"start": v(10.1, -5.22) * mm, "end": v(10.12, -5.26) * mm});
            skLineSegment(sketch, "E100.41.10", {"start": v(10.11, -5.48) * mm, "end": v(10.1, -5.51) * mm});
            skLineSegment(sketch, "E100.41.11", {"start": v(10.12, -5.26) * mm, "end": v(10.15, -5.3) * mm});
            skLineSegment(sketch, "E100.41.12", {"start": v(10.03, -5.14) * mm, "end": v(10.06, -5.18) * mm});
            skLineSegment(sketch, "E100.41.13", {"start": v(10.65, -4.2) * mm, "end": v(10.7, -4.2) * mm});
            skLineSegment(sketch, "E100.41.14", {"start": v(10.18, -5.34) * mm, "end": v(10.17, -5.38) * mm});
            skLineSegment(sketch, "E100.41.15", {"start": v(9.93, -5.02) * mm, "end": v(9.96, -5.06) * mm});
            skLineSegment(sketch, "E100.41.16", {"start": v(10.15, -5.41) * mm, "end": v(10.13, -5.44) * mm});
            skLineSegment(sketch, "E100.41.17", {"start": v(10.7, -4.2) * mm, "end": v(10.72, -4.16) * mm});
            skLineSegment(sketch, "E100.41.18", {"start": v(10.45, -4.21) * mm, "end": v(10.5, -4.21) * mm});
            skLineSegment(sketch, "E100.41.19", {"start": v(10, -5.1) * mm, "end": v(10.03, -5.14) * mm});
            skLineSegment(sketch, "E100.41.20", {"start": v(10.15, -5.3) * mm, "end": v(10.18, -5.34) * mm});
            skLineSegment(sketch, "E100.41.21", {"start": v(10.3, -4.21) * mm, "end": v(10.35, -4.21) * mm});
            skLineSegment(sketch, "E100.41.22", {"start": v(10.5, -4.21) * mm, "end": v(10.55, -4.2) * mm});
            skLineSegment(sketch, "E100.41.23", {"start": v(9.96, -5.06) * mm, "end": v(10, -5.1) * mm});
            skLineSegment(sketch, "E100.41.24", {"start": v(10.35, -4.21) * mm, "end": v(10.4, -4.21) * mm});
            skLineSegment(sketch, "E100.41.25", {"start": v(10.4, -4.21) * mm, "end": v(10.45, -4.21) * mm});
            skLineSegment(sketch, "E100.41.26", {"start": v(10.6, -4.2) * mm, "end": v(10.65, -4.2) * mm});
            skLineSegment(sketch, "E100.41.27", {"start": v(10.25, -4.21) * mm, "end": v(10.3, -4.21) * mm});
            skLineSegment(sketch, "E100.41.28", {"start": v(9.59, -4.15) * mm, "end": v(9.6, -4.15) * mm});
            skLineSegment(sketch, "E100.41.29", {"start": v(9.86, -4.18) * mm, "end": v(9.9, -4.19) * mm});
            skLineSegment(sketch, "E100.41.30", {"start": v(10, -4.2) * mm, "end": v(10.05, -4.2) * mm});
            skLineSegment(sketch, "E100.41.31", {"start": v(9.43, -4.55) * mm, "end": v(9.44, -4.56) * mm});
            skLineSegment(sketch, "E100.41.32", {"start": v(9.86, -4.95) * mm, "end": v(9.9, -4.99) * mm});
            skLineSegment(sketch, "E100.41.33", {"start": v(9.53, -4.16) * mm, "end": v(9.54, -4.16) * mm});
            skLineSegment(sketch, "E100.41.34", {"start": v(9.39, -4.48) * mm, "end": v(9.4, -4.48) * mm});
            skLineSegment(sketch, "E100.41.35", {"start": v(9.61, -4.15) * mm, "end": v(9.63, -4.15) * mm});
            skLineSegment(sketch, "E100.41.36", {"start": v(9.72, -4.16) * mm, "end": v(9.76, -4.17) * mm});
            skLineSegment(sketch, "E100.41.37", {"start": v(9.8, -4.88) * mm, "end": v(9.83, -4.91) * mm});
            skLineSegment(sketch, "E100.41.38", {"start": v(9.58, -4.68) * mm, "end": v(9.62, -4.71) * mm});
            skLineSegment(sketch, "E100.41.39", {"start": v(9.69, -4.78) * mm, "end": v(9.72, -4.8) * mm});
            skLineSegment(sketch, "E100.41.40", {"start": v(9.44, -4.3) * mm, "end": v(9.43, -4.33) * mm});
            skLineSegment(sketch, "E100.41.41", {"start": v(9.43, -4.33) * mm, "end": v(9.42, -4.35) * mm});
            skLineSegment(sketch, "E100.41.42", {"start": v(10.1, -4.2) * mm, "end": v(10.15, -4.2) * mm});
            skLineSegment(sketch, "E100.41.43", {"start": v(10.05, -4.2) * mm, "end": v(10.1, -4.2) * mm});
            skLineSegment(sketch, "E100.41.44", {"start": v(9.83, -4.91) * mm, "end": v(9.86, -4.95) * mm});
            skLineSegment(sketch, "E100.41.45", {"start": v(9.4, -4.5) * mm, "end": v(9.4, -4.52) * mm});
            skLineSegment(sketch, "E100.41.46", {"start": v(9.39, -4.42) * mm, "end": v(9.38, -4.43) * mm});
            skLineSegment(sketch, "E100.41.47", {"start": v(9.72, -4.8) * mm, "end": v(9.76, -4.84) * mm});
            skLineSegment(sketch, "E100.41.48", {"start": v(10.2, -4.21) * mm, "end": v(10.25, -4.21) * mm});
            skLineSegment(sketch, "E100.41.49", {"start": v(9.65, -4.15) * mm, "end": v(9.66, -4.15) * mm});
            skLineSegment(sketch, "E100.41.50", {"start": v(9.76, -4.84) * mm, "end": v(9.8, -4.88) * mm});
            skLineSegment(sketch, "E100.41.51", {"start": v(9.54, -4.65) * mm, "end": v(9.58, -4.68) * mm});
            skLineSegment(sketch, "E100.41.52", {"start": v(9.52, -4.17) * mm, "end": v(9.53, -4.16) * mm});
            skLineSegment(sketch, "E100.41.53", {"start": v(9.95, -4.2) * mm, "end": v(10, -4.2) * mm});
            skLineSegment(sketch, "E100.41.54", {"start": v(9.45, -4.57) * mm, "end": v(9.46, -4.58) * mm});
            skLineSegment(sketch, "E100.41.55", {"start": v(9.4, -4.4) * mm, "end": v(9.39, -4.42) * mm});
            skLineSegment(sketch, "E100.41.56", {"start": v(9.42, -4.54) * mm, "end": v(9.43, -4.55) * mm});
            skLineSegment(sketch, "E100.41.57", {"start": v(9.51, -4.17) * mm, "end": v(9.52, -4.17) * mm});
            skLineSegment(sketch, "E100.41.58", {"start": v(9.48, -4.6) * mm, "end": v(9.5, -4.6) * mm});
            skLineSegment(sketch, "E100.41.59", {"start": v(9.66, -4.15) * mm, "end": v(9.68, -4.15) * mm});
            skLineSegment(sketch, "E100.41.60", {"start": v(9.62, -4.71) * mm, "end": v(9.65, -4.74) * mm});
            skLineSegment(sketch, "E100.41.61", {"start": v(10.15, -4.2) * mm, "end": v(10.2, -4.21) * mm});
            skLineSegment(sketch, "E100.41.62", {"start": v(9.9, -4.19) * mm, "end": v(9.95, -4.2) * mm});
            skLineSegment(sketch, "E100.41.63", {"start": v(9.7, -4.16) * mm, "end": v(9.72, -4.16) * mm});
            skLineSegment(sketch, "E100.41.64", {"start": v(9.5, -4.18) * mm, "end": v(9.51, -4.17) * mm});
            skLineSegment(sketch, "E100.41.65", {"start": v(9.4, -4.37) * mm, "end": v(9.4, -4.4) * mm});
            skLineSegment(sketch, "E100.41.66", {"start": v(9.46, -4.58) * mm, "end": v(9.48, -4.6) * mm});
            skLineSegment(sketch, "E100.41.67", {"start": v(9.65, -4.74) * mm, "end": v(9.69, -4.78) * mm});
            skLineSegment(sketch, "E100.41.68", {"start": v(9.41, -4.53) * mm, "end": v(9.42, -4.54) * mm});
            skLineSegment(sketch, "E100.41.69", {"start": v(9.81, -4.18) * mm, "end": v(9.86, -4.18) * mm});
            skLineSegment(sketch, "E100.41.70", {"start": v(9.38, -4.44) * mm, "end": v(9.38, -4.45) * mm});
            skLineSegment(sketch, "E100.41.71", {"start": v(9.44, -4.56) * mm, "end": v(9.45, -4.57) * mm});
            skLineSegment(sketch, "E100.41.72", {"start": v(9.38, -4.46) * mm, "end": v(9.38, -4.47) * mm});
            skLineSegment(sketch, "E100.41.73", {"start": v(9.76, -4.17) * mm, "end": v(9.81, -4.18) * mm});
            skLineSegment(sketch, "E100.41.74", {"start": v(9.5, -4.18) * mm, "end": v(9.5, -4.18) * mm});
            skLineSegment(sketch, "E100.41.75", {"start": v(9.5, -4.19) * mm, "end": v(9.5, -4.18) * mm});
            skLineSegment(sketch, "E100.41.76", {"start": v(9.46, -4.27) * mm, "end": v(9.47, -4.25) * mm});
            skLineSegment(sketch, "E100.41.77", {"start": v(9.4, -4.52) * mm, "end": v(9.41, -4.53) * mm});
            skLineSegment(sketch, "E100.41.78", {"start": v(9.6, -4.15) * mm, "end": v(9.61, -4.15) * mm});
            skLineSegment(sketch, "E100.41.79", {"start": v(9.5, -4.62) * mm, "end": v(9.54, -4.65) * mm});
            skLineSegment(sketch, "E100.41.80", {"start": v(9.38, -4.47) * mm, "end": v(9.39, -4.48) * mm});
            skLineSegment(sketch, "E100.41.81", {"start": v(9.49, -4.2) * mm, "end": v(9.5, -4.19) * mm});
            skLineSegment(sketch, "E100.41.82", {"start": v(9.5, -4.6) * mm, "end": v(9.5, -4.62) * mm});
            skLineSegment(sketch, "E100.41.83", {"start": v(9.45, -4.29) * mm, "end": v(9.46, -4.27) * mm});
            skLineSegment(sketch, "E100.41.84", {"start": v(9.63, -4.15) * mm, "end": v(9.65, -4.15) * mm});
            skLineSegment(sketch, "E100.41.85", {"start": v(9.4, -4.5) * mm, "end": v(9.4, -4.5) * mm});
            skLineSegment(sketch, "E100.41.86", {"start": v(9.44, -4.3) * mm, "end": v(9.45, -4.29) * mm});
            skLineSegment(sketch, "E100.41.87", {"start": v(9.68, -4.15) * mm, "end": v(9.7, -4.16) * mm});
            skLineSegment(sketch, "E100.41.88", {"start": v(9.49, -4.2) * mm, "end": v(9.49, -4.2) * mm});
            skLineSegment(sketch, "E100.41.89", {"start": v(9.48, -4.22) * mm, "end": v(9.49, -4.2) * mm});
            skLineSegment(sketch, "E100.41.90", {"start": v(9.39, -4.42) * mm, "end": v(9.39, -4.42) * mm});
            skLineSegment(sketch, "E100.41.91", {"start": v(9.38, -4.45) * mm, "end": v(9.38, -4.46) * mm});
            skLineSegment(sketch, "E100.41.92", {"start": v(9.4, -4.48) * mm, "end": v(9.4, -4.5) * mm});
            skLineSegment(sketch, "E100.41.93", {"start": v(9.42, -4.35) * mm, "end": v(9.4, -4.37) * mm});
            skLineSegment(sketch, "E100.41.94", {"start": v(9.47, -4.25) * mm, "end": v(9.48, -4.22) * mm});
            skLineSegment(sketch, "E100.41.95", {"start": v(9.55, -4.16) * mm, "end": v(9.56, -4.15) * mm});
            skLineSegment(sketch, "E100.41.96", {"start": v(9.38, -4.43) * mm, "end": v(9.38, -4.44) * mm});
            skLineSegment(sketch, "E100.41.97", {"start": v(9.54, -4.16) * mm, "end": v(9.55, -4.16) * mm});
            skLineSegment(sketch, "E100.41.98", {"start": v(9.56, -4.15) * mm, "end": v(9.57, -4.15) * mm});
            skLineSegment(sketch, "E100.41.99", {"start": v(9.57, -4.15) * mm, "end": v(9.59, -4.15) * mm});
            skLineSegment(sketch, "E100.42.0", {"start": v(10.83, -3.87) * mm, "end": v(10.81, -3.91) * mm});
            skLineSegment(sketch, "E100.42.1", {"start": v(11.21, -2.56) * mm, "end": v(11.22, -2.52) * mm});
            skLineSegment(sketch, "E100.42.2", {"start": v(11.04, -2.66) * mm, "end": v(11.1, -2.65) * mm});
            skLineSegment(sketch, "E100.42.3", {"start": v(11.23, -2.48) * mm, "end": v(11.24, -2.44) * mm});
            skLineSegment(sketch, "E100.42.4", {"start": v(10.5, -3.53) * mm, "end": v(10.54, -3.56) * mm});
            skLineSegment(sketch, "E100.42.5", {"start": v(10.8, -3.95) * mm, "end": v(10.79, -3.98) * mm});
            skLineSegment(sketch, "E100.42.6", {"start": v(11.2, -2.6) * mm, "end": v(11.21, -2.56) * mm});
            skLineSegment(sketch, "E100.42.7", {"start": v(10.7, -3.7) * mm, "end": v(10.73, -3.73) * mm});
            skLineSegment(sketch, "E100.42.8", {"start": v(11.22, -2.52) * mm, "end": v(11.23, -2.48) * mm});
            skLineSegment(sketch, "E100.42.9", {"start": v(10.73, -3.73) * mm, "end": v(10.77, -3.77) * mm});
            skLineSegment(sketch, "E100.42.10", {"start": v(10.79, -3.98) * mm, "end": v(10.77, -4.02) * mm});
            skLineSegment(sketch, "E100.42.11", {"start": v(10.77, -3.77) * mm, "end": v(10.8, -3.8) * mm});
            skLineSegment(sketch, "E100.42.12", {"start": v(10.66, -3.66) * mm, "end": v(10.7, -3.7) * mm});
            skLineSegment(sketch, "E100.42.13", {"start": v(11.14, -2.64) * mm, "end": v(11.2, -2.63) * mm});
            skLineSegment(sketch, "E100.42.14", {"start": v(10.84, -3.84) * mm, "end": v(10.83, -3.87) * mm});
            skLineSegment(sketch, "E100.42.15", {"start": v(10.54, -3.56) * mm, "end": v(10.58, -3.6) * mm});
            skLineSegment(sketch, "E100.42.16", {"start": v(10.81, -3.91) * mm, "end": v(10.8, -3.95) * mm});
            skLineSegment(sketch, "E100.42.17", {"start": v(11.2, -2.63) * mm, "end": v(11.2, -2.6) * mm});
            skLineSegment(sketch, "E100.42.18", {"start": v(10.94, -2.68) * mm, "end": v(11, -2.67) * mm});
            skLineSegment(sketch, "E100.42.19", {"start": v(10.62, -3.63) * mm, "end": v(10.66, -3.66) * mm});
            skLineSegment(sketch, "E100.42.20", {"start": v(10.8, -3.8) * mm, "end": v(10.84, -3.84) * mm});
            skLineSegment(sketch, "E100.42.21", {"start": v(10.8, -2.7) * mm, "end": v(10.84, -2.7) * mm});
            skLineSegment(sketch, "E100.42.22", {"start": v(11, -2.67) * mm, "end": v(11.04, -2.66) * mm});
            skLineSegment(sketch, "E100.42.23", {"start": v(10.58, -3.6) * mm, "end": v(10.62, -3.63) * mm});
            skLineSegment(sketch, "E100.42.24", {"start": v(10.84, -2.7) * mm, "end": v(10.9, -2.69) * mm});
            skLineSegment(sketch, "E100.42.25", {"start": v(10.9, -2.69) * mm, "end": v(10.94, -2.68) * mm});
            skLineSegment(sketch, "E100.42.26", {"start": v(11.1, -2.65) * mm, "end": v(11.14, -2.64) * mm});
            skLineSegment(sketch, "E100.42.27", {"start": v(10.74, -2.71) * mm, "end": v(10.8, -2.7) * mm});
            skLineSegment(sketch, "E100.42.28", {"start": v(10.08, -2.74) * mm, "end": v(10.1, -2.74) * mm});
            skLineSegment(sketch, "E100.42.29", {"start": v(10.35, -2.74) * mm, "end": v(10.4, -2.74) * mm});
            skLineSegment(sketch, "E100.42.30", {"start": v(10.5, -2.73) * mm, "end": v(10.55, -2.73) * mm});
            skLineSegment(sketch, "E100.42.31", {"start": v(9.98, -3.16) * mm, "end": v(10, -3.17) * mm});
            skLineSegment(sketch, "E100.42.32", {"start": v(10.47, -3.5) * mm, "end": v(10.5, -3.53) * mm});
            skLineSegment(sketch, "E100.42.33", {"start": v(10.02, -2.76) * mm, "end": v(10.03, -2.76) * mm});
            skLineSegment(sketch, "E100.42.34", {"start": v(9.93, -3.1) * mm, "end": v(9.93, -3.1) * mm});
            skLineSegment(sketch, "E100.42.35", {"start": v(10.1, -2.74) * mm, "end": v(10.12, -2.74) * mm});
            skLineSegment(sketch, "E100.42.36", {"start": v(10.2, -2.73) * mm, "end": v(10.26, -2.74) * mm});
            skLineSegment(sketch, "E100.42.37", {"start": v(10.39, -3.44) * mm, "end": v(10.43, -3.47) * mm});
            skLineSegment(sketch, "E100.42.38", {"start": v(10.15, -3.27) * mm, "end": v(10.19, -3.3) * mm});
            skLineSegment(sketch, "E100.42.39", {"start": v(10.27, -3.35) * mm, "end": v(10.3, -3.38) * mm});
            skLineSegment(sketch, "E100.42.40", {"start": v(9.95, -2.92) * mm, "end": v(9.95, -2.95) * mm});
            skLineSegment(sketch, "E100.42.41", {"start": v(9.95, -2.95) * mm, "end": v(9.94, -2.97) * mm});
            skLineSegment(sketch, "E100.42.42", {"start": v(10.6, -2.73) * mm, "end": v(10.65, -2.72) * mm});
            skLineSegment(sketch, "E100.42.43", {"start": v(10.55, -2.73) * mm, "end": v(10.6, -2.73) * mm});
            skLineSegment(sketch, "E100.42.44", {"start": v(10.43, -3.47) * mm, "end": v(10.47, -3.5) * mm});
            skLineSegment(sketch, "E100.42.45", {"start": v(9.95, -3.12) * mm, "end": v(9.95, -3.13) * mm});
            skLineSegment(sketch, "E100.42.46", {"start": v(9.92, -3.04) * mm, "end": v(9.92, -3.05) * mm});
            skLineSegment(sketch, "E100.42.47", {"start": v(10.3, -3.38) * mm, "end": v(10.35, -3.4) * mm});
            skLineSegment(sketch, "E100.42.48", {"start": v(10.7, -2.72) * mm, "end": v(10.74, -2.71) * mm});
            skLineSegment(sketch, "E100.42.49", {"start": v(10.14, -2.73) * mm, "end": v(10.15, -2.73) * mm});
            skLineSegment(sketch, "E100.42.50", {"start": v(10.35, -3.4) * mm, "end": v(10.39, -3.44) * mm});
            skLineSegment(sketch, "E100.42.51", {"start": v(10.1, -3.24) * mm, "end": v(10.15, -3.27) * mm});
            skLineSegment(sketch, "E100.42.52", {"start": v(10.02, -2.77) * mm, "end": v(10.02, -2.76) * mm});
            skLineSegment(sketch, "E100.42.53", {"start": v(10.45, -2.73) * mm, "end": v(10.5, -2.73) * mm});
            skLineSegment(sketch, "E100.42.54", {"start": v(10, -3.18) * mm, "end": v(10.02, -3.2) * mm});
            skLineSegment(sketch, "E100.42.55", {"start": v(9.93, -3.01) * mm, "end": v(9.92, -3.03) * mm});
            skLineSegment(sketch, "E100.42.56", {"start": v(9.97, -3.15) * mm, "end": v(9.98, -3.16) * mm});
            skLineSegment(sketch, "E100.42.57", {"start": v(10, -2.78) * mm, "end": v(10.02, -2.77) * mm});
            skLineSegment(sketch, "E100.42.58", {"start": v(10.03, -3.2) * mm, "end": v(10.05, -3.2) * mm});
            skLineSegment(sketch, "E100.42.59", {"start": v(10.15, -2.73) * mm, "end": v(10.17, -2.73) * mm});
            skLineSegment(sketch, "E100.42.60", {"start": v(10.19, -3.3) * mm, "end": v(10.23, -3.32) * mm});
            skLineSegment(sketch, "E100.42.61", {"start": v(10.65, -2.72) * mm, "end": v(10.7, -2.72) * mm});
            skLineSegment(sketch, "E100.42.62", {"start": v(10.4, -2.74) * mm, "end": v(10.45, -2.73) * mm});
            skLineSegment(sketch, "E100.42.63", {"start": v(10.2, -2.73) * mm, "end": v(10.2, -2.73) * mm});
            skLineSegment(sketch, "E100.42.64", {"start": v(10, -2.78) * mm, "end": v(10, -2.78) * mm});
            skLineSegment(sketch, "E100.42.65", {"start": v(9.93, -3) * mm, "end": v(9.93, -3.01) * mm});
            skLineSegment(sketch, "E100.42.66", {"start": v(10.02, -3.2) * mm, "end": v(10.03, -3.2) * mm});
            skLineSegment(sketch, "E100.42.67", {"start": v(10.23, -3.32) * mm, "end": v(10.27, -3.35) * mm});
            skLineSegment(sketch, "E100.42.68", {"start": v(9.96, -3.14) * mm, "end": v(9.97, -3.15) * mm});
            skLineSegment(sketch, "E100.42.69", {"start": v(10.3, -2.74) * mm, "end": v(10.35, -2.74) * mm});
            skLineSegment(sketch, "E100.42.70", {"start": v(9.92, -3.06) * mm, "end": v(9.92, -3.07) * mm});
            skLineSegment(sketch, "E100.42.71", {"start": v(10, -3.17) * mm, "end": v(10, -3.18) * mm});
            skLineSegment(sketch, "E100.42.72", {"start": v(9.92, -3.08) * mm, "end": v(9.92, -3.08) * mm});
            skLineSegment(sketch, "E100.42.73", {"start": v(10.26, -2.74) * mm, "end": v(10.3, -2.74) * mm});
            skLineSegment(sketch, "E100.42.74", {"start": v(10, -2.79) * mm, "end": v(10, -2.78) * mm});
            skLineSegment(sketch, "E100.42.75", {"start": v(10, -2.8) * mm, "end": v(10, -2.79) * mm});
            skLineSegment(sketch, "E100.42.76", {"start": v(9.97, -2.88) * mm, "end": v(9.97, -2.86) * mm});
            skLineSegment(sketch, "E100.42.77", {"start": v(9.95, -3.13) * mm, "end": v(9.96, -3.14) * mm});
            skLineSegment(sketch, "E100.42.78", {"start": v(10.1, -2.74) * mm, "end": v(10.1, -2.74) * mm});
            skLineSegment(sketch, "E100.42.79", {"start": v(10.07, -3.22) * mm, "end": v(10.1, -3.24) * mm});
            skLineSegment(sketch, "E100.42.80", {"start": v(9.92, -3.08) * mm, "end": v(9.93, -3.1) * mm});
            skLineSegment(sketch, "E100.42.81", {"start": v(9.99, -2.8) * mm, "end": v(10, -2.8) * mm});
            skLineSegment(sketch, "E100.42.82", {"start": v(10.05, -3.2) * mm, "end": v(10.07, -3.22) * mm});
            skLineSegment(sketch, "E100.42.83", {"start": v(9.96, -2.9) * mm, "end": v(9.97, -2.88) * mm});
            skLineSegment(sketch, "E100.42.84", {"start": v(10.12, -2.74) * mm, "end": v(10.14, -2.73) * mm});
            skLineSegment(sketch, "E100.42.85", {"start": v(9.94, -3.11) * mm, "end": v(9.95, -3.12) * mm});
            skLineSegment(sketch, "E100.42.86", {"start": v(9.95, -2.92) * mm, "end": v(9.96, -2.9) * mm});
            skLineSegment(sketch, "E100.42.87", {"start": v(10.17, -2.73) * mm, "end": v(10.2, -2.73) * mm});
            skLineSegment(sketch, "E100.42.88", {"start": v(9.99, -2.81) * mm, "end": v(9.99, -2.8) * mm});
            skLineSegment(sketch, "E100.42.89", {"start": v(9.98, -2.83) * mm, "end": v(9.99, -2.81) * mm});
            skLineSegment(sketch, "E100.42.90", {"start": v(9.92, -3.03) * mm, "end": v(9.92, -3.04) * mm});
            skLineSegment(sketch, "E100.42.91", {"start": v(9.92, -3.07) * mm, "end": v(9.92, -3.08) * mm});
            skLineSegment(sketch, "E100.42.92", {"start": v(9.93, -3.1) * mm, "end": v(9.94, -3.11) * mm});
            skLineSegment(sketch, "E100.42.93", {"start": v(9.94, -2.97) * mm, "end": v(9.93, -3) * mm});
            skLineSegment(sketch, "E100.42.94", {"start": v(9.97, -2.86) * mm, "end": v(9.98, -2.83) * mm});
            skLineSegment(sketch, "E100.42.95", {"start": v(10.04, -2.76) * mm, "end": v(10.05, -2.75) * mm});
            skLineSegment(sketch, "E100.42.96", {"start": v(9.92, -3.05) * mm, "end": v(9.92, -3.06) * mm});
            skLineSegment(sketch, "E100.42.97", {"start": v(10.03, -2.76) * mm, "end": v(10.04, -2.76) * mm});
            skLineSegment(sketch, "E100.42.98", {"start": v(10.05, -2.75) * mm, "end": v(10.07, -2.75) * mm});
            skLineSegment(sketch, "E100.42.99", {"start": v(10.07, -2.75) * mm, "end": v(10.08, -2.74) * mm});
            skLineSegment(sketch, "E100.43.0", {"start": v(11.27, -2.3) * mm, "end": v(11.26, -2.33) * mm});
            skLineSegment(sketch, "E100.43.1", {"start": v(11.46, -0.94) * mm, "end": v(11.46, -0.9) * mm});
            skLineSegment(sketch, "E100.43.2", {"start": v(11.31, -1.06) * mm, "end": v(11.36, -1.05) * mm});
            skLineSegment(sketch, "E100.43.3", {"start": v(11.47, -0.86) * mm, "end": v(11.47, -0.82) * mm});
            skLineSegment(sketch, "E100.43.4", {"start": v(10.9, -2) * mm, "end": v(10.94, -2.02) * mm});
            skLineSegment(sketch, "E100.43.5", {"start": v(11.25, -2.37) * mm, "end": v(11.25, -2.4) * mm});
            skLineSegment(sketch, "E100.43.6", {"start": v(11.46, -0.97) * mm, "end": v(11.46, -0.94) * mm});
            skLineSegment(sketch, "E100.43.7", {"start": v(11.11, -2.14) * mm, "end": v(11.15, -2.17) * mm});
            skLineSegment(sketch, "E100.43.8", {"start": v(11.46, -0.9) * mm, "end": v(11.47, -0.86) * mm});
            skLineSegment(sketch, "E100.43.9", {"start": v(11.15, -2.17) * mm, "end": v(11.2, -2.2) * mm});
            skLineSegment(sketch, "E100.43.10", {"start": v(11.25, -2.4) * mm, "end": v(11.24, -2.44) * mm});
            skLineSegment(sketch, "E100.43.11", {"start": v(11.2, -2.2) * mm, "end": v(11.24, -2.23) * mm});
            skLineSegment(sketch, "E100.43.12", {"start": v(11.07, -2.1) * mm, "end": v(11.11, -2.14) * mm});
            skLineSegment(sketch, "E100.43.13", {"start": v(11.4, -1.03) * mm, "end": v(11.46, -1.01) * mm});
            skLineSegment(sketch, "E100.43.14", {"start": v(11.28, -2.26) * mm, "end": v(11.27, -2.3) * mm});
            skLineSegment(sketch, "E100.43.15", {"start": v(10.94, -2.02) * mm, "end": v(10.98, -2.05) * mm});
            skLineSegment(sketch, "E100.43.16", {"start": v(11.26, -2.33) * mm, "end": v(11.25, -2.37) * mm});
            skLineSegment(sketch, "E100.43.17", {"start": v(11.46, -1.01) * mm, "end": v(11.46, -0.97) * mm});
            skLineSegment(sketch, "E100.43.18", {"start": v(11.21, -1.1) * mm, "end": v(11.26, -1.08) * mm});
            skLineSegment(sketch, "E100.43.19", {"start": v(11.03, -2.08) * mm, "end": v(11.07, -2.1) * mm});
            skLineSegment(sketch, "E100.43.20", {"start": v(11.24, -2.23) * mm, "end": v(11.28, -2.26) * mm});
            skLineSegment(sketch, "E100.43.21", {"start": v(11.07, -1.14) * mm, "end": v(11.12, -1.13) * mm});
            skLineSegment(sketch, "E100.43.22", {"start": v(11.26, -1.08) * mm, "end": v(11.31, -1.06) * mm});
            skLineSegment(sketch, "E100.43.23", {"start": v(10.98, -2.05) * mm, "end": v(11.03, -2.08) * mm});
            skLineSegment(sketch, "E100.43.24", {"start": v(11.12, -1.13) * mm, "end": v(11.17, -1.11) * mm});
            skLineSegment(sketch, "E100.43.25", {"start": v(11.17, -1.11) * mm, "end": v(11.21, -1.1) * mm});
            skLineSegment(sketch, "E100.43.26", {"start": v(11.36, -1.05) * mm, "end": v(11.4, -1.03) * mm});
            skLineSegment(sketch, "E100.43.27", {"start": v(11.02, -1.15) * mm, "end": v(11.07, -1.14) * mm});
            skLineSegment(sketch, "E100.43.28", {"start": v(10.37, -1.28) * mm, "end": v(10.38, -1.28) * mm});
            skLineSegment(sketch, "E100.43.29", {"start": v(10.64, -1.24) * mm, "end": v(10.69, -1.23) * mm});
            skLineSegment(sketch, "E100.43.30", {"start": v(10.78, -1.21) * mm, "end": v(10.83, -1.2) * mm});
            skLineSegment(sketch, "E100.43.31", {"start": v(10.33, -1.7) * mm, "end": v(10.34, -1.72) * mm});
            skLineSegment(sketch, "E100.43.32", {"start": v(10.86, -1.97) * mm, "end": v(10.9, -2) * mm});
            skLineSegment(sketch, "E100.43.33", {"start": v(10.32, -1.31) * mm, "end": v(10.32, -1.3) * mm});
            skLineSegment(sketch, "E100.43.34", {"start": v(10.27, -1.65) * mm, "end": v(10.27, -1.66) * mm});
            skLineSegment(sketch, "E100.43.35", {"start": v(10.4, -1.27) * mm, "end": v(10.4, -1.27) * mm});
            skLineSegment(sketch, "E100.43.36", {"start": v(10.5, -1.25) * mm, "end": v(10.54, -1.25) * mm});
            skLineSegment(sketch, "E100.43.37", {"start": v(10.77, -1.92) * mm, "end": v(10.81, -1.95) * mm});
            skLineSegment(sketch, "E100.43.38", {"start": v(10.51, -1.8) * mm, "end": v(10.55, -1.81) * mm});
            skLineSegment(sketch, "E100.43.39", {"start": v(10.64, -1.85) * mm, "end": v(10.69, -1.88) * mm});
            skLineSegment(sketch, "E100.43.40", {"start": v(10.27, -1.48) * mm, "end": v(10.27, -1.5) * mm});
            skLineSegment(sketch, "E100.43.41", {"start": v(10.27, -1.5) * mm, "end": v(10.26, -1.52) * mm});
            skLineSegment(sketch, "E100.43.42", {"start": v(10.88, -1.2) * mm, "end": v(10.92, -1.18) * mm});
            skLineSegment(sketch, "E100.43.43", {"start": v(10.83, -1.2) * mm, "end": v(10.88, -1.2) * mm});
            skLineSegment(sketch, "E100.43.44", {"start": v(10.81, -1.95) * mm, "end": v(10.86, -1.97) * mm});
            skLineSegment(sketch, "E100.43.45", {"start": v(10.29, -1.67) * mm, "end": v(10.3, -1.68) * mm});
            skLineSegment(sketch, "E100.43.46", {"start": v(10.25, -1.6) * mm, "end": v(10.25, -1.6) * mm});
            skLineSegment(sketch, "E100.43.47", {"start": v(10.69, -1.88) * mm, "end": v(10.73, -1.9) * mm});
            skLineSegment(sketch, "E100.43.48", {"start": v(10.97, -1.17) * mm, "end": v(11.02, -1.15) * mm});
            skLineSegment(sketch, "E100.43.49", {"start": v(10.42, -1.26) * mm, "end": v(10.44, -1.26) * mm});
            skLineSegment(sketch, "E100.43.50", {"start": v(10.73, -1.9) * mm, "end": v(10.77, -1.92) * mm});
            skLineSegment(sketch, "E100.43.51", {"start": v(10.47, -1.77) * mm, "end": v(10.51, -1.8) * mm});
            skLineSegment(sketch, "E100.43.52", {"start": v(10.3, -1.32) * mm, "end": v(10.32, -1.31) * mm});
            skLineSegment(sketch, "E100.43.53", {"start": v(10.73, -1.22) * mm, "end": v(10.78, -1.21) * mm});
            skLineSegment(sketch, "E100.43.54", {"start": v(10.36, -1.72) * mm, "end": v(10.37, -1.73) * mm});
            skLineSegment(sketch, "E100.43.55", {"start": v(10.26, -1.57) * mm, "end": v(10.25, -1.6) * mm});
            skLineSegment(sketch, "E100.43.56", {"start": v(10.32, -1.7) * mm, "end": v(10.33, -1.7) * mm});
            skLineSegment(sketch, "E100.43.57", {"start": v(10.3, -1.32) * mm, "end": v(10.3, -1.32) * mm});
            skLineSegment(sketch, "E100.43.58", {"start": v(10.39, -1.74) * mm, "end": v(10.4, -1.75) * mm});
            skLineSegment(sketch, "E100.43.59", {"start": v(10.44, -1.26) * mm, "end": v(10.46, -1.26) * mm});
            skLineSegment(sketch, "E100.43.60", {"start": v(10.55, -1.81) * mm, "end": v(10.6, -1.83) * mm});
            skLineSegment(sketch, "E100.43.61", {"start": v(10.92, -1.18) * mm, "end": v(10.97, -1.17) * mm});
            skLineSegment(sketch, "E100.43.62", {"start": v(10.69, -1.23) * mm, "end": v(10.73, -1.22) * mm});
            skLineSegment(sketch, "E100.43.63", {"start": v(10.48, -1.26) * mm, "end": v(10.5, -1.25) * mm});
            skLineSegment(sketch, "E100.43.64", {"start": v(10.3, -1.33) * mm, "end": v(10.3, -1.32) * mm});
            skLineSegment(sketch, "E100.43.65", {"start": v(10.26, -1.55) * mm, "end": v(10.26, -1.57) * mm});
            skLineSegment(sketch, "E100.43.66", {"start": v(10.37, -1.73) * mm, "end": v(10.39, -1.74) * mm});
            skLineSegment(sketch, "E100.43.67", {"start": v(10.6, -1.83) * mm, "end": v(10.64, -1.85) * mm});
            skLineSegment(sketch, "E100.43.68", {"start": v(10.3, -1.7) * mm, "end": v(10.32, -1.7) * mm});
            skLineSegment(sketch, "E100.43.69", {"start": v(10.59, -1.24) * mm, "end": v(10.64, -1.24) * mm});
            skLineSegment(sketch, "E100.43.70", {"start": v(10.25, -1.62) * mm, "end": v(10.26, -1.62) * mm});
            skLineSegment(sketch, "E100.43.71", {"start": v(10.34, -1.72) * mm, "end": v(10.36, -1.72) * mm});
            skLineSegment(sketch, "E100.43.72", {"start": v(10.26, -1.63) * mm, "end": v(10.26, -1.64) * mm});
            skLineSegment(sketch, "E100.43.73", {"start": v(10.54, -1.25) * mm, "end": v(10.59, -1.24) * mm});
            skLineSegment(sketch, "E100.43.74", {"start": v(10.3, -1.34) * mm, "end": v(10.3, -1.33) * mm});
            skLineSegment(sketch, "E100.43.75", {"start": v(10.29, -1.35) * mm, "end": v(10.3, -1.34) * mm});
            skLineSegment(sketch, "E100.43.76", {"start": v(10.28, -1.43) * mm, "end": v(10.28, -1.4) * mm});
            skLineSegment(sketch, "E100.43.77", {"start": v(10.3, -1.68) * mm, "end": v(10.3, -1.7) * mm});
            skLineSegment(sketch, "E100.43.78", {"start": v(10.38, -1.28) * mm, "end": v(10.4, -1.27) * mm});
            skLineSegment(sketch, "E100.43.79", {"start": v(10.42, -1.75) * mm, "end": v(10.47, -1.77) * mm});
            skLineSegment(sketch, "E100.43.80", {"start": v(10.26, -1.64) * mm, "end": v(10.27, -1.65) * mm});
            skLineSegment(sketch, "E100.43.81", {"start": v(10.29, -1.35) * mm, "end": v(10.29, -1.35) * mm});
            skLineSegment(sketch, "E100.43.82", {"start": v(10.4, -1.75) * mm, "end": v(10.42, -1.75) * mm});
            skLineSegment(sketch, "E100.43.83", {"start": v(10.27, -1.45) * mm, "end": v(10.28, -1.43) * mm});
            skLineSegment(sketch, "E100.43.84", {"start": v(10.4, -1.27) * mm, "end": v(10.42, -1.26) * mm});
            skLineSegment(sketch, "E100.43.85", {"start": v(10.28, -1.67) * mm, "end": v(10.29, -1.67) * mm});
            skLineSegment(sketch, "E100.43.86", {"start": v(10.27, -1.48) * mm, "end": v(10.27, -1.45) * mm});
            skLineSegment(sketch, "E100.43.87", {"start": v(10.46, -1.26) * mm, "end": v(10.48, -1.26) * mm});
            skLineSegment(sketch, "E100.43.88", {"start": v(10.29, -1.36) * mm, "end": v(10.29, -1.35) * mm});
            skLineSegment(sketch, "E100.43.89", {"start": v(10.28, -1.38) * mm, "end": v(10.29, -1.36) * mm});
            skLineSegment(sketch, "E100.43.90", {"start": v(10.25, -1.6) * mm, "end": v(10.25, -1.6) * mm});
            skLineSegment(sketch, "E100.43.91", {"start": v(10.26, -1.62) * mm, "end": v(10.26, -1.63) * mm});
            skLineSegment(sketch, "E100.43.92", {"start": v(10.27, -1.66) * mm, "end": v(10.28, -1.67) * mm});
            skLineSegment(sketch, "E100.43.93", {"start": v(10.26, -1.52) * mm, "end": v(10.26, -1.55) * mm});
            skLineSegment(sketch, "E100.43.94", {"start": v(10.28, -1.4) * mm, "end": v(10.28, -1.38) * mm});
            skLineSegment(sketch, "E100.43.95", {"start": v(10.33, -1.3) * mm, "end": v(10.34, -1.3) * mm});
            skLineSegment(sketch, "E100.43.96", {"start": v(10.25, -1.6) * mm, "end": v(10.25, -1.62) * mm});
            skLineSegment(sketch, "E100.43.97", {"start": v(10.32, -1.3) * mm, "end": v(10.33, -1.3) * mm});
            skLineSegment(sketch, "E100.43.98", {"start": v(10.34, -1.3) * mm, "end": v(10.35, -1.29) * mm});
            skLineSegment(sketch, "E100.43.99", {"start": v(10.35, -1.29) * mm, "end": v(10.37, -1.28) * mm});
            skPoint(sketch, "E100.center", {"position": v(0, 0) * mm});
            skSolve(sketch);
        }
        {
            var Q0;
            Q0=makeQuery(id+"F0.imprint","IMPRINT",FACE,{"disambiguationData":[TD([[makeQuery(id+"F0.imprint","IMPRINT",EDGE,{"derivedFrom":sQuery(id+"F0.wireOp",EDGE,"E0")}),1.0]])]});
            extrude(context, id + "F1", {"entities" : qUnion([Q0]), "offsetDistance" : 25 * mm, "depth" : 3 * mm});
        }
        {
            var Q0;
            Q0=qCreatedBy(makeId("Top.planeOp"),FACE);
            var sketch = newSketch(context, id + "F2", { "sketchPlane" : qUnion([Q0])});
            skLineSegment(sketch, "E101.bottom", {"start": v(0, 0) * mm, "end": v(10.5, 0) * mm});
            skLineSegment(sketch, "E101.top", {"start": v(0, 1) * mm, "end": v(10.5, 1) * mm});
            skLineSegment(sketch, "E101.left", {"start": v(0, 0) * mm, "end": v(0, 1) * mm});
            skLineSegment(sketch, "E101.right", {"start": v(10.5, 0) * mm, "end": v(10.5, 1) * mm});
            skLineSegment(sketch, "E102.bottom", {"start": v(0, 1) * mm, "end": v(10, 1) * mm});
            skLineSegment(sketch, "E102.top", {"start": v(0, 8.5) * mm, "end": v(10, 8.5) * mm});
            skLineSegment(sketch, "E102.left", {"start": v(0, 1) * mm, "end": v(0, 8.5) * mm});
            skLineSegment(sketch, "E102.right", {"start": v(10, 1) * mm, "end": v(10, 8.5) * mm});
            skLineSegment(sketch, "E103", {"start": v(10, 1) * mm, "end": v(10, 0) * mm});
            skLineSegment(sketch, "E104", {"start": v(3.05, 8.5) * mm, "end": v(3.05, 0) * mm});
            skLineSegment(sketch, "E105", {"start": v(0, 3) * mm, "end": v(3.05, 3) * mm});
            skLineSegment(sketch, "E106", {"start": v(2.7, 3) * mm, "end": v(2.7, 0) * mm});
            skSolve(sketch);
        }
        {
            var Q0;
            {var subQ0=sQuery(id+"F2.wireOp",EDGE,"E102.right");Q0=makeQuery(id+"F2.imprint","IMPRINT",FACE,{"disambiguationData":[TD([[makeQuery(id+"F2.imprint","IMPRINT",EDGE,{"derivedFrom":subQ0}),1.0]])]});}
            var Q1;
            {var subQ0=sQuery(id+"F2.wireOp",EDGE,"E103");Q1=makeQuery(id+"F2.imprint","IMPRINT",FACE,{"disambiguationData":[TD([[makeQuery(id+"F2.imprint","IMPRINT",EDGE,{"derivedFrom":subQ0}),-1.0]])]});}
            var Q2;
            Q2=makeQuery(id+"F2.imprint","IMPRINT",FACE,{"disambiguationData":[TD([[makeQuery(id+"F2.imprint","IMPRINT",EDGE,{"derivedFrom":sQuery(id+"F2.wireOp",EDGE,"E101.top")}),-1.0]])]});
            var Q3;
            {var subQ0=sQuery(id+"F2.wireOp",EDGE,"E104");var subQ1=sQuery(id+"F2.wireOp",EDGE,"E101.bottom");var subQ2=makeQuery(id+"F2.imprint","INTERSECT",VERTEX,{"derivedFrom":[subQ1,subQ0]});Q3=makeQuery(id+"F2.imprint","IMPRINT",FACE,{"disambiguationData":[TD([[makeQuery(id+"F2.imprint","IMPRINT",EDGE,{"disambiguationData":[TD([[subQ2,1.0]])],"derivedFrom":subQ1}),1.0]])]});}
            var Q4;
            {var subQ0=sQuery(id+"F2.wireOp",EDGE,"E106");var subQ1=sQuery(id+"F2.wireOp",EDGE,"E102.bottom");var subQ2=makeQuery(id+"F2.imprint","INTERSECT",VERTEX,{"derivedFrom":[subQ1,subQ0]});Q4=makeQuery(id+"F2.imprint","IMPRINT",FACE,{"disambiguationData":[TD([[makeQuery(id+"F2.imprint","IMPRINT",EDGE,{"disambiguationData":[TD([[subQ2,-1.0]])],"derivedFrom":subQ1}),1.0]])]});}
            var Q5;
            Q5=sQuery(id+"F2.wireOp",EDGE,"E102.left");
            revolve(context, id + "F3", {"operationType" : NewBodyOperationType.ADD, "surfaceOperationType" : NewSurfaceOperationType.NEW, "entities" : qUnion([Q0, Q1, Q2, Q3, Q4]), "axis" : qUnion([Q5]), "revolveType" : RevolveType.FULL});
        }
        {
            var Q0;
            Q0=makeQuery(id+"F3.opRevolve","SWEPT_FACE",FACE,{"disambiguationData":[OSD([sQuery(id+"F2.wireOp",EDGE,"E101.bottom")])]});
            var sketch = newSketch(context, id + "F4", { "sketchPlane" : qUnion([Q0])});
            skCircle(sketch, "E107", {"center": v(0, 0) * mm, "radius": 3.05 * mm});
            skSolve(sketch);
        }
        {
            var Q0;
            Q0=qSketchRegion(id+"F4",true);
            extrude(context, id + "F5", {"entities" : qUnion([Q0]), "operationType" : NewBodyOperationType.REMOVE, "offsetDistance" : 25 * mm, "depth" : 3 * mm});
        }
        {
            var Q0;
            Q0=makeQuery(id+"F3.opRevolve","SWEPT_FACE",FACE,{"disambiguationData":[OSD([sQuery(id+"F2.wireOp",EDGE,"E102.top")])]});
            var sketch = newSketch(context, id + "F6", { "sketchPlane" : qUnion([Q0])});
            skCircle(sketch, "E108", {"center": v(0, 0) * mm, "radius": 4.25 * mm});
            skCircle(sketch, "E109", {"center": v(0, 0) * mm, "radius": 8.25 * mm});
            skLineSegment(sketch, "E110.2.3", {"start": v(2.23, -2.44) * mm, "end": v(3.23, -0.7) * mm});
            skPoint(sketch, "E111", {"position": v(0, 8.25) * mm});
            skPoint(sketch, "E112", {"position": v(0, 8.53) * mm});
            skArc(sketch, "E113", {"start": v(-7.3, -4.37) * mm, "mid": v(-3.86, -6.5) * mm, "end": v(0, -5.33) * mm});
            skFitSpline(sketch, "E114", {"points": [v(-7.3, -4.37) * mm, v(0, 9.45) * mm], "startDerivative": vector(-12.69, 18.6) * mm, "endDerivative": vector(0, 11.09) * mm});
            skFitSpline(sketch, "E115.MirrorCS", {"points": [v(7.3, -4.37) * mm, v(0, 9.45) * mm], "startDerivative": vector(12.69, 18.6) * mm, "endDerivative": vector(0, 11.09) * mm});
            skArc(sketch, "E116.MirrorCS", {"start": v(7.3, -4.37) * mm, "mid": v(3.86, -6.5) * mm, "end": v(0, -5.33) * mm});
            skSolve(sketch);
        }
        {
            var Q0;
            {var subQ0=sQuery(id+"F6.wireOp",EDGE,"E114");var subQ1=sQuery(id+"F6.wireOp",EDGE,"E109");var subQ2=makeQuery(id+"F6.imprint","INTERSECT",VERTEX,{"disambiguationData":[OD(0.0)],"derivedFrom":[subQ1,subQ0]});Q0=makeQuery(id+"F6.imprint","IMPRINT",FACE,{"disambiguationData":[TD([[makeQuery(id+"F6.imprint","IMPRINT",EDGE,{"disambiguationData":[TD([[subQ2,-1.0]])],"derivedFrom":subQ1}),1.0]])]});}
            var Q1;
            {var subQ0=sQuery(id+"F6.wireOp",EDGE,"E113");var subQ1=sQuery(id+"F6.wireOp",EDGE,"E109");var subQ2=makeQuery(id+"F6.imprint","INTERSECT",VERTEX,{"derivedFrom":[subQ1,subQ0]});Q1=makeQuery(id+"F6.imprint","IMPRINT",FACE,{"disambiguationData":[TD([[makeQuery(id+"F6.imprint","IMPRINT",EDGE,{"disambiguationData":[TD([[subQ2,-1.0]])],"derivedFrom":subQ1}),1.0]])]});}
            var Q2;
            {var subQ0=sQuery(id+"F6.wireOp",EDGE,"a6352883-2e23-4508-b3d2-c43ff309d0480.MirrorCS");var subQ1=sQuery(id+"F6.wireOp",EDGE,"E109");var subQ2=makeQuery(id+"F6.imprint","INTERSECT",VERTEX,{"disambiguationData":[OD(0.0)],"derivedFrom":[subQ1,subQ0]});Q2=makeQuery(id+"F6.imprint","IMPRINT",FACE,{"disambiguationData":[TD([[makeQuery(id+"F6.imprint","IMPRINT",EDGE,{"disambiguationData":[TD([[subQ2,1.0]])],"derivedFrom":subQ1}),1.0]])]});}
            extrude(context, id + "F7", {"entities" : qUnion([Q0, Q1, Q2]), "operationType" : NewBodyOperationType.REMOVE, "oppositeDirection" : true, "depth" : 25 * mm, "offsetDistance" : 25 * mm});
        }
    });
